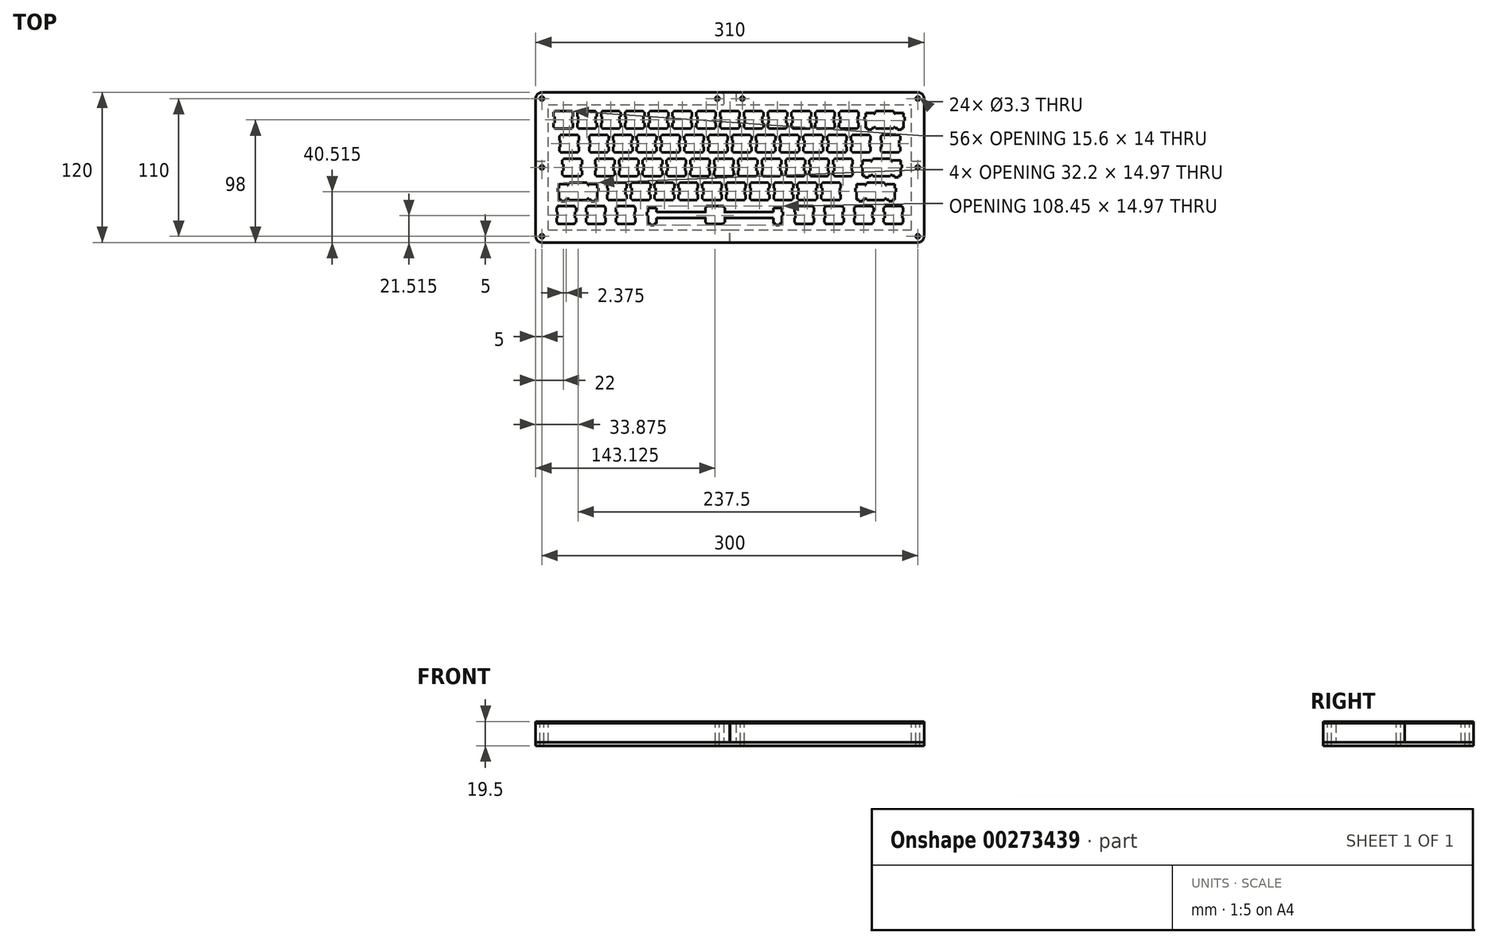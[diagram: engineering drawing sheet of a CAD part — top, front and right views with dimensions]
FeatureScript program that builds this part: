
annotation { "Feature Type Name" : "Feature", "Feature Type Description" : "" }
export const myFeature = defineFeature(function(context is Context, id is Id, definition is map)
    precondition{}
    {
        {
            var Q0;
            Q0=qCreatedBy(makeId("Top.planeOp"),FACE);
            var sketch = newSketch(context, id + "F0", { "sketchPlane" : qUnion([Q0])});
            skLineSegment(sketch, "E0", {"start": v(-145, -50) * mm, "end": v(145, -50) * mm});
            skLineSegment(sketch, "E1", {"start": v(145, -50) * mm, "end": v(145, 50) * mm});
            skLineSegment(sketch, "E2", {"start": v(145, 50) * mm, "end": v(-145, 50) * mm});
            skLineSegment(sketch, "E3", {"start": v(-145, 50) * mm, "end": v(-145, -50) * mm});
            skLineSegment(sketch, "E4", {"start": v(-126, 32) * mm, "end": v(-125.2, 32) * mm});
            skLineSegment(sketch, "E5", {"start": v(-125.2, 32) * mm, "end": v(-125.2, 35.5) * mm});
            skLineSegment(sketch, "E6", {"start": v(-125.2, 35.5) * mm, "end": v(-126, 35.5) * mm});
            skLineSegment(sketch, "E7", {"start": v(-126, 35.5) * mm, "end": v(-126, 40.5) * mm});
            skLineSegment(sketch, "E8", {"start": v(-126, 40.5) * mm, "end": v(-125.2, 40.5) * mm});
            skLineSegment(sketch, "E9", {"start": v(-125.2, 40.5) * mm, "end": v(-125.2, 44) * mm});
            skLineSegment(sketch, "E10", {"start": v(-125.2, 44) * mm, "end": v(-126, 44) * mm});
            skLineSegment(sketch, "E11", {"start": v(-126, 44) * mm, "end": v(-126, 45) * mm});
            skLineSegment(sketch, "E12", {"start": v(-126, 45) * mm, "end": v(-140, 45) * mm});
            skLineSegment(sketch, "E13", {"start": v(-140, 45) * mm, "end": v(-140, 44) * mm});
            skLineSegment(sketch, "E14", {"start": v(-140, 44) * mm, "end": v(-140.8, 44) * mm});
            skLineSegment(sketch, "E15", {"start": v(-140.8, 44) * mm, "end": v(-140.8, 40.5) * mm});
            skLineSegment(sketch, "E16", {"start": v(-140.8, 40.5) * mm, "end": v(-140, 40.5) * mm});
            skLineSegment(sketch, "E17", {"start": v(-140, 40.5) * mm, "end": v(-140, 35.5) * mm});
            skLineSegment(sketch, "E18", {"start": v(-140, 35.5) * mm, "end": v(-140.8, 35.5) * mm});
            skLineSegment(sketch, "E19", {"start": v(-140.8, 35.5) * mm, "end": v(-140.8, 32) * mm});
            skLineSegment(sketch, "E20", {"start": v(-140.8, 32) * mm, "end": v(-140, 32) * mm});
            skLineSegment(sketch, "E21", {"start": v(-140, 32) * mm, "end": v(-140, 31) * mm});
            skLineSegment(sketch, "E22", {"start": v(-140, 31) * mm, "end": v(-126, 31) * mm});
            skLineSegment(sketch, "E23", {"start": v(-126, 31) * mm, "end": v(-126, 32) * mm});
            skLineSegment(sketch, "E24", {"start": v(-107, 32) * mm, "end": v(-106.2, 32) * mm});
            skLineSegment(sketch, "E25", {"start": v(-106.2, 32) * mm, "end": v(-106.2, 35.5) * mm});
            skLineSegment(sketch, "E26", {"start": v(-106.2, 35.5) * mm, "end": v(-107, 35.5) * mm});
            skLineSegment(sketch, "E27", {"start": v(-107, 35.5) * mm, "end": v(-107, 40.5) * mm});
            skLineSegment(sketch, "E28", {"start": v(-107, 40.5) * mm, "end": v(-106.2, 40.5) * mm});
            skLineSegment(sketch, "E29", {"start": v(-106.2, 40.5) * mm, "end": v(-106.2, 44) * mm});
            skLineSegment(sketch, "E30", {"start": v(-106.2, 44) * mm, "end": v(-107, 44) * mm});
            skLineSegment(sketch, "E31", {"start": v(-107, 44) * mm, "end": v(-107, 45) * mm});
            skLineSegment(sketch, "E32", {"start": v(-107, 45) * mm, "end": v(-121, 45) * mm});
            skLineSegment(sketch, "E33", {"start": v(-121, 45) * mm, "end": v(-121, 44) * mm});
            skLineSegment(sketch, "E34", {"start": v(-121, 44) * mm, "end": v(-121.8, 44) * mm});
            skLineSegment(sketch, "E35", {"start": v(-121.8, 44) * mm, "end": v(-121.8, 40.5) * mm});
            skLineSegment(sketch, "E36", {"start": v(-121.8, 40.5) * mm, "end": v(-121, 40.5) * mm});
            skLineSegment(sketch, "E37", {"start": v(-121, 40.5) * mm, "end": v(-121, 35.5) * mm});
            skLineSegment(sketch, "E38", {"start": v(-121, 35.5) * mm, "end": v(-121.8, 35.5) * mm});
            skLineSegment(sketch, "E39", {"start": v(-121.8, 35.5) * mm, "end": v(-121.8, 32) * mm});
            skLineSegment(sketch, "E40", {"start": v(-121.8, 32) * mm, "end": v(-121, 32) * mm});
            skLineSegment(sketch, "E41", {"start": v(-121, 32) * mm, "end": v(-121, 31) * mm});
            skLineSegment(sketch, "E42", {"start": v(-121, 31) * mm, "end": v(-107, 31) * mm});
            skLineSegment(sketch, "E43", {"start": v(-107, 31) * mm, "end": v(-107, 32) * mm});
            skLineSegment(sketch, "E44", {"start": v(-88, 32) * mm, "end": v(-87.2, 32) * mm});
            skLineSegment(sketch, "E45", {"start": v(-87.2, 32) * mm, "end": v(-87.2, 35.5) * mm});
            skLineSegment(sketch, "E46", {"start": v(-87.2, 35.5) * mm, "end": v(-88, 35.5) * mm});
            skLineSegment(sketch, "E47", {"start": v(-88, 35.5) * mm, "end": v(-88, 40.5) * mm});
            skLineSegment(sketch, "E48", {"start": v(-88, 40.5) * mm, "end": v(-87.2, 40.5) * mm});
            skLineSegment(sketch, "E49", {"start": v(-87.2, 40.5) * mm, "end": v(-87.2, 44) * mm});
            skLineSegment(sketch, "E50", {"start": v(-87.2, 44) * mm, "end": v(-88, 44) * mm});
            skLineSegment(sketch, "E51", {"start": v(-88, 44) * mm, "end": v(-88, 45) * mm});
            skLineSegment(sketch, "E52", {"start": v(-88, 45) * mm, "end": v(-102, 45) * mm});
            skLineSegment(sketch, "E53", {"start": v(-102, 45) * mm, "end": v(-102, 44) * mm});
            skLineSegment(sketch, "E54", {"start": v(-102, 44) * mm, "end": v(-102.8, 44) * mm});
            skLineSegment(sketch, "E55", {"start": v(-102.8, 44) * mm, "end": v(-102.8, 40.5) * mm});
            skLineSegment(sketch, "E56", {"start": v(-102.8, 40.5) * mm, "end": v(-102, 40.5) * mm});
            skLineSegment(sketch, "E57", {"start": v(-102, 40.5) * mm, "end": v(-102, 35.5) * mm});
            skLineSegment(sketch, "E58", {"start": v(-102, 35.5) * mm, "end": v(-102.8, 35.5) * mm});
            skLineSegment(sketch, "E59", {"start": v(-102.8, 35.5) * mm, "end": v(-102.8, 32) * mm});
            skLineSegment(sketch, "E60", {"start": v(-102.8, 32) * mm, "end": v(-102, 32) * mm});
            skLineSegment(sketch, "E61", {"start": v(-102, 32) * mm, "end": v(-102, 31) * mm});
            skLineSegment(sketch, "E62", {"start": v(-102, 31) * mm, "end": v(-88, 31) * mm});
            skLineSegment(sketch, "E63", {"start": v(-88, 31) * mm, "end": v(-88, 32) * mm});
            skLineSegment(sketch, "E64", {"start": v(-69, 32) * mm, "end": v(-68.2, 32) * mm});
            skLineSegment(sketch, "E65", {"start": v(-68.2, 32) * mm, "end": v(-68.2, 35.5) * mm});
            skLineSegment(sketch, "E66", {"start": v(-68.2, 35.5) * mm, "end": v(-69, 35.5) * mm});
            skLineSegment(sketch, "E67", {"start": v(-69, 35.5) * mm, "end": v(-69, 40.5) * mm});
            skLineSegment(sketch, "E68", {"start": v(-69, 40.5) * mm, "end": v(-68.2, 40.5) * mm});
            skLineSegment(sketch, "E69", {"start": v(-68.2, 40.5) * mm, "end": v(-68.2, 44) * mm});
            skLineSegment(sketch, "E70", {"start": v(-68.2, 44) * mm, "end": v(-69, 44) * mm});
            skLineSegment(sketch, "E71", {"start": v(-69, 44) * mm, "end": v(-69, 45) * mm});
            skLineSegment(sketch, "E72", {"start": v(-69, 45) * mm, "end": v(-83, 45) * mm});
            skLineSegment(sketch, "E73", {"start": v(-83, 45) * mm, "end": v(-83, 44) * mm});
            skLineSegment(sketch, "E74", {"start": v(-83, 44) * mm, "end": v(-83.8, 44) * mm});
            skLineSegment(sketch, "E75", {"start": v(-83.8, 44) * mm, "end": v(-83.8, 40.5) * mm});
            skLineSegment(sketch, "E76", {"start": v(-83.8, 40.5) * mm, "end": v(-83, 40.5) * mm});
            skLineSegment(sketch, "E77", {"start": v(-83, 40.5) * mm, "end": v(-83, 35.5) * mm});
            skLineSegment(sketch, "E78", {"start": v(-83, 35.5) * mm, "end": v(-83.8, 35.5) * mm});
            skLineSegment(sketch, "E79", {"start": v(-83.8, 35.5) * mm, "end": v(-83.8, 32) * mm});
            skLineSegment(sketch, "E80", {"start": v(-83.8, 32) * mm, "end": v(-83, 32) * mm});
            skLineSegment(sketch, "E81", {"start": v(-83, 32) * mm, "end": v(-83, 31) * mm});
            skLineSegment(sketch, "E82", {"start": v(-83, 31) * mm, "end": v(-69, 31) * mm});
            skLineSegment(sketch, "E83", {"start": v(-69, 31) * mm, "end": v(-69, 32) * mm});
            skLineSegment(sketch, "E84", {"start": v(-50, 32) * mm, "end": v(-49.2, 32) * mm});
            skLineSegment(sketch, "E85", {"start": v(-49.2, 32) * mm, "end": v(-49.2, 35.5) * mm});
            skLineSegment(sketch, "E86", {"start": v(-49.2, 35.5) * mm, "end": v(-50, 35.5) * mm});
            skLineSegment(sketch, "E87", {"start": v(-50, 35.5) * mm, "end": v(-50, 40.5) * mm});
            skLineSegment(sketch, "E88", {"start": v(-50, 40.5) * mm, "end": v(-49.2, 40.5) * mm});
            skLineSegment(sketch, "E89", {"start": v(-49.2, 40.5) * mm, "end": v(-49.2, 44) * mm});
            skLineSegment(sketch, "E90", {"start": v(-49.2, 44) * mm, "end": v(-50, 44) * mm});
            skLineSegment(sketch, "E91", {"start": v(-50, 44) * mm, "end": v(-50, 45) * mm});
            skLineSegment(sketch, "E92", {"start": v(-50, 45) * mm, "end": v(-64, 45) * mm});
            skLineSegment(sketch, "E93", {"start": v(-64, 45) * mm, "end": v(-64, 44) * mm});
            skLineSegment(sketch, "E94", {"start": v(-64, 44) * mm, "end": v(-64.8, 44) * mm});
            skLineSegment(sketch, "E95", {"start": v(-64.8, 44) * mm, "end": v(-64.8, 40.5) * mm});
            skLineSegment(sketch, "E96", {"start": v(-64.8, 40.5) * mm, "end": v(-64, 40.5) * mm});
            skLineSegment(sketch, "E97", {"start": v(-64, 40.5) * mm, "end": v(-64, 35.5) * mm});
            skLineSegment(sketch, "E98", {"start": v(-64, 35.5) * mm, "end": v(-64.8, 35.5) * mm});
            skLineSegment(sketch, "E99", {"start": v(-64.8, 35.5) * mm, "end": v(-64.8, 32) * mm});
            skLineSegment(sketch, "E100", {"start": v(-64.8, 32) * mm, "end": v(-64, 32) * mm});
            skLineSegment(sketch, "E101", {"start": v(-64, 32) * mm, "end": v(-64, 31) * mm});
            skLineSegment(sketch, "E102", {"start": v(-64, 31) * mm, "end": v(-50, 31) * mm});
            skLineSegment(sketch, "E103", {"start": v(-50, 31) * mm, "end": v(-50, 32) * mm});
            skLineSegment(sketch, "E104", {"start": v(-31, 32) * mm, "end": v(-30.2, 32) * mm});
            skLineSegment(sketch, "E105", {"start": v(-30.2, 32) * mm, "end": v(-30.2, 35.5) * mm});
            skLineSegment(sketch, "E106", {"start": v(-30.2, 35.5) * mm, "end": v(-31, 35.5) * mm});
            skLineSegment(sketch, "E107", {"start": v(-31, 35.5) * mm, "end": v(-31, 40.5) * mm});
            skLineSegment(sketch, "E108", {"start": v(-31, 40.5) * mm, "end": v(-30.2, 40.5) * mm});
            skLineSegment(sketch, "E109", {"start": v(-30.2, 40.5) * mm, "end": v(-30.2, 44) * mm});
            skLineSegment(sketch, "E110", {"start": v(-30.2, 44) * mm, "end": v(-31, 44) * mm});
            skLineSegment(sketch, "E111", {"start": v(-31, 44) * mm, "end": v(-31, 45) * mm});
            skLineSegment(sketch, "E112", {"start": v(-31, 45) * mm, "end": v(-45, 45) * mm});
            skLineSegment(sketch, "E113", {"start": v(-45, 45) * mm, "end": v(-45, 44) * mm});
            skLineSegment(sketch, "E114", {"start": v(-45, 44) * mm, "end": v(-45.8, 44) * mm});
            skLineSegment(sketch, "E115", {"start": v(-45.8, 44) * mm, "end": v(-45.8, 40.5) * mm});
            skLineSegment(sketch, "E116", {"start": v(-45.8, 40.5) * mm, "end": v(-45, 40.5) * mm});
            skLineSegment(sketch, "E117", {"start": v(-45, 40.5) * mm, "end": v(-45, 35.5) * mm});
            skLineSegment(sketch, "E118", {"start": v(-45, 35.5) * mm, "end": v(-45.8, 35.5) * mm});
            skLineSegment(sketch, "E119", {"start": v(-45.8, 35.5) * mm, "end": v(-45.8, 32) * mm});
            skLineSegment(sketch, "E120", {"start": v(-45.8, 32) * mm, "end": v(-45, 32) * mm});
            skLineSegment(sketch, "E121", {"start": v(-45, 32) * mm, "end": v(-45, 31) * mm});
            skLineSegment(sketch, "E122", {"start": v(-45, 31) * mm, "end": v(-31, 31) * mm});
            skLineSegment(sketch, "E123", {"start": v(-31, 31) * mm, "end": v(-31, 32) * mm});
            skLineSegment(sketch, "E124", {"start": v(-12, 32) * mm, "end": v(-11.2, 32) * mm});
            skLineSegment(sketch, "E125", {"start": v(-11.2, 32) * mm, "end": v(-11.2, 35.5) * mm});
            skLineSegment(sketch, "E126", {"start": v(-11.2, 35.5) * mm, "end": v(-12, 35.5) * mm});
            skLineSegment(sketch, "E127", {"start": v(-12, 35.5) * mm, "end": v(-12, 40.5) * mm});
            skLineSegment(sketch, "E128", {"start": v(-12, 40.5) * mm, "end": v(-11.2, 40.5) * mm});
            skLineSegment(sketch, "E129", {"start": v(-11.2, 40.5) * mm, "end": v(-11.2, 44) * mm});
            skLineSegment(sketch, "E130", {"start": v(-11.2, 44) * mm, "end": v(-12, 44) * mm});
            skLineSegment(sketch, "E131", {"start": v(-12, 44) * mm, "end": v(-12, 45) * mm});
            skLineSegment(sketch, "E132", {"start": v(-12, 45) * mm, "end": v(-26, 45) * mm});
            skLineSegment(sketch, "E133", {"start": v(-26, 45) * mm, "end": v(-26, 44) * mm});
            skLineSegment(sketch, "E134", {"start": v(-26, 44) * mm, "end": v(-26.8, 44) * mm});
            skLineSegment(sketch, "E135", {"start": v(-26.8, 44) * mm, "end": v(-26.8, 40.5) * mm});
            skLineSegment(sketch, "E136", {"start": v(-26.8, 40.5) * mm, "end": v(-26, 40.5) * mm});
            skLineSegment(sketch, "E137", {"start": v(-26, 40.5) * mm, "end": v(-26, 35.5) * mm});
            skLineSegment(sketch, "E138", {"start": v(-26, 35.5) * mm, "end": v(-26.8, 35.5) * mm});
            skLineSegment(sketch, "E139", {"start": v(-26.8, 35.5) * mm, "end": v(-26.8, 32) * mm});
            skLineSegment(sketch, "E140", {"start": v(-26.8, 32) * mm, "end": v(-26, 32) * mm});
            skLineSegment(sketch, "E141", {"start": v(-26, 32) * mm, "end": v(-26, 31) * mm});
            skLineSegment(sketch, "E142", {"start": v(-26, 31) * mm, "end": v(-12, 31) * mm});
            skLineSegment(sketch, "E143", {"start": v(-12, 31) * mm, "end": v(-12, 32) * mm});
            skLineSegment(sketch, "E144", {"start": v(7, 32) * mm, "end": v(7.8, 32) * mm});
            skLineSegment(sketch, "E145", {"start": v(7.8, 32) * mm, "end": v(7.8, 35.5) * mm});
            skLineSegment(sketch, "E146", {"start": v(7.8, 35.5) * mm, "end": v(7, 35.5) * mm});
            skLineSegment(sketch, "E147", {"start": v(7, 35.5) * mm, "end": v(7, 40.5) * mm});
            skLineSegment(sketch, "E148", {"start": v(7, 40.5) * mm, "end": v(7.8, 40.5) * mm});
            skLineSegment(sketch, "E149", {"start": v(7.8, 40.5) * mm, "end": v(7.8, 44) * mm});
            skLineSegment(sketch, "E150", {"start": v(7.8, 44) * mm, "end": v(7, 44) * mm});
            skLineSegment(sketch, "E151", {"start": v(7, 44) * mm, "end": v(7, 45) * mm});
            skLineSegment(sketch, "E152", {"start": v(7, 45) * mm, "end": v(-7, 45) * mm});
            skLineSegment(sketch, "E153", {"start": v(-7, 45) * mm, "end": v(-7, 44) * mm});
            skLineSegment(sketch, "E154", {"start": v(-7, 44) * mm, "end": v(-7.8, 44) * mm});
            skLineSegment(sketch, "E155", {"start": v(-7.8, 44) * mm, "end": v(-7.8, 40.5) * mm});
            skLineSegment(sketch, "E156", {"start": v(-7.8, 40.5) * mm, "end": v(-7, 40.5) * mm});
            skLineSegment(sketch, "E157", {"start": v(-7, 40.5) * mm, "end": v(-7, 35.5) * mm});
            skLineSegment(sketch, "E158", {"start": v(-7, 35.5) * mm, "end": v(-7.8, 35.5) * mm});
            skLineSegment(sketch, "E159", {"start": v(-7.8, 35.5) * mm, "end": v(-7.8, 32) * mm});
            skLineSegment(sketch, "E160", {"start": v(-7.8, 32) * mm, "end": v(-7, 32) * mm});
            skLineSegment(sketch, "E161", {"start": v(-7, 32) * mm, "end": v(-7, 31) * mm});
            skLineSegment(sketch, "E162", {"start": v(-7, 31) * mm, "end": v(7, 31) * mm});
            skLineSegment(sketch, "E163", {"start": v(7, 31) * mm, "end": v(7, 32) * mm});
            skLineSegment(sketch, "E164", {"start": v(26, 32) * mm, "end": v(26.8, 32) * mm});
            skLineSegment(sketch, "E165", {"start": v(26.8, 32) * mm, "end": v(26.8, 35.5) * mm});
            skLineSegment(sketch, "E166", {"start": v(26.8, 35.5) * mm, "end": v(26, 35.5) * mm});
            skLineSegment(sketch, "E167", {"start": v(26, 35.5) * mm, "end": v(26, 40.5) * mm});
            skLineSegment(sketch, "E168", {"start": v(26, 40.5) * mm, "end": v(26.8, 40.5) * mm});
            skLineSegment(sketch, "E169", {"start": v(26.8, 40.5) * mm, "end": v(26.8, 44) * mm});
            skLineSegment(sketch, "E170", {"start": v(26.8, 44) * mm, "end": v(26, 44) * mm});
            skLineSegment(sketch, "E171", {"start": v(26, 44) * mm, "end": v(26, 45) * mm});
            skLineSegment(sketch, "E172", {"start": v(26, 45) * mm, "end": v(12, 45) * mm});
            skLineSegment(sketch, "E173", {"start": v(12, 45) * mm, "end": v(12, 44) * mm});
            skLineSegment(sketch, "E174", {"start": v(12, 44) * mm, "end": v(11.2, 44) * mm});
            skLineSegment(sketch, "E175", {"start": v(11.2, 44) * mm, "end": v(11.2, 40.5) * mm});
            skLineSegment(sketch, "E176", {"start": v(11.2, 40.5) * mm, "end": v(12, 40.5) * mm});
            skLineSegment(sketch, "E177", {"start": v(12, 40.5) * mm, "end": v(12, 35.5) * mm});
            skLineSegment(sketch, "E178", {"start": v(12, 35.5) * mm, "end": v(11.2, 35.5) * mm});
            skLineSegment(sketch, "E179", {"start": v(11.2, 35.5) * mm, "end": v(11.2, 32) * mm});
            skLineSegment(sketch, "E180", {"start": v(11.2, 32) * mm, "end": v(12, 32) * mm});
            skLineSegment(sketch, "E181", {"start": v(12, 32) * mm, "end": v(12, 31) * mm});
            skLineSegment(sketch, "E182", {"start": v(12, 31) * mm, "end": v(26, 31) * mm});
            skLineSegment(sketch, "E183", {"start": v(26, 31) * mm, "end": v(26, 32) * mm});
            skLineSegment(sketch, "E184", {"start": v(45, 32) * mm, "end": v(45.8, 32) * mm});
            skLineSegment(sketch, "E185", {"start": v(45.8, 32) * mm, "end": v(45.8, 35.5) * mm});
            skLineSegment(sketch, "E186", {"start": v(45.8, 35.5) * mm, "end": v(45, 35.5) * mm});
            skLineSegment(sketch, "E187", {"start": v(45, 35.5) * mm, "end": v(45, 40.5) * mm});
            skLineSegment(sketch, "E188", {"start": v(45, 40.5) * mm, "end": v(45.8, 40.5) * mm});
            skLineSegment(sketch, "E189", {"start": v(45.8, 40.5) * mm, "end": v(45.8, 44) * mm});
            skLineSegment(sketch, "E190", {"start": v(45.8, 44) * mm, "end": v(45, 44) * mm});
            skLineSegment(sketch, "E191", {"start": v(45, 44) * mm, "end": v(45, 45) * mm});
            skLineSegment(sketch, "E192", {"start": v(45, 45) * mm, "end": v(31, 45) * mm});
            skLineSegment(sketch, "E193", {"start": v(31, 45) * mm, "end": v(31, 44) * mm});
            skLineSegment(sketch, "E194", {"start": v(31, 44) * mm, "end": v(30.2, 44) * mm});
            skLineSegment(sketch, "E195", {"start": v(30.2, 44) * mm, "end": v(30.2, 40.5) * mm});
            skLineSegment(sketch, "E196", {"start": v(30.2, 40.5) * mm, "end": v(31, 40.5) * mm});
            skLineSegment(sketch, "E197", {"start": v(31, 40.5) * mm, "end": v(31, 35.5) * mm});
            skLineSegment(sketch, "E198", {"start": v(31, 35.5) * mm, "end": v(30.2, 35.5) * mm});
            skLineSegment(sketch, "E199", {"start": v(30.2, 35.5) * mm, "end": v(30.2, 32) * mm});
            skLineSegment(sketch, "E200", {"start": v(30.2, 32) * mm, "end": v(31, 32) * mm});
            skLineSegment(sketch, "E201", {"start": v(31, 32) * mm, "end": v(31, 31) * mm});
            skLineSegment(sketch, "E202", {"start": v(31, 31) * mm, "end": v(45, 31) * mm});
            skLineSegment(sketch, "E203", {"start": v(45, 31) * mm, "end": v(45, 32) * mm});
            skLineSegment(sketch, "E204", {"start": v(64, 32) * mm, "end": v(64.8, 32) * mm});
            skLineSegment(sketch, "E205", {"start": v(64.8, 32) * mm, "end": v(64.8, 35.5) * mm});
            skLineSegment(sketch, "E206", {"start": v(64.8, 35.5) * mm, "end": v(64, 35.5) * mm});
            skLineSegment(sketch, "E207", {"start": v(64, 35.5) * mm, "end": v(64, 40.5) * mm});
            skLineSegment(sketch, "E208", {"start": v(64, 40.5) * mm, "end": v(64.8, 40.5) * mm});
            skLineSegment(sketch, "E209", {"start": v(64.8, 40.5) * mm, "end": v(64.8, 44) * mm});
            skLineSegment(sketch, "E210", {"start": v(64.8, 44) * mm, "end": v(64, 44) * mm});
            skLineSegment(sketch, "E211", {"start": v(64, 44) * mm, "end": v(64, 45) * mm});
            skLineSegment(sketch, "E212", {"start": v(64, 45) * mm, "end": v(50, 45) * mm});
            skLineSegment(sketch, "E213", {"start": v(50, 45) * mm, "end": v(50, 44) * mm});
            skLineSegment(sketch, "E214", {"start": v(50, 44) * mm, "end": v(49.2, 44) * mm});
            skLineSegment(sketch, "E215", {"start": v(49.2, 44) * mm, "end": v(49.2, 40.5) * mm});
            skLineSegment(sketch, "E216", {"start": v(49.2, 40.5) * mm, "end": v(50, 40.5) * mm});
            skLineSegment(sketch, "E217", {"start": v(50, 40.5) * mm, "end": v(50, 35.5) * mm});
            skLineSegment(sketch, "E218", {"start": v(50, 35.5) * mm, "end": v(49.2, 35.5) * mm});
            skLineSegment(sketch, "E219", {"start": v(49.2, 35.5) * mm, "end": v(49.2, 32) * mm});
            skLineSegment(sketch, "E220", {"start": v(49.2, 32) * mm, "end": v(50, 32) * mm});
            skLineSegment(sketch, "E221", {"start": v(50, 32) * mm, "end": v(50, 31) * mm});
            skLineSegment(sketch, "E222", {"start": v(50, 31) * mm, "end": v(64, 31) * mm});
            skLineSegment(sketch, "E223", {"start": v(64, 31) * mm, "end": v(64, 32) * mm});
            skLineSegment(sketch, "E224", {"start": v(83, 32) * mm, "end": v(83.8, 32) * mm});
            skLineSegment(sketch, "E225", {"start": v(83.8, 32) * mm, "end": v(83.8, 35.5) * mm});
            skLineSegment(sketch, "E226", {"start": v(83.8, 35.5) * mm, "end": v(83, 35.5) * mm});
            skLineSegment(sketch, "E227", {"start": v(83, 35.5) * mm, "end": v(83, 40.5) * mm});
            skLineSegment(sketch, "E228", {"start": v(83, 40.5) * mm, "end": v(83.8, 40.5) * mm});
            skLineSegment(sketch, "E229", {"start": v(83.8, 40.5) * mm, "end": v(83.8, 44) * mm});
            skLineSegment(sketch, "E230", {"start": v(83.8, 44) * mm, "end": v(83, 44) * mm});
            skLineSegment(sketch, "E231", {"start": v(83, 44) * mm, "end": v(83, 45) * mm});
            skLineSegment(sketch, "E232", {"start": v(83, 45) * mm, "end": v(69, 45) * mm});
            skLineSegment(sketch, "E233", {"start": v(69, 45) * mm, "end": v(69, 44) * mm});
            skLineSegment(sketch, "E234", {"start": v(69, 44) * mm, "end": v(68.2, 44) * mm});
            skLineSegment(sketch, "E235", {"start": v(68.2, 44) * mm, "end": v(68.2, 40.5) * mm});
            skLineSegment(sketch, "E236", {"start": v(68.2, 40.5) * mm, "end": v(69, 40.5) * mm});
            skLineSegment(sketch, "E237", {"start": v(69, 40.5) * mm, "end": v(69, 35.5) * mm});
            skLineSegment(sketch, "E238", {"start": v(69, 35.5) * mm, "end": v(68.2, 35.5) * mm});
            skLineSegment(sketch, "E239", {"start": v(68.2, 35.5) * mm, "end": v(68.2, 32) * mm});
            skLineSegment(sketch, "E240", {"start": v(68.2, 32) * mm, "end": v(69, 32) * mm});
            skLineSegment(sketch, "E241", {"start": v(69, 32) * mm, "end": v(69, 31) * mm});
            skLineSegment(sketch, "E242", {"start": v(69, 31) * mm, "end": v(83, 31) * mm});
            skLineSegment(sketch, "E243", {"start": v(83, 31) * mm, "end": v(83, 32) * mm});
            skLineSegment(sketch, "E244", {"start": v(102, 32) * mm, "end": v(102.8, 32) * mm});
            skLineSegment(sketch, "E245", {"start": v(102.8, 32) * mm, "end": v(102.8, 35.5) * mm});
            skLineSegment(sketch, "E246", {"start": v(102.8, 35.5) * mm, "end": v(102, 35.5) * mm});
            skLineSegment(sketch, "E247", {"start": v(102, 35.5) * mm, "end": v(102, 40.5) * mm});
            skLineSegment(sketch, "E248", {"start": v(102, 40.5) * mm, "end": v(102.8, 40.5) * mm});
            skLineSegment(sketch, "E249", {"start": v(102.8, 40.5) * mm, "end": v(102.8, 44) * mm});
            skLineSegment(sketch, "E250", {"start": v(102.8, 44) * mm, "end": v(102, 44) * mm});
            skLineSegment(sketch, "E251", {"start": v(102, 44) * mm, "end": v(102, 45) * mm});
            skLineSegment(sketch, "E252", {"start": v(102, 45) * mm, "end": v(88, 45) * mm});
            skLineSegment(sketch, "E253", {"start": v(88, 45) * mm, "end": v(88, 44) * mm});
            skLineSegment(sketch, "E254", {"start": v(88, 44) * mm, "end": v(87.2, 44) * mm});
            skLineSegment(sketch, "E255", {"start": v(87.2, 44) * mm, "end": v(87.2, 40.5) * mm});
            skLineSegment(sketch, "E256", {"start": v(87.2, 40.5) * mm, "end": v(88, 40.5) * mm});
            skLineSegment(sketch, "E257", {"start": v(88, 40.5) * mm, "end": v(88, 35.5) * mm});
            skLineSegment(sketch, "E258", {"start": v(88, 35.5) * mm, "end": v(87.2, 35.5) * mm});
            skLineSegment(sketch, "E259", {"start": v(87.2, 35.5) * mm, "end": v(87.2, 32) * mm});
            skLineSegment(sketch, "E260", {"start": v(87.2, 32) * mm, "end": v(88, 32) * mm});
            skLineSegment(sketch, "E261", {"start": v(88, 32) * mm, "end": v(88, 31) * mm});
            skLineSegment(sketch, "E262", {"start": v(88, 31) * mm, "end": v(102, 31) * mm});
            skLineSegment(sketch, "E263", {"start": v(102, 31) * mm, "end": v(102, 32) * mm});
            skLineSegment(sketch, "E264", {"start": v(113.1, 31.23) * mm, "end": v(114.93, 31.23) * mm});
            skLineSegment(sketch, "E265", {"start": v(114.93, 31.23) * mm, "end": v(114.93, 32.03) * mm});
            skLineSegment(sketch, "E266", {"start": v(114.93, 32.03) * mm, "end": v(115.7, 32.03) * mm});
            skLineSegment(sketch, "E267", {"start": v(115.7, 32.03) * mm, "end": v(115.7, 32) * mm});
            skLineSegment(sketch, "E268", {"start": v(115.7, 32) * mm, "end": v(116.5, 32) * mm});
            skLineSegment(sketch, "E269", {"start": v(116.5, 32) * mm, "end": v(116.5, 31) * mm});
            skLineSegment(sketch, "E270", {"start": v(116.5, 31) * mm, "end": v(130.5, 31) * mm});
            skLineSegment(sketch, "E271", {"start": v(130.5, 31) * mm, "end": v(130.5, 32) * mm});
            skLineSegment(sketch, "E272", {"start": v(130.5, 32) * mm, "end": v(131.3, 32) * mm});
            skLineSegment(sketch, "E273", {"start": v(131.3, 32) * mm, "end": v(131.3, 32.03) * mm});
            skLineSegment(sketch, "E274", {"start": v(131.3, 32.03) * mm, "end": v(132.07, 32.03) * mm});
            skLineSegment(sketch, "E275", {"start": v(132.07, 32.03) * mm, "end": v(132.07, 31.23) * mm});
            skLineSegment(sketch, "E276", {"start": v(132.07, 31.23) * mm, "end": v(133.9, 31.23) * mm});
            skLineSegment(sketch, "E277", {"start": v(133.9, 31.23) * mm, "end": v(133.9, 30.03) * mm});
            skLineSegment(sketch, "E278", {"start": v(133.9, 30.03) * mm, "end": v(136.9, 30.03) * mm});
            skLineSegment(sketch, "E279", {"start": v(136.9, 30.03) * mm, "end": v(136.9, 31.23) * mm});
            skLineSegment(sketch, "E280", {"start": v(136.9, 31.23) * mm, "end": v(138.73, 31.23) * mm});
            skLineSegment(sketch, "E281", {"start": v(138.73, 31.23) * mm, "end": v(138.73, 37.5) * mm});
            skLineSegment(sketch, "E282", {"start": v(138.73, 37.5) * mm, "end": v(139.6, 37.5) * mm});
            skLineSegment(sketch, "E283", {"start": v(139.6, 37.5) * mm, "end": v(139.6, 40.3) * mm});
            skLineSegment(sketch, "E284", {"start": v(139.6, 40.3) * mm, "end": v(138.73, 40.3) * mm});
            skLineSegment(sketch, "E285", {"start": v(138.73, 40.3) * mm, "end": v(138.73, 43.53) * mm});
            skLineSegment(sketch, "E286", {"start": v(138.73, 43.53) * mm, "end": v(132.07, 43.53) * mm});
            skLineSegment(sketch, "E287", {"start": v(132.07, 43.53) * mm, "end": v(132.07, 42.73) * mm});
            skLineSegment(sketch, "E288", {"start": v(132.07, 42.73) * mm, "end": v(131.3, 42.73) * mm});
            skLineSegment(sketch, "E289", {"start": v(131.3, 42.73) * mm, "end": v(131.3, 44) * mm});
            skLineSegment(sketch, "E290", {"start": v(131.3, 44) * mm, "end": v(130.5, 44) * mm});
            skLineSegment(sketch, "E291", {"start": v(130.5, 44) * mm, "end": v(130.5, 45) * mm});
            skLineSegment(sketch, "E292", {"start": v(130.5, 45) * mm, "end": v(116.5, 45) * mm});
            skLineSegment(sketch, "E293", {"start": v(116.5, 45) * mm, "end": v(116.5, 44) * mm});
            skLineSegment(sketch, "E294", {"start": v(116.5, 44) * mm, "end": v(115.7, 44) * mm});
            skLineSegment(sketch, "E295", {"start": v(115.7, 44) * mm, "end": v(115.7, 42.73) * mm});
            skLineSegment(sketch, "E296", {"start": v(115.7, 42.73) * mm, "end": v(114.93, 42.73) * mm});
            skLineSegment(sketch, "E297", {"start": v(114.93, 42.73) * mm, "end": v(114.93, 43.53) * mm});
            skLineSegment(sketch, "E298", {"start": v(114.93, 43.53) * mm, "end": v(108.28, 43.53) * mm});
            skLineSegment(sketch, "E299", {"start": v(108.28, 43.53) * mm, "end": v(108.28, 40.3) * mm});
            skLineSegment(sketch, "E300", {"start": v(108.28, 40.3) * mm, "end": v(107.4, 40.3) * mm});
            skLineSegment(sketch, "E301", {"start": v(107.4, 40.3) * mm, "end": v(107.4, 37.5) * mm});
            skLineSegment(sketch, "E302", {"start": v(107.4, 37.5) * mm, "end": v(108.28, 37.5) * mm});
            skLineSegment(sketch, "E303", {"start": v(108.28, 37.5) * mm, "end": v(108.28, 31.23) * mm});
            skLineSegment(sketch, "E304", {"start": v(108.28, 31.23) * mm, "end": v(110.1, 31.23) * mm});
            skLineSegment(sketch, "E305", {"start": v(110.1, 31.23) * mm, "end": v(110.1, 30.03) * mm});
            skLineSegment(sketch, "E306", {"start": v(110.1, 30.03) * mm, "end": v(113.1, 30.03) * mm});
            skLineSegment(sketch, "E307", {"start": v(113.1, 30.03) * mm, "end": v(113.1, 31.23) * mm});
            skLineSegment(sketch, "E308", {"start": v(-121.25, 13) * mm, "end": v(-120.45, 13) * mm});
            skLineSegment(sketch, "E309", {"start": v(-120.45, 13) * mm, "end": v(-120.45, 16.5) * mm});
            skLineSegment(sketch, "E310", {"start": v(-120.45, 16.5) * mm, "end": v(-121.25, 16.5) * mm});
            skLineSegment(sketch, "E311", {"start": v(-121.25, 16.5) * mm, "end": v(-121.25, 21.5) * mm});
            skLineSegment(sketch, "E312", {"start": v(-121.25, 21.5) * mm, "end": v(-120.45, 21.5) * mm});
            skLineSegment(sketch, "E313", {"start": v(-120.45, 21.5) * mm, "end": v(-120.45, 25) * mm});
            skLineSegment(sketch, "E314", {"start": v(-120.45, 25) * mm, "end": v(-121.25, 25) * mm});
            skLineSegment(sketch, "E315", {"start": v(-121.25, 25) * mm, "end": v(-121.25, 26) * mm});
            skLineSegment(sketch, "E316", {"start": v(-121.25, 26) * mm, "end": v(-135.25, 26) * mm});
            skLineSegment(sketch, "E317", {"start": v(-135.25, 26) * mm, "end": v(-135.25, 25) * mm});
            skLineSegment(sketch, "E318", {"start": v(-135.25, 25) * mm, "end": v(-136.05, 25) * mm});
            skLineSegment(sketch, "E319", {"start": v(-136.05, 25) * mm, "end": v(-136.05, 21.5) * mm});
            skLineSegment(sketch, "E320", {"start": v(-136.05, 21.5) * mm, "end": v(-135.25, 21.5) * mm});
            skLineSegment(sketch, "E321", {"start": v(-135.25, 21.5) * mm, "end": v(-135.25, 16.5) * mm});
            skLineSegment(sketch, "E322", {"start": v(-135.25, 16.5) * mm, "end": v(-136.05, 16.5) * mm});
            skLineSegment(sketch, "E323", {"start": v(-136.05, 16.5) * mm, "end": v(-136.05, 13) * mm});
            skLineSegment(sketch, "E324", {"start": v(-136.05, 13) * mm, "end": v(-135.25, 13) * mm});
            skLineSegment(sketch, "E325", {"start": v(-135.25, 13) * mm, "end": v(-135.25, 12) * mm});
            skLineSegment(sketch, "E326", {"start": v(-135.25, 12) * mm, "end": v(-121.25, 12) * mm});
            skLineSegment(sketch, "E327", {"start": v(-121.25, 12) * mm, "end": v(-121.25, 13) * mm});
            skLineSegment(sketch, "E328", {"start": v(-97.5, 13) * mm, "end": v(-96.7, 13) * mm});
            skLineSegment(sketch, "E329", {"start": v(-96.7, 13) * mm, "end": v(-96.7, 16.5) * mm});
            skLineSegment(sketch, "E330", {"start": v(-96.7, 16.5) * mm, "end": v(-97.5, 16.5) * mm});
            skLineSegment(sketch, "E331", {"start": v(-97.5, 16.5) * mm, "end": v(-97.5, 21.5) * mm});
            skLineSegment(sketch, "E332", {"start": v(-97.5, 21.5) * mm, "end": v(-96.7, 21.5) * mm});
            skLineSegment(sketch, "E333", {"start": v(-96.7, 21.5) * mm, "end": v(-96.7, 25) * mm});
            skLineSegment(sketch, "E334", {"start": v(-96.7, 25) * mm, "end": v(-97.5, 25) * mm});
            skLineSegment(sketch, "E335", {"start": v(-97.5, 25) * mm, "end": v(-97.5, 26) * mm});
            skLineSegment(sketch, "E336", {"start": v(-97.5, 26) * mm, "end": v(-111.5, 26) * mm});
            skLineSegment(sketch, "E337", {"start": v(-111.5, 26) * mm, "end": v(-111.5, 25) * mm});
            skLineSegment(sketch, "E338", {"start": v(-111.5, 25) * mm, "end": v(-112.3, 25) * mm});
            skLineSegment(sketch, "E339", {"start": v(-112.3, 25) * mm, "end": v(-112.3, 21.5) * mm});
            skLineSegment(sketch, "E340", {"start": v(-112.3, 21.5) * mm, "end": v(-111.5, 21.5) * mm});
            skLineSegment(sketch, "E341", {"start": v(-111.5, 21.5) * mm, "end": v(-111.5, 16.5) * mm});
            skLineSegment(sketch, "E342", {"start": v(-111.5, 16.5) * mm, "end": v(-112.3, 16.5) * mm});
            skLineSegment(sketch, "E343", {"start": v(-112.3, 16.5) * mm, "end": v(-112.3, 13) * mm});
            skLineSegment(sketch, "E344", {"start": v(-112.3, 13) * mm, "end": v(-111.5, 13) * mm});
            skLineSegment(sketch, "E345", {"start": v(-111.5, 13) * mm, "end": v(-111.5, 12) * mm});
            skLineSegment(sketch, "E346", {"start": v(-111.5, 12) * mm, "end": v(-97.5, 12) * mm});
            skLineSegment(sketch, "E347", {"start": v(-97.5, 12) * mm, "end": v(-97.5, 13) * mm});
            skLineSegment(sketch, "E348", {"start": v(-78.5, 13) * mm, "end": v(-77.7, 13) * mm});
            skLineSegment(sketch, "E349", {"start": v(-77.7, 13) * mm, "end": v(-77.7, 16.5) * mm});
            skLineSegment(sketch, "E350", {"start": v(-77.7, 16.5) * mm, "end": v(-78.5, 16.5) * mm});
            skLineSegment(sketch, "E351", {"start": v(-78.5, 16.5) * mm, "end": v(-78.5, 21.5) * mm});
            skLineSegment(sketch, "E352", {"start": v(-78.5, 21.5) * mm, "end": v(-77.7, 21.5) * mm});
            skLineSegment(sketch, "E353", {"start": v(-77.7, 21.5) * mm, "end": v(-77.7, 25) * mm});
            skLineSegment(sketch, "E354", {"start": v(-77.7, 25) * mm, "end": v(-78.5, 25) * mm});
            skLineSegment(sketch, "E355", {"start": v(-78.5, 25) * mm, "end": v(-78.5, 26) * mm});
            skLineSegment(sketch, "E356", {"start": v(-78.5, 26) * mm, "end": v(-92.5, 26) * mm});
            skLineSegment(sketch, "E357", {"start": v(-92.5, 26) * mm, "end": v(-92.5, 25) * mm});
            skLineSegment(sketch, "E358", {"start": v(-92.5, 25) * mm, "end": v(-93.3, 25) * mm});
            skLineSegment(sketch, "E359", {"start": v(-93.3, 25) * mm, "end": v(-93.3, 21.5) * mm});
            skLineSegment(sketch, "E360", {"start": v(-93.3, 21.5) * mm, "end": v(-92.5, 21.5) * mm});
            skLineSegment(sketch, "E361", {"start": v(-92.5, 21.5) * mm, "end": v(-92.5, 16.5) * mm});
            skLineSegment(sketch, "E362", {"start": v(-92.5, 16.5) * mm, "end": v(-93.3, 16.5) * mm});
            skLineSegment(sketch, "E363", {"start": v(-93.3, 16.5) * mm, "end": v(-93.3, 13) * mm});
            skLineSegment(sketch, "E364", {"start": v(-93.3, 13) * mm, "end": v(-92.5, 13) * mm});
            skLineSegment(sketch, "E365", {"start": v(-92.5, 13) * mm, "end": v(-92.5, 12) * mm});
            skLineSegment(sketch, "E366", {"start": v(-92.5, 12) * mm, "end": v(-78.5, 12) * mm});
            skLineSegment(sketch, "E367", {"start": v(-78.5, 12) * mm, "end": v(-78.5, 13) * mm});
            skLineSegment(sketch, "E368", {"start": v(-59.5, 13) * mm, "end": v(-58.7, 13) * mm});
            skLineSegment(sketch, "E369", {"start": v(-58.7, 13) * mm, "end": v(-58.7, 16.5) * mm});
            skLineSegment(sketch, "E370", {"start": v(-58.7, 16.5) * mm, "end": v(-59.5, 16.5) * mm});
            skLineSegment(sketch, "E371", {"start": v(-59.5, 16.5) * mm, "end": v(-59.5, 21.5) * mm});
            skLineSegment(sketch, "E372", {"start": v(-59.5, 21.5) * mm, "end": v(-58.7, 21.5) * mm});
            skLineSegment(sketch, "E373", {"start": v(-58.7, 21.5) * mm, "end": v(-58.7, 25) * mm});
            skLineSegment(sketch, "E374", {"start": v(-58.7, 25) * mm, "end": v(-59.5, 25) * mm});
            skLineSegment(sketch, "E375", {"start": v(-59.5, 25) * mm, "end": v(-59.5, 26) * mm});
            skLineSegment(sketch, "E376", {"start": v(-59.5, 26) * mm, "end": v(-73.5, 26) * mm});
            skLineSegment(sketch, "E377", {"start": v(-73.5, 26) * mm, "end": v(-73.5, 25) * mm});
            skLineSegment(sketch, "E378", {"start": v(-73.5, 25) * mm, "end": v(-74.3, 25) * mm});
            skLineSegment(sketch, "E379", {"start": v(-74.3, 25) * mm, "end": v(-74.3, 21.5) * mm});
            skLineSegment(sketch, "E380", {"start": v(-74.3, 21.5) * mm, "end": v(-73.5, 21.5) * mm});
            skLineSegment(sketch, "E381", {"start": v(-73.5, 21.5) * mm, "end": v(-73.5, 16.5) * mm});
            skLineSegment(sketch, "E382", {"start": v(-73.5, 16.5) * mm, "end": v(-74.3, 16.5) * mm});
            skLineSegment(sketch, "E383", {"start": v(-74.3, 16.5) * mm, "end": v(-74.3, 13) * mm});
            skLineSegment(sketch, "E384", {"start": v(-74.3, 13) * mm, "end": v(-73.5, 13) * mm});
            skLineSegment(sketch, "E385", {"start": v(-73.5, 13) * mm, "end": v(-73.5, 12) * mm});
            skLineSegment(sketch, "E386", {"start": v(-73.5, 12) * mm, "end": v(-59.5, 12) * mm});
            skLineSegment(sketch, "E387", {"start": v(-59.5, 12) * mm, "end": v(-59.5, 13) * mm});
            skLineSegment(sketch, "E388", {"start": v(-40.5, 13) * mm, "end": v(-39.7, 13) * mm});
            skLineSegment(sketch, "E389", {"start": v(-39.7, 13) * mm, "end": v(-39.7, 16.5) * mm});
            skLineSegment(sketch, "E390", {"start": v(-39.7, 16.5) * mm, "end": v(-40.5, 16.5) * mm});
            skLineSegment(sketch, "E391", {"start": v(-40.5, 16.5) * mm, "end": v(-40.5, 21.5) * mm});
            skLineSegment(sketch, "E392", {"start": v(-40.5, 21.5) * mm, "end": v(-39.7, 21.5) * mm});
            skLineSegment(sketch, "E393", {"start": v(-39.7, 21.5) * mm, "end": v(-39.7, 25) * mm});
            skLineSegment(sketch, "E394", {"start": v(-39.7, 25) * mm, "end": v(-40.5, 25) * mm});
            skLineSegment(sketch, "E395", {"start": v(-40.5, 25) * mm, "end": v(-40.5, 26) * mm});
            skLineSegment(sketch, "E396", {"start": v(-40.5, 26) * mm, "end": v(-54.5, 26) * mm});
            skLineSegment(sketch, "E397", {"start": v(-54.5, 26) * mm, "end": v(-54.5, 25) * mm});
            skLineSegment(sketch, "E398", {"start": v(-54.5, 25) * mm, "end": v(-55.3, 25) * mm});
            skLineSegment(sketch, "E399", {"start": v(-55.3, 25) * mm, "end": v(-55.3, 21.5) * mm});
            skLineSegment(sketch, "E400", {"start": v(-55.3, 21.5) * mm, "end": v(-54.5, 21.5) * mm});
            skLineSegment(sketch, "E401", {"start": v(-54.5, 21.5) * mm, "end": v(-54.5, 16.5) * mm});
            skLineSegment(sketch, "E402", {"start": v(-54.5, 16.5) * mm, "end": v(-55.3, 16.5) * mm});
            skLineSegment(sketch, "E403", {"start": v(-55.3, 16.5) * mm, "end": v(-55.3, 13) * mm});
            skLineSegment(sketch, "E404", {"start": v(-55.3, 13) * mm, "end": v(-54.5, 13) * mm});
            skLineSegment(sketch, "E405", {"start": v(-54.5, 13) * mm, "end": v(-54.5, 12) * mm});
            skLineSegment(sketch, "E406", {"start": v(-54.5, 12) * mm, "end": v(-40.5, 12) * mm});
            skLineSegment(sketch, "E407", {"start": v(-40.5, 12) * mm, "end": v(-40.5, 13) * mm});
            skLineSegment(sketch, "E408", {"start": v(-21.5, 13) * mm, "end": v(-20.7, 13) * mm});
            skLineSegment(sketch, "E409", {"start": v(-20.7, 13) * mm, "end": v(-20.7, 16.5) * mm});
            skLineSegment(sketch, "E410", {"start": v(-20.7, 16.5) * mm, "end": v(-21.5, 16.5) * mm});
            skLineSegment(sketch, "E411", {"start": v(-21.5, 16.5) * mm, "end": v(-21.5, 21.5) * mm});
            skLineSegment(sketch, "E412", {"start": v(-21.5, 21.5) * mm, "end": v(-20.7, 21.5) * mm});
            skLineSegment(sketch, "E413", {"start": v(-20.7, 21.5) * mm, "end": v(-20.7, 25) * mm});
            skLineSegment(sketch, "E414", {"start": v(-20.7, 25) * mm, "end": v(-21.5, 25) * mm});
            skLineSegment(sketch, "E415", {"start": v(-21.5, 25) * mm, "end": v(-21.5, 26) * mm});
            skLineSegment(sketch, "E416", {"start": v(-21.5, 26) * mm, "end": v(-35.5, 26) * mm});
            skLineSegment(sketch, "E417", {"start": v(-35.5, 26) * mm, "end": v(-35.5, 25) * mm});
            skLineSegment(sketch, "E418", {"start": v(-35.5, 25) * mm, "end": v(-36.3, 25) * mm});
            skLineSegment(sketch, "E419", {"start": v(-36.3, 25) * mm, "end": v(-36.3, 21.5) * mm});
            skLineSegment(sketch, "E420", {"start": v(-36.3, 21.5) * mm, "end": v(-35.5, 21.5) * mm});
            skLineSegment(sketch, "E421", {"start": v(-35.5, 21.5) * mm, "end": v(-35.5, 16.5) * mm});
            skLineSegment(sketch, "E422", {"start": v(-35.5, 16.5) * mm, "end": v(-36.3, 16.5) * mm});
            skLineSegment(sketch, "E423", {"start": v(-36.3, 16.5) * mm, "end": v(-36.3, 13) * mm});
            skLineSegment(sketch, "E424", {"start": v(-36.3, 13) * mm, "end": v(-35.5, 13) * mm});
            skLineSegment(sketch, "E425", {"start": v(-35.5, 13) * mm, "end": v(-35.5, 12) * mm});
            skLineSegment(sketch, "E426", {"start": v(-35.5, 12) * mm, "end": v(-21.5, 12) * mm});
            skLineSegment(sketch, "E427", {"start": v(-21.5, 12) * mm, "end": v(-21.5, 13) * mm});
            skLineSegment(sketch, "E428", {"start": v(-2.5, 13) * mm, "end": v(-1.7, 13) * mm});
            skLineSegment(sketch, "E429", {"start": v(-1.7, 13) * mm, "end": v(-1.7, 16.5) * mm});
            skLineSegment(sketch, "E430", {"start": v(-1.7, 16.5) * mm, "end": v(-2.5, 16.5) * mm});
            skLineSegment(sketch, "E431", {"start": v(-2.5, 16.5) * mm, "end": v(-2.5, 21.5) * mm});
            skLineSegment(sketch, "E432", {"start": v(-2.5, 21.5) * mm, "end": v(-1.7, 21.5) * mm});
            skLineSegment(sketch, "E433", {"start": v(-1.7, 21.5) * mm, "end": v(-1.7, 25) * mm});
            skLineSegment(sketch, "E434", {"start": v(-1.7, 25) * mm, "end": v(-2.5, 25) * mm});
            skLineSegment(sketch, "E435", {"start": v(-2.5, 25) * mm, "end": v(-2.5, 26) * mm});
            skLineSegment(sketch, "E436", {"start": v(-2.5, 26) * mm, "end": v(-16.5, 26) * mm});
            skLineSegment(sketch, "E437", {"start": v(-16.5, 26) * mm, "end": v(-16.5, 25) * mm});
            skLineSegment(sketch, "E438", {"start": v(-16.5, 25) * mm, "end": v(-17.3, 25) * mm});
            skLineSegment(sketch, "E439", {"start": v(-17.3, 25) * mm, "end": v(-17.3, 21.5) * mm});
            skLineSegment(sketch, "E440", {"start": v(-17.3, 21.5) * mm, "end": v(-16.5, 21.5) * mm});
            skLineSegment(sketch, "E441", {"start": v(-16.5, 21.5) * mm, "end": v(-16.5, 16.5) * mm});
            skLineSegment(sketch, "E442", {"start": v(-16.5, 16.5) * mm, "end": v(-17.3, 16.5) * mm});
            skLineSegment(sketch, "E443", {"start": v(-17.3, 16.5) * mm, "end": v(-17.3, 13) * mm});
            skLineSegment(sketch, "E444", {"start": v(-17.3, 13) * mm, "end": v(-16.5, 13) * mm});
            skLineSegment(sketch, "E445", {"start": v(-16.5, 13) * mm, "end": v(-16.5, 12) * mm});
            skLineSegment(sketch, "E446", {"start": v(-16.5, 12) * mm, "end": v(-2.5, 12) * mm});
            skLineSegment(sketch, "E447", {"start": v(-2.5, 12) * mm, "end": v(-2.5, 13) * mm});
            skLineSegment(sketch, "E448", {"start": v(16.5, 13) * mm, "end": v(17.3, 13) * mm});
            skLineSegment(sketch, "E449", {"start": v(17.3, 13) * mm, "end": v(17.3, 16.5) * mm});
            skLineSegment(sketch, "E450", {"start": v(17.3, 16.5) * mm, "end": v(16.5, 16.5) * mm});
            skLineSegment(sketch, "E451", {"start": v(16.5, 16.5) * mm, "end": v(16.5, 21.5) * mm});
            skLineSegment(sketch, "E452", {"start": v(16.5, 21.5) * mm, "end": v(17.3, 21.5) * mm});
            skLineSegment(sketch, "E453", {"start": v(17.3, 21.5) * mm, "end": v(17.3, 25) * mm});
            skLineSegment(sketch, "E454", {"start": v(17.3, 25) * mm, "end": v(16.5, 25) * mm});
            skLineSegment(sketch, "E455", {"start": v(16.5, 25) * mm, "end": v(16.5, 26) * mm});
            skLineSegment(sketch, "E456", {"start": v(16.5, 26) * mm, "end": v(2.5, 26) * mm});
            skLineSegment(sketch, "E457", {"start": v(2.5, 26) * mm, "end": v(2.5, 25) * mm});
            skLineSegment(sketch, "E458", {"start": v(2.5, 25) * mm, "end": v(1.7, 25) * mm});
            skLineSegment(sketch, "E459", {"start": v(1.7, 25) * mm, "end": v(1.7, 21.5) * mm});
            skLineSegment(sketch, "E460", {"start": v(1.7, 21.5) * mm, "end": v(2.5, 21.5) * mm});
            skLineSegment(sketch, "E461", {"start": v(2.5, 21.5) * mm, "end": v(2.5, 16.5) * mm});
            skLineSegment(sketch, "E462", {"start": v(2.5, 16.5) * mm, "end": v(1.7, 16.5) * mm});
            skLineSegment(sketch, "E463", {"start": v(1.7, 16.5) * mm, "end": v(1.7, 13) * mm});
            skLineSegment(sketch, "E464", {"start": v(1.7, 13) * mm, "end": v(2.5, 13) * mm});
            skLineSegment(sketch, "E465", {"start": v(2.5, 13) * mm, "end": v(2.5, 12) * mm});
            skLineSegment(sketch, "E466", {"start": v(2.5, 12) * mm, "end": v(16.5, 12) * mm});
            skLineSegment(sketch, "E467", {"start": v(16.5, 12) * mm, "end": v(16.5, 13) * mm});
            skLineSegment(sketch, "E468", {"start": v(35.5, 13) * mm, "end": v(36.3, 13) * mm});
            skLineSegment(sketch, "E469", {"start": v(36.3, 13) * mm, "end": v(36.3, 16.5) * mm});
            skLineSegment(sketch, "E470", {"start": v(36.3, 16.5) * mm, "end": v(35.5, 16.5) * mm});
            skLineSegment(sketch, "E471", {"start": v(35.5, 16.5) * mm, "end": v(35.5, 21.5) * mm});
            skLineSegment(sketch, "E472", {"start": v(35.5, 21.5) * mm, "end": v(36.3, 21.5) * mm});
            skLineSegment(sketch, "E473", {"start": v(36.3, 21.5) * mm, "end": v(36.3, 25) * mm});
            skLineSegment(sketch, "E474", {"start": v(36.3, 25) * mm, "end": v(35.5, 25) * mm});
            skLineSegment(sketch, "E475", {"start": v(35.5, 25) * mm, "end": v(35.5, 26) * mm});
            skLineSegment(sketch, "E476", {"start": v(35.5, 26) * mm, "end": v(21.5, 26) * mm});
            skLineSegment(sketch, "E477", {"start": v(21.5, 26) * mm, "end": v(21.5, 25) * mm});
            skLineSegment(sketch, "E478", {"start": v(21.5, 25) * mm, "end": v(20.7, 25) * mm});
            skLineSegment(sketch, "E479", {"start": v(20.7, 25) * mm, "end": v(20.7, 21.5) * mm});
            skLineSegment(sketch, "E480", {"start": v(20.7, 21.5) * mm, "end": v(21.5, 21.5) * mm});
            skLineSegment(sketch, "E481", {"start": v(21.5, 21.5) * mm, "end": v(21.5, 16.5) * mm});
            skLineSegment(sketch, "E482", {"start": v(21.5, 16.5) * mm, "end": v(20.7, 16.5) * mm});
            skLineSegment(sketch, "E483", {"start": v(20.7, 16.5) * mm, "end": v(20.7, 13) * mm});
            skLineSegment(sketch, "E484", {"start": v(20.7, 13) * mm, "end": v(21.5, 13) * mm});
            skLineSegment(sketch, "E485", {"start": v(21.5, 13) * mm, "end": v(21.5, 12) * mm});
            skLineSegment(sketch, "E486", {"start": v(21.5, 12) * mm, "end": v(35.5, 12) * mm});
            skLineSegment(sketch, "E487", {"start": v(35.5, 12) * mm, "end": v(35.5, 13) * mm});
            skLineSegment(sketch, "E488", {"start": v(54.5, 13) * mm, "end": v(55.3, 13) * mm});
            skLineSegment(sketch, "E489", {"start": v(55.3, 13) * mm, "end": v(55.3, 16.5) * mm});
            skLineSegment(sketch, "E490", {"start": v(55.3, 16.5) * mm, "end": v(54.5, 16.5) * mm});
            skLineSegment(sketch, "E491", {"start": v(54.5, 16.5) * mm, "end": v(54.5, 21.5) * mm});
            skLineSegment(sketch, "E492", {"start": v(54.5, 21.5) * mm, "end": v(55.3, 21.5) * mm});
            skLineSegment(sketch, "E493", {"start": v(55.3, 21.5) * mm, "end": v(55.3, 25) * mm});
            skLineSegment(sketch, "E494", {"start": v(55.3, 25) * mm, "end": v(54.5, 25) * mm});
            skLineSegment(sketch, "E495", {"start": v(54.5, 25) * mm, "end": v(54.5, 26) * mm});
            skLineSegment(sketch, "E496", {"start": v(54.5, 26) * mm, "end": v(40.5, 26) * mm});
            skLineSegment(sketch, "E497", {"start": v(40.5, 26) * mm, "end": v(40.5, 25) * mm});
            skLineSegment(sketch, "E498", {"start": v(40.5, 25) * mm, "end": v(39.7, 25) * mm});
            skLineSegment(sketch, "E499", {"start": v(39.7, 25) * mm, "end": v(39.7, 21.5) * mm});
            skLineSegment(sketch, "E500", {"start": v(39.7, 21.5) * mm, "end": v(40.5, 21.5) * mm});
            skLineSegment(sketch, "E501", {"start": v(40.5, 21.5) * mm, "end": v(40.5, 16.5) * mm});
            skLineSegment(sketch, "E502", {"start": v(40.5, 16.5) * mm, "end": v(39.7, 16.5) * mm});
            skLineSegment(sketch, "E503", {"start": v(39.7, 16.5) * mm, "end": v(39.7, 13) * mm});
            skLineSegment(sketch, "E504", {"start": v(39.7, 13) * mm, "end": v(40.5, 13) * mm});
            skLineSegment(sketch, "E505", {"start": v(40.5, 13) * mm, "end": v(40.5, 12) * mm});
            skLineSegment(sketch, "E506", {"start": v(40.5, 12) * mm, "end": v(54.5, 12) * mm});
            skLineSegment(sketch, "E507", {"start": v(54.5, 12) * mm, "end": v(54.5, 13) * mm});
            skLineSegment(sketch, "E508", {"start": v(73.5, 13) * mm, "end": v(74.3, 13) * mm});
            skLineSegment(sketch, "E509", {"start": v(74.3, 13) * mm, "end": v(74.3, 16.5) * mm});
            skLineSegment(sketch, "E510", {"start": v(74.3, 16.5) * mm, "end": v(73.5, 16.5) * mm});
            skLineSegment(sketch, "E511", {"start": v(73.5, 16.5) * mm, "end": v(73.5, 21.5) * mm});
            skLineSegment(sketch, "E512", {"start": v(73.5, 21.5) * mm, "end": v(74.3, 21.5) * mm});
            skLineSegment(sketch, "E513", {"start": v(74.3, 21.5) * mm, "end": v(74.3, 25) * mm});
            skLineSegment(sketch, "E514", {"start": v(74.3, 25) * mm, "end": v(73.5, 25) * mm});
            skLineSegment(sketch, "E515", {"start": v(73.5, 25) * mm, "end": v(73.5, 26) * mm});
            skLineSegment(sketch, "E516", {"start": v(73.5, 26) * mm, "end": v(59.5, 26) * mm});
            skLineSegment(sketch, "E517", {"start": v(59.5, 26) * mm, "end": v(59.5, 25) * mm});
            skLineSegment(sketch, "E518", {"start": v(59.5, 25) * mm, "end": v(58.7, 25) * mm});
            skLineSegment(sketch, "E519", {"start": v(58.7, 25) * mm, "end": v(58.7, 21.5) * mm});
            skLineSegment(sketch, "E520", {"start": v(58.7, 21.5) * mm, "end": v(59.5, 21.5) * mm});
            skLineSegment(sketch, "E521", {"start": v(59.5, 21.5) * mm, "end": v(59.5, 16.5) * mm});
            skLineSegment(sketch, "E522", {"start": v(59.5, 16.5) * mm, "end": v(58.7, 16.5) * mm});
            skLineSegment(sketch, "E523", {"start": v(58.7, 16.5) * mm, "end": v(58.7, 13) * mm});
            skLineSegment(sketch, "E524", {"start": v(58.7, 13) * mm, "end": v(59.5, 13) * mm});
            skLineSegment(sketch, "E525", {"start": v(59.5, 13) * mm, "end": v(59.5, 12) * mm});
            skLineSegment(sketch, "E526", {"start": v(59.5, 12) * mm, "end": v(73.5, 12) * mm});
            skLineSegment(sketch, "E527", {"start": v(73.5, 12) * mm, "end": v(73.5, 13) * mm});
            skLineSegment(sketch, "E528", {"start": v(92.5, 13) * mm, "end": v(93.3, 13) * mm});
            skLineSegment(sketch, "E529", {"start": v(93.3, 13) * mm, "end": v(93.3, 16.5) * mm});
            skLineSegment(sketch, "E530", {"start": v(93.3, 16.5) * mm, "end": v(92.5, 16.5) * mm});
            skLineSegment(sketch, "E531", {"start": v(92.5, 16.5) * mm, "end": v(92.5, 21.5) * mm});
            skLineSegment(sketch, "E532", {"start": v(92.5, 21.5) * mm, "end": v(93.3, 21.5) * mm});
            skLineSegment(sketch, "E533", {"start": v(93.3, 21.5) * mm, "end": v(93.3, 25) * mm});
            skLineSegment(sketch, "E534", {"start": v(93.3, 25) * mm, "end": v(92.5, 25) * mm});
            skLineSegment(sketch, "E535", {"start": v(92.5, 25) * mm, "end": v(92.5, 26) * mm});
            skLineSegment(sketch, "E536", {"start": v(92.5, 26) * mm, "end": v(78.5, 26) * mm});
            skLineSegment(sketch, "E537", {"start": v(78.5, 26) * mm, "end": v(78.5, 25) * mm});
            skLineSegment(sketch, "E538", {"start": v(78.5, 25) * mm, "end": v(77.7, 25) * mm});
            skLineSegment(sketch, "E539", {"start": v(77.7, 25) * mm, "end": v(77.7, 21.5) * mm});
            skLineSegment(sketch, "E540", {"start": v(77.7, 21.5) * mm, "end": v(78.5, 21.5) * mm});
            skLineSegment(sketch, "E541", {"start": v(78.5, 21.5) * mm, "end": v(78.5, 16.5) * mm});
            skLineSegment(sketch, "E542", {"start": v(78.5, 16.5) * mm, "end": v(77.7, 16.5) * mm});
            skLineSegment(sketch, "E543", {"start": v(77.7, 16.5) * mm, "end": v(77.7, 13) * mm});
            skLineSegment(sketch, "E544", {"start": v(77.7, 13) * mm, "end": v(78.5, 13) * mm});
            skLineSegment(sketch, "E545", {"start": v(78.5, 13) * mm, "end": v(78.5, 12) * mm});
            skLineSegment(sketch, "E546", {"start": v(78.5, 12) * mm, "end": v(92.5, 12) * mm});
            skLineSegment(sketch, "E547", {"start": v(92.5, 12) * mm, "end": v(92.5, 13) * mm});
            skLineSegment(sketch, "E548", {"start": v(111.5, 13) * mm, "end": v(112.3, 13) * mm});
            skLineSegment(sketch, "E549", {"start": v(112.3, 13) * mm, "end": v(112.3, 16.5) * mm});
            skLineSegment(sketch, "E550", {"start": v(112.3, 16.5) * mm, "end": v(111.5, 16.5) * mm});
            skLineSegment(sketch, "E551", {"start": v(111.5, 16.5) * mm, "end": v(111.5, 21.5) * mm});
            skLineSegment(sketch, "E552", {"start": v(111.5, 21.5) * mm, "end": v(112.3, 21.5) * mm});
            skLineSegment(sketch, "E553", {"start": v(112.3, 21.5) * mm, "end": v(112.3, 25) * mm});
            skLineSegment(sketch, "E554", {"start": v(112.3, 25) * mm, "end": v(111.5, 25) * mm});
            skLineSegment(sketch, "E555", {"start": v(111.5, 25) * mm, "end": v(111.5, 26) * mm});
            skLineSegment(sketch, "E556", {"start": v(111.5, 26) * mm, "end": v(97.5, 26) * mm});
            skLineSegment(sketch, "E557", {"start": v(97.5, 26) * mm, "end": v(97.5, 25) * mm});
            skLineSegment(sketch, "E558", {"start": v(97.5, 25) * mm, "end": v(96.7, 25) * mm});
            skLineSegment(sketch, "E559", {"start": v(96.7, 25) * mm, "end": v(96.7, 21.5) * mm});
            skLineSegment(sketch, "E560", {"start": v(96.7, 21.5) * mm, "end": v(97.5, 21.5) * mm});
            skLineSegment(sketch, "E561", {"start": v(97.5, 21.5) * mm, "end": v(97.5, 16.5) * mm});
            skLineSegment(sketch, "E562", {"start": v(97.5, 16.5) * mm, "end": v(96.7, 16.5) * mm});
            skLineSegment(sketch, "E563", {"start": v(96.7, 16.5) * mm, "end": v(96.7, 13) * mm});
            skLineSegment(sketch, "E564", {"start": v(96.7, 13) * mm, "end": v(97.5, 13) * mm});
            skLineSegment(sketch, "E565", {"start": v(97.5, 13) * mm, "end": v(97.5, 12) * mm});
            skLineSegment(sketch, "E566", {"start": v(97.5, 12) * mm, "end": v(111.5, 12) * mm});
            skLineSegment(sketch, "E567", {"start": v(111.5, 12) * mm, "end": v(111.5, 13) * mm});
            skLineSegment(sketch, "E568", {"start": v(135.25, 13) * mm, "end": v(136.05, 13) * mm});
            skLineSegment(sketch, "E569", {"start": v(136.05, 13) * mm, "end": v(136.05, 16.5) * mm});
            skLineSegment(sketch, "E570", {"start": v(136.05, 16.5) * mm, "end": v(135.25, 16.5) * mm});
            skLineSegment(sketch, "E571", {"start": v(135.25, 16.5) * mm, "end": v(135.25, 21.5) * mm});
            skLineSegment(sketch, "E572", {"start": v(135.25, 21.5) * mm, "end": v(136.05, 21.5) * mm});
            skLineSegment(sketch, "E573", {"start": v(136.05, 21.5) * mm, "end": v(136.05, 25) * mm});
            skLineSegment(sketch, "E574", {"start": v(136.05, 25) * mm, "end": v(135.25, 25) * mm});
            skLineSegment(sketch, "E575", {"start": v(135.25, 25) * mm, "end": v(135.25, 26) * mm});
            skLineSegment(sketch, "E576", {"start": v(135.25, 26) * mm, "end": v(121.25, 26) * mm});
            skLineSegment(sketch, "E577", {"start": v(121.25, 26) * mm, "end": v(121.25, 25) * mm});
            skLineSegment(sketch, "E578", {"start": v(121.25, 25) * mm, "end": v(120.45, 25) * mm});
            skLineSegment(sketch, "E579", {"start": v(120.45, 25) * mm, "end": v(120.45, 21.5) * mm});
            skLineSegment(sketch, "E580", {"start": v(120.45, 21.5) * mm, "end": v(121.25, 21.5) * mm});
            skLineSegment(sketch, "E581", {"start": v(121.25, 21.5) * mm, "end": v(121.25, 16.5) * mm});
            skLineSegment(sketch, "E582", {"start": v(121.25, 16.5) * mm, "end": v(120.45, 16.5) * mm});
            skLineSegment(sketch, "E583", {"start": v(120.45, 16.5) * mm, "end": v(120.45, 13) * mm});
            skLineSegment(sketch, "E584", {"start": v(120.45, 13) * mm, "end": v(121.25, 13) * mm});
            skLineSegment(sketch, "E585", {"start": v(121.25, 13) * mm, "end": v(121.25, 12) * mm});
            skLineSegment(sketch, "E586", {"start": v(121.25, 12) * mm, "end": v(135.25, 12) * mm});
            skLineSegment(sketch, "E587", {"start": v(135.25, 12) * mm, "end": v(135.25, 13) * mm});
            skLineSegment(sketch, "E588", {"start": v(-118.88, -6) * mm, "end": v(-118.08, -6) * mm});
            skLineSegment(sketch, "E589", {"start": v(-118.08, -6) * mm, "end": v(-118.08, -2.5) * mm});
            skLineSegment(sketch, "E590", {"start": v(-118.08, -2.5) * mm, "end": v(-118.88, -2.5) * mm});
            skLineSegment(sketch, "E591", {"start": v(-118.88, -2.5) * mm, "end": v(-118.88, 2.5) * mm});
            skLineSegment(sketch, "E592", {"start": v(-118.88, 2.5) * mm, "end": v(-118.08, 2.5) * mm});
            skLineSegment(sketch, "E593", {"start": v(-118.08, 2.5) * mm, "end": v(-118.08, 6) * mm});
            skLineSegment(sketch, "E594", {"start": v(-118.08, 6) * mm, "end": v(-118.88, 6) * mm});
            skLineSegment(sketch, "E595", {"start": v(-118.88, 6) * mm, "end": v(-118.88, 7) * mm});
            skLineSegment(sketch, "E596", {"start": v(-118.88, 7) * mm, "end": v(-132.88, 7) * mm});
            skLineSegment(sketch, "E597", {"start": v(-132.88, 7) * mm, "end": v(-132.88, 6) * mm});
            skLineSegment(sketch, "E598", {"start": v(-132.88, 6) * mm, "end": v(-133.68, 6) * mm});
            skLineSegment(sketch, "E599", {"start": v(-133.68, 6) * mm, "end": v(-133.68, 2.5) * mm});
            skLineSegment(sketch, "E600", {"start": v(-133.68, 2.5) * mm, "end": v(-132.88, 2.5) * mm});
            skLineSegment(sketch, "E601", {"start": v(-132.88, 2.5) * mm, "end": v(-132.88, -2.5) * mm});
            skLineSegment(sketch, "E602", {"start": v(-132.88, -2.5) * mm, "end": v(-133.68, -2.5) * mm});
            skLineSegment(sketch, "E603", {"start": v(-133.68, -2.5) * mm, "end": v(-133.68, -6) * mm});
            skLineSegment(sketch, "E604", {"start": v(-133.68, -6) * mm, "end": v(-132.88, -6) * mm});
            skLineSegment(sketch, "E605", {"start": v(-132.88, -6) * mm, "end": v(-132.88, -7) * mm});
            skLineSegment(sketch, "E606", {"start": v(-132.88, -7) * mm, "end": v(-118.88, -7) * mm});
            skLineSegment(sketch, "E607", {"start": v(-118.88, -7) * mm, "end": v(-118.88, -6) * mm});
            skLineSegment(sketch, "E608", {"start": v(-92.75, -6) * mm, "end": v(-91.95, -6) * mm});
            skLineSegment(sketch, "E609", {"start": v(-91.95, -6) * mm, "end": v(-91.95, -2.5) * mm});
            skLineSegment(sketch, "E610", {"start": v(-91.95, -2.5) * mm, "end": v(-92.75, -2.5) * mm});
            skLineSegment(sketch, "E611", {"start": v(-92.75, -2.5) * mm, "end": v(-92.75, 2.5) * mm});
            skLineSegment(sketch, "E612", {"start": v(-92.75, 2.5) * mm, "end": v(-91.95, 2.5) * mm});
            skLineSegment(sketch, "E613", {"start": v(-91.95, 2.5) * mm, "end": v(-91.95, 6) * mm});
            skLineSegment(sketch, "E614", {"start": v(-91.95, 6) * mm, "end": v(-92.75, 6) * mm});
            skLineSegment(sketch, "E615", {"start": v(-92.75, 6) * mm, "end": v(-92.75, 7) * mm});
            skLineSegment(sketch, "E616", {"start": v(-92.75, 7) * mm, "end": v(-106.75, 7) * mm});
            skLineSegment(sketch, "E617", {"start": v(-106.75, 7) * mm, "end": v(-106.75, 6) * mm});
            skLineSegment(sketch, "E618", {"start": v(-106.75, 6) * mm, "end": v(-107.55, 6) * mm});
            skLineSegment(sketch, "E619", {"start": v(-107.55, 6) * mm, "end": v(-107.55, 2.5) * mm});
            skLineSegment(sketch, "E620", {"start": v(-107.55, 2.5) * mm, "end": v(-106.75, 2.5) * mm});
            skLineSegment(sketch, "E621", {"start": v(-106.75, 2.5) * mm, "end": v(-106.75, -2.5) * mm});
            skLineSegment(sketch, "E622", {"start": v(-106.75, -2.5) * mm, "end": v(-107.55, -2.5) * mm});
            skLineSegment(sketch, "E623", {"start": v(-107.55, -2.5) * mm, "end": v(-107.55, -6) * mm});
            skLineSegment(sketch, "E624", {"start": v(-107.55, -6) * mm, "end": v(-106.75, -6) * mm});
            skLineSegment(sketch, "E625", {"start": v(-106.75, -6) * mm, "end": v(-106.75, -7) * mm});
            skLineSegment(sketch, "E626", {"start": v(-106.75, -7) * mm, "end": v(-92.75, -7) * mm});
            skLineSegment(sketch, "E627", {"start": v(-92.75, -7) * mm, "end": v(-92.75, -6) * mm});
            skLineSegment(sketch, "E628", {"start": v(-73.75, -6) * mm, "end": v(-72.95, -6) * mm});
            skLineSegment(sketch, "E629", {"start": v(-72.95, -6) * mm, "end": v(-72.95, -2.5) * mm});
            skLineSegment(sketch, "E630", {"start": v(-72.95, -2.5) * mm, "end": v(-73.75, -2.5) * mm});
            skLineSegment(sketch, "E631", {"start": v(-73.75, -2.5) * mm, "end": v(-73.75, 2.5) * mm});
            skLineSegment(sketch, "E632", {"start": v(-73.75, 2.5) * mm, "end": v(-72.95, 2.5) * mm});
            skLineSegment(sketch, "E633", {"start": v(-72.95, 2.5) * mm, "end": v(-72.95, 6) * mm});
            skLineSegment(sketch, "E634", {"start": v(-72.95, 6) * mm, "end": v(-73.75, 6) * mm});
            skLineSegment(sketch, "E635", {"start": v(-73.75, 6) * mm, "end": v(-73.75, 7) * mm});
            skLineSegment(sketch, "E636", {"start": v(-73.75, 7) * mm, "end": v(-87.75, 7) * mm});
            skLineSegment(sketch, "E637", {"start": v(-87.75, 7) * mm, "end": v(-87.75, 6) * mm});
            skLineSegment(sketch, "E638", {"start": v(-87.75, 6) * mm, "end": v(-88.55, 6) * mm});
            skLineSegment(sketch, "E639", {"start": v(-88.55, 6) * mm, "end": v(-88.55, 2.5) * mm});
            skLineSegment(sketch, "E640", {"start": v(-88.55, 2.5) * mm, "end": v(-87.75, 2.5) * mm});
            skLineSegment(sketch, "E641", {"start": v(-87.75, 2.5) * mm, "end": v(-87.75, -2.5) * mm});
            skLineSegment(sketch, "E642", {"start": v(-87.75, -2.5) * mm, "end": v(-88.55, -2.5) * mm});
            skLineSegment(sketch, "E643", {"start": v(-88.55, -2.5) * mm, "end": v(-88.55, -6) * mm});
            skLineSegment(sketch, "E644", {"start": v(-88.55, -6) * mm, "end": v(-87.75, -6) * mm});
            skLineSegment(sketch, "E645", {"start": v(-87.75, -6) * mm, "end": v(-87.75, -7) * mm});
            skLineSegment(sketch, "E646", {"start": v(-87.75, -7) * mm, "end": v(-73.75, -7) * mm});
            skLineSegment(sketch, "E647", {"start": v(-73.75, -7) * mm, "end": v(-73.75, -6) * mm});
            skLineSegment(sketch, "E648", {"start": v(-54.75, -6) * mm, "end": v(-53.95, -6) * mm});
            skLineSegment(sketch, "E649", {"start": v(-53.95, -6) * mm, "end": v(-53.95, -2.5) * mm});
            skLineSegment(sketch, "E650", {"start": v(-53.95, -2.5) * mm, "end": v(-54.75, -2.5) * mm});
            skLineSegment(sketch, "E651", {"start": v(-54.75, -2.5) * mm, "end": v(-54.75, 2.5) * mm});
            skLineSegment(sketch, "E652", {"start": v(-54.75, 2.5) * mm, "end": v(-53.95, 2.5) * mm});
            skLineSegment(sketch, "E653", {"start": v(-53.95, 2.5) * mm, "end": v(-53.95, 6) * mm});
            skLineSegment(sketch, "E654", {"start": v(-53.95, 6) * mm, "end": v(-54.75, 6) * mm});
            skLineSegment(sketch, "E655", {"start": v(-54.75, 6) * mm, "end": v(-54.75, 7) * mm});
            skLineSegment(sketch, "E656", {"start": v(-54.75, 7) * mm, "end": v(-68.75, 7) * mm});
            skLineSegment(sketch, "E657", {"start": v(-68.75, 7) * mm, "end": v(-68.75, 6) * mm});
            skLineSegment(sketch, "E658", {"start": v(-68.75, 6) * mm, "end": v(-69.55, 6) * mm});
            skLineSegment(sketch, "E659", {"start": v(-69.55, 6) * mm, "end": v(-69.55, 2.5) * mm});
            skLineSegment(sketch, "E660", {"start": v(-69.55, 2.5) * mm, "end": v(-68.75, 2.5) * mm});
            skLineSegment(sketch, "E661", {"start": v(-68.75, 2.5) * mm, "end": v(-68.75, -2.5) * mm});
            skLineSegment(sketch, "E662", {"start": v(-68.75, -2.5) * mm, "end": v(-69.55, -2.5) * mm});
            skLineSegment(sketch, "E663", {"start": v(-69.55, -2.5) * mm, "end": v(-69.55, -6) * mm});
            skLineSegment(sketch, "E664", {"start": v(-69.55, -6) * mm, "end": v(-68.75, -6) * mm});
            skLineSegment(sketch, "E665", {"start": v(-68.75, -6) * mm, "end": v(-68.75, -7) * mm});
            skLineSegment(sketch, "E666", {"start": v(-68.75, -7) * mm, "end": v(-54.75, -7) * mm});
            skLineSegment(sketch, "E667", {"start": v(-54.75, -7) * mm, "end": v(-54.75, -6) * mm});
            skLineSegment(sketch, "E668", {"start": v(-35.75, -6) * mm, "end": v(-34.95, -6) * mm});
            skLineSegment(sketch, "E669", {"start": v(-34.95, -6) * mm, "end": v(-34.95, -2.5) * mm});
            skLineSegment(sketch, "E670", {"start": v(-34.95, -2.5) * mm, "end": v(-35.75, -2.5) * mm});
            skLineSegment(sketch, "E671", {"start": v(-35.75, -2.5) * mm, "end": v(-35.75, 2.5) * mm});
            skLineSegment(sketch, "E672", {"start": v(-35.75, 2.5) * mm, "end": v(-34.95, 2.5) * mm});
            skLineSegment(sketch, "E673", {"start": v(-34.95, 2.5) * mm, "end": v(-34.95, 6) * mm});
            skLineSegment(sketch, "E674", {"start": v(-34.95, 6) * mm, "end": v(-35.75, 6) * mm});
            skLineSegment(sketch, "E675", {"start": v(-35.75, 6) * mm, "end": v(-35.75, 7) * mm});
            skLineSegment(sketch, "E676", {"start": v(-35.75, 7) * mm, "end": v(-49.75, 7) * mm});
            skLineSegment(sketch, "E677", {"start": v(-49.75, 7) * mm, "end": v(-49.75, 6) * mm});
            skLineSegment(sketch, "E678", {"start": v(-49.75, 6) * mm, "end": v(-50.55, 6) * mm});
            skLineSegment(sketch, "E679", {"start": v(-50.55, 6) * mm, "end": v(-50.55, 2.5) * mm});
            skLineSegment(sketch, "E680", {"start": v(-50.55, 2.5) * mm, "end": v(-49.75, 2.5) * mm});
            skLineSegment(sketch, "E681", {"start": v(-49.75, 2.5) * mm, "end": v(-49.75, -2.5) * mm});
            skLineSegment(sketch, "E682", {"start": v(-49.75, -2.5) * mm, "end": v(-50.55, -2.5) * mm});
            skLineSegment(sketch, "E683", {"start": v(-50.55, -2.5) * mm, "end": v(-50.55, -6) * mm});
            skLineSegment(sketch, "E684", {"start": v(-50.55, -6) * mm, "end": v(-49.75, -6) * mm});
            skLineSegment(sketch, "E685", {"start": v(-49.75, -6) * mm, "end": v(-49.75, -7) * mm});
            skLineSegment(sketch, "E686", {"start": v(-49.75, -7) * mm, "end": v(-35.75, -7) * mm});
            skLineSegment(sketch, "E687", {"start": v(-35.75, -7) * mm, "end": v(-35.75, -6) * mm});
            skLineSegment(sketch, "E688", {"start": v(-16.75, -6) * mm, "end": v(-15.95, -6) * mm});
            skLineSegment(sketch, "E689", {"start": v(-15.95, -6) * mm, "end": v(-15.95, -2.5) * mm});
            skLineSegment(sketch, "E690", {"start": v(-15.95, -2.5) * mm, "end": v(-16.75, -2.5) * mm});
            skLineSegment(sketch, "E691", {"start": v(-16.75, -2.5) * mm, "end": v(-16.75, 2.5) * mm});
            skLineSegment(sketch, "E692", {"start": v(-16.75, 2.5) * mm, "end": v(-15.95, 2.5) * mm});
            skLineSegment(sketch, "E693", {"start": v(-15.95, 2.5) * mm, "end": v(-15.95, 6) * mm});
            skLineSegment(sketch, "E694", {"start": v(-15.95, 6) * mm, "end": v(-16.75, 6) * mm});
            skLineSegment(sketch, "E695", {"start": v(-16.75, 6) * mm, "end": v(-16.75, 7) * mm});
            skLineSegment(sketch, "E696", {"start": v(-16.75, 7) * mm, "end": v(-30.75, 7) * mm});
            skLineSegment(sketch, "E697", {"start": v(-30.75, 7) * mm, "end": v(-30.75, 6) * mm});
            skLineSegment(sketch, "E698", {"start": v(-30.75, 6) * mm, "end": v(-31.55, 6) * mm});
            skLineSegment(sketch, "E699", {"start": v(-31.55, 6) * mm, "end": v(-31.55, 2.5) * mm});
            skLineSegment(sketch, "E700", {"start": v(-31.55, 2.5) * mm, "end": v(-30.75, 2.5) * mm});
            skLineSegment(sketch, "E701", {"start": v(-30.75, 2.5) * mm, "end": v(-30.75, -2.5) * mm});
            skLineSegment(sketch, "E702", {"start": v(-30.75, -2.5) * mm, "end": v(-31.55, -2.5) * mm});
            skLineSegment(sketch, "E703", {"start": v(-31.55, -2.5) * mm, "end": v(-31.55, -6) * mm});
            skLineSegment(sketch, "E704", {"start": v(-31.55, -6) * mm, "end": v(-30.75, -6) * mm});
            skLineSegment(sketch, "E705", {"start": v(-30.75, -6) * mm, "end": v(-30.75, -7) * mm});
            skLineSegment(sketch, "E706", {"start": v(-30.75, -7) * mm, "end": v(-16.75, -7) * mm});
            skLineSegment(sketch, "E707", {"start": v(-16.75, -7) * mm, "end": v(-16.75, -6) * mm});
            skLineSegment(sketch, "E708", {"start": v(2.25, -6) * mm, "end": v(3.05, -6) * mm});
            skLineSegment(sketch, "E709", {"start": v(3.05, -6) * mm, "end": v(3.05, -2.5) * mm});
            skLineSegment(sketch, "E710", {"start": v(3.05, -2.5) * mm, "end": v(2.25, -2.5) * mm});
            skLineSegment(sketch, "E711", {"start": v(2.25, -2.5) * mm, "end": v(2.25, 2.5) * mm});
            skLineSegment(sketch, "E712", {"start": v(2.25, 2.5) * mm, "end": v(3.05, 2.5) * mm});
            skLineSegment(sketch, "E713", {"start": v(3.05, 2.5) * mm, "end": v(3.05, 6) * mm});
            skLineSegment(sketch, "E714", {"start": v(3.05, 6) * mm, "end": v(2.25, 6) * mm});
            skLineSegment(sketch, "E715", {"start": v(2.25, 6) * mm, "end": v(2.25, 7) * mm});
            skLineSegment(sketch, "E716", {"start": v(2.25, 7) * mm, "end": v(-11.75, 7) * mm});
            skLineSegment(sketch, "E717", {"start": v(-11.75, 7) * mm, "end": v(-11.75, 6) * mm});
            skLineSegment(sketch, "E718", {"start": v(-11.75, 6) * mm, "end": v(-12.55, 6) * mm});
            skLineSegment(sketch, "E719", {"start": v(-12.55, 6) * mm, "end": v(-12.55, 2.5) * mm});
            skLineSegment(sketch, "E720", {"start": v(-12.55, 2.5) * mm, "end": v(-11.75, 2.5) * mm});
            skLineSegment(sketch, "E721", {"start": v(-11.75, 2.5) * mm, "end": v(-11.75, -2.5) * mm});
            skLineSegment(sketch, "E722", {"start": v(-11.75, -2.5) * mm, "end": v(-12.55, -2.5) * mm});
            skLineSegment(sketch, "E723", {"start": v(-12.55, -2.5) * mm, "end": v(-12.55, -6) * mm});
            skLineSegment(sketch, "E724", {"start": v(-12.55, -6) * mm, "end": v(-11.75, -6) * mm});
            skLineSegment(sketch, "E725", {"start": v(-11.75, -6) * mm, "end": v(-11.75, -7) * mm});
            skLineSegment(sketch, "E726", {"start": v(-11.75, -7) * mm, "end": v(2.25, -7) * mm});
            skLineSegment(sketch, "E727", {"start": v(2.25, -7) * mm, "end": v(2.25, -6) * mm});
            skLineSegment(sketch, "E728", {"start": v(21.25, -6) * mm, "end": v(22.05, -6) * mm});
            skLineSegment(sketch, "E729", {"start": v(22.05, -6) * mm, "end": v(22.05, -2.5) * mm});
            skLineSegment(sketch, "E730", {"start": v(22.05, -2.5) * mm, "end": v(21.25, -2.5) * mm});
            skLineSegment(sketch, "E731", {"start": v(21.25, -2.5) * mm, "end": v(21.25, 2.5) * mm});
            skLineSegment(sketch, "E732", {"start": v(21.25, 2.5) * mm, "end": v(22.05, 2.5) * mm});
            skLineSegment(sketch, "E733", {"start": v(22.05, 2.5) * mm, "end": v(22.05, 6) * mm});
            skLineSegment(sketch, "E734", {"start": v(22.05, 6) * mm, "end": v(21.25, 6) * mm});
            skLineSegment(sketch, "E735", {"start": v(21.25, 6) * mm, "end": v(21.25, 7) * mm});
            skLineSegment(sketch, "E736", {"start": v(21.25, 7) * mm, "end": v(7.25, 7) * mm});
            skLineSegment(sketch, "E737", {"start": v(7.25, 7) * mm, "end": v(7.25, 6) * mm});
            skLineSegment(sketch, "E738", {"start": v(7.25, 6) * mm, "end": v(6.45, 6) * mm});
            skLineSegment(sketch, "E739", {"start": v(6.45, 6) * mm, "end": v(6.45, 2.5) * mm});
            skLineSegment(sketch, "E740", {"start": v(6.45, 2.5) * mm, "end": v(7.25, 2.5) * mm});
            skLineSegment(sketch, "E741", {"start": v(7.25, 2.5) * mm, "end": v(7.25, -2.5) * mm});
            skLineSegment(sketch, "E742", {"start": v(7.25, -2.5) * mm, "end": v(6.45, -2.5) * mm});
            skLineSegment(sketch, "E743", {"start": v(6.45, -2.5) * mm, "end": v(6.45, -6) * mm});
            skLineSegment(sketch, "E744", {"start": v(6.45, -6) * mm, "end": v(7.25, -6) * mm});
            skLineSegment(sketch, "E745", {"start": v(7.25, -6) * mm, "end": v(7.25, -7) * mm});
            skLineSegment(sketch, "E746", {"start": v(7.25, -7) * mm, "end": v(21.25, -7) * mm});
            skLineSegment(sketch, "E747", {"start": v(21.25, -7) * mm, "end": v(21.25, -6) * mm});
            skLineSegment(sketch, "E748", {"start": v(40.25, -6) * mm, "end": v(41.05, -6) * mm});
            skLineSegment(sketch, "E749", {"start": v(41.05, -6) * mm, "end": v(41.05, -2.5) * mm});
            skLineSegment(sketch, "E750", {"start": v(41.05, -2.5) * mm, "end": v(40.25, -2.5) * mm});
            skLineSegment(sketch, "E751", {"start": v(40.25, -2.5) * mm, "end": v(40.25, 2.5) * mm});
            skLineSegment(sketch, "E752", {"start": v(40.25, 2.5) * mm, "end": v(41.05, 2.5) * mm});
            skLineSegment(sketch, "E753", {"start": v(41.05, 2.5) * mm, "end": v(41.05, 6) * mm});
            skLineSegment(sketch, "E754", {"start": v(41.05, 6) * mm, "end": v(40.25, 6) * mm});
            skLineSegment(sketch, "E755", {"start": v(40.25, 6) * mm, "end": v(40.25, 7) * mm});
            skLineSegment(sketch, "E756", {"start": v(40.25, 7) * mm, "end": v(26.25, 7) * mm});
            skLineSegment(sketch, "E757", {"start": v(26.25, 7) * mm, "end": v(26.25, 6) * mm});
            skLineSegment(sketch, "E758", {"start": v(26.25, 6) * mm, "end": v(25.45, 6) * mm});
            skLineSegment(sketch, "E759", {"start": v(25.45, 6) * mm, "end": v(25.45, 2.5) * mm});
            skLineSegment(sketch, "E760", {"start": v(25.45, 2.5) * mm, "end": v(26.25, 2.5) * mm});
            skLineSegment(sketch, "E761", {"start": v(26.25, 2.5) * mm, "end": v(26.25, -2.5) * mm});
            skLineSegment(sketch, "E762", {"start": v(26.25, -2.5) * mm, "end": v(25.45, -2.5) * mm});
            skLineSegment(sketch, "E763", {"start": v(25.45, -2.5) * mm, "end": v(25.45, -6) * mm});
            skLineSegment(sketch, "E764", {"start": v(25.45, -6) * mm, "end": v(26.25, -6) * mm});
            skLineSegment(sketch, "E765", {"start": v(26.25, -6) * mm, "end": v(26.25, -7) * mm});
            skLineSegment(sketch, "E766", {"start": v(26.25, -7) * mm, "end": v(40.25, -7) * mm});
            skLineSegment(sketch, "E767", {"start": v(40.25, -7) * mm, "end": v(40.25, -6) * mm});
            skLineSegment(sketch, "E768", {"start": v(59.25, -6) * mm, "end": v(60.05, -6) * mm});
            skLineSegment(sketch, "E769", {"start": v(60.05, -6) * mm, "end": v(60.05, -2.5) * mm});
            skLineSegment(sketch, "E770", {"start": v(60.05, -2.5) * mm, "end": v(59.25, -2.5) * mm});
            skLineSegment(sketch, "E771", {"start": v(59.25, -2.5) * mm, "end": v(59.25, 2.5) * mm});
            skLineSegment(sketch, "E772", {"start": v(59.25, 2.5) * mm, "end": v(60.05, 2.5) * mm});
            skLineSegment(sketch, "E773", {"start": v(60.05, 2.5) * mm, "end": v(60.05, 6) * mm});
            skLineSegment(sketch, "E774", {"start": v(60.05, 6) * mm, "end": v(59.25, 6) * mm});
            skLineSegment(sketch, "E775", {"start": v(59.25, 6) * mm, "end": v(59.25, 7) * mm});
            skLineSegment(sketch, "E776", {"start": v(59.25, 7) * mm, "end": v(45.25, 7) * mm});
            skLineSegment(sketch, "E777", {"start": v(45.25, 7) * mm, "end": v(45.25, 6) * mm});
            skLineSegment(sketch, "E778", {"start": v(45.25, 6) * mm, "end": v(44.45, 6) * mm});
            skLineSegment(sketch, "E779", {"start": v(44.45, 6) * mm, "end": v(44.45, 2.5) * mm});
            skLineSegment(sketch, "E780", {"start": v(44.45, 2.5) * mm, "end": v(45.25, 2.5) * mm});
            skLineSegment(sketch, "E781", {"start": v(45.25, 2.5) * mm, "end": v(45.25, -2.5) * mm});
            skLineSegment(sketch, "E782", {"start": v(45.25, -2.5) * mm, "end": v(44.45, -2.5) * mm});
            skLineSegment(sketch, "E783", {"start": v(44.45, -2.5) * mm, "end": v(44.45, -6) * mm});
            skLineSegment(sketch, "E784", {"start": v(44.45, -6) * mm, "end": v(45.25, -6) * mm});
            skLineSegment(sketch, "E785", {"start": v(45.25, -6) * mm, "end": v(45.25, -7) * mm});
            skLineSegment(sketch, "E786", {"start": v(45.25, -7) * mm, "end": v(59.25, -7) * mm});
            skLineSegment(sketch, "E787", {"start": v(59.25, -7) * mm, "end": v(59.25, -6) * mm});
            skLineSegment(sketch, "E788", {"start": v(78.25, -6) * mm, "end": v(79.05, -6) * mm});
            skLineSegment(sketch, "E789", {"start": v(79.05, -6) * mm, "end": v(79.05, -2.5) * mm});
            skLineSegment(sketch, "E790", {"start": v(79.05, -2.5) * mm, "end": v(78.25, -2.5) * mm});
            skLineSegment(sketch, "E791", {"start": v(78.25, -2.5) * mm, "end": v(78.25, 2.5) * mm});
            skLineSegment(sketch, "E792", {"start": v(78.25, 2.5) * mm, "end": v(79.05, 2.5) * mm});
            skLineSegment(sketch, "E793", {"start": v(79.05, 2.5) * mm, "end": v(79.05, 6) * mm});
            skLineSegment(sketch, "E794", {"start": v(79.05, 6) * mm, "end": v(78.25, 6) * mm});
            skLineSegment(sketch, "E795", {"start": v(78.25, 6) * mm, "end": v(78.25, 7) * mm});
            skLineSegment(sketch, "E796", {"start": v(78.25, 7) * mm, "end": v(64.25, 7) * mm});
            skLineSegment(sketch, "E797", {"start": v(64.25, 7) * mm, "end": v(64.25, 6) * mm});
            skLineSegment(sketch, "E798", {"start": v(64.25, 6) * mm, "end": v(63.45, 6) * mm});
            skLineSegment(sketch, "E799", {"start": v(63.45, 6) * mm, "end": v(63.45, 2.5) * mm});
            skLineSegment(sketch, "E800", {"start": v(63.45, 2.5) * mm, "end": v(64.25, 2.5) * mm});
            skLineSegment(sketch, "E801", {"start": v(64.25, 2.5) * mm, "end": v(64.25, -2.5) * mm});
            skLineSegment(sketch, "E802", {"start": v(64.25, -2.5) * mm, "end": v(63.45, -2.5) * mm});
            skLineSegment(sketch, "E803", {"start": v(63.45, -2.5) * mm, "end": v(63.45, -6) * mm});
            skLineSegment(sketch, "E804", {"start": v(63.45, -6) * mm, "end": v(64.25, -6) * mm});
            skLineSegment(sketch, "E805", {"start": v(64.25, -6) * mm, "end": v(64.25, -7) * mm});
            skLineSegment(sketch, "E806", {"start": v(64.25, -7) * mm, "end": v(78.25, -7) * mm});
            skLineSegment(sketch, "E807", {"start": v(78.25, -7) * mm, "end": v(78.25, -6) * mm});
            skLineSegment(sketch, "E808", {"start": v(97.25, -6) * mm, "end": v(98.05, -6) * mm});
            skLineSegment(sketch, "E809", {"start": v(98.05, -6) * mm, "end": v(98.05, -2.5) * mm});
            skLineSegment(sketch, "E810", {"start": v(98.05, -2.5) * mm, "end": v(97.25, -2.5) * mm});
            skLineSegment(sketch, "E811", {"start": v(97.25, -2.5) * mm, "end": v(97.25, 2.5) * mm});
            skLineSegment(sketch, "E812", {"start": v(97.25, 2.5) * mm, "end": v(98.05, 2.5) * mm});
            skLineSegment(sketch, "E813", {"start": v(98.05, 2.5) * mm, "end": v(98.05, 6) * mm});
            skLineSegment(sketch, "E814", {"start": v(98.05, 6) * mm, "end": v(97.25, 6) * mm});
            skLineSegment(sketch, "E815", {"start": v(97.25, 6) * mm, "end": v(97.25, 7) * mm});
            skLineSegment(sketch, "E816", {"start": v(97.25, 7) * mm, "end": v(83.25, 7) * mm});
            skLineSegment(sketch, "E817", {"start": v(83.25, 7) * mm, "end": v(83.25, 6) * mm});
            skLineSegment(sketch, "E818", {"start": v(83.25, 6) * mm, "end": v(82.45, 6) * mm});
            skLineSegment(sketch, "E819", {"start": v(82.45, 6) * mm, "end": v(82.45, 2.5) * mm});
            skLineSegment(sketch, "E820", {"start": v(82.45, 2.5) * mm, "end": v(83.25, 2.5) * mm});
            skLineSegment(sketch, "E821", {"start": v(83.25, 2.5) * mm, "end": v(83.25, -2.5) * mm});
            skLineSegment(sketch, "E822", {"start": v(83.25, -2.5) * mm, "end": v(82.45, -2.5) * mm});
            skLineSegment(sketch, "E823", {"start": v(82.45, -2.5) * mm, "end": v(82.45, -6) * mm});
            skLineSegment(sketch, "E824", {"start": v(82.45, -6) * mm, "end": v(83.25, -6) * mm});
            skLineSegment(sketch, "E825", {"start": v(83.25, -6) * mm, "end": v(83.25, -7) * mm});
            skLineSegment(sketch, "E826", {"start": v(83.25, -7) * mm, "end": v(97.25, -7) * mm});
            skLineSegment(sketch, "E827", {"start": v(97.25, -7) * mm, "end": v(97.25, -6) * mm});
            skLineSegment(sketch, "E828", {"start": v(110.72, -6.77) * mm, "end": v(112.55, -6.77) * mm});
            skLineSegment(sketch, "E829", {"start": v(112.55, -6.77) * mm, "end": v(112.55, -5.97) * mm});
            skLineSegment(sketch, "E830", {"start": v(112.55, -5.97) * mm, "end": v(113.32, -5.97) * mm});
            skLineSegment(sketch, "E831", {"start": v(113.32, -5.97) * mm, "end": v(113.32, -6) * mm});
            skLineSegment(sketch, "E832", {"start": v(113.32, -6) * mm, "end": v(114.12, -6) * mm});
            skLineSegment(sketch, "E833", {"start": v(114.12, -6) * mm, "end": v(114.12, -7) * mm});
            skLineSegment(sketch, "E834", {"start": v(114.12, -7) * mm, "end": v(128.12, -7) * mm});
            skLineSegment(sketch, "E835", {"start": v(128.12, -7) * mm, "end": v(128.12, -6) * mm});
            skLineSegment(sketch, "E836", {"start": v(128.12, -6) * mm, "end": v(128.93, -6) * mm});
            skLineSegment(sketch, "E837", {"start": v(128.93, -6) * mm, "end": v(128.93, -5.97) * mm});
            skLineSegment(sketch, "E838", {"start": v(128.93, -5.97) * mm, "end": v(129.7, -5.97) * mm});
            skLineSegment(sketch, "E839", {"start": v(129.7, -5.97) * mm, "end": v(129.7, -6.77) * mm});
            skLineSegment(sketch, "E840", {"start": v(129.7, -6.77) * mm, "end": v(131.52, -6.77) * mm});
            skLineSegment(sketch, "E841", {"start": v(131.52, -6.77) * mm, "end": v(131.52, -7.97) * mm});
            skLineSegment(sketch, "E842", {"start": v(131.52, -7.97) * mm, "end": v(134.52, -7.97) * mm});
            skLineSegment(sketch, "E843", {"start": v(134.52, -7.97) * mm, "end": v(134.52, -6.77) * mm});
            skLineSegment(sketch, "E844", {"start": v(134.52, -6.77) * mm, "end": v(136.35, -6.77) * mm});
            skLineSegment(sketch, "E845", {"start": v(136.35, -6.77) * mm, "end": v(136.35, -0.5) * mm});
            skLineSegment(sketch, "E846", {"start": v(136.35, -0.5) * mm, "end": v(137.23, -0.5) * mm});
            skLineSegment(sketch, "E847", {"start": v(137.23, -0.5) * mm, "end": v(137.23, 2.3) * mm});
            skLineSegment(sketch, "E848", {"start": v(137.23, 2.3) * mm, "end": v(136.35, 2.3) * mm});
            skLineSegment(sketch, "E849", {"start": v(136.35, 2.3) * mm, "end": v(136.35, 5.53) * mm});
            skLineSegment(sketch, "E850", {"start": v(136.35, 5.53) * mm, "end": v(129.7, 5.53) * mm});
            skLineSegment(sketch, "E851", {"start": v(129.7, 5.53) * mm, "end": v(129.7, 4.73) * mm});
            skLineSegment(sketch, "E852", {"start": v(129.7, 4.73) * mm, "end": v(128.93, 4.73) * mm});
            skLineSegment(sketch, "E853", {"start": v(128.93, 4.73) * mm, "end": v(128.93, 6) * mm});
            skLineSegment(sketch, "E854", {"start": v(128.93, 6) * mm, "end": v(128.12, 6) * mm});
            skLineSegment(sketch, "E855", {"start": v(128.12, 6) * mm, "end": v(128.12, 7) * mm});
            skLineSegment(sketch, "E856", {"start": v(128.12, 7) * mm, "end": v(114.12, 7) * mm});
            skLineSegment(sketch, "E857", {"start": v(114.12, 7) * mm, "end": v(114.12, 6) * mm});
            skLineSegment(sketch, "E858", {"start": v(114.12, 6) * mm, "end": v(113.32, 6) * mm});
            skLineSegment(sketch, "E859", {"start": v(113.32, 6) * mm, "end": v(113.32, 4.73) * mm});
            skLineSegment(sketch, "E860", {"start": v(113.32, 4.73) * mm, "end": v(112.55, 4.73) * mm});
            skLineSegment(sketch, "E861", {"start": v(112.55, 4.73) * mm, "end": v(112.55, 5.53) * mm});
            skLineSegment(sketch, "E862", {"start": v(112.55, 5.53) * mm, "end": v(105.9, 5.53) * mm});
            skLineSegment(sketch, "E863", {"start": v(105.9, 5.53) * mm, "end": v(105.9, 2.3) * mm});
            skLineSegment(sketch, "E864", {"start": v(105.9, 2.3) * mm, "end": v(105.03, 2.3) * mm});
            skLineSegment(sketch, "E865", {"start": v(105.03, 2.3) * mm, "end": v(105.03, -0.5) * mm});
            skLineSegment(sketch, "E866", {"start": v(105.03, -0.5) * mm, "end": v(105.9, -0.5) * mm});
            skLineSegment(sketch, "E867", {"start": v(105.9, -0.5) * mm, "end": v(105.9, -6.77) * mm});
            skLineSegment(sketch, "E868", {"start": v(105.9, -6.77) * mm, "end": v(107.72, -6.77) * mm});
            skLineSegment(sketch, "E869", {"start": v(107.72, -6.77) * mm, "end": v(107.72, -7.97) * mm});
            skLineSegment(sketch, "E870", {"start": v(107.72, -7.97) * mm, "end": v(110.72, -7.97) * mm});
            skLineSegment(sketch, "E871", {"start": v(110.72, -7.97) * mm, "end": v(110.72, -6.77) * mm});
            skLineSegment(sketch, "E872", {"start": v(-131.53, -25.77) * mm, "end": v(-129.7, -25.77) * mm});
            skLineSegment(sketch, "E873", {"start": v(-129.7, -25.77) * mm, "end": v(-129.7, -24.97) * mm});
            skLineSegment(sketch, "E874", {"start": v(-129.7, -24.97) * mm, "end": v(-128.93, -24.97) * mm});
            skLineSegment(sketch, "E875", {"start": v(-128.93, -24.97) * mm, "end": v(-128.93, -25) * mm});
            skLineSegment(sketch, "E876", {"start": v(-128.93, -25) * mm, "end": v(-128.12, -25) * mm});
            skLineSegment(sketch, "E877", {"start": v(-128.12, -25) * mm, "end": v(-128.12, -26) * mm});
            skLineSegment(sketch, "E878", {"start": v(-128.12, -26) * mm, "end": v(-114.12, -26) * mm});
            skLineSegment(sketch, "E879", {"start": v(-114.12, -26) * mm, "end": v(-114.12, -25) * mm});
            skLineSegment(sketch, "E880", {"start": v(-114.12, -25) * mm, "end": v(-113.33, -25) * mm});
            skLineSegment(sketch, "E881", {"start": v(-113.33, -25) * mm, "end": v(-113.33, -24.97) * mm});
            skLineSegment(sketch, "E882", {"start": v(-113.33, -24.97) * mm, "end": v(-112.55, -24.97) * mm});
            skLineSegment(sketch, "E883", {"start": v(-112.55, -24.97) * mm, "end": v(-112.55, -25.77) * mm});
            skLineSegment(sketch, "E884", {"start": v(-112.55, -25.77) * mm, "end": v(-110.72, -25.77) * mm});
            skLineSegment(sketch, "E885", {"start": v(-110.72, -25.77) * mm, "end": v(-110.72, -26.97) * mm});
            skLineSegment(sketch, "E886", {"start": v(-110.72, -26.97) * mm, "end": v(-107.72, -26.97) * mm});
            skLineSegment(sketch, "E887", {"start": v(-107.72, -26.97) * mm, "end": v(-107.72, -25.77) * mm});
            skLineSegment(sketch, "E888", {"start": v(-107.72, -25.77) * mm, "end": v(-105.9, -25.77) * mm});
            skLineSegment(sketch, "E889", {"start": v(-105.9, -25.77) * mm, "end": v(-105.9, -19.5) * mm});
            skLineSegment(sketch, "E890", {"start": v(-105.9, -19.5) * mm, "end": v(-105.03, -19.5) * mm});
            skLineSegment(sketch, "E891", {"start": v(-105.03, -19.5) * mm, "end": v(-105.03, -16.7) * mm});
            skLineSegment(sketch, "E892", {"start": v(-105.03, -16.7) * mm, "end": v(-105.9, -16.7) * mm});
            skLineSegment(sketch, "E893", {"start": v(-105.9, -16.7) * mm, "end": v(-105.9, -13.47) * mm});
            skLineSegment(sketch, "E894", {"start": v(-105.9, -13.47) * mm, "end": v(-112.55, -13.47) * mm});
            skLineSegment(sketch, "E895", {"start": v(-112.55, -13.47) * mm, "end": v(-112.55, -14.27) * mm});
            skLineSegment(sketch, "E896", {"start": v(-112.55, -14.27) * mm, "end": v(-113.33, -14.27) * mm});
            skLineSegment(sketch, "E897", {"start": v(-113.33, -14.27) * mm, "end": v(-113.33, -13) * mm});
            skLineSegment(sketch, "E898", {"start": v(-113.33, -13) * mm, "end": v(-114.12, -13) * mm});
            skLineSegment(sketch, "E899", {"start": v(-114.12, -13) * mm, "end": v(-114.12, -12) * mm});
            skLineSegment(sketch, "E900", {"start": v(-114.12, -12) * mm, "end": v(-128.12, -12) * mm});
            skLineSegment(sketch, "E901", {"start": v(-128.12, -12) * mm, "end": v(-128.12, -13) * mm});
            skLineSegment(sketch, "E902", {"start": v(-128.12, -13) * mm, "end": v(-128.93, -13) * mm});
            skLineSegment(sketch, "E903", {"start": v(-128.93, -13) * mm, "end": v(-128.93, -14.27) * mm});
            skLineSegment(sketch, "E904", {"start": v(-128.93, -14.27) * mm, "end": v(-129.7, -14.27) * mm});
            skLineSegment(sketch, "E905", {"start": v(-129.7, -14.27) * mm, "end": v(-129.7, -13.47) * mm});
            skLineSegment(sketch, "E906", {"start": v(-129.7, -13.47) * mm, "end": v(-136.35, -13.47) * mm});
            skLineSegment(sketch, "E907", {"start": v(-136.35, -13.47) * mm, "end": v(-136.35, -16.7) * mm});
            skLineSegment(sketch, "E908", {"start": v(-136.35, -16.7) * mm, "end": v(-137.22, -16.7) * mm});
            skLineSegment(sketch, "E909", {"start": v(-137.22, -16.7) * mm, "end": v(-137.22, -19.5) * mm});
            skLineSegment(sketch, "E910", {"start": v(-137.22, -19.5) * mm, "end": v(-136.35, -19.5) * mm});
            skLineSegment(sketch, "E911", {"start": v(-136.35, -19.5) * mm, "end": v(-136.35, -25.77) * mm});
            skLineSegment(sketch, "E912", {"start": v(-136.35, -25.77) * mm, "end": v(-134.53, -25.77) * mm});
            skLineSegment(sketch, "E913", {"start": v(-134.53, -25.77) * mm, "end": v(-134.53, -26.97) * mm});
            skLineSegment(sketch, "E914", {"start": v(-134.53, -26.97) * mm, "end": v(-131.53, -26.97) * mm});
            skLineSegment(sketch, "E915", {"start": v(-131.53, -26.97) * mm, "end": v(-131.53, -25.77) * mm});
            skLineSegment(sketch, "E916", {"start": v(-83.25, -25) * mm, "end": v(-82.45, -25) * mm});
            skLineSegment(sketch, "E917", {"start": v(-82.45, -25) * mm, "end": v(-82.45, -21.5) * mm});
            skLineSegment(sketch, "E918", {"start": v(-82.45, -21.5) * mm, "end": v(-83.25, -21.5) * mm});
            skLineSegment(sketch, "E919", {"start": v(-83.25, -21.5) * mm, "end": v(-83.25, -16.5) * mm});
            skLineSegment(sketch, "E920", {"start": v(-83.25, -16.5) * mm, "end": v(-82.45, -16.5) * mm});
            skLineSegment(sketch, "E921", {"start": v(-82.45, -16.5) * mm, "end": v(-82.45, -13) * mm});
            skLineSegment(sketch, "E922", {"start": v(-82.45, -13) * mm, "end": v(-83.25, -13) * mm});
            skLineSegment(sketch, "E923", {"start": v(-83.25, -13) * mm, "end": v(-83.25, -12) * mm});
            skLineSegment(sketch, "E924", {"start": v(-83.25, -12) * mm, "end": v(-97.25, -12) * mm});
            skLineSegment(sketch, "E925", {"start": v(-97.25, -12) * mm, "end": v(-97.25, -13) * mm});
            skLineSegment(sketch, "E926", {"start": v(-97.25, -13) * mm, "end": v(-98.05, -13) * mm});
            skLineSegment(sketch, "E927", {"start": v(-98.05, -13) * mm, "end": v(-98.05, -16.5) * mm});
            skLineSegment(sketch, "E928", {"start": v(-98.05, -16.5) * mm, "end": v(-97.25, -16.5) * mm});
            skLineSegment(sketch, "E929", {"start": v(-97.25, -16.5) * mm, "end": v(-97.25, -21.5) * mm});
            skLineSegment(sketch, "E930", {"start": v(-97.25, -21.5) * mm, "end": v(-98.05, -21.5) * mm});
            skLineSegment(sketch, "E931", {"start": v(-98.05, -21.5) * mm, "end": v(-98.05, -25) * mm});
            skLineSegment(sketch, "E932", {"start": v(-98.05, -25) * mm, "end": v(-97.25, -25) * mm});
            skLineSegment(sketch, "E933", {"start": v(-97.25, -25) * mm, "end": v(-97.25, -26) * mm});
            skLineSegment(sketch, "E934", {"start": v(-97.25, -26) * mm, "end": v(-83.25, -26) * mm});
            skLineSegment(sketch, "E935", {"start": v(-83.25, -26) * mm, "end": v(-83.25, -25) * mm});
            skLineSegment(sketch, "E936", {"start": v(-64.25, -25) * mm, "end": v(-63.45, -25) * mm});
            skLineSegment(sketch, "E937", {"start": v(-63.45, -25) * mm, "end": v(-63.45, -21.5) * mm});
            skLineSegment(sketch, "E938", {"start": v(-63.45, -21.5) * mm, "end": v(-64.25, -21.5) * mm});
            skLineSegment(sketch, "E939", {"start": v(-64.25, -21.5) * mm, "end": v(-64.25, -16.5) * mm});
            skLineSegment(sketch, "E940", {"start": v(-64.25, -16.5) * mm, "end": v(-63.45, -16.5) * mm});
            skLineSegment(sketch, "E941", {"start": v(-63.45, -16.5) * mm, "end": v(-63.45, -13) * mm});
            skLineSegment(sketch, "E942", {"start": v(-63.45, -13) * mm, "end": v(-64.25, -13) * mm});
            skLineSegment(sketch, "E943", {"start": v(-64.25, -13) * mm, "end": v(-64.25, -12) * mm});
            skLineSegment(sketch, "E944", {"start": v(-64.25, -12) * mm, "end": v(-78.25, -12) * mm});
            skLineSegment(sketch, "E945", {"start": v(-78.25, -12) * mm, "end": v(-78.25, -13) * mm});
            skLineSegment(sketch, "E946", {"start": v(-78.25, -13) * mm, "end": v(-79.05, -13) * mm});
            skLineSegment(sketch, "E947", {"start": v(-79.05, -13) * mm, "end": v(-79.05, -16.5) * mm});
            skLineSegment(sketch, "E948", {"start": v(-79.05, -16.5) * mm, "end": v(-78.25, -16.5) * mm});
            skLineSegment(sketch, "E949", {"start": v(-78.25, -16.5) * mm, "end": v(-78.25, -21.5) * mm});
            skLineSegment(sketch, "E950", {"start": v(-78.25, -21.5) * mm, "end": v(-79.05, -21.5) * mm});
            skLineSegment(sketch, "E951", {"start": v(-79.05, -21.5) * mm, "end": v(-79.05, -25) * mm});
            skLineSegment(sketch, "E952", {"start": v(-79.05, -25) * mm, "end": v(-78.25, -25) * mm});
            skLineSegment(sketch, "E953", {"start": v(-78.25, -25) * mm, "end": v(-78.25, -26) * mm});
            skLineSegment(sketch, "E954", {"start": v(-78.25, -26) * mm, "end": v(-64.25, -26) * mm});
            skLineSegment(sketch, "E955", {"start": v(-64.25, -26) * mm, "end": v(-64.25, -25) * mm});
            skLineSegment(sketch, "E956", {"start": v(-45.25, -25) * mm, "end": v(-44.45, -25) * mm});
            skLineSegment(sketch, "E957", {"start": v(-44.45, -25) * mm, "end": v(-44.45, -21.5) * mm});
            skLineSegment(sketch, "E958", {"start": v(-44.45, -21.5) * mm, "end": v(-45.25, -21.5) * mm});
            skLineSegment(sketch, "E959", {"start": v(-45.25, -21.5) * mm, "end": v(-45.25, -16.5) * mm});
            skLineSegment(sketch, "E960", {"start": v(-45.25, -16.5) * mm, "end": v(-44.45, -16.5) * mm});
            skLineSegment(sketch, "E961", {"start": v(-44.45, -16.5) * mm, "end": v(-44.45, -13) * mm});
            skLineSegment(sketch, "E962", {"start": v(-44.45, -13) * mm, "end": v(-45.25, -13) * mm});
            skLineSegment(sketch, "E963", {"start": v(-45.25, -13) * mm, "end": v(-45.25, -12) * mm});
            skLineSegment(sketch, "E964", {"start": v(-45.25, -12) * mm, "end": v(-59.25, -12) * mm});
            skLineSegment(sketch, "E965", {"start": v(-59.25, -12) * mm, "end": v(-59.25, -13) * mm});
            skLineSegment(sketch, "E966", {"start": v(-59.25, -13) * mm, "end": v(-60.05, -13) * mm});
            skLineSegment(sketch, "E967", {"start": v(-60.05, -13) * mm, "end": v(-60.05, -16.5) * mm});
            skLineSegment(sketch, "E968", {"start": v(-60.05, -16.5) * mm, "end": v(-59.25, -16.5) * mm});
            skLineSegment(sketch, "E969", {"start": v(-59.25, -16.5) * mm, "end": v(-59.25, -21.5) * mm});
            skLineSegment(sketch, "E970", {"start": v(-59.25, -21.5) * mm, "end": v(-60.05, -21.5) * mm});
            skLineSegment(sketch, "E971", {"start": v(-60.05, -21.5) * mm, "end": v(-60.05, -25) * mm});
            skLineSegment(sketch, "E972", {"start": v(-60.05, -25) * mm, "end": v(-59.25, -25) * mm});
            skLineSegment(sketch, "E973", {"start": v(-59.25, -25) * mm, "end": v(-59.25, -26) * mm});
            skLineSegment(sketch, "E974", {"start": v(-59.25, -26) * mm, "end": v(-45.25, -26) * mm});
            skLineSegment(sketch, "E975", {"start": v(-45.25, -26) * mm, "end": v(-45.25, -25) * mm});
            skLineSegment(sketch, "E976", {"start": v(-26.25, -25) * mm, "end": v(-25.45, -25) * mm});
            skLineSegment(sketch, "E977", {"start": v(-25.45, -25) * mm, "end": v(-25.45, -21.5) * mm});
            skLineSegment(sketch, "E978", {"start": v(-25.45, -21.5) * mm, "end": v(-26.25, -21.5) * mm});
            skLineSegment(sketch, "E979", {"start": v(-26.25, -21.5) * mm, "end": v(-26.25, -16.5) * mm});
            skLineSegment(sketch, "E980", {"start": v(-26.25, -16.5) * mm, "end": v(-25.45, -16.5) * mm});
            skLineSegment(sketch, "E981", {"start": v(-25.45, -16.5) * mm, "end": v(-25.45, -13) * mm});
            skLineSegment(sketch, "E982", {"start": v(-25.45, -13) * mm, "end": v(-26.25, -13) * mm});
            skLineSegment(sketch, "E983", {"start": v(-26.25, -13) * mm, "end": v(-26.25, -12) * mm});
            skLineSegment(sketch, "E984", {"start": v(-26.25, -12) * mm, "end": v(-40.25, -12) * mm});
            skLineSegment(sketch, "E985", {"start": v(-40.25, -12) * mm, "end": v(-40.25, -13) * mm});
            skLineSegment(sketch, "E986", {"start": v(-40.25, -13) * mm, "end": v(-41.05, -13) * mm});
            skLineSegment(sketch, "E987", {"start": v(-41.05, -13) * mm, "end": v(-41.05, -16.5) * mm});
            skLineSegment(sketch, "E988", {"start": v(-41.05, -16.5) * mm, "end": v(-40.25, -16.5) * mm});
            skLineSegment(sketch, "E989", {"start": v(-40.25, -16.5) * mm, "end": v(-40.25, -21.5) * mm});
            skLineSegment(sketch, "E990", {"start": v(-40.25, -21.5) * mm, "end": v(-41.05, -21.5) * mm});
            skLineSegment(sketch, "E991", {"start": v(-41.05, -21.5) * mm, "end": v(-41.05, -25) * mm});
            skLineSegment(sketch, "E992", {"start": v(-41.05, -25) * mm, "end": v(-40.25, -25) * mm});
            skLineSegment(sketch, "E993", {"start": v(-40.25, -25) * mm, "end": v(-40.25, -26) * mm});
            skLineSegment(sketch, "E994", {"start": v(-40.25, -26) * mm, "end": v(-26.25, -26) * mm});
            skLineSegment(sketch, "E995", {"start": v(-26.25, -26) * mm, "end": v(-26.25, -25) * mm});
            skLineSegment(sketch, "E996", {"start": v(-7.25, -25) * mm, "end": v(-6.45, -25) * mm});
            skLineSegment(sketch, "E997", {"start": v(-6.45, -25) * mm, "end": v(-6.45, -21.5) * mm});
            skLineSegment(sketch, "E998", {"start": v(-6.45, -21.5) * mm, "end": v(-7.25, -21.5) * mm});
            skLineSegment(sketch, "E999", {"start": v(-7.25, -21.5) * mm, "end": v(-7.25, -16.5) * mm});
            skLineSegment(sketch, "E1000", {"start": v(-7.25, -16.5) * mm, "end": v(-6.45, -16.5) * mm});
            skLineSegment(sketch, "E1001", {"start": v(-6.45, -16.5) * mm, "end": v(-6.45, -13) * mm});
            skLineSegment(sketch, "E1002", {"start": v(-6.45, -13) * mm, "end": v(-7.25, -13) * mm});
            skLineSegment(sketch, "E1003", {"start": v(-7.25, -13) * mm, "end": v(-7.25, -12) * mm});
            skLineSegment(sketch, "E1004", {"start": v(-7.25, -12) * mm, "end": v(-21.25, -12) * mm});
            skLineSegment(sketch, "E1005", {"start": v(-21.25, -12) * mm, "end": v(-21.25, -13) * mm});
            skLineSegment(sketch, "E1006", {"start": v(-21.25, -13) * mm, "end": v(-22.05, -13) * mm});
            skLineSegment(sketch, "E1007", {"start": v(-22.05, -13) * mm, "end": v(-22.05, -16.5) * mm});
            skLineSegment(sketch, "E1008", {"start": v(-22.05, -16.5) * mm, "end": v(-21.25, -16.5) * mm});
            skLineSegment(sketch, "E1009", {"start": v(-21.25, -16.5) * mm, "end": v(-21.25, -21.5) * mm});
            skLineSegment(sketch, "E1010", {"start": v(-21.25, -21.5) * mm, "end": v(-22.05, -21.5) * mm});
            skLineSegment(sketch, "E1011", {"start": v(-22.05, -21.5) * mm, "end": v(-22.05, -25) * mm});
            skLineSegment(sketch, "E1012", {"start": v(-22.05, -25) * mm, "end": v(-21.25, -25) * mm});
            skLineSegment(sketch, "E1013", {"start": v(-21.25, -25) * mm, "end": v(-21.25, -26) * mm});
            skLineSegment(sketch, "E1014", {"start": v(-21.25, -26) * mm, "end": v(-7.25, -26) * mm});
            skLineSegment(sketch, "E1015", {"start": v(-7.25, -26) * mm, "end": v(-7.25, -25) * mm});
            skLineSegment(sketch, "E1016", {"start": v(11.75, -25) * mm, "end": v(12.55, -25) * mm});
            skLineSegment(sketch, "E1017", {"start": v(12.55, -25) * mm, "end": v(12.55, -21.5) * mm});
            skLineSegment(sketch, "E1018", {"start": v(12.55, -21.5) * mm, "end": v(11.75, -21.5) * mm});
            skLineSegment(sketch, "E1019", {"start": v(11.75, -21.5) * mm, "end": v(11.75, -16.5) * mm});
            skLineSegment(sketch, "E1020", {"start": v(11.75, -16.5) * mm, "end": v(12.55, -16.5) * mm});
            skLineSegment(sketch, "E1021", {"start": v(12.55, -16.5) * mm, "end": v(12.55, -13) * mm});
            skLineSegment(sketch, "E1022", {"start": v(12.55, -13) * mm, "end": v(11.75, -13) * mm});
            skLineSegment(sketch, "E1023", {"start": v(11.75, -13) * mm, "end": v(11.75, -12) * mm});
            skLineSegment(sketch, "E1024", {"start": v(11.75, -12) * mm, "end": v(-2.25, -12) * mm});
            skLineSegment(sketch, "E1025", {"start": v(-2.25, -12) * mm, "end": v(-2.25, -13) * mm});
            skLineSegment(sketch, "E1026", {"start": v(-2.25, -13) * mm, "end": v(-3.05, -13) * mm});
            skLineSegment(sketch, "E1027", {"start": v(-3.05, -13) * mm, "end": v(-3.05, -16.5) * mm});
            skLineSegment(sketch, "E1028", {"start": v(-3.05, -16.5) * mm, "end": v(-2.25, -16.5) * mm});
            skLineSegment(sketch, "E1029", {"start": v(-2.25, -16.5) * mm, "end": v(-2.25, -21.5) * mm});
            skLineSegment(sketch, "E1030", {"start": v(-2.25, -21.5) * mm, "end": v(-3.05, -21.5) * mm});
            skLineSegment(sketch, "E1031", {"start": v(-3.05, -21.5) * mm, "end": v(-3.05, -25) * mm});
            skLineSegment(sketch, "E1032", {"start": v(-3.05, -25) * mm, "end": v(-2.25, -25) * mm});
            skLineSegment(sketch, "E1033", {"start": v(-2.25, -25) * mm, "end": v(-2.25, -26) * mm});
            skLineSegment(sketch, "E1034", {"start": v(-2.25, -26) * mm, "end": v(11.75, -26) * mm});
            skLineSegment(sketch, "E1035", {"start": v(11.75, -26) * mm, "end": v(11.75, -25) * mm});
            skLineSegment(sketch, "E1036", {"start": v(30.75, -25) * mm, "end": v(31.55, -25) * mm});
            skLineSegment(sketch, "E1037", {"start": v(31.55, -25) * mm, "end": v(31.55, -21.5) * mm});
            skLineSegment(sketch, "E1038", {"start": v(31.55, -21.5) * mm, "end": v(30.75, -21.5) * mm});
            skLineSegment(sketch, "E1039", {"start": v(30.75, -21.5) * mm, "end": v(30.75, -16.5) * mm});
            skLineSegment(sketch, "E1040", {"start": v(30.75, -16.5) * mm, "end": v(31.55, -16.5) * mm});
            skLineSegment(sketch, "E1041", {"start": v(31.55, -16.5) * mm, "end": v(31.55, -13) * mm});
            skLineSegment(sketch, "E1042", {"start": v(31.55, -13) * mm, "end": v(30.75, -13) * mm});
            skLineSegment(sketch, "E1043", {"start": v(30.75, -13) * mm, "end": v(30.75, -12) * mm});
            skLineSegment(sketch, "E1044", {"start": v(30.75, -12) * mm, "end": v(16.75, -12) * mm});
            skLineSegment(sketch, "E1045", {"start": v(16.75, -12) * mm, "end": v(16.75, -13) * mm});
            skLineSegment(sketch, "E1046", {"start": v(16.75, -13) * mm, "end": v(15.95, -13) * mm});
            skLineSegment(sketch, "E1047", {"start": v(15.95, -13) * mm, "end": v(15.95, -16.5) * mm});
            skLineSegment(sketch, "E1048", {"start": v(15.95, -16.5) * mm, "end": v(16.75, -16.5) * mm});
            skLineSegment(sketch, "E1049", {"start": v(16.75, -16.5) * mm, "end": v(16.75, -21.5) * mm});
            skLineSegment(sketch, "E1050", {"start": v(16.75, -21.5) * mm, "end": v(15.95, -21.5) * mm});
            skLineSegment(sketch, "E1051", {"start": v(15.95, -21.5) * mm, "end": v(15.95, -25) * mm});
            skLineSegment(sketch, "E1052", {"start": v(15.95, -25) * mm, "end": v(16.75, -25) * mm});
            skLineSegment(sketch, "E1053", {"start": v(16.75, -25) * mm, "end": v(16.75, -26) * mm});
            skLineSegment(sketch, "E1054", {"start": v(16.75, -26) * mm, "end": v(30.75, -26) * mm});
            skLineSegment(sketch, "E1055", {"start": v(30.75, -26) * mm, "end": v(30.75, -25) * mm});
            skLineSegment(sketch, "E1056", {"start": v(49.75, -25) * mm, "end": v(50.55, -25) * mm});
            skLineSegment(sketch, "E1057", {"start": v(50.55, -25) * mm, "end": v(50.55, -21.5) * mm});
            skLineSegment(sketch, "E1058", {"start": v(50.55, -21.5) * mm, "end": v(49.75, -21.5) * mm});
            skLineSegment(sketch, "E1059", {"start": v(49.75, -21.5) * mm, "end": v(49.75, -16.5) * mm});
            skLineSegment(sketch, "E1060", {"start": v(49.75, -16.5) * mm, "end": v(50.55, -16.5) * mm});
            skLineSegment(sketch, "E1061", {"start": v(50.55, -16.5) * mm, "end": v(50.55, -13) * mm});
            skLineSegment(sketch, "E1062", {"start": v(50.55, -13) * mm, "end": v(49.75, -13) * mm});
            skLineSegment(sketch, "E1063", {"start": v(49.75, -13) * mm, "end": v(49.75, -12) * mm});
            skLineSegment(sketch, "E1064", {"start": v(49.75, -12) * mm, "end": v(35.75, -12) * mm});
            skLineSegment(sketch, "E1065", {"start": v(35.75, -12) * mm, "end": v(35.75, -13) * mm});
            skLineSegment(sketch, "E1066", {"start": v(35.75, -13) * mm, "end": v(34.95, -13) * mm});
            skLineSegment(sketch, "E1067", {"start": v(34.95, -13) * mm, "end": v(34.95, -16.5) * mm});
            skLineSegment(sketch, "E1068", {"start": v(34.95, -16.5) * mm, "end": v(35.75, -16.5) * mm});
            skLineSegment(sketch, "E1069", {"start": v(35.75, -16.5) * mm, "end": v(35.75, -21.5) * mm});
            skLineSegment(sketch, "E1070", {"start": v(35.75, -21.5) * mm, "end": v(34.95, -21.5) * mm});
            skLineSegment(sketch, "E1071", {"start": v(34.95, -21.5) * mm, "end": v(34.95, -25) * mm});
            skLineSegment(sketch, "E1072", {"start": v(34.95, -25) * mm, "end": v(35.75, -25) * mm});
            skLineSegment(sketch, "E1073", {"start": v(35.75, -25) * mm, "end": v(35.75, -26) * mm});
            skLineSegment(sketch, "E1074", {"start": v(35.75, -26) * mm, "end": v(49.75, -26) * mm});
            skLineSegment(sketch, "E1075", {"start": v(49.75, -26) * mm, "end": v(49.75, -25) * mm});
            skLineSegment(sketch, "E1076", {"start": v(68.75, -25) * mm, "end": v(69.55, -25) * mm});
            skLineSegment(sketch, "E1077", {"start": v(69.55, -25) * mm, "end": v(69.55, -21.5) * mm});
            skLineSegment(sketch, "E1078", {"start": v(69.55, -21.5) * mm, "end": v(68.75, -21.5) * mm});
            skLineSegment(sketch, "E1079", {"start": v(68.75, -21.5) * mm, "end": v(68.75, -16.5) * mm});
            skLineSegment(sketch, "E1080", {"start": v(68.75, -16.5) * mm, "end": v(69.55, -16.5) * mm});
            skLineSegment(sketch, "E1081", {"start": v(69.55, -16.5) * mm, "end": v(69.55, -13) * mm});
            skLineSegment(sketch, "E1082", {"start": v(69.55, -13) * mm, "end": v(68.75, -13) * mm});
            skLineSegment(sketch, "E1083", {"start": v(68.75, -13) * mm, "end": v(68.75, -12) * mm});
            skLineSegment(sketch, "E1084", {"start": v(68.75, -12) * mm, "end": v(54.75, -12) * mm});
            skLineSegment(sketch, "E1085", {"start": v(54.75, -12) * mm, "end": v(54.75, -13) * mm});
            skLineSegment(sketch, "E1086", {"start": v(54.75, -13) * mm, "end": v(53.95, -13) * mm});
            skLineSegment(sketch, "E1087", {"start": v(53.95, -13) * mm, "end": v(53.95, -16.5) * mm});
            skLineSegment(sketch, "E1088", {"start": v(53.95, -16.5) * mm, "end": v(54.75, -16.5) * mm});
            skLineSegment(sketch, "E1089", {"start": v(54.75, -16.5) * mm, "end": v(54.75, -21.5) * mm});
            skLineSegment(sketch, "E1090", {"start": v(54.75, -21.5) * mm, "end": v(53.95, -21.5) * mm});
            skLineSegment(sketch, "E1091", {"start": v(53.95, -21.5) * mm, "end": v(53.95, -25) * mm});
            skLineSegment(sketch, "E1092", {"start": v(53.95, -25) * mm, "end": v(54.75, -25) * mm});
            skLineSegment(sketch, "E1093", {"start": v(54.75, -25) * mm, "end": v(54.75, -26) * mm});
            skLineSegment(sketch, "E1094", {"start": v(54.75, -26) * mm, "end": v(68.75, -26) * mm});
            skLineSegment(sketch, "E1095", {"start": v(68.75, -26) * mm, "end": v(68.75, -25) * mm});
            skLineSegment(sketch, "E1096", {"start": v(87.75, -25) * mm, "end": v(88.55, -25) * mm});
            skLineSegment(sketch, "E1097", {"start": v(88.55, -25) * mm, "end": v(88.55, -21.5) * mm});
            skLineSegment(sketch, "E1098", {"start": v(88.55, -21.5) * mm, "end": v(87.75, -21.5) * mm});
            skLineSegment(sketch, "E1099", {"start": v(87.75, -21.5) * mm, "end": v(87.75, -16.5) * mm});
            skLineSegment(sketch, "E1100", {"start": v(87.75, -16.5) * mm, "end": v(88.55, -16.5) * mm});
            skLineSegment(sketch, "E1101", {"start": v(88.55, -16.5) * mm, "end": v(88.55, -13) * mm});
            skLineSegment(sketch, "E1102", {"start": v(88.55, -13) * mm, "end": v(87.75, -13) * mm});
            skLineSegment(sketch, "E1103", {"start": v(87.75, -13) * mm, "end": v(87.75, -12) * mm});
            skLineSegment(sketch, "E1104", {"start": v(87.75, -12) * mm, "end": v(73.75, -12) * mm});
            skLineSegment(sketch, "E1105", {"start": v(73.75, -12) * mm, "end": v(73.75, -13) * mm});
            skLineSegment(sketch, "E1106", {"start": v(73.75, -13) * mm, "end": v(72.95, -13) * mm});
            skLineSegment(sketch, "E1107", {"start": v(72.95, -13) * mm, "end": v(72.95, -16.5) * mm});
            skLineSegment(sketch, "E1108", {"start": v(72.95, -16.5) * mm, "end": v(73.75, -16.5) * mm});
            skLineSegment(sketch, "E1109", {"start": v(73.75, -16.5) * mm, "end": v(73.75, -21.5) * mm});
            skLineSegment(sketch, "E1110", {"start": v(73.75, -21.5) * mm, "end": v(72.95, -21.5) * mm});
            skLineSegment(sketch, "E1111", {"start": v(72.95, -21.5) * mm, "end": v(72.95, -25) * mm});
            skLineSegment(sketch, "E1112", {"start": v(72.95, -25) * mm, "end": v(73.75, -25) * mm});
            skLineSegment(sketch, "E1113", {"start": v(73.75, -25) * mm, "end": v(73.75, -26) * mm});
            skLineSegment(sketch, "E1114", {"start": v(73.75, -26) * mm, "end": v(87.75, -26) * mm});
            skLineSegment(sketch, "E1115", {"start": v(87.75, -26) * mm, "end": v(87.75, -25) * mm});
            skLineSegment(sketch, "E1116", {"start": v(105.97, -25.77) * mm, "end": v(107.8, -25.77) * mm});
            skLineSegment(sketch, "E1117", {"start": v(107.8, -25.77) * mm, "end": v(107.8, -24.97) * mm});
            skLineSegment(sketch, "E1118", {"start": v(107.8, -24.97) * mm, "end": v(108.57, -24.97) * mm});
            skLineSegment(sketch, "E1119", {"start": v(108.57, -24.97) * mm, "end": v(108.57, -25) * mm});
            skLineSegment(sketch, "E1120", {"start": v(108.57, -25) * mm, "end": v(109.38, -25) * mm});
            skLineSegment(sketch, "E1121", {"start": v(109.38, -25) * mm, "end": v(109.38, -26) * mm});
            skLineSegment(sketch, "E1122", {"start": v(109.38, -26) * mm, "end": v(123.38, -26) * mm});
            skLineSegment(sketch, "E1123", {"start": v(123.38, -26) * mm, "end": v(123.38, -25) * mm});
            skLineSegment(sketch, "E1124", {"start": v(123.38, -25) * mm, "end": v(124.18, -25) * mm});
            skLineSegment(sketch, "E1125", {"start": v(124.18, -25) * mm, "end": v(124.18, -24.97) * mm});
            skLineSegment(sketch, "E1126", {"start": v(124.18, -24.97) * mm, "end": v(124.95, -24.97) * mm});
            skLineSegment(sketch, "E1127", {"start": v(124.95, -24.97) * mm, "end": v(124.95, -25.77) * mm});
            skLineSegment(sketch, "E1128", {"start": v(124.95, -25.77) * mm, "end": v(126.77, -25.77) * mm});
            skLineSegment(sketch, "E1129", {"start": v(126.77, -25.77) * mm, "end": v(126.77, -26.97) * mm});
            skLineSegment(sketch, "E1130", {"start": v(126.77, -26.97) * mm, "end": v(129.77, -26.97) * mm});
            skLineSegment(sketch, "E1131", {"start": v(129.77, -26.97) * mm, "end": v(129.77, -25.77) * mm});
            skLineSegment(sketch, "E1132", {"start": v(129.77, -25.77) * mm, "end": v(131.6, -25.77) * mm});
            skLineSegment(sketch, "E1133", {"start": v(131.6, -25.77) * mm, "end": v(131.6, -19.5) * mm});
            skLineSegment(sketch, "E1134", {"start": v(131.6, -19.5) * mm, "end": v(132.48, -19.5) * mm});
            skLineSegment(sketch, "E1135", {"start": v(132.48, -19.5) * mm, "end": v(132.48, -16.7) * mm});
            skLineSegment(sketch, "E1136", {"start": v(132.48, -16.7) * mm, "end": v(131.6, -16.7) * mm});
            skLineSegment(sketch, "E1137", {"start": v(131.6, -16.7) * mm, "end": v(131.6, -13.47) * mm});
            skLineSegment(sketch, "E1138", {"start": v(131.6, -13.47) * mm, "end": v(124.95, -13.47) * mm});
            skLineSegment(sketch, "E1139", {"start": v(124.95, -13.47) * mm, "end": v(124.95, -14.27) * mm});
            skLineSegment(sketch, "E1140", {"start": v(124.95, -14.27) * mm, "end": v(124.18, -14.27) * mm});
            skLineSegment(sketch, "E1141", {"start": v(124.18, -14.27) * mm, "end": v(124.18, -13) * mm});
            skLineSegment(sketch, "E1142", {"start": v(124.18, -13) * mm, "end": v(123.38, -13) * mm});
            skLineSegment(sketch, "E1143", {"start": v(123.38, -13) * mm, "end": v(123.38, -12) * mm});
            skLineSegment(sketch, "E1144", {"start": v(123.38, -12) * mm, "end": v(109.38, -12) * mm});
            skLineSegment(sketch, "E1145", {"start": v(109.38, -12) * mm, "end": v(109.38, -13) * mm});
            skLineSegment(sketch, "E1146", {"start": v(109.38, -13) * mm, "end": v(108.57, -13) * mm});
            skLineSegment(sketch, "E1147", {"start": v(108.57, -13) * mm, "end": v(108.57, -14.27) * mm});
            skLineSegment(sketch, "E1148", {"start": v(108.57, -14.27) * mm, "end": v(107.8, -14.27) * mm});
            skLineSegment(sketch, "E1149", {"start": v(107.8, -14.27) * mm, "end": v(107.8, -13.47) * mm});
            skLineSegment(sketch, "E1150", {"start": v(107.8, -13.47) * mm, "end": v(101.15, -13.47) * mm});
            skLineSegment(sketch, "E1151", {"start": v(101.15, -13.47) * mm, "end": v(101.15, -16.7) * mm});
            skLineSegment(sketch, "E1152", {"start": v(101.15, -16.7) * mm, "end": v(100.28, -16.7) * mm});
            skLineSegment(sketch, "E1153", {"start": v(100.28, -16.7) * mm, "end": v(100.28, -19.5) * mm});
            skLineSegment(sketch, "E1154", {"start": v(100.28, -19.5) * mm, "end": v(101.15, -19.5) * mm});
            skLineSegment(sketch, "E1155", {"start": v(101.15, -19.5) * mm, "end": v(101.15, -25.77) * mm});
            skLineSegment(sketch, "E1156", {"start": v(101.15, -25.77) * mm, "end": v(102.97, -25.77) * mm});
            skLineSegment(sketch, "E1157", {"start": v(102.97, -25.77) * mm, "end": v(102.97, -26.97) * mm});
            skLineSegment(sketch, "E1158", {"start": v(102.97, -26.97) * mm, "end": v(105.97, -26.97) * mm});
            skLineSegment(sketch, "E1159", {"start": v(105.97, -26.97) * mm, "end": v(105.97, -25.77) * mm});
            skLineSegment(sketch, "E1160", {"start": v(-123.62, -44) * mm, "end": v(-122.83, -44) * mm});
            skLineSegment(sketch, "E1161", {"start": v(-122.83, -44) * mm, "end": v(-122.83, -40.5) * mm});
            skLineSegment(sketch, "E1162", {"start": v(-122.83, -40.5) * mm, "end": v(-123.62, -40.5) * mm});
            skLineSegment(sketch, "E1163", {"start": v(-123.62, -40.5) * mm, "end": v(-123.62, -35.5) * mm});
            skLineSegment(sketch, "E1164", {"start": v(-123.62, -35.5) * mm, "end": v(-122.83, -35.5) * mm});
            skLineSegment(sketch, "E1165", {"start": v(-122.83, -35.5) * mm, "end": v(-122.83, -32) * mm});
            skLineSegment(sketch, "E1166", {"start": v(-122.83, -32) * mm, "end": v(-123.62, -32) * mm});
            skLineSegment(sketch, "E1167", {"start": v(-123.62, -32) * mm, "end": v(-123.62, -31) * mm});
            skLineSegment(sketch, "E1168", {"start": v(-123.62, -31) * mm, "end": v(-137.62, -31) * mm});
            skLineSegment(sketch, "E1169", {"start": v(-137.62, -31) * mm, "end": v(-137.62, -32) * mm});
            skLineSegment(sketch, "E1170", {"start": v(-137.62, -32) * mm, "end": v(-138.43, -32) * mm});
            skLineSegment(sketch, "E1171", {"start": v(-138.43, -32) * mm, "end": v(-138.43, -35.5) * mm});
            skLineSegment(sketch, "E1172", {"start": v(-138.43, -35.5) * mm, "end": v(-137.62, -35.5) * mm});
            skLineSegment(sketch, "E1173", {"start": v(-137.62, -35.5) * mm, "end": v(-137.62, -40.5) * mm});
            skLineSegment(sketch, "E1174", {"start": v(-137.62, -40.5) * mm, "end": v(-138.43, -40.5) * mm});
            skLineSegment(sketch, "E1175", {"start": v(-138.43, -40.5) * mm, "end": v(-138.43, -44) * mm});
            skLineSegment(sketch, "E1176", {"start": v(-138.43, -44) * mm, "end": v(-137.62, -44) * mm});
            skLineSegment(sketch, "E1177", {"start": v(-137.62, -44) * mm, "end": v(-137.62, -45) * mm});
            skLineSegment(sketch, "E1178", {"start": v(-137.62, -45) * mm, "end": v(-123.62, -45) * mm});
            skLineSegment(sketch, "E1179", {"start": v(-123.62, -45) * mm, "end": v(-123.62, -44) * mm});
            skLineSegment(sketch, "E1180", {"start": v(-99.88, -44) * mm, "end": v(-99.08, -44) * mm});
            skLineSegment(sketch, "E1181", {"start": v(-99.08, -44) * mm, "end": v(-99.08, -40.5) * mm});
            skLineSegment(sketch, "E1182", {"start": v(-99.08, -40.5) * mm, "end": v(-99.88, -40.5) * mm});
            skLineSegment(sketch, "E1183", {"start": v(-99.88, -40.5) * mm, "end": v(-99.88, -35.5) * mm});
            skLineSegment(sketch, "E1184", {"start": v(-99.88, -35.5) * mm, "end": v(-99.08, -35.5) * mm});
            skLineSegment(sketch, "E1185", {"start": v(-99.08, -35.5) * mm, "end": v(-99.08, -32) * mm});
            skLineSegment(sketch, "E1186", {"start": v(-99.08, -32) * mm, "end": v(-99.88, -32) * mm});
            skLineSegment(sketch, "E1187", {"start": v(-99.88, -32) * mm, "end": v(-99.88, -31) * mm});
            skLineSegment(sketch, "E1188", {"start": v(-99.88, -31) * mm, "end": v(-113.88, -31) * mm});
            skLineSegment(sketch, "E1189", {"start": v(-113.88, -31) * mm, "end": v(-113.88, -32) * mm});
            skLineSegment(sketch, "E1190", {"start": v(-113.88, -32) * mm, "end": v(-114.67, -32) * mm});
            skLineSegment(sketch, "E1191", {"start": v(-114.67, -32) * mm, "end": v(-114.67, -35.5) * mm});
            skLineSegment(sketch, "E1192", {"start": v(-114.67, -35.5) * mm, "end": v(-113.88, -35.5) * mm});
            skLineSegment(sketch, "E1193", {"start": v(-113.88, -35.5) * mm, "end": v(-113.88, -40.5) * mm});
            skLineSegment(sketch, "E1194", {"start": v(-113.88, -40.5) * mm, "end": v(-114.67, -40.5) * mm});
            skLineSegment(sketch, "E1195", {"start": v(-114.67, -40.5) * mm, "end": v(-114.67, -44) * mm});
            skLineSegment(sketch, "E1196", {"start": v(-114.67, -44) * mm, "end": v(-113.88, -44) * mm});
            skLineSegment(sketch, "E1197", {"start": v(-113.88, -44) * mm, "end": v(-113.88, -45) * mm});
            skLineSegment(sketch, "E1198", {"start": v(-113.88, -45) * mm, "end": v(-99.88, -45) * mm});
            skLineSegment(sketch, "E1199", {"start": v(-99.88, -45) * mm, "end": v(-99.88, -44) * mm});
            skLineSegment(sketch, "E1200", {"start": v(-76.12, -44) * mm, "end": v(-75.33, -44) * mm});
            skLineSegment(sketch, "E1201", {"start": v(-75.33, -44) * mm, "end": v(-75.33, -40.5) * mm});
            skLineSegment(sketch, "E1202", {"start": v(-75.33, -40.5) * mm, "end": v(-76.12, -40.5) * mm});
            skLineSegment(sketch, "E1203", {"start": v(-76.12, -40.5) * mm, "end": v(-76.12, -35.5) * mm});
            skLineSegment(sketch, "E1204", {"start": v(-76.12, -35.5) * mm, "end": v(-75.33, -35.5) * mm});
            skLineSegment(sketch, "E1205", {"start": v(-75.33, -35.5) * mm, "end": v(-75.33, -32) * mm});
            skLineSegment(sketch, "E1206", {"start": v(-75.33, -32) * mm, "end": v(-76.12, -32) * mm});
            skLineSegment(sketch, "E1207", {"start": v(-76.12, -32) * mm, "end": v(-76.12, -31) * mm});
            skLineSegment(sketch, "E1208", {"start": v(-76.12, -31) * mm, "end": v(-90.12, -31) * mm});
            skLineSegment(sketch, "E1209", {"start": v(-90.12, -31) * mm, "end": v(-90.12, -32) * mm});
            skLineSegment(sketch, "E1210", {"start": v(-90.12, -32) * mm, "end": v(-90.93, -32) * mm});
            skLineSegment(sketch, "E1211", {"start": v(-90.93, -32) * mm, "end": v(-90.93, -35.5) * mm});
            skLineSegment(sketch, "E1212", {"start": v(-90.93, -35.5) * mm, "end": v(-90.12, -35.5) * mm});
            skLineSegment(sketch, "E1213", {"start": v(-90.12, -35.5) * mm, "end": v(-90.12, -40.5) * mm});
            skLineSegment(sketch, "E1214", {"start": v(-90.12, -40.5) * mm, "end": v(-90.93, -40.5) * mm});
            skLineSegment(sketch, "E1215", {"start": v(-90.93, -40.5) * mm, "end": v(-90.93, -44) * mm});
            skLineSegment(sketch, "E1216", {"start": v(-90.93, -44) * mm, "end": v(-90.12, -44) * mm});
            skLineSegment(sketch, "E1217", {"start": v(-90.12, -44) * mm, "end": v(-90.12, -45) * mm});
            skLineSegment(sketch, "E1218", {"start": v(-90.12, -45) * mm, "end": v(-76.12, -45) * mm});
            skLineSegment(sketch, "E1219", {"start": v(-76.12, -45) * mm, "end": v(-76.12, -44) * mm});
            skLineSegment(sketch, "E1220", {"start": v(-60.38, -44.77) * mm, "end": v(-58.55, -44.77) * mm});
            skLineSegment(sketch, "E1221", {"start": v(-58.55, -44.77) * mm, "end": v(-58.55, -40.3) * mm});
            skLineSegment(sketch, "E1222", {"start": v(-58.55, -40.3) * mm, "end": v(-18.87, -40.3) * mm});
            skLineSegment(sketch, "E1223", {"start": v(-18.88, -40.3) * mm, "end": v(-18.88, -40.5) * mm});
            skLineSegment(sketch, "E1224", {"start": v(-18.88, -40.5) * mm, "end": v(-19.67, -40.5) * mm});
            skLineSegment(sketch, "E1225", {"start": v(-19.67, -40.5) * mm, "end": v(-19.67, -44) * mm});
            skLineSegment(sketch, "E1226", {"start": v(-19.67, -44) * mm, "end": v(-18.88, -44) * mm});
            skLineSegment(sketch, "E1227", {"start": v(-18.88, -44) * mm, "end": v(-18.88, -45) * mm});
            skLineSegment(sketch, "E1228", {"start": v(-18.88, -45) * mm, "end": v(-4.88, -45) * mm});
            skLineSegment(sketch, "E1229", {"start": v(-4.88, -45) * mm, "end": v(-4.88, -44) * mm});
            skLineSegment(sketch, "E1230", {"start": v(-4.88, -44) * mm, "end": v(-4.07, -44) * mm});
            skLineSegment(sketch, "E1231", {"start": v(-4.07, -44) * mm, "end": v(-4.07, -40.5) * mm});
            skLineSegment(sketch, "E1232", {"start": v(-4.07, -40.5) * mm, "end": v(-4.88, -40.5) * mm});
            skLineSegment(sketch, "E1233", {"start": v(-4.88, -40.5) * mm, "end": v(-4.88, -40.3) * mm});
            skLineSegment(sketch, "E1234", {"start": v(-4.88, -40.3) * mm, "end": v(34.8, -40.3) * mm});
            skLineSegment(sketch, "E1235", {"start": v(34.8, -40.3) * mm, "end": v(34.8, -44.77) * mm});
            skLineSegment(sketch, "E1236", {"start": v(34.8, -44.77) * mm, "end": v(36.62, -44.77) * mm});
            skLineSegment(sketch, "E1237", {"start": v(36.62, -44.77) * mm, "end": v(36.62, -45.97) * mm});
            skLineSegment(sketch, "E1238", {"start": v(36.62, -45.97) * mm, "end": v(39.62, -45.97) * mm});
            skLineSegment(sketch, "E1239", {"start": v(39.62, -45.97) * mm, "end": v(39.62, -44.77) * mm});
            skLineSegment(sketch, "E1240", {"start": v(39.62, -44.77) * mm, "end": v(41.45, -44.77) * mm});
            skLineSegment(sketch, "E1241", {"start": v(41.45, -44.77) * mm, "end": v(41.45, -38.5) * mm});
            skLineSegment(sketch, "E1242", {"start": v(41.45, -38.5) * mm, "end": v(42.35, -38.5) * mm});
            skLineSegment(sketch, "E1243", {"start": v(42.35, -38.5) * mm, "end": v(42.35, -35.7) * mm});
            skLineSegment(sketch, "E1244", {"start": v(42.35, -35.7) * mm, "end": v(41.45, -35.7) * mm});
            skLineSegment(sketch, "E1245", {"start": v(41.45, -35.7) * mm, "end": v(41.45, -32.47) * mm});
            skLineSegment(sketch, "E1246", {"start": v(41.45, -32.47) * mm, "end": v(34.8, -32.47) * mm});
            skLineSegment(sketch, "E1247", {"start": v(34.8, -32.47) * mm, "end": v(34.8, -35.7) * mm});
            skLineSegment(sketch, "E1248", {"start": v(34.8, -35.7) * mm, "end": v(-4.87, -35.7) * mm});
            skLineSegment(sketch, "E1249", {"start": v(-4.88, -35.7) * mm, "end": v(-4.88, -35.5) * mm});
            skLineSegment(sketch, "E1250", {"start": v(-4.88, -35.5) * mm, "end": v(-4.07, -35.5) * mm});
            skLineSegment(sketch, "E1251", {"start": v(-4.07, -35.5) * mm, "end": v(-4.07, -32) * mm});
            skLineSegment(sketch, "E1252", {"start": v(-4.07, -32) * mm, "end": v(-4.88, -32) * mm});
            skLineSegment(sketch, "E1253", {"start": v(-4.88, -32) * mm, "end": v(-4.88, -31) * mm});
            skLineSegment(sketch, "E1254", {"start": v(-4.88, -31) * mm, "end": v(-18.88, -31) * mm});
            skLineSegment(sketch, "E1255", {"start": v(-18.88, -31) * mm, "end": v(-18.88, -32) * mm});
            skLineSegment(sketch, "E1256", {"start": v(-18.88, -32) * mm, "end": v(-19.67, -32) * mm});
            skLineSegment(sketch, "E1257", {"start": v(-19.67, -32) * mm, "end": v(-19.67, -35.5) * mm});
            skLineSegment(sketch, "E1258", {"start": v(-19.67, -35.5) * mm, "end": v(-18.88, -35.5) * mm});
            skLineSegment(sketch, "E1259", {"start": v(-18.88, -35.5) * mm, "end": v(-18.88, -35.7) * mm});
            skLineSegment(sketch, "E1260", {"start": v(-18.88, -35.7) * mm, "end": v(-58.55, -35.7) * mm});
            skLineSegment(sketch, "E1261", {"start": v(-58.55, -35.7) * mm, "end": v(-58.55, -32.47) * mm});
            skLineSegment(sketch, "E1262", {"start": v(-58.55, -32.47) * mm, "end": v(-65.2, -32.47) * mm});
            skLineSegment(sketch, "E1263", {"start": v(-65.2, -32.47) * mm, "end": v(-65.2, -35.7) * mm});
            skLineSegment(sketch, "E1264", {"start": v(-65.2, -35.7) * mm, "end": v(-66.1, -35.7) * mm});
            skLineSegment(sketch, "E1265", {"start": v(-66.1, -35.7) * mm, "end": v(-66.1, -38.5) * mm});
            skLineSegment(sketch, "E1266", {"start": v(-66.1, -38.5) * mm, "end": v(-65.2, -38.5) * mm});
            skLineSegment(sketch, "E1267", {"start": v(-65.2, -38.5) * mm, "end": v(-65.2, -44.77) * mm});
            skLineSegment(sketch, "E1268", {"start": v(-65.2, -44.77) * mm, "end": v(-63.38, -44.77) * mm});
            skLineSegment(sketch, "E1269", {"start": v(-63.38, -44.77) * mm, "end": v(-63.38, -45.97) * mm});
            skLineSegment(sketch, "E1270", {"start": v(-63.38, -45.97) * mm, "end": v(-60.38, -45.97) * mm});
            skLineSegment(sketch, "E1271", {"start": v(-60.38, -45.97) * mm, "end": v(-60.38, -44.77) * mm});
            skLineSegment(sketch, "E1272", {"start": v(66.38, -44) * mm, "end": v(67.18, -44) * mm});
            skLineSegment(sketch, "E1273", {"start": v(67.18, -44) * mm, "end": v(67.18, -40.5) * mm});
            skLineSegment(sketch, "E1274", {"start": v(67.18, -40.5) * mm, "end": v(66.38, -40.5) * mm});
            skLineSegment(sketch, "E1275", {"start": v(66.38, -40.5) * mm, "end": v(66.38, -35.5) * mm});
            skLineSegment(sketch, "E1276", {"start": v(66.38, -35.5) * mm, "end": v(67.18, -35.5) * mm});
            skLineSegment(sketch, "E1277", {"start": v(67.18, -35.5) * mm, "end": v(67.18, -32) * mm});
            skLineSegment(sketch, "E1278", {"start": v(67.18, -32) * mm, "end": v(66.38, -32) * mm});
            skLineSegment(sketch, "E1279", {"start": v(66.38, -32) * mm, "end": v(66.38, -31) * mm});
            skLineSegment(sketch, "E1280", {"start": v(66.38, -31) * mm, "end": v(52.38, -31) * mm});
            skLineSegment(sketch, "E1281", {"start": v(52.38, -31) * mm, "end": v(52.38, -32) * mm});
            skLineSegment(sketch, "E1282", {"start": v(52.38, -32) * mm, "end": v(51.57, -32) * mm});
            skLineSegment(sketch, "E1283", {"start": v(51.57, -32) * mm, "end": v(51.57, -35.5) * mm});
            skLineSegment(sketch, "E1284", {"start": v(51.57, -35.5) * mm, "end": v(52.38, -35.5) * mm});
            skLineSegment(sketch, "E1285", {"start": v(52.38, -35.5) * mm, "end": v(52.38, -40.5) * mm});
            skLineSegment(sketch, "E1286", {"start": v(52.38, -40.5) * mm, "end": v(51.57, -40.5) * mm});
            skLineSegment(sketch, "E1287", {"start": v(51.57, -40.5) * mm, "end": v(51.57, -44) * mm});
            skLineSegment(sketch, "E1288", {"start": v(51.57, -44) * mm, "end": v(52.38, -44) * mm});
            skLineSegment(sketch, "E1289", {"start": v(52.38, -44) * mm, "end": v(52.38, -45) * mm});
            skLineSegment(sketch, "E1290", {"start": v(52.38, -45) * mm, "end": v(66.38, -45) * mm});
            skLineSegment(sketch, "E1291", {"start": v(66.38, -45) * mm, "end": v(66.38, -44) * mm});
            skLineSegment(sketch, "E1292", {"start": v(90.12, -44) * mm, "end": v(90.93, -44) * mm});
            skLineSegment(sketch, "E1293", {"start": v(90.93, -44) * mm, "end": v(90.93, -40.5) * mm});
            skLineSegment(sketch, "E1294", {"start": v(90.93, -40.5) * mm, "end": v(90.12, -40.5) * mm});
            skLineSegment(sketch, "E1295", {"start": v(90.12, -40.5) * mm, "end": v(90.12, -35.5) * mm});
            skLineSegment(sketch, "E1296", {"start": v(90.12, -35.5) * mm, "end": v(90.93, -35.5) * mm});
            skLineSegment(sketch, "E1297", {"start": v(90.93, -35.5) * mm, "end": v(90.93, -32) * mm});
            skLineSegment(sketch, "E1298", {"start": v(90.93, -32) * mm, "end": v(90.12, -32) * mm});
            skLineSegment(sketch, "E1299", {"start": v(90.12, -32) * mm, "end": v(90.12, -31) * mm});
            skLineSegment(sketch, "E1300", {"start": v(90.12, -31) * mm, "end": v(76.12, -31) * mm});
            skLineSegment(sketch, "E1301", {"start": v(76.12, -31) * mm, "end": v(76.12, -32) * mm});
            skLineSegment(sketch, "E1302", {"start": v(76.12, -32) * mm, "end": v(75.32, -32) * mm});
            skLineSegment(sketch, "E1303", {"start": v(75.32, -32) * mm, "end": v(75.32, -35.5) * mm});
            skLineSegment(sketch, "E1304", {"start": v(75.32, -35.5) * mm, "end": v(76.12, -35.5) * mm});
            skLineSegment(sketch, "E1305", {"start": v(76.12, -35.5) * mm, "end": v(76.12, -40.5) * mm});
            skLineSegment(sketch, "E1306", {"start": v(76.12, -40.5) * mm, "end": v(75.32, -40.5) * mm});
            skLineSegment(sketch, "E1307", {"start": v(75.32, -40.5) * mm, "end": v(75.32, -44) * mm});
            skLineSegment(sketch, "E1308", {"start": v(75.32, -44) * mm, "end": v(76.12, -44) * mm});
            skLineSegment(sketch, "E1309", {"start": v(76.12, -44) * mm, "end": v(76.12, -45) * mm});
            skLineSegment(sketch, "E1310", {"start": v(76.12, -45) * mm, "end": v(90.12, -45) * mm});
            skLineSegment(sketch, "E1311", {"start": v(90.12, -45) * mm, "end": v(90.12, -44) * mm});
            skLineSegment(sketch, "E1312", {"start": v(113.88, -44) * mm, "end": v(114.68, -44) * mm});
            skLineSegment(sketch, "E1313", {"start": v(114.68, -44) * mm, "end": v(114.68, -40.5) * mm});
            skLineSegment(sketch, "E1314", {"start": v(114.68, -40.5) * mm, "end": v(113.88, -40.5) * mm});
            skLineSegment(sketch, "E1315", {"start": v(113.88, -40.5) * mm, "end": v(113.88, -35.5) * mm});
            skLineSegment(sketch, "E1316", {"start": v(113.88, -35.5) * mm, "end": v(114.68, -35.5) * mm});
            skLineSegment(sketch, "E1317", {"start": v(114.68, -35.5) * mm, "end": v(114.68, -32) * mm});
            skLineSegment(sketch, "E1318", {"start": v(114.68, -32) * mm, "end": v(113.88, -32) * mm});
            skLineSegment(sketch, "E1319", {"start": v(113.88, -32) * mm, "end": v(113.88, -31) * mm});
            skLineSegment(sketch, "E1320", {"start": v(113.88, -31) * mm, "end": v(99.88, -31) * mm});
            skLineSegment(sketch, "E1321", {"start": v(99.88, -31) * mm, "end": v(99.88, -32) * mm});
            skLineSegment(sketch, "E1322", {"start": v(99.88, -32) * mm, "end": v(99.08, -32) * mm});
            skLineSegment(sketch, "E1323", {"start": v(99.08, -32) * mm, "end": v(99.08, -35.5) * mm});
            skLineSegment(sketch, "E1324", {"start": v(99.08, -35.5) * mm, "end": v(99.88, -35.5) * mm});
            skLineSegment(sketch, "E1325", {"start": v(99.88, -35.5) * mm, "end": v(99.88, -40.5) * mm});
            skLineSegment(sketch, "E1326", {"start": v(99.88, -40.5) * mm, "end": v(99.08, -40.5) * mm});
            skLineSegment(sketch, "E1327", {"start": v(99.08, -40.5) * mm, "end": v(99.08, -44) * mm});
            skLineSegment(sketch, "E1328", {"start": v(99.08, -44) * mm, "end": v(99.88, -44) * mm});
            skLineSegment(sketch, "E1329", {"start": v(99.88, -44) * mm, "end": v(99.88, -45) * mm});
            skLineSegment(sketch, "E1330", {"start": v(99.88, -45) * mm, "end": v(113.88, -45) * mm});
            skLineSegment(sketch, "E1331", {"start": v(113.88, -45) * mm, "end": v(113.88, -44) * mm});
            skLineSegment(sketch, "E1332", {"start": v(137.62, -44) * mm, "end": v(138.43, -44) * mm});
            skLineSegment(sketch, "E1333", {"start": v(138.43, -44) * mm, "end": v(138.43, -40.5) * mm});
            skLineSegment(sketch, "E1334", {"start": v(138.43, -40.5) * mm, "end": v(137.62, -40.5) * mm});
            skLineSegment(sketch, "E1335", {"start": v(137.62, -40.5) * mm, "end": v(137.62, -35.5) * mm});
            skLineSegment(sketch, "E1336", {"start": v(137.62, -35.5) * mm, "end": v(138.43, -35.5) * mm});
            skLineSegment(sketch, "E1337", {"start": v(138.43, -35.5) * mm, "end": v(138.43, -32) * mm});
            skLineSegment(sketch, "E1338", {"start": v(138.43, -32) * mm, "end": v(137.62, -32) * mm});
            skLineSegment(sketch, "E1339", {"start": v(137.62, -32) * mm, "end": v(137.62, -31) * mm});
            skLineSegment(sketch, "E1340", {"start": v(137.62, -31) * mm, "end": v(123.62, -31) * mm});
            skLineSegment(sketch, "E1341", {"start": v(123.62, -31) * mm, "end": v(123.62, -32) * mm});
            skLineSegment(sketch, "E1342", {"start": v(123.62, -32) * mm, "end": v(122.82, -32) * mm});
            skLineSegment(sketch, "E1343", {"start": v(122.82, -32) * mm, "end": v(122.82, -35.5) * mm});
            skLineSegment(sketch, "E1344", {"start": v(122.82, -35.5) * mm, "end": v(123.62, -35.5) * mm});
            skLineSegment(sketch, "E1345", {"start": v(123.62, -35.5) * mm, "end": v(123.62, -40.5) * mm});
            skLineSegment(sketch, "E1346", {"start": v(123.62, -40.5) * mm, "end": v(122.82, -40.5) * mm});
            skLineSegment(sketch, "E1347", {"start": v(122.82, -40.5) * mm, "end": v(122.82, -44) * mm});
            skLineSegment(sketch, "E1348", {"start": v(122.82, -44) * mm, "end": v(123.62, -44) * mm});
            skLineSegment(sketch, "E1349", {"start": v(123.62, -44) * mm, "end": v(123.62, -45) * mm});
            skLineSegment(sketch, "E1350", {"start": v(123.62, -45) * mm, "end": v(137.62, -45) * mm});
            skLineSegment(sketch, "E1351", {"start": v(137.62, -45) * mm, "end": v(137.62, -44) * mm});
            skSolve(sketch);
        }
        {
            var Q0;
            Q0=qCreatedBy(makeId("Top.planeOp"),FACE);
            var sketch = newSketch(context, id + "F1", { "sketchPlane" : qUnion([Q0])});
            skLineSegment(sketch, "E1352", {"start": v(-145, -50) * mm, "end": v(145, -50) * mm});
            skLineSegment(sketch, "E1353", {"start": v(145, -50) * mm, "end": v(145, 50) * mm});
            skLineSegment(sketch, "E1354", {"start": v(145, 50) * mm, "end": v(-145, 50) * mm});
            skLineSegment(sketch, "E1355", {"start": v(-145, 50) * mm, "end": v(-145, -50) * mm});
            skLineSegment(sketch, "E1356", {"start": v(-126, 32) * mm, "end": v(-125.2, 32) * mm});
            skLineSegment(sketch, "E1357", {"start": v(-125.2, 32) * mm, "end": v(-125.2, 44) * mm});
            skLineSegment(sketch, "E1358", {"start": v(-125.2, 44) * mm, "end": v(-126, 44) * mm});
            skLineSegment(sketch, "E1359", {"start": v(-126, 44) * mm, "end": v(-126, 45) * mm});
            skLineSegment(sketch, "E1360", {"start": v(-126, 45) * mm, "end": v(-140, 45) * mm});
            skLineSegment(sketch, "E1361", {"start": v(-140, 45) * mm, "end": v(-140, 44) * mm});
            skLineSegment(sketch, "E1362", {"start": v(-140, 44) * mm, "end": v(-140.8, 44) * mm});
            skLineSegment(sketch, "E1363", {"start": v(-140.8, 44) * mm, "end": v(-140.8, 32) * mm});
            skLineSegment(sketch, "E1364", {"start": v(-140.8, 32) * mm, "end": v(-140, 32) * mm});
            skLineSegment(sketch, "E1365", {"start": v(-140, 32) * mm, "end": v(-140, 31) * mm});
            skLineSegment(sketch, "E1366", {"start": v(-140, 31) * mm, "end": v(-126, 31) * mm});
            skLineSegment(sketch, "E1367", {"start": v(-126, 31) * mm, "end": v(-126, 32) * mm});
            skLineSegment(sketch, "E1368", {"start": v(-107, 32) * mm, "end": v(-106.2, 32) * mm});
            skLineSegment(sketch, "E1369", {"start": v(-106.2, 32) * mm, "end": v(-106.2, 44) * mm});
            skLineSegment(sketch, "E1370", {"start": v(-106.2, 44) * mm, "end": v(-107, 44) * mm});
            skLineSegment(sketch, "E1371", {"start": v(-107, 44) * mm, "end": v(-107, 45) * mm});
            skLineSegment(sketch, "E1372", {"start": v(-107, 45) * mm, "end": v(-121, 45) * mm});
            skLineSegment(sketch, "E1373", {"start": v(-121, 45) * mm, "end": v(-121, 44) * mm});
            skLineSegment(sketch, "E1374", {"start": v(-121, 44) * mm, "end": v(-121.8, 44) * mm});
            skLineSegment(sketch, "E1375", {"start": v(-121.8, 44) * mm, "end": v(-121.8, 32) * mm});
            skLineSegment(sketch, "E1376", {"start": v(-121.8, 32) * mm, "end": v(-121, 32) * mm});
            skLineSegment(sketch, "E1377", {"start": v(-121, 32) * mm, "end": v(-121, 31) * mm});
            skLineSegment(sketch, "E1378", {"start": v(-121, 31) * mm, "end": v(-107, 31) * mm});
            skLineSegment(sketch, "E1379", {"start": v(-107, 31) * mm, "end": v(-107, 32) * mm});
            skLineSegment(sketch, "E1380", {"start": v(-88, 32) * mm, "end": v(-87.2, 32) * mm});
            skLineSegment(sketch, "E1381", {"start": v(-87.2, 32) * mm, "end": v(-87.2, 44) * mm});
            skLineSegment(sketch, "E1382", {"start": v(-87.2, 44) * mm, "end": v(-88, 44) * mm});
            skLineSegment(sketch, "E1383", {"start": v(-88, 44) * mm, "end": v(-88, 45) * mm});
            skLineSegment(sketch, "E1384", {"start": v(-88, 45) * mm, "end": v(-102, 45) * mm});
            skLineSegment(sketch, "E1385", {"start": v(-102, 45) * mm, "end": v(-102, 44) * mm});
            skLineSegment(sketch, "E1386", {"start": v(-102, 44) * mm, "end": v(-102.8, 44) * mm});
            skLineSegment(sketch, "E1387", {"start": v(-102.8, 44) * mm, "end": v(-102.8, 32) * mm});
            skLineSegment(sketch, "E1388", {"start": v(-102.8, 32) * mm, "end": v(-102, 32) * mm});
            skLineSegment(sketch, "E1389", {"start": v(-102, 32) * mm, "end": v(-102, 31) * mm});
            skLineSegment(sketch, "E1390", {"start": v(-102, 31) * mm, "end": v(-88, 31) * mm});
            skLineSegment(sketch, "E1391", {"start": v(-88, 31) * mm, "end": v(-88, 32) * mm});
            skLineSegment(sketch, "E1392", {"start": v(-69, 32) * mm, "end": v(-68.2, 32) * mm});
            skLineSegment(sketch, "E1393", {"start": v(-68.2, 32) * mm, "end": v(-68.2, 44) * mm});
            skLineSegment(sketch, "E1394", {"start": v(-68.2, 44) * mm, "end": v(-69, 44) * mm});
            skLineSegment(sketch, "E1395", {"start": v(-69, 44) * mm, "end": v(-69, 45) * mm});
            skLineSegment(sketch, "E1396", {"start": v(-69, 45) * mm, "end": v(-83, 45) * mm});
            skLineSegment(sketch, "E1397", {"start": v(-83, 45) * mm, "end": v(-83, 44) * mm});
            skLineSegment(sketch, "E1398", {"start": v(-83, 44) * mm, "end": v(-83.8, 44) * mm});
            skLineSegment(sketch, "E1399", {"start": v(-83.8, 44) * mm, "end": v(-83.8, 32) * mm});
            skLineSegment(sketch, "E1400", {"start": v(-83.8, 32) * mm, "end": v(-83, 32) * mm});
            skLineSegment(sketch, "E1401", {"start": v(-83, 32) * mm, "end": v(-83, 31) * mm});
            skLineSegment(sketch, "E1402", {"start": v(-83, 31) * mm, "end": v(-69, 31) * mm});
            skLineSegment(sketch, "E1403", {"start": v(-69, 31) * mm, "end": v(-69, 32) * mm});
            skLineSegment(sketch, "E1404", {"start": v(-50, 32) * mm, "end": v(-49.2, 32) * mm});
            skLineSegment(sketch, "E1405", {"start": v(-49.2, 32) * mm, "end": v(-49.2, 44) * mm});
            skLineSegment(sketch, "E1406", {"start": v(-49.2, 44) * mm, "end": v(-50, 44) * mm});
            skLineSegment(sketch, "E1407", {"start": v(-50, 44) * mm, "end": v(-50, 45) * mm});
            skLineSegment(sketch, "E1408", {"start": v(-50, 45) * mm, "end": v(-64, 45) * mm});
            skLineSegment(sketch, "E1409", {"start": v(-64, 45) * mm, "end": v(-64, 44) * mm});
            skLineSegment(sketch, "E1410", {"start": v(-64, 44) * mm, "end": v(-64.8, 44) * mm});
            skLineSegment(sketch, "E1411", {"start": v(-64.8, 44) * mm, "end": v(-64.8, 32) * mm});
            skLineSegment(sketch, "E1412", {"start": v(-64.8, 32) * mm, "end": v(-64, 32) * mm});
            skLineSegment(sketch, "E1413", {"start": v(-64, 32) * mm, "end": v(-64, 31) * mm});
            skLineSegment(sketch, "E1414", {"start": v(-64, 31) * mm, "end": v(-50, 31) * mm});
            skLineSegment(sketch, "E1415", {"start": v(-50, 31) * mm, "end": v(-50, 32) * mm});
            skLineSegment(sketch, "E1416", {"start": v(-31, 32) * mm, "end": v(-30.2, 32) * mm});
            skLineSegment(sketch, "E1417", {"start": v(-30.2, 32) * mm, "end": v(-30.2, 44) * mm});
            skLineSegment(sketch, "E1418", {"start": v(-30.2, 44) * mm, "end": v(-31, 44) * mm});
            skLineSegment(sketch, "E1419", {"start": v(-31, 44) * mm, "end": v(-31, 45) * mm});
            skLineSegment(sketch, "E1420", {"start": v(-31, 45) * mm, "end": v(-45, 45) * mm});
            skLineSegment(sketch, "E1421", {"start": v(-45, 45) * mm, "end": v(-45, 44) * mm});
            skLineSegment(sketch, "E1422", {"start": v(-45, 44) * mm, "end": v(-45.8, 44) * mm});
            skLineSegment(sketch, "E1423", {"start": v(-45.8, 44) * mm, "end": v(-45.8, 32) * mm});
            skLineSegment(sketch, "E1424", {"start": v(-45.8, 32) * mm, "end": v(-45, 32) * mm});
            skLineSegment(sketch, "E1425", {"start": v(-45, 32) * mm, "end": v(-45, 31) * mm});
            skLineSegment(sketch, "E1426", {"start": v(-45, 31) * mm, "end": v(-31, 31) * mm});
            skLineSegment(sketch, "E1427", {"start": v(-31, 31) * mm, "end": v(-31, 32) * mm});
            skLineSegment(sketch, "E1428", {"start": v(-12, 32) * mm, "end": v(-11.2, 32) * mm});
            skLineSegment(sketch, "E1429", {"start": v(-11.2, 32) * mm, "end": v(-11.2, 44) * mm});
            skLineSegment(sketch, "E1430", {"start": v(-11.2, 44) * mm, "end": v(-12, 44) * mm});
            skLineSegment(sketch, "E1431", {"start": v(-12, 44) * mm, "end": v(-12, 45) * mm});
            skLineSegment(sketch, "E1432", {"start": v(-12, 45) * mm, "end": v(-26, 45) * mm});
            skLineSegment(sketch, "E1433", {"start": v(-26, 45) * mm, "end": v(-26, 44) * mm});
            skLineSegment(sketch, "E1434", {"start": v(-26, 44) * mm, "end": v(-26.8, 44) * mm});
            skLineSegment(sketch, "E1435", {"start": v(-26.8, 44) * mm, "end": v(-26.8, 32) * mm});
            skLineSegment(sketch, "E1436", {"start": v(-26.8, 32) * mm, "end": v(-26, 32) * mm});
            skLineSegment(sketch, "E1437", {"start": v(-26, 32) * mm, "end": v(-26, 31) * mm});
            skLineSegment(sketch, "E1438", {"start": v(-26, 31) * mm, "end": v(-12, 31) * mm});
            skLineSegment(sketch, "E1439", {"start": v(-12, 31) * mm, "end": v(-12, 32) * mm});
            skLineSegment(sketch, "E1440", {"start": v(7, 32) * mm, "end": v(7.8, 32) * mm});
            skLineSegment(sketch, "E1441", {"start": v(7.8, 32) * mm, "end": v(7.8, 44) * mm});
            skLineSegment(sketch, "E1442", {"start": v(7.8, 44) * mm, "end": v(7, 44) * mm});
            skLineSegment(sketch, "E1443", {"start": v(7, 44) * mm, "end": v(7, 45) * mm});
            skLineSegment(sketch, "E1444", {"start": v(7, 45) * mm, "end": v(-7, 45) * mm});
            skLineSegment(sketch, "E1445", {"start": v(-7, 45) * mm, "end": v(-7, 44) * mm});
            skLineSegment(sketch, "E1446", {"start": v(-7, 44) * mm, "end": v(-7.8, 44) * mm});
            skLineSegment(sketch, "E1447", {"start": v(-7.8, 44) * mm, "end": v(-7.8, 32) * mm});
            skLineSegment(sketch, "E1448", {"start": v(-7.8, 32) * mm, "end": v(-7, 32) * mm});
            skLineSegment(sketch, "E1449", {"start": v(-7, 32) * mm, "end": v(-7, 31) * mm});
            skLineSegment(sketch, "E1450", {"start": v(-7, 31) * mm, "end": v(7, 31) * mm});
            skLineSegment(sketch, "E1451", {"start": v(7, 31) * mm, "end": v(7, 32) * mm});
            skLineSegment(sketch, "E1452", {"start": v(26, 32) * mm, "end": v(26.8, 32) * mm});
            skLineSegment(sketch, "E1453", {"start": v(26.8, 32) * mm, "end": v(26.8, 44) * mm});
            skLineSegment(sketch, "E1454", {"start": v(26.8, 44) * mm, "end": v(26, 44) * mm});
            skLineSegment(sketch, "E1455", {"start": v(26, 44) * mm, "end": v(26, 45) * mm});
            skLineSegment(sketch, "E1456", {"start": v(26, 45) * mm, "end": v(12, 45) * mm});
            skLineSegment(sketch, "E1457", {"start": v(12, 45) * mm, "end": v(12, 44) * mm});
            skLineSegment(sketch, "E1458", {"start": v(12, 44) * mm, "end": v(11.2, 44) * mm});
            skLineSegment(sketch, "E1459", {"start": v(11.2, 44) * mm, "end": v(11.2, 32) * mm});
            skLineSegment(sketch, "E1460", {"start": v(11.2, 32) * mm, "end": v(12, 32) * mm});
            skLineSegment(sketch, "E1461", {"start": v(12, 32) * mm, "end": v(12, 31) * mm});
            skLineSegment(sketch, "E1462", {"start": v(12, 31) * mm, "end": v(26, 31) * mm});
            skLineSegment(sketch, "E1463", {"start": v(26, 31) * mm, "end": v(26, 32) * mm});
            skLineSegment(sketch, "E1464", {"start": v(45, 32) * mm, "end": v(45.8, 32) * mm});
            skLineSegment(sketch, "E1465", {"start": v(45.8, 32) * mm, "end": v(45.8, 44) * mm});
            skLineSegment(sketch, "E1466", {"start": v(45.8, 44) * mm, "end": v(45, 44) * mm});
            skLineSegment(sketch, "E1467", {"start": v(45, 44) * mm, "end": v(45, 45) * mm});
            skLineSegment(sketch, "E1468", {"start": v(45, 45) * mm, "end": v(31, 45) * mm});
            skLineSegment(sketch, "E1469", {"start": v(31, 45) * mm, "end": v(31, 44) * mm});
            skLineSegment(sketch, "E1470", {"start": v(31, 44) * mm, "end": v(30.2, 44) * mm});
            skLineSegment(sketch, "E1471", {"start": v(30.2, 44) * mm, "end": v(30.2, 32) * mm});
            skLineSegment(sketch, "E1472", {"start": v(30.2, 32) * mm, "end": v(31, 32) * mm});
            skLineSegment(sketch, "E1473", {"start": v(31, 32) * mm, "end": v(31, 31) * mm});
            skLineSegment(sketch, "E1474", {"start": v(31, 31) * mm, "end": v(45, 31) * mm});
            skLineSegment(sketch, "E1475", {"start": v(45, 31) * mm, "end": v(45, 32) * mm});
            skLineSegment(sketch, "E1476", {"start": v(64, 32) * mm, "end": v(64.8, 32) * mm});
            skLineSegment(sketch, "E1477", {"start": v(64.8, 32) * mm, "end": v(64.8, 44) * mm});
            skLineSegment(sketch, "E1478", {"start": v(64.8, 44) * mm, "end": v(64, 44) * mm});
            skLineSegment(sketch, "E1479", {"start": v(64, 44) * mm, "end": v(64, 45) * mm});
            skLineSegment(sketch, "E1480", {"start": v(64, 45) * mm, "end": v(50, 45) * mm});
            skLineSegment(sketch, "E1481", {"start": v(50, 45) * mm, "end": v(50, 44) * mm});
            skLineSegment(sketch, "E1482", {"start": v(50, 44) * mm, "end": v(49.2, 44) * mm});
            skLineSegment(sketch, "E1483", {"start": v(49.2, 44) * mm, "end": v(49.2, 32) * mm});
            skLineSegment(sketch, "E1484", {"start": v(49.2, 32) * mm, "end": v(50, 32) * mm});
            skLineSegment(sketch, "E1485", {"start": v(50, 32) * mm, "end": v(50, 31) * mm});
            skLineSegment(sketch, "E1486", {"start": v(50, 31) * mm, "end": v(64, 31) * mm});
            skLineSegment(sketch, "E1487", {"start": v(64, 31) * mm, "end": v(64, 32) * mm});
            skLineSegment(sketch, "E1488", {"start": v(83, 32) * mm, "end": v(83.8, 32) * mm});
            skLineSegment(sketch, "E1489", {"start": v(83.8, 32) * mm, "end": v(83.8, 44) * mm});
            skLineSegment(sketch, "E1490", {"start": v(83.8, 44) * mm, "end": v(83, 44) * mm});
            skLineSegment(sketch, "E1491", {"start": v(83, 44) * mm, "end": v(83, 45) * mm});
            skLineSegment(sketch, "E1492", {"start": v(83, 45) * mm, "end": v(69, 45) * mm});
            skLineSegment(sketch, "E1493", {"start": v(69, 45) * mm, "end": v(69, 44) * mm});
            skLineSegment(sketch, "E1494", {"start": v(69, 44) * mm, "end": v(68.2, 44) * mm});
            skLineSegment(sketch, "E1495", {"start": v(68.2, 44) * mm, "end": v(68.2, 32) * mm});
            skLineSegment(sketch, "E1496", {"start": v(68.2, 32) * mm, "end": v(69, 32) * mm});
            skLineSegment(sketch, "E1497", {"start": v(69, 32) * mm, "end": v(69, 31) * mm});
            skLineSegment(sketch, "E1498", {"start": v(69, 31) * mm, "end": v(83, 31) * mm});
            skLineSegment(sketch, "E1499", {"start": v(83, 31) * mm, "end": v(83, 32) * mm});
            skLineSegment(sketch, "E1500", {"start": v(102, 32) * mm, "end": v(102.8, 32) * mm});
            skLineSegment(sketch, "E1501", {"start": v(102.8, 32) * mm, "end": v(102.8, 44) * mm});
            skLineSegment(sketch, "E1502", {"start": v(102.8, 44) * mm, "end": v(102, 44) * mm});
            skLineSegment(sketch, "E1503", {"start": v(102, 44) * mm, "end": v(102, 45) * mm});
            skLineSegment(sketch, "E1504", {"start": v(102, 45) * mm, "end": v(88, 45) * mm});
            skLineSegment(sketch, "E1505", {"start": v(88, 45) * mm, "end": v(88, 44) * mm});
            skLineSegment(sketch, "E1506", {"start": v(88, 44) * mm, "end": v(87.2, 44) * mm});
            skLineSegment(sketch, "E1507", {"start": v(87.2, 44) * mm, "end": v(87.2, 32) * mm});
            skLineSegment(sketch, "E1508", {"start": v(87.2, 32) * mm, "end": v(88, 32) * mm});
            skLineSegment(sketch, "E1509", {"start": v(88, 32) * mm, "end": v(88, 31) * mm});
            skLineSegment(sketch, "E1510", {"start": v(88, 31) * mm, "end": v(102, 31) * mm});
            skLineSegment(sketch, "E1511", {"start": v(102, 31) * mm, "end": v(102, 32) * mm});
            skLineSegment(sketch, "E1512", {"start": v(113.1, 31.23) * mm, "end": v(114.93, 31.23) * mm});
            skLineSegment(sketch, "E1513", {"start": v(114.93, 31.23) * mm, "end": v(114.93, 32.03) * mm});
            skLineSegment(sketch, "E1514", {"start": v(114.93, 32.03) * mm, "end": v(115.7, 32.03) * mm});
            skLineSegment(sketch, "E1515", {"start": v(115.7, 32.03) * mm, "end": v(115.7, 32) * mm});
            skLineSegment(sketch, "E1516", {"start": v(115.7, 32) * mm, "end": v(116.5, 32) * mm});
            skLineSegment(sketch, "E1517", {"start": v(116.5, 32) * mm, "end": v(116.5, 31) * mm});
            skLineSegment(sketch, "E1518", {"start": v(116.5, 31) * mm, "end": v(130.5, 31) * mm});
            skLineSegment(sketch, "E1519", {"start": v(130.5, 31) * mm, "end": v(130.5, 32) * mm});
            skLineSegment(sketch, "E1520", {"start": v(130.5, 32) * mm, "end": v(131.3, 32) * mm});
            skLineSegment(sketch, "E1521", {"start": v(131.3, 32) * mm, "end": v(131.3, 32.03) * mm});
            skLineSegment(sketch, "E1522", {"start": v(131.3, 32.03) * mm, "end": v(132.07, 32.03) * mm});
            skLineSegment(sketch, "E1523", {"start": v(132.07, 32.03) * mm, "end": v(132.07, 31.23) * mm});
            skLineSegment(sketch, "E1524", {"start": v(132.07, 31.23) * mm, "end": v(133.9, 31.23) * mm});
            skLineSegment(sketch, "E1525", {"start": v(133.9, 31.23) * mm, "end": v(133.9, 30.03) * mm});
            skLineSegment(sketch, "E1526", {"start": v(133.9, 30.03) * mm, "end": v(136.9, 30.03) * mm});
            skLineSegment(sketch, "E1527", {"start": v(136.9, 30.03) * mm, "end": v(136.9, 31.23) * mm});
            skLineSegment(sketch, "E1528", {"start": v(136.9, 31.23) * mm, "end": v(138.73, 31.23) * mm});
            skLineSegment(sketch, "E1529", {"start": v(138.73, 31.23) * mm, "end": v(138.73, 37.5) * mm});
            skLineSegment(sketch, "E1530", {"start": v(138.73, 37.5) * mm, "end": v(139.6, 37.5) * mm});
            skLineSegment(sketch, "E1531", {"start": v(139.6, 37.5) * mm, "end": v(139.6, 40.3) * mm});
            skLineSegment(sketch, "E1532", {"start": v(139.6, 40.3) * mm, "end": v(138.73, 40.3) * mm});
            skLineSegment(sketch, "E1533", {"start": v(138.73, 40.3) * mm, "end": v(138.73, 43.53) * mm});
            skLineSegment(sketch, "E1534", {"start": v(138.73, 43.53) * mm, "end": v(132.07, 43.53) * mm});
            skLineSegment(sketch, "E1535", {"start": v(132.07, 43.53) * mm, "end": v(132.07, 42.73) * mm});
            skLineSegment(sketch, "E1536", {"start": v(132.07, 42.73) * mm, "end": v(131.3, 42.73) * mm});
            skLineSegment(sketch, "E1537", {"start": v(131.3, 42.73) * mm, "end": v(131.3, 44) * mm});
            skLineSegment(sketch, "E1538", {"start": v(131.3, 44) * mm, "end": v(130.5, 44) * mm});
            skLineSegment(sketch, "E1539", {"start": v(130.5, 44) * mm, "end": v(130.5, 45) * mm});
            skLineSegment(sketch, "E1540", {"start": v(130.5, 45) * mm, "end": v(116.5, 45) * mm});
            skLineSegment(sketch, "E1541", {"start": v(116.5, 45) * mm, "end": v(116.5, 44) * mm});
            skLineSegment(sketch, "E1542", {"start": v(116.5, 44) * mm, "end": v(115.7, 44) * mm});
            skLineSegment(sketch, "E1543", {"start": v(115.7, 44) * mm, "end": v(115.7, 42.73) * mm});
            skLineSegment(sketch, "E1544", {"start": v(115.7, 42.73) * mm, "end": v(114.93, 42.73) * mm});
            skLineSegment(sketch, "E1545", {"start": v(114.93, 42.73) * mm, "end": v(114.93, 43.53) * mm});
            skLineSegment(sketch, "E1546", {"start": v(114.93, 43.53) * mm, "end": v(108.28, 43.53) * mm});
            skLineSegment(sketch, "E1547", {"start": v(108.28, 43.53) * mm, "end": v(108.28, 40.3) * mm});
            skLineSegment(sketch, "E1548", {"start": v(108.28, 40.3) * mm, "end": v(107.4, 40.3) * mm});
            skLineSegment(sketch, "E1549", {"start": v(107.4, 40.3) * mm, "end": v(107.4, 37.5) * mm});
            skLineSegment(sketch, "E1550", {"start": v(107.4, 37.5) * mm, "end": v(108.28, 37.5) * mm});
            skLineSegment(sketch, "E1551", {"start": v(108.28, 37.5) * mm, "end": v(108.28, 31.23) * mm});
            skLineSegment(sketch, "E1552", {"start": v(108.28, 31.23) * mm, "end": v(110.1, 31.23) * mm});
            skLineSegment(sketch, "E1553", {"start": v(110.1, 31.23) * mm, "end": v(110.1, 30.03) * mm});
            skLineSegment(sketch, "E1554", {"start": v(110.1, 30.03) * mm, "end": v(113.1, 30.03) * mm});
            skLineSegment(sketch, "E1555", {"start": v(113.1, 30.03) * mm, "end": v(113.1, 31.23) * mm});
            skLineSegment(sketch, "E1556", {"start": v(-121.25, 13) * mm, "end": v(-120.45, 13) * mm});
            skLineSegment(sketch, "E1557", {"start": v(-120.45, 13) * mm, "end": v(-120.45, 25) * mm});
            skLineSegment(sketch, "E1558", {"start": v(-120.45, 25) * mm, "end": v(-121.25, 25) * mm});
            skLineSegment(sketch, "E1559", {"start": v(-121.25, 25) * mm, "end": v(-121.25, 26) * mm});
            skLineSegment(sketch, "E1560", {"start": v(-121.25, 26) * mm, "end": v(-135.25, 26) * mm});
            skLineSegment(sketch, "E1561", {"start": v(-135.25, 26) * mm, "end": v(-135.25, 25) * mm});
            skLineSegment(sketch, "E1562", {"start": v(-135.25, 25) * mm, "end": v(-136.05, 25) * mm});
            skLineSegment(sketch, "E1563", {"start": v(-136.05, 25) * mm, "end": v(-136.05, 13) * mm});
            skLineSegment(sketch, "E1564", {"start": v(-136.05, 13) * mm, "end": v(-135.25, 13) * mm});
            skLineSegment(sketch, "E1565", {"start": v(-135.25, 13) * mm, "end": v(-135.25, 12) * mm});
            skLineSegment(sketch, "E1566", {"start": v(-135.25, 12) * mm, "end": v(-121.25, 12) * mm});
            skLineSegment(sketch, "E1567", {"start": v(-121.25, 12) * mm, "end": v(-121.25, 13) * mm});
            skLineSegment(sketch, "E1568", {"start": v(-97.5, 13) * mm, "end": v(-96.7, 13) * mm});
            skLineSegment(sketch, "E1569", {"start": v(-96.7, 13) * mm, "end": v(-96.7, 25) * mm});
            skLineSegment(sketch, "E1570", {"start": v(-96.7, 25) * mm, "end": v(-97.5, 25) * mm});
            skLineSegment(sketch, "E1571", {"start": v(-97.5, 25) * mm, "end": v(-97.5, 26) * mm});
            skLineSegment(sketch, "E1572", {"start": v(-97.5, 26) * mm, "end": v(-111.5, 26) * mm});
            skLineSegment(sketch, "E1573", {"start": v(-111.5, 26) * mm, "end": v(-111.5, 25) * mm});
            skLineSegment(sketch, "E1574", {"start": v(-111.5, 25) * mm, "end": v(-112.3, 25) * mm});
            skLineSegment(sketch, "E1575", {"start": v(-112.3, 25) * mm, "end": v(-112.3, 13) * mm});
            skLineSegment(sketch, "E1576", {"start": v(-112.3, 13) * mm, "end": v(-111.5, 13) * mm});
            skLineSegment(sketch, "E1577", {"start": v(-111.5, 13) * mm, "end": v(-111.5, 12) * mm});
            skLineSegment(sketch, "E1578", {"start": v(-111.5, 12) * mm, "end": v(-97.5, 12) * mm});
            skLineSegment(sketch, "E1579", {"start": v(-97.5, 12) * mm, "end": v(-97.5, 13) * mm});
            skLineSegment(sketch, "E1580", {"start": v(-78.5, 13) * mm, "end": v(-77.7, 13) * mm});
            skLineSegment(sketch, "E1581", {"start": v(-77.7, 13) * mm, "end": v(-77.7, 25) * mm});
            skLineSegment(sketch, "E1582", {"start": v(-77.7, 25) * mm, "end": v(-78.5, 25) * mm});
            skLineSegment(sketch, "E1583", {"start": v(-78.5, 25) * mm, "end": v(-78.5, 26) * mm});
            skLineSegment(sketch, "E1584", {"start": v(-78.5, 26) * mm, "end": v(-92.5, 26) * mm});
            skLineSegment(sketch, "E1585", {"start": v(-92.5, 26) * mm, "end": v(-92.5, 25) * mm});
            skLineSegment(sketch, "E1586", {"start": v(-92.5, 25) * mm, "end": v(-93.3, 25) * mm});
            skLineSegment(sketch, "E1587", {"start": v(-93.3, 25) * mm, "end": v(-93.3, 13) * mm});
            skLineSegment(sketch, "E1588", {"start": v(-93.3, 13) * mm, "end": v(-92.5, 13) * mm});
            skLineSegment(sketch, "E1589", {"start": v(-92.5, 13) * mm, "end": v(-92.5, 12) * mm});
            skLineSegment(sketch, "E1590", {"start": v(-92.5, 12) * mm, "end": v(-78.5, 12) * mm});
            skLineSegment(sketch, "E1591", {"start": v(-78.5, 12) * mm, "end": v(-78.5, 13) * mm});
            skLineSegment(sketch, "E1592", {"start": v(-59.5, 13) * mm, "end": v(-58.7, 13) * mm});
            skLineSegment(sketch, "E1593", {"start": v(-58.7, 13) * mm, "end": v(-58.7, 25) * mm});
            skLineSegment(sketch, "E1594", {"start": v(-58.7, 25) * mm, "end": v(-59.5, 25) * mm});
            skLineSegment(sketch, "E1595", {"start": v(-59.5, 25) * mm, "end": v(-59.5, 26) * mm});
            skLineSegment(sketch, "E1596", {"start": v(-59.5, 26) * mm, "end": v(-73.5, 26) * mm});
            skLineSegment(sketch, "E1597", {"start": v(-73.5, 26) * mm, "end": v(-73.5, 25) * mm});
            skLineSegment(sketch, "E1598", {"start": v(-73.5, 25) * mm, "end": v(-74.3, 25) * mm});
            skLineSegment(sketch, "E1599", {"start": v(-74.3, 25) * mm, "end": v(-74.3, 13) * mm});
            skLineSegment(sketch, "E1600", {"start": v(-74.3, 13) * mm, "end": v(-73.5, 13) * mm});
            skLineSegment(sketch, "E1601", {"start": v(-73.5, 13) * mm, "end": v(-73.5, 12) * mm});
            skLineSegment(sketch, "E1602", {"start": v(-73.5, 12) * mm, "end": v(-59.5, 12) * mm});
            skLineSegment(sketch, "E1603", {"start": v(-59.5, 12) * mm, "end": v(-59.5, 13) * mm});
            skLineSegment(sketch, "E1604", {"start": v(-40.5, 13) * mm, "end": v(-39.7, 13) * mm});
            skLineSegment(sketch, "E1605", {"start": v(-39.7, 13) * mm, "end": v(-39.7, 25) * mm});
            skLineSegment(sketch, "E1606", {"start": v(-39.7, 25) * mm, "end": v(-40.5, 25) * mm});
            skLineSegment(sketch, "E1607", {"start": v(-40.5, 25) * mm, "end": v(-40.5, 26) * mm});
            skLineSegment(sketch, "E1608", {"start": v(-40.5, 26) * mm, "end": v(-54.5, 26) * mm});
            skLineSegment(sketch, "E1609", {"start": v(-54.5, 26) * mm, "end": v(-54.5, 25) * mm});
            skLineSegment(sketch, "E1610", {"start": v(-54.5, 25) * mm, "end": v(-55.3, 25) * mm});
            skLineSegment(sketch, "E1611", {"start": v(-55.3, 25) * mm, "end": v(-55.3, 13) * mm});
            skLineSegment(sketch, "E1612", {"start": v(-55.3, 13) * mm, "end": v(-54.5, 13) * mm});
            skLineSegment(sketch, "E1613", {"start": v(-54.5, 13) * mm, "end": v(-54.5, 12) * mm});
            skLineSegment(sketch, "E1614", {"start": v(-54.5, 12) * mm, "end": v(-40.5, 12) * mm});
            skLineSegment(sketch, "E1615", {"start": v(-40.5, 12) * mm, "end": v(-40.5, 13) * mm});
            skLineSegment(sketch, "E1616", {"start": v(-21.5, 13) * mm, "end": v(-20.7, 13) * mm});
            skLineSegment(sketch, "E1617", {"start": v(-20.7, 13) * mm, "end": v(-20.7, 25) * mm});
            skLineSegment(sketch, "E1618", {"start": v(-20.7, 25) * mm, "end": v(-21.5, 25) * mm});
            skLineSegment(sketch, "E1619", {"start": v(-21.5, 25) * mm, "end": v(-21.5, 26) * mm});
            skLineSegment(sketch, "E1620", {"start": v(-21.5, 26) * mm, "end": v(-35.5, 26) * mm});
            skLineSegment(sketch, "E1621", {"start": v(-35.5, 26) * mm, "end": v(-35.5, 25) * mm});
            skLineSegment(sketch, "E1622", {"start": v(-35.5, 25) * mm, "end": v(-36.3, 25) * mm});
            skLineSegment(sketch, "E1623", {"start": v(-36.3, 25) * mm, "end": v(-36.3, 13) * mm});
            skLineSegment(sketch, "E1624", {"start": v(-36.3, 13) * mm, "end": v(-35.5, 13) * mm});
            skLineSegment(sketch, "E1625", {"start": v(-35.5, 13) * mm, "end": v(-35.5, 12) * mm});
            skLineSegment(sketch, "E1626", {"start": v(-35.5, 12) * mm, "end": v(-21.5, 12) * mm});
            skLineSegment(sketch, "E1627", {"start": v(-21.5, 12) * mm, "end": v(-21.5, 13) * mm});
            skLineSegment(sketch, "E1628", {"start": v(-2.5, 13) * mm, "end": v(-1.7, 13) * mm});
            skLineSegment(sketch, "E1629", {"start": v(-1.7, 13) * mm, "end": v(-1.7, 25) * mm});
            skLineSegment(sketch, "E1630", {"start": v(-1.7, 25) * mm, "end": v(-2.5, 25) * mm});
            skLineSegment(sketch, "E1631", {"start": v(-2.5, 25) * mm, "end": v(-2.5, 26) * mm});
            skLineSegment(sketch, "E1632", {"start": v(-2.5, 26) * mm, "end": v(-16.5, 26) * mm});
            skLineSegment(sketch, "E1633", {"start": v(-16.5, 26) * mm, "end": v(-16.5, 25) * mm});
            skLineSegment(sketch, "E1634", {"start": v(-16.5, 25) * mm, "end": v(-17.3, 25) * mm});
            skLineSegment(sketch, "E1635", {"start": v(-17.3, 25) * mm, "end": v(-17.3, 13) * mm});
            skLineSegment(sketch, "E1636", {"start": v(-17.3, 13) * mm, "end": v(-16.5, 13) * mm});
            skLineSegment(sketch, "E1637", {"start": v(-16.5, 13) * mm, "end": v(-16.5, 12) * mm});
            skLineSegment(sketch, "E1638", {"start": v(-16.5, 12) * mm, "end": v(-2.5, 12) * mm});
            skLineSegment(sketch, "E1639", {"start": v(-2.5, 12) * mm, "end": v(-2.5, 13) * mm});
            skLineSegment(sketch, "E1640", {"start": v(16.5, 13) * mm, "end": v(17.3, 13) * mm});
            skLineSegment(sketch, "E1641", {"start": v(17.3, 13) * mm, "end": v(17.3, 25) * mm});
            skLineSegment(sketch, "E1642", {"start": v(17.3, 25) * mm, "end": v(16.5, 25) * mm});
            skLineSegment(sketch, "E1643", {"start": v(16.5, 25) * mm, "end": v(16.5, 26) * mm});
            skLineSegment(sketch, "E1644", {"start": v(16.5, 26) * mm, "end": v(2.5, 26) * mm});
            skLineSegment(sketch, "E1645", {"start": v(2.5, 26) * mm, "end": v(2.5, 25) * mm});
            skLineSegment(sketch, "E1646", {"start": v(2.5, 25) * mm, "end": v(1.7, 25) * mm});
            skLineSegment(sketch, "E1647", {"start": v(1.7, 25) * mm, "end": v(1.7, 13) * mm});
            skLineSegment(sketch, "E1648", {"start": v(1.7, 13) * mm, "end": v(2.5, 13) * mm});
            skLineSegment(sketch, "E1649", {"start": v(2.5, 13) * mm, "end": v(2.5, 12) * mm});
            skLineSegment(sketch, "E1650", {"start": v(2.5, 12) * mm, "end": v(16.5, 12) * mm});
            skLineSegment(sketch, "E1651", {"start": v(16.5, 12) * mm, "end": v(16.5, 13) * mm});
            skLineSegment(sketch, "E1652", {"start": v(35.5, 13) * mm, "end": v(36.3, 13) * mm});
            skLineSegment(sketch, "E1653", {"start": v(36.3, 13) * mm, "end": v(36.3, 25) * mm});
            skLineSegment(sketch, "E1654", {"start": v(36.3, 25) * mm, "end": v(35.5, 25) * mm});
            skLineSegment(sketch, "E1655", {"start": v(35.5, 25) * mm, "end": v(35.5, 26) * mm});
            skLineSegment(sketch, "E1656", {"start": v(35.5, 26) * mm, "end": v(21.5, 26) * mm});
            skLineSegment(sketch, "E1657", {"start": v(21.5, 26) * mm, "end": v(21.5, 25) * mm});
            skLineSegment(sketch, "E1658", {"start": v(21.5, 25) * mm, "end": v(20.7, 25) * mm});
            skLineSegment(sketch, "E1659", {"start": v(20.7, 25) * mm, "end": v(20.7, 13) * mm});
            skLineSegment(sketch, "E1660", {"start": v(20.7, 13) * mm, "end": v(21.5, 13) * mm});
            skLineSegment(sketch, "E1661", {"start": v(21.5, 13) * mm, "end": v(21.5, 12) * mm});
            skLineSegment(sketch, "E1662", {"start": v(21.5, 12) * mm, "end": v(35.5, 12) * mm});
            skLineSegment(sketch, "E1663", {"start": v(35.5, 12) * mm, "end": v(35.5, 13) * mm});
            skLineSegment(sketch, "E1664", {"start": v(54.5, 13) * mm, "end": v(55.3, 13) * mm});
            skLineSegment(sketch, "E1665", {"start": v(55.3, 13) * mm, "end": v(55.3, 25) * mm});
            skLineSegment(sketch, "E1666", {"start": v(55.3, 25) * mm, "end": v(54.5, 25) * mm});
            skLineSegment(sketch, "E1667", {"start": v(54.5, 25) * mm, "end": v(54.5, 26) * mm});
            skLineSegment(sketch, "E1668", {"start": v(54.5, 26) * mm, "end": v(40.5, 26) * mm});
            skLineSegment(sketch, "E1669", {"start": v(40.5, 26) * mm, "end": v(40.5, 25) * mm});
            skLineSegment(sketch, "E1670", {"start": v(40.5, 25) * mm, "end": v(39.7, 25) * mm});
            skLineSegment(sketch, "E1671", {"start": v(39.7, 25) * mm, "end": v(39.7, 13) * mm});
            skLineSegment(sketch, "E1672", {"start": v(39.7, 13) * mm, "end": v(40.5, 13) * mm});
            skLineSegment(sketch, "E1673", {"start": v(40.5, 13) * mm, "end": v(40.5, 12) * mm});
            skLineSegment(sketch, "E1674", {"start": v(40.5, 12) * mm, "end": v(54.5, 12) * mm});
            skLineSegment(sketch, "E1675", {"start": v(54.5, 12) * mm, "end": v(54.5, 13) * mm});
            skLineSegment(sketch, "E1676", {"start": v(73.5, 13) * mm, "end": v(74.3, 13) * mm});
            skLineSegment(sketch, "E1677", {"start": v(74.3, 13) * mm, "end": v(74.3, 25) * mm});
            skLineSegment(sketch, "E1678", {"start": v(74.3, 25) * mm, "end": v(73.5, 25) * mm});
            skLineSegment(sketch, "E1679", {"start": v(73.5, 25) * mm, "end": v(73.5, 26) * mm});
            skLineSegment(sketch, "E1680", {"start": v(73.5, 26) * mm, "end": v(59.5, 26) * mm});
            skLineSegment(sketch, "E1681", {"start": v(59.5, 26) * mm, "end": v(59.5, 25) * mm});
            skLineSegment(sketch, "E1682", {"start": v(59.5, 25) * mm, "end": v(58.7, 25) * mm});
            skLineSegment(sketch, "E1683", {"start": v(58.7, 25) * mm, "end": v(58.7, 13) * mm});
            skLineSegment(sketch, "E1684", {"start": v(58.7, 13) * mm, "end": v(59.5, 13) * mm});
            skLineSegment(sketch, "E1685", {"start": v(59.5, 13) * mm, "end": v(59.5, 12) * mm});
            skLineSegment(sketch, "E1686", {"start": v(59.5, 12) * mm, "end": v(73.5, 12) * mm});
            skLineSegment(sketch, "E1687", {"start": v(73.5, 12) * mm, "end": v(73.5, 13) * mm});
            skLineSegment(sketch, "E1688", {"start": v(92.5, 13) * mm, "end": v(93.3, 13) * mm});
            skLineSegment(sketch, "E1689", {"start": v(93.3, 13) * mm, "end": v(93.3, 25) * mm});
            skLineSegment(sketch, "E1690", {"start": v(93.3, 25) * mm, "end": v(92.5, 25) * mm});
            skLineSegment(sketch, "E1691", {"start": v(92.5, 25) * mm, "end": v(92.5, 26) * mm});
            skLineSegment(sketch, "E1692", {"start": v(92.5, 26) * mm, "end": v(78.5, 26) * mm});
            skLineSegment(sketch, "E1693", {"start": v(78.5, 26) * mm, "end": v(78.5, 25) * mm});
            skLineSegment(sketch, "E1694", {"start": v(78.5, 25) * mm, "end": v(77.7, 25) * mm});
            skLineSegment(sketch, "E1695", {"start": v(77.7, 25) * mm, "end": v(77.7, 13) * mm});
            skLineSegment(sketch, "E1696", {"start": v(77.7, 13) * mm, "end": v(78.5, 13) * mm});
            skLineSegment(sketch, "E1697", {"start": v(78.5, 13) * mm, "end": v(78.5, 12) * mm});
            skLineSegment(sketch, "E1698", {"start": v(78.5, 12) * mm, "end": v(92.5, 12) * mm});
            skLineSegment(sketch, "E1699", {"start": v(92.5, 12) * mm, "end": v(92.5, 13) * mm});
            skLineSegment(sketch, "E1700", {"start": v(111.5, 13) * mm, "end": v(112.3, 13) * mm});
            skLineSegment(sketch, "E1701", {"start": v(112.3, 13) * mm, "end": v(112.3, 25) * mm});
            skLineSegment(sketch, "E1702", {"start": v(112.3, 25) * mm, "end": v(111.5, 25) * mm});
            skLineSegment(sketch, "E1703", {"start": v(111.5, 25) * mm, "end": v(111.5, 26) * mm});
            skLineSegment(sketch, "E1704", {"start": v(111.5, 26) * mm, "end": v(97.5, 26) * mm});
            skLineSegment(sketch, "E1705", {"start": v(97.5, 26) * mm, "end": v(97.5, 25) * mm});
            skLineSegment(sketch, "E1706", {"start": v(97.5, 25) * mm, "end": v(96.7, 25) * mm});
            skLineSegment(sketch, "E1707", {"start": v(96.7, 25) * mm, "end": v(96.7, 13) * mm});
            skLineSegment(sketch, "E1708", {"start": v(96.7, 13) * mm, "end": v(97.5, 13) * mm});
            skLineSegment(sketch, "E1709", {"start": v(97.5, 13) * mm, "end": v(97.5, 12) * mm});
            skLineSegment(sketch, "E1710", {"start": v(97.5, 12) * mm, "end": v(111.5, 12) * mm});
            skLineSegment(sketch, "E1711", {"start": v(111.5, 12) * mm, "end": v(111.5, 13) * mm});
            skLineSegment(sketch, "E1712", {"start": v(135.25, 13) * mm, "end": v(136.05, 13) * mm});
            skLineSegment(sketch, "E1713", {"start": v(136.05, 13) * mm, "end": v(136.05, 25) * mm});
            skLineSegment(sketch, "E1714", {"start": v(136.05, 25) * mm, "end": v(135.25, 25) * mm});
            skLineSegment(sketch, "E1715", {"start": v(135.25, 25) * mm, "end": v(135.25, 26) * mm});
            skLineSegment(sketch, "E1716", {"start": v(135.25, 26) * mm, "end": v(121.25, 26) * mm});
            skLineSegment(sketch, "E1717", {"start": v(121.25, 26) * mm, "end": v(121.25, 25) * mm});
            skLineSegment(sketch, "E1718", {"start": v(121.25, 25) * mm, "end": v(120.45, 25) * mm});
            skLineSegment(sketch, "E1719", {"start": v(120.45, 25) * mm, "end": v(120.45, 13) * mm});
            skLineSegment(sketch, "E1720", {"start": v(120.45, 13) * mm, "end": v(121.25, 13) * mm});
            skLineSegment(sketch, "E1721", {"start": v(121.25, 13) * mm, "end": v(121.25, 12) * mm});
            skLineSegment(sketch, "E1722", {"start": v(121.25, 12) * mm, "end": v(135.25, 12) * mm});
            skLineSegment(sketch, "E1723", {"start": v(135.25, 12) * mm, "end": v(135.25, 13) * mm});
            skLineSegment(sketch, "E1724", {"start": v(-118.88, -6) * mm, "end": v(-118.08, -6) * mm});
            skLineSegment(sketch, "E1725", {"start": v(-118.08, -6) * mm, "end": v(-118.08, 6) * mm});
            skLineSegment(sketch, "E1726", {"start": v(-118.08, 6) * mm, "end": v(-118.88, 6) * mm});
            skLineSegment(sketch, "E1727", {"start": v(-118.88, 6) * mm, "end": v(-118.88, 7) * mm});
            skLineSegment(sketch, "E1728", {"start": v(-118.88, 7) * mm, "end": v(-132.88, 7) * mm});
            skLineSegment(sketch, "E1729", {"start": v(-132.88, 7) * mm, "end": v(-132.88, 6) * mm});
            skLineSegment(sketch, "E1730", {"start": v(-132.88, 6) * mm, "end": v(-133.68, 6) * mm});
            skLineSegment(sketch, "E1731", {"start": v(-133.68, 6) * mm, "end": v(-133.68, -6) * mm});
            skLineSegment(sketch, "E1732", {"start": v(-133.68, -6) * mm, "end": v(-132.88, -6) * mm});
            skLineSegment(sketch, "E1733", {"start": v(-132.88, -6) * mm, "end": v(-132.88, -7) * mm});
            skLineSegment(sketch, "E1734", {"start": v(-132.88, -7) * mm, "end": v(-118.88, -7) * mm});
            skLineSegment(sketch, "E1735", {"start": v(-118.88, -7) * mm, "end": v(-118.88, -6) * mm});
            skLineSegment(sketch, "E1736", {"start": v(-92.75, -6) * mm, "end": v(-91.95, -6) * mm});
            skLineSegment(sketch, "E1737", {"start": v(-91.95, -6) * mm, "end": v(-91.95, 6) * mm});
            skLineSegment(sketch, "E1738", {"start": v(-91.95, 6) * mm, "end": v(-92.75, 6) * mm});
            skLineSegment(sketch, "E1739", {"start": v(-92.75, 6) * mm, "end": v(-92.75, 7) * mm});
            skLineSegment(sketch, "E1740", {"start": v(-92.75, 7) * mm, "end": v(-106.75, 7) * mm});
            skLineSegment(sketch, "E1741", {"start": v(-106.75, 7) * mm, "end": v(-106.75, 6) * mm});
            skLineSegment(sketch, "E1742", {"start": v(-106.75, 6) * mm, "end": v(-107.55, 6) * mm});
            skLineSegment(sketch, "E1743", {"start": v(-107.55, 6) * mm, "end": v(-107.55, -6) * mm});
            skLineSegment(sketch, "E1744", {"start": v(-107.55, -6) * mm, "end": v(-106.75, -6) * mm});
            skLineSegment(sketch, "E1745", {"start": v(-106.75, -6) * mm, "end": v(-106.75, -7) * mm});
            skLineSegment(sketch, "E1746", {"start": v(-106.75, -7) * mm, "end": v(-92.75, -7) * mm});
            skLineSegment(sketch, "E1747", {"start": v(-92.75, -7) * mm, "end": v(-92.75, -6) * mm});
            skLineSegment(sketch, "E1748", {"start": v(-73.75, -6) * mm, "end": v(-72.95, -6) * mm});
            skLineSegment(sketch, "E1749", {"start": v(-72.95, -6) * mm, "end": v(-72.95, 6) * mm});
            skLineSegment(sketch, "E1750", {"start": v(-72.95, 6) * mm, "end": v(-73.75, 6) * mm});
            skLineSegment(sketch, "E1751", {"start": v(-73.75, 6) * mm, "end": v(-73.75, 7) * mm});
            skLineSegment(sketch, "E1752", {"start": v(-73.75, 7) * mm, "end": v(-87.75, 7) * mm});
            skLineSegment(sketch, "E1753", {"start": v(-87.75, 7) * mm, "end": v(-87.75, 6) * mm});
            skLineSegment(sketch, "E1754", {"start": v(-87.75, 6) * mm, "end": v(-88.55, 6) * mm});
            skLineSegment(sketch, "E1755", {"start": v(-88.55, 6) * mm, "end": v(-88.55, -6) * mm});
            skLineSegment(sketch, "E1756", {"start": v(-88.55, -6) * mm, "end": v(-87.75, -6) * mm});
            skLineSegment(sketch, "E1757", {"start": v(-87.75, -6) * mm, "end": v(-87.75, -7) * mm});
            skLineSegment(sketch, "E1758", {"start": v(-87.75, -7) * mm, "end": v(-73.75, -7) * mm});
            skLineSegment(sketch, "E1759", {"start": v(-73.75, -7) * mm, "end": v(-73.75, -6) * mm});
            skLineSegment(sketch, "E1760", {"start": v(-54.75, -6) * mm, "end": v(-53.95, -6) * mm});
            skLineSegment(sketch, "E1761", {"start": v(-53.95, -6) * mm, "end": v(-53.95, 6) * mm});
            skLineSegment(sketch, "E1762", {"start": v(-53.95, 6) * mm, "end": v(-54.75, 6) * mm});
            skLineSegment(sketch, "E1763", {"start": v(-54.75, 6) * mm, "end": v(-54.75, 7) * mm});
            skLineSegment(sketch, "E1764", {"start": v(-54.75, 7) * mm, "end": v(-68.75, 7) * mm});
            skLineSegment(sketch, "E1765", {"start": v(-68.75, 7) * mm, "end": v(-68.75, 6) * mm});
            skLineSegment(sketch, "E1766", {"start": v(-68.75, 6) * mm, "end": v(-69.55, 6) * mm});
            skLineSegment(sketch, "E1767", {"start": v(-69.55, 6) * mm, "end": v(-69.55, -6) * mm});
            skLineSegment(sketch, "E1768", {"start": v(-69.55, -6) * mm, "end": v(-68.75, -6) * mm});
            skLineSegment(sketch, "E1769", {"start": v(-68.75, -6) * mm, "end": v(-68.75, -7) * mm});
            skLineSegment(sketch, "E1770", {"start": v(-68.75, -7) * mm, "end": v(-54.75, -7) * mm});
            skLineSegment(sketch, "E1771", {"start": v(-54.75, -7) * mm, "end": v(-54.75, -6) * mm});
            skLineSegment(sketch, "E1772", {"start": v(-35.75, -6) * mm, "end": v(-34.95, -6) * mm});
            skLineSegment(sketch, "E1773", {"start": v(-34.95, -6) * mm, "end": v(-34.95, 6) * mm});
            skLineSegment(sketch, "E1774", {"start": v(-34.95, 6) * mm, "end": v(-35.75, 6) * mm});
            skLineSegment(sketch, "E1775", {"start": v(-35.75, 6) * mm, "end": v(-35.75, 7) * mm});
            skLineSegment(sketch, "E1776", {"start": v(-35.75, 7) * mm, "end": v(-49.75, 7) * mm});
            skLineSegment(sketch, "E1777", {"start": v(-49.75, 7) * mm, "end": v(-49.75, 6) * mm});
            skLineSegment(sketch, "E1778", {"start": v(-49.75, 6) * mm, "end": v(-50.55, 6) * mm});
            skLineSegment(sketch, "E1779", {"start": v(-50.55, 6) * mm, "end": v(-50.55, -6) * mm});
            skLineSegment(sketch, "E1780", {"start": v(-50.55, -6) * mm, "end": v(-49.75, -6) * mm});
            skLineSegment(sketch, "E1781", {"start": v(-49.75, -6) * mm, "end": v(-49.75, -7) * mm});
            skLineSegment(sketch, "E1782", {"start": v(-49.75, -7) * mm, "end": v(-35.75, -7) * mm});
            skLineSegment(sketch, "E1783", {"start": v(-35.75, -7) * mm, "end": v(-35.75, -6) * mm});
            skLineSegment(sketch, "E1784", {"start": v(-16.75, -6) * mm, "end": v(-15.95, -6) * mm});
            skLineSegment(sketch, "E1785", {"start": v(-15.95, -6) * mm, "end": v(-15.95, 6) * mm});
            skLineSegment(sketch, "E1786", {"start": v(-15.95, 6) * mm, "end": v(-16.75, 6) * mm});
            skLineSegment(sketch, "E1787", {"start": v(-16.75, 6) * mm, "end": v(-16.75, 7) * mm});
            skLineSegment(sketch, "E1788", {"start": v(-16.75, 7) * mm, "end": v(-30.75, 7) * mm});
            skLineSegment(sketch, "E1789", {"start": v(-30.75, 7) * mm, "end": v(-30.75, 6) * mm});
            skLineSegment(sketch, "E1790", {"start": v(-30.75, 6) * mm, "end": v(-31.55, 6) * mm});
            skLineSegment(sketch, "E1791", {"start": v(-31.55, 6) * mm, "end": v(-31.55, -6) * mm});
            skLineSegment(sketch, "E1792", {"start": v(-31.55, -6) * mm, "end": v(-30.75, -6) * mm});
            skLineSegment(sketch, "E1793", {"start": v(-30.75, -6) * mm, "end": v(-30.75, -7) * mm});
            skLineSegment(sketch, "E1794", {"start": v(-30.75, -7) * mm, "end": v(-16.75, -7) * mm});
            skLineSegment(sketch, "E1795", {"start": v(-16.75, -7) * mm, "end": v(-16.75, -6) * mm});
            skLineSegment(sketch, "E1796", {"start": v(2.25, -6) * mm, "end": v(3.05, -6) * mm});
            skLineSegment(sketch, "E1797", {"start": v(3.05, -6) * mm, "end": v(3.05, 6) * mm});
            skLineSegment(sketch, "E1798", {"start": v(3.05, 6) * mm, "end": v(2.25, 6) * mm});
            skLineSegment(sketch, "E1799", {"start": v(2.25, 6) * mm, "end": v(2.25, 7) * mm});
            skLineSegment(sketch, "E1800", {"start": v(2.25, 7) * mm, "end": v(-11.75, 7) * mm});
            skLineSegment(sketch, "E1801", {"start": v(-11.75, 7) * mm, "end": v(-11.75, 6) * mm});
            skLineSegment(sketch, "E1802", {"start": v(-11.75, 6) * mm, "end": v(-12.55, 6) * mm});
            skLineSegment(sketch, "E1803", {"start": v(-12.55, 6) * mm, "end": v(-12.55, -6) * mm});
            skLineSegment(sketch, "E1804", {"start": v(-12.55, -6) * mm, "end": v(-11.75, -6) * mm});
            skLineSegment(sketch, "E1805", {"start": v(-11.75, -6) * mm, "end": v(-11.75, -7) * mm});
            skLineSegment(sketch, "E1806", {"start": v(-11.75, -7) * mm, "end": v(2.25, -7) * mm});
            skLineSegment(sketch, "E1807", {"start": v(2.25, -7) * mm, "end": v(2.25, -6) * mm});
            skLineSegment(sketch, "E1808", {"start": v(21.25, -6) * mm, "end": v(22.05, -6) * mm});
            skLineSegment(sketch, "E1809", {"start": v(22.05, -6) * mm, "end": v(22.05, 6) * mm});
            skLineSegment(sketch, "E1810", {"start": v(22.05, 6) * mm, "end": v(21.25, 6) * mm});
            skLineSegment(sketch, "E1811", {"start": v(21.25, 6) * mm, "end": v(21.25, 7) * mm});
            skLineSegment(sketch, "E1812", {"start": v(21.25, 7) * mm, "end": v(7.25, 7) * mm});
            skLineSegment(sketch, "E1813", {"start": v(7.25, 7) * mm, "end": v(7.25, 6) * mm});
            skLineSegment(sketch, "E1814", {"start": v(7.25, 6) * mm, "end": v(6.45, 6) * mm});
            skLineSegment(sketch, "E1815", {"start": v(6.45, 6) * mm, "end": v(6.45, -6) * mm});
            skLineSegment(sketch, "E1816", {"start": v(6.45, -6) * mm, "end": v(7.25, -6) * mm});
            skLineSegment(sketch, "E1817", {"start": v(7.25, -6) * mm, "end": v(7.25, -7) * mm});
            skLineSegment(sketch, "E1818", {"start": v(7.25, -7) * mm, "end": v(21.25, -7) * mm});
            skLineSegment(sketch, "E1819", {"start": v(21.25, -7) * mm, "end": v(21.25, -6) * mm});
            skLineSegment(sketch, "E1820", {"start": v(40.25, -6) * mm, "end": v(41.05, -6) * mm});
            skLineSegment(sketch, "E1821", {"start": v(41.05, -6) * mm, "end": v(41.05, 6) * mm});
            skLineSegment(sketch, "E1822", {"start": v(41.05, 6) * mm, "end": v(40.25, 6) * mm});
            skLineSegment(sketch, "E1823", {"start": v(40.25, 6) * mm, "end": v(40.25, 7) * mm});
            skLineSegment(sketch, "E1824", {"start": v(40.25, 7) * mm, "end": v(26.25, 7) * mm});
            skLineSegment(sketch, "E1825", {"start": v(26.25, 7) * mm, "end": v(26.25, 6) * mm});
            skLineSegment(sketch, "E1826", {"start": v(26.25, 6) * mm, "end": v(25.45, 6) * mm});
            skLineSegment(sketch, "E1827", {"start": v(25.45, 6) * mm, "end": v(25.45, -6) * mm});
            skLineSegment(sketch, "E1828", {"start": v(25.45, -6) * mm, "end": v(26.25, -6) * mm});
            skLineSegment(sketch, "E1829", {"start": v(26.25, -6) * mm, "end": v(26.25, -7) * mm});
            skLineSegment(sketch, "E1830", {"start": v(26.25, -7) * mm, "end": v(40.25, -7) * mm});
            skLineSegment(sketch, "E1831", {"start": v(40.25, -7) * mm, "end": v(40.25, -6) * mm});
            skLineSegment(sketch, "E1832", {"start": v(59.25, -6) * mm, "end": v(60.05, -6) * mm});
            skLineSegment(sketch, "E1833", {"start": v(60.05, -6) * mm, "end": v(60.05, 6) * mm});
            skLineSegment(sketch, "E1834", {"start": v(60.05, 6) * mm, "end": v(59.25, 6) * mm});
            skLineSegment(sketch, "E1835", {"start": v(59.25, 6) * mm, "end": v(59.25, 7) * mm});
            skLineSegment(sketch, "E1836", {"start": v(59.25, 7) * mm, "end": v(45.25, 7) * mm});
            skLineSegment(sketch, "E1837", {"start": v(45.25, 7) * mm, "end": v(45.25, 6) * mm});
            skLineSegment(sketch, "E1838", {"start": v(45.25, 6) * mm, "end": v(44.45, 6) * mm});
            skLineSegment(sketch, "E1839", {"start": v(44.45, 6) * mm, "end": v(44.45, -6) * mm});
            skLineSegment(sketch, "E1840", {"start": v(44.45, -6) * mm, "end": v(45.25, -6) * mm});
            skLineSegment(sketch, "E1841", {"start": v(45.25, -6) * mm, "end": v(45.25, -7) * mm});
            skLineSegment(sketch, "E1842", {"start": v(45.25, -7) * mm, "end": v(59.25, -7) * mm});
            skLineSegment(sketch, "E1843", {"start": v(59.25, -7) * mm, "end": v(59.25, -6) * mm});
            skLineSegment(sketch, "E1844", {"start": v(78.25, -6) * mm, "end": v(79.05, -6) * mm});
            skLineSegment(sketch, "E1845", {"start": v(79.05, -6) * mm, "end": v(79.05, 6) * mm});
            skLineSegment(sketch, "E1846", {"start": v(79.05, 6) * mm, "end": v(78.25, 6) * mm});
            skLineSegment(sketch, "E1847", {"start": v(78.25, 6) * mm, "end": v(78.25, 7) * mm});
            skLineSegment(sketch, "E1848", {"start": v(78.25, 7) * mm, "end": v(64.25, 7) * mm});
            skLineSegment(sketch, "E1849", {"start": v(64.25, 7) * mm, "end": v(64.25, 6) * mm});
            skLineSegment(sketch, "E1850", {"start": v(64.25, 6) * mm, "end": v(63.45, 6) * mm});
            skLineSegment(sketch, "E1851", {"start": v(63.45, 6) * mm, "end": v(63.45, -6) * mm});
            skLineSegment(sketch, "E1852", {"start": v(63.45, -6) * mm, "end": v(64.25, -6) * mm});
            skLineSegment(sketch, "E1853", {"start": v(64.25, -6) * mm, "end": v(64.25, -7) * mm});
            skLineSegment(sketch, "E1854", {"start": v(64.25, -7) * mm, "end": v(78.25, -7) * mm});
            skLineSegment(sketch, "E1855", {"start": v(78.25, -7) * mm, "end": v(78.25, -6) * mm});
            skLineSegment(sketch, "E1856", {"start": v(97.25, -6) * mm, "end": v(98.05, -6) * mm});
            skLineSegment(sketch, "E1857", {"start": v(98.05, -6) * mm, "end": v(98.05, 6) * mm});
            skLineSegment(sketch, "E1858", {"start": v(98.05, 6) * mm, "end": v(97.25, 6) * mm});
            skLineSegment(sketch, "E1859", {"start": v(97.25, 6) * mm, "end": v(97.25, 7) * mm});
            skLineSegment(sketch, "E1860", {"start": v(97.25, 7) * mm, "end": v(83.25, 7) * mm});
            skLineSegment(sketch, "E1861", {"start": v(83.25, 7) * mm, "end": v(83.25, 6) * mm});
            skLineSegment(sketch, "E1862", {"start": v(83.25, 6) * mm, "end": v(82.45, 6) * mm});
            skLineSegment(sketch, "E1863", {"start": v(82.45, 6) * mm, "end": v(82.45, -6) * mm});
            skLineSegment(sketch, "E1864", {"start": v(82.45, -6) * mm, "end": v(83.25, -6) * mm});
            skLineSegment(sketch, "E1865", {"start": v(83.25, -6) * mm, "end": v(83.25, -7) * mm});
            skLineSegment(sketch, "E1866", {"start": v(83.25, -7) * mm, "end": v(97.25, -7) * mm});
            skLineSegment(sketch, "E1867", {"start": v(97.25, -7) * mm, "end": v(97.25, -6) * mm});
            skLineSegment(sketch, "E1868", {"start": v(110.72, -6.77) * mm, "end": v(112.55, -6.77) * mm});
            skLineSegment(sketch, "E1869", {"start": v(112.55, -6.77) * mm, "end": v(112.55, -5.97) * mm});
            skLineSegment(sketch, "E1870", {"start": v(112.55, -5.97) * mm, "end": v(113.32, -5.97) * mm});
            skLineSegment(sketch, "E1871", {"start": v(113.32, -5.97) * mm, "end": v(113.32, -6) * mm});
            skLineSegment(sketch, "E1872", {"start": v(113.32, -6) * mm, "end": v(114.12, -6) * mm});
            skLineSegment(sketch, "E1873", {"start": v(114.12, -6) * mm, "end": v(114.12, -7) * mm});
            skLineSegment(sketch, "E1874", {"start": v(114.12, -7) * mm, "end": v(128.12, -7) * mm});
            skLineSegment(sketch, "E1875", {"start": v(128.12, -7) * mm, "end": v(128.12, -6) * mm});
            skLineSegment(sketch, "E1876", {"start": v(128.12, -6) * mm, "end": v(128.93, -6) * mm});
            skLineSegment(sketch, "E1877", {"start": v(128.93, -6) * mm, "end": v(128.93, -5.97) * mm});
            skLineSegment(sketch, "E1878", {"start": v(128.93, -5.97) * mm, "end": v(129.7, -5.97) * mm});
            skLineSegment(sketch, "E1879", {"start": v(129.7, -5.97) * mm, "end": v(129.7, -6.77) * mm});
            skLineSegment(sketch, "E1880", {"start": v(129.7, -6.77) * mm, "end": v(131.52, -6.77) * mm});
            skLineSegment(sketch, "E1881", {"start": v(131.52, -6.77) * mm, "end": v(131.52, -7.97) * mm});
            skLineSegment(sketch, "E1882", {"start": v(131.52, -7.97) * mm, "end": v(134.52, -7.97) * mm});
            skLineSegment(sketch, "E1883", {"start": v(134.52, -7.97) * mm, "end": v(134.52, -6.77) * mm});
            skLineSegment(sketch, "E1884", {"start": v(134.52, -6.77) * mm, "end": v(136.35, -6.77) * mm});
            skLineSegment(sketch, "E1885", {"start": v(136.35, -6.77) * mm, "end": v(136.35, -0.5) * mm});
            skLineSegment(sketch, "E1886", {"start": v(136.35, -0.5) * mm, "end": v(137.23, -0.5) * mm});
            skLineSegment(sketch, "E1887", {"start": v(137.23, -0.5) * mm, "end": v(137.23, 2.3) * mm});
            skLineSegment(sketch, "E1888", {"start": v(137.23, 2.3) * mm, "end": v(136.35, 2.3) * mm});
            skLineSegment(sketch, "E1889", {"start": v(136.35, 2.3) * mm, "end": v(136.35, 5.53) * mm});
            skLineSegment(sketch, "E1890", {"start": v(136.35, 5.53) * mm, "end": v(129.7, 5.53) * mm});
            skLineSegment(sketch, "E1891", {"start": v(129.7, 5.53) * mm, "end": v(129.7, 4.73) * mm});
            skLineSegment(sketch, "E1892", {"start": v(129.7, 4.73) * mm, "end": v(128.93, 4.73) * mm});
            skLineSegment(sketch, "E1893", {"start": v(128.93, 4.73) * mm, "end": v(128.93, 6) * mm});
            skLineSegment(sketch, "E1894", {"start": v(128.93, 6) * mm, "end": v(128.12, 6) * mm});
            skLineSegment(sketch, "E1895", {"start": v(128.12, 6) * mm, "end": v(128.12, 7) * mm});
            skLineSegment(sketch, "E1896", {"start": v(128.12, 7) * mm, "end": v(114.12, 7) * mm});
            skLineSegment(sketch, "E1897", {"start": v(114.12, 7) * mm, "end": v(114.12, 6) * mm});
            skLineSegment(sketch, "E1898", {"start": v(114.12, 6) * mm, "end": v(113.32, 6) * mm});
            skLineSegment(sketch, "E1899", {"start": v(113.32, 6) * mm, "end": v(113.32, 4.73) * mm});
            skLineSegment(sketch, "E1900", {"start": v(113.32, 4.73) * mm, "end": v(112.55, 4.73) * mm});
            skLineSegment(sketch, "E1901", {"start": v(112.55, 4.73) * mm, "end": v(112.55, 5.53) * mm});
            skLineSegment(sketch, "E1902", {"start": v(112.55, 5.53) * mm, "end": v(105.9, 5.53) * mm});
            skLineSegment(sketch, "E1903", {"start": v(105.9, 5.53) * mm, "end": v(105.9, 2.3) * mm});
            skLineSegment(sketch, "E1904", {"start": v(105.9, 2.3) * mm, "end": v(105.03, 2.3) * mm});
            skLineSegment(sketch, "E1905", {"start": v(105.03, 2.3) * mm, "end": v(105.03, -0.5) * mm});
            skLineSegment(sketch, "E1906", {"start": v(105.03, -0.5) * mm, "end": v(105.9, -0.5) * mm});
            skLineSegment(sketch, "E1907", {"start": v(105.9, -0.5) * mm, "end": v(105.9, -6.77) * mm});
            skLineSegment(sketch, "E1908", {"start": v(105.9, -6.77) * mm, "end": v(107.72, -6.77) * mm});
            skLineSegment(sketch, "E1909", {"start": v(107.72, -6.77) * mm, "end": v(107.72, -7.97) * mm});
            skLineSegment(sketch, "E1910", {"start": v(107.72, -7.97) * mm, "end": v(110.72, -7.97) * mm});
            skLineSegment(sketch, "E1911", {"start": v(110.72, -7.97) * mm, "end": v(110.72, -6.77) * mm});
            skLineSegment(sketch, "E1912", {"start": v(-131.53, -25.77) * mm, "end": v(-129.7, -25.77) * mm});
            skLineSegment(sketch, "E1913", {"start": v(-129.7, -25.77) * mm, "end": v(-129.7, -24.97) * mm});
            skLineSegment(sketch, "E1914", {"start": v(-129.7, -24.97) * mm, "end": v(-128.93, -24.97) * mm});
            skLineSegment(sketch, "E1915", {"start": v(-128.93, -24.97) * mm, "end": v(-128.93, -25) * mm});
            skLineSegment(sketch, "E1916", {"start": v(-128.93, -25) * mm, "end": v(-128.12, -25) * mm});
            skLineSegment(sketch, "E1917", {"start": v(-128.12, -25) * mm, "end": v(-128.12, -26) * mm});
            skLineSegment(sketch, "E1918", {"start": v(-128.12, -26) * mm, "end": v(-114.12, -26) * mm});
            skLineSegment(sketch, "E1919", {"start": v(-114.12, -26) * mm, "end": v(-114.12, -25) * mm});
            skLineSegment(sketch, "E1920", {"start": v(-114.12, -25) * mm, "end": v(-113.33, -25) * mm});
            skLineSegment(sketch, "E1921", {"start": v(-113.33, -25) * mm, "end": v(-113.33, -24.97) * mm});
            skLineSegment(sketch, "E1922", {"start": v(-113.33, -24.97) * mm, "end": v(-112.55, -24.97) * mm});
            skLineSegment(sketch, "E1923", {"start": v(-112.55, -24.97) * mm, "end": v(-112.55, -25.77) * mm});
            skLineSegment(sketch, "E1924", {"start": v(-112.55, -25.77) * mm, "end": v(-110.72, -25.77) * mm});
            skLineSegment(sketch, "E1925", {"start": v(-110.72, -25.77) * mm, "end": v(-110.72, -26.97) * mm});
            skLineSegment(sketch, "E1926", {"start": v(-110.72, -26.97) * mm, "end": v(-107.72, -26.97) * mm});
            skLineSegment(sketch, "E1927", {"start": v(-107.72, -26.97) * mm, "end": v(-107.72, -25.77) * mm});
            skLineSegment(sketch, "E1928", {"start": v(-107.72, -25.77) * mm, "end": v(-105.9, -25.77) * mm});
            skLineSegment(sketch, "E1929", {"start": v(-105.9, -25.77) * mm, "end": v(-105.9, -19.5) * mm});
            skLineSegment(sketch, "E1930", {"start": v(-105.9, -19.5) * mm, "end": v(-105.03, -19.5) * mm});
            skLineSegment(sketch, "E1931", {"start": v(-105.03, -19.5) * mm, "end": v(-105.03, -16.7) * mm});
            skLineSegment(sketch, "E1932", {"start": v(-105.03, -16.7) * mm, "end": v(-105.9, -16.7) * mm});
            skLineSegment(sketch, "E1933", {"start": v(-105.9, -16.7) * mm, "end": v(-105.9, -13.47) * mm});
            skLineSegment(sketch, "E1934", {"start": v(-105.9, -13.47) * mm, "end": v(-112.55, -13.47) * mm});
            skLineSegment(sketch, "E1935", {"start": v(-112.55, -13.47) * mm, "end": v(-112.55, -14.27) * mm});
            skLineSegment(sketch, "E1936", {"start": v(-112.55, -14.27) * mm, "end": v(-113.33, -14.27) * mm});
            skLineSegment(sketch, "E1937", {"start": v(-113.33, -14.27) * mm, "end": v(-113.33, -13) * mm});
            skLineSegment(sketch, "E1938", {"start": v(-113.33, -13) * mm, "end": v(-114.12, -13) * mm});
            skLineSegment(sketch, "E1939", {"start": v(-114.12, -13) * mm, "end": v(-114.12, -12) * mm});
            skLineSegment(sketch, "E1940", {"start": v(-114.12, -12) * mm, "end": v(-128.12, -12) * mm});
            skLineSegment(sketch, "E1941", {"start": v(-128.12, -12) * mm, "end": v(-128.12, -13) * mm});
            skLineSegment(sketch, "E1942", {"start": v(-128.12, -13) * mm, "end": v(-128.93, -13) * mm});
            skLineSegment(sketch, "E1943", {"start": v(-128.93, -13) * mm, "end": v(-128.93, -14.27) * mm});
            skLineSegment(sketch, "E1944", {"start": v(-128.93, -14.27) * mm, "end": v(-129.7, -14.27) * mm});
            skLineSegment(sketch, "E1945", {"start": v(-129.7, -14.27) * mm, "end": v(-129.7, -13.47) * mm});
            skLineSegment(sketch, "E1946", {"start": v(-129.7, -13.47) * mm, "end": v(-136.35, -13.47) * mm});
            skLineSegment(sketch, "E1947", {"start": v(-136.35, -13.47) * mm, "end": v(-136.35, -16.7) * mm});
            skLineSegment(sketch, "E1948", {"start": v(-136.35, -16.7) * mm, "end": v(-137.22, -16.7) * mm});
            skLineSegment(sketch, "E1949", {"start": v(-137.22, -16.7) * mm, "end": v(-137.22, -19.5) * mm});
            skLineSegment(sketch, "E1950", {"start": v(-137.22, -19.5) * mm, "end": v(-136.35, -19.5) * mm});
            skLineSegment(sketch, "E1951", {"start": v(-136.35, -19.5) * mm, "end": v(-136.35, -25.77) * mm});
            skLineSegment(sketch, "E1952", {"start": v(-136.35, -25.77) * mm, "end": v(-134.53, -25.77) * mm});
            skLineSegment(sketch, "E1953", {"start": v(-134.53, -25.77) * mm, "end": v(-134.53, -26.97) * mm});
            skLineSegment(sketch, "E1954", {"start": v(-134.53, -26.97) * mm, "end": v(-131.53, -26.97) * mm});
            skLineSegment(sketch, "E1955", {"start": v(-131.53, -26.97) * mm, "end": v(-131.53, -25.77) * mm});
            skLineSegment(sketch, "E1956", {"start": v(-83.25, -25) * mm, "end": v(-82.45, -25) * mm});
            skLineSegment(sketch, "E1957", {"start": v(-82.45, -25) * mm, "end": v(-82.45, -13) * mm});
            skLineSegment(sketch, "E1958", {"start": v(-82.45, -13) * mm, "end": v(-83.25, -13) * mm});
            skLineSegment(sketch, "E1959", {"start": v(-83.25, -13) * mm, "end": v(-83.25, -12) * mm});
            skLineSegment(sketch, "E1960", {"start": v(-83.25, -12) * mm, "end": v(-97.25, -12) * mm});
            skLineSegment(sketch, "E1961", {"start": v(-97.25, -12) * mm, "end": v(-97.25, -13) * mm});
            skLineSegment(sketch, "E1962", {"start": v(-97.25, -13) * mm, "end": v(-98.05, -13) * mm});
            skLineSegment(sketch, "E1963", {"start": v(-98.05, -13) * mm, "end": v(-98.05, -25) * mm});
            skLineSegment(sketch, "E1964", {"start": v(-98.05, -25) * mm, "end": v(-97.25, -25) * mm});
            skLineSegment(sketch, "E1965", {"start": v(-97.25, -25) * mm, "end": v(-97.25, -26) * mm});
            skLineSegment(sketch, "E1966", {"start": v(-97.25, -26) * mm, "end": v(-83.25, -26) * mm});
            skLineSegment(sketch, "E1967", {"start": v(-83.25, -26) * mm, "end": v(-83.25, -25) * mm});
            skLineSegment(sketch, "E1968", {"start": v(-64.25, -25) * mm, "end": v(-63.45, -25) * mm});
            skLineSegment(sketch, "E1969", {"start": v(-63.45, -25) * mm, "end": v(-63.45, -13) * mm});
            skLineSegment(sketch, "E1970", {"start": v(-63.45, -13) * mm, "end": v(-64.25, -13) * mm});
            skLineSegment(sketch, "E1971", {"start": v(-64.25, -13) * mm, "end": v(-64.25, -12) * mm});
            skLineSegment(sketch, "E1972", {"start": v(-64.25, -12) * mm, "end": v(-78.25, -12) * mm});
            skLineSegment(sketch, "E1973", {"start": v(-78.25, -12) * mm, "end": v(-78.25, -13) * mm});
            skLineSegment(sketch, "E1974", {"start": v(-78.25, -13) * mm, "end": v(-79.05, -13) * mm});
            skLineSegment(sketch, "E1975", {"start": v(-79.05, -13) * mm, "end": v(-79.05, -25) * mm});
            skLineSegment(sketch, "E1976", {"start": v(-79.05, -25) * mm, "end": v(-78.25, -25) * mm});
            skLineSegment(sketch, "E1977", {"start": v(-78.25, -25) * mm, "end": v(-78.25, -26) * mm});
            skLineSegment(sketch, "E1978", {"start": v(-78.25, -26) * mm, "end": v(-64.25, -26) * mm});
            skLineSegment(sketch, "E1979", {"start": v(-64.25, -26) * mm, "end": v(-64.25, -25) * mm});
            skLineSegment(sketch, "E1980", {"start": v(-45.25, -25) * mm, "end": v(-44.45, -25) * mm});
            skLineSegment(sketch, "E1981", {"start": v(-44.45, -25) * mm, "end": v(-44.45, -13) * mm});
            skLineSegment(sketch, "E1982", {"start": v(-44.45, -13) * mm, "end": v(-45.25, -13) * mm});
            skLineSegment(sketch, "E1983", {"start": v(-45.25, -13) * mm, "end": v(-45.25, -12) * mm});
            skLineSegment(sketch, "E1984", {"start": v(-45.25, -12) * mm, "end": v(-59.25, -12) * mm});
            skLineSegment(sketch, "E1985", {"start": v(-59.25, -12) * mm, "end": v(-59.25, -13) * mm});
            skLineSegment(sketch, "E1986", {"start": v(-59.25, -13) * mm, "end": v(-60.05, -13) * mm});
            skLineSegment(sketch, "E1987", {"start": v(-60.05, -13) * mm, "end": v(-60.05, -25) * mm});
            skLineSegment(sketch, "E1988", {"start": v(-60.05, -25) * mm, "end": v(-59.25, -25) * mm});
            skLineSegment(sketch, "E1989", {"start": v(-59.25, -25) * mm, "end": v(-59.25, -26) * mm});
            skLineSegment(sketch, "E1990", {"start": v(-59.25, -26) * mm, "end": v(-45.25, -26) * mm});
            skLineSegment(sketch, "E1991", {"start": v(-45.25, -26) * mm, "end": v(-45.25, -25) * mm});
            skLineSegment(sketch, "E1992", {"start": v(-26.25, -25) * mm, "end": v(-25.45, -25) * mm});
            skLineSegment(sketch, "E1993", {"start": v(-25.45, -25) * mm, "end": v(-25.45, -13) * mm});
            skLineSegment(sketch, "E1994", {"start": v(-25.45, -13) * mm, "end": v(-26.25, -13) * mm});
            skLineSegment(sketch, "E1995", {"start": v(-26.25, -13) * mm, "end": v(-26.25, -12) * mm});
            skLineSegment(sketch, "E1996", {"start": v(-26.25, -12) * mm, "end": v(-40.25, -12) * mm});
            skLineSegment(sketch, "E1997", {"start": v(-40.25, -12) * mm, "end": v(-40.25, -13) * mm});
            skLineSegment(sketch, "E1998", {"start": v(-40.25, -13) * mm, "end": v(-41.05, -13) * mm});
            skLineSegment(sketch, "E1999", {"start": v(-41.05, -13) * mm, "end": v(-41.05, -25) * mm});
            skLineSegment(sketch, "E2000", {"start": v(-41.05, -25) * mm, "end": v(-40.25, -25) * mm});
            skLineSegment(sketch, "E2001", {"start": v(-40.25, -25) * mm, "end": v(-40.25, -26) * mm});
            skLineSegment(sketch, "E2002", {"start": v(-40.25, -26) * mm, "end": v(-26.25, -26) * mm});
            skLineSegment(sketch, "E2003", {"start": v(-26.25, -26) * mm, "end": v(-26.25, -25) * mm});
            skLineSegment(sketch, "E2004", {"start": v(-7.25, -25) * mm, "end": v(-6.45, -25) * mm});
            skLineSegment(sketch, "E2005", {"start": v(-6.45, -25) * mm, "end": v(-6.45, -13) * mm});
            skLineSegment(sketch, "E2006", {"start": v(-6.45, -13) * mm, "end": v(-7.25, -13) * mm});
            skLineSegment(sketch, "E2007", {"start": v(-7.25, -13) * mm, "end": v(-7.25, -12) * mm});
            skLineSegment(sketch, "E2008", {"start": v(-7.25, -12) * mm, "end": v(-21.25, -12) * mm});
            skLineSegment(sketch, "E2009", {"start": v(-21.25, -12) * mm, "end": v(-21.25, -13) * mm});
            skLineSegment(sketch, "E2010", {"start": v(-21.25, -13) * mm, "end": v(-22.05, -13) * mm});
            skLineSegment(sketch, "E2011", {"start": v(-22.05, -13) * mm, "end": v(-22.05, -25) * mm});
            skLineSegment(sketch, "E2012", {"start": v(-22.05, -25) * mm, "end": v(-21.25, -25) * mm});
            skLineSegment(sketch, "E2013", {"start": v(-21.25, -25) * mm, "end": v(-21.25, -26) * mm});
            skLineSegment(sketch, "E2014", {"start": v(-21.25, -26) * mm, "end": v(-7.25, -26) * mm});
            skLineSegment(sketch, "E2015", {"start": v(-7.25, -26) * mm, "end": v(-7.25, -25) * mm});
            skLineSegment(sketch, "E2016", {"start": v(11.75, -25) * mm, "end": v(12.55, -25) * mm});
            skLineSegment(sketch, "E2017", {"start": v(12.55, -25) * mm, "end": v(12.55, -13) * mm});
            skLineSegment(sketch, "E2018", {"start": v(12.55, -13) * mm, "end": v(11.75, -13) * mm});
            skLineSegment(sketch, "E2019", {"start": v(11.75, -13) * mm, "end": v(11.75, -12) * mm});
            skLineSegment(sketch, "E2020", {"start": v(11.75, -12) * mm, "end": v(-2.25, -12) * mm});
            skLineSegment(sketch, "E2021", {"start": v(-2.25, -12) * mm, "end": v(-2.25, -13) * mm});
            skLineSegment(sketch, "E2022", {"start": v(-2.25, -13) * mm, "end": v(-3.05, -13) * mm});
            skLineSegment(sketch, "E2023", {"start": v(-3.05, -13) * mm, "end": v(-3.05, -25) * mm});
            skLineSegment(sketch, "E2024", {"start": v(-3.05, -25) * mm, "end": v(-2.25, -25) * mm});
            skLineSegment(sketch, "E2025", {"start": v(-2.25, -25) * mm, "end": v(-2.25, -26) * mm});
            skLineSegment(sketch, "E2026", {"start": v(-2.25, -26) * mm, "end": v(11.75, -26) * mm});
            skLineSegment(sketch, "E2027", {"start": v(11.75, -26) * mm, "end": v(11.75, -25) * mm});
            skLineSegment(sketch, "E2028", {"start": v(30.75, -25) * mm, "end": v(31.55, -25) * mm});
            skLineSegment(sketch, "E2029", {"start": v(31.55, -25) * mm, "end": v(31.55, -13) * mm});
            skLineSegment(sketch, "E2030", {"start": v(31.55, -13) * mm, "end": v(30.75, -13) * mm});
            skLineSegment(sketch, "E2031", {"start": v(30.75, -13) * mm, "end": v(30.75, -12) * mm});
            skLineSegment(sketch, "E2032", {"start": v(30.75, -12) * mm, "end": v(16.75, -12) * mm});
            skLineSegment(sketch, "E2033", {"start": v(16.75, -12) * mm, "end": v(16.75, -13) * mm});
            skLineSegment(sketch, "E2034", {"start": v(16.75, -13) * mm, "end": v(15.95, -13) * mm});
            skLineSegment(sketch, "E2035", {"start": v(15.95, -13) * mm, "end": v(15.95, -25) * mm});
            skLineSegment(sketch, "E2036", {"start": v(15.95, -25) * mm, "end": v(16.75, -25) * mm});
            skLineSegment(sketch, "E2037", {"start": v(16.75, -25) * mm, "end": v(16.75, -26) * mm});
            skLineSegment(sketch, "E2038", {"start": v(16.75, -26) * mm, "end": v(30.75, -26) * mm});
            skLineSegment(sketch, "E2039", {"start": v(30.75, -26) * mm, "end": v(30.75, -25) * mm});
            skLineSegment(sketch, "E2040", {"start": v(49.75, -25) * mm, "end": v(50.55, -25) * mm});
            skLineSegment(sketch, "E2041", {"start": v(50.55, -25) * mm, "end": v(50.55, -13) * mm});
            skLineSegment(sketch, "E2042", {"start": v(50.55, -13) * mm, "end": v(49.75, -13) * mm});
            skLineSegment(sketch, "E2043", {"start": v(49.75, -13) * mm, "end": v(49.75, -12) * mm});
            skLineSegment(sketch, "E2044", {"start": v(49.75, -12) * mm, "end": v(35.75, -12) * mm});
            skLineSegment(sketch, "E2045", {"start": v(35.75, -12) * mm, "end": v(35.75, -13) * mm});
            skLineSegment(sketch, "E2046", {"start": v(35.75, -13) * mm, "end": v(34.95, -13) * mm});
            skLineSegment(sketch, "E2047", {"start": v(34.95, -13) * mm, "end": v(34.95, -25) * mm});
            skLineSegment(sketch, "E2048", {"start": v(34.95, -25) * mm, "end": v(35.75, -25) * mm});
            skLineSegment(sketch, "E2049", {"start": v(35.75, -25) * mm, "end": v(35.75, -26) * mm});
            skLineSegment(sketch, "E2050", {"start": v(35.75, -26) * mm, "end": v(49.75, -26) * mm});
            skLineSegment(sketch, "E2051", {"start": v(49.75, -26) * mm, "end": v(49.75, -25) * mm});
            skLineSegment(sketch, "E2052", {"start": v(68.75, -25) * mm, "end": v(69.55, -25) * mm});
            skLineSegment(sketch, "E2053", {"start": v(69.55, -25) * mm, "end": v(69.55, -13) * mm});
            skLineSegment(sketch, "E2054", {"start": v(69.55, -13) * mm, "end": v(68.75, -13) * mm});
            skLineSegment(sketch, "E2055", {"start": v(68.75, -13) * mm, "end": v(68.75, -12) * mm});
            skLineSegment(sketch, "E2056", {"start": v(68.75, -12) * mm, "end": v(54.75, -12) * mm});
            skLineSegment(sketch, "E2057", {"start": v(54.75, -12) * mm, "end": v(54.75, -13) * mm});
            skLineSegment(sketch, "E2058", {"start": v(54.75, -13) * mm, "end": v(53.95, -13) * mm});
            skLineSegment(sketch, "E2059", {"start": v(53.95, -13) * mm, "end": v(53.95, -25) * mm});
            skLineSegment(sketch, "E2060", {"start": v(53.95, -25) * mm, "end": v(54.75, -25) * mm});
            skLineSegment(sketch, "E2061", {"start": v(54.75, -25) * mm, "end": v(54.75, -26) * mm});
            skLineSegment(sketch, "E2062", {"start": v(54.75, -26) * mm, "end": v(68.75, -26) * mm});
            skLineSegment(sketch, "E2063", {"start": v(68.75, -26) * mm, "end": v(68.75, -25) * mm});
            skLineSegment(sketch, "E2064", {"start": v(87.75, -25) * mm, "end": v(88.55, -25) * mm});
            skLineSegment(sketch, "E2065", {"start": v(88.55, -25) * mm, "end": v(88.55, -13) * mm});
            skLineSegment(sketch, "E2066", {"start": v(88.55, -13) * mm, "end": v(87.75, -13) * mm});
            skLineSegment(sketch, "E2067", {"start": v(87.75, -13) * mm, "end": v(87.75, -12) * mm});
            skLineSegment(sketch, "E2068", {"start": v(87.75, -12) * mm, "end": v(73.75, -12) * mm});
            skLineSegment(sketch, "E2069", {"start": v(73.75, -12) * mm, "end": v(73.75, -13) * mm});
            skLineSegment(sketch, "E2070", {"start": v(73.75, -13) * mm, "end": v(72.95, -13) * mm});
            skLineSegment(sketch, "E2071", {"start": v(72.95, -13) * mm, "end": v(72.95, -25) * mm});
            skLineSegment(sketch, "E2072", {"start": v(72.95, -25) * mm, "end": v(73.75, -25) * mm});
            skLineSegment(sketch, "E2073", {"start": v(73.75, -25) * mm, "end": v(73.75, -26) * mm});
            skLineSegment(sketch, "E2074", {"start": v(73.75, -26) * mm, "end": v(87.75, -26) * mm});
            skLineSegment(sketch, "E2075", {"start": v(87.75, -26) * mm, "end": v(87.75, -25) * mm});
            skLineSegment(sketch, "E2076", {"start": v(105.97, -25.77) * mm, "end": v(107.8, -25.77) * mm});
            skLineSegment(sketch, "E2077", {"start": v(107.8, -25.77) * mm, "end": v(107.8, -24.97) * mm});
            skLineSegment(sketch, "E2078", {"start": v(107.8, -24.97) * mm, "end": v(108.57, -24.97) * mm});
            skLineSegment(sketch, "E2079", {"start": v(108.57, -24.97) * mm, "end": v(108.57, -25) * mm});
            skLineSegment(sketch, "E2080", {"start": v(108.57, -25) * mm, "end": v(109.38, -25) * mm});
            skLineSegment(sketch, "E2081", {"start": v(109.38, -25) * mm, "end": v(109.38, -26) * mm});
            skLineSegment(sketch, "E2082", {"start": v(109.38, -26) * mm, "end": v(123.38, -26) * mm});
            skLineSegment(sketch, "E2083", {"start": v(123.38, -26) * mm, "end": v(123.38, -25) * mm});
            skLineSegment(sketch, "E2084", {"start": v(123.38, -25) * mm, "end": v(124.18, -25) * mm});
            skLineSegment(sketch, "E2085", {"start": v(124.18, -25) * mm, "end": v(124.18, -24.97) * mm});
            skLineSegment(sketch, "E2086", {"start": v(124.18, -24.97) * mm, "end": v(124.95, -24.97) * mm});
            skLineSegment(sketch, "E2087", {"start": v(124.95, -24.97) * mm, "end": v(124.95, -25.77) * mm});
            skLineSegment(sketch, "E2088", {"start": v(124.95, -25.77) * mm, "end": v(126.77, -25.77) * mm});
            skLineSegment(sketch, "E2089", {"start": v(126.77, -25.77) * mm, "end": v(126.77, -26.97) * mm});
            skLineSegment(sketch, "E2090", {"start": v(126.77, -26.97) * mm, "end": v(129.77, -26.97) * mm});
            skLineSegment(sketch, "E2091", {"start": v(129.77, -26.97) * mm, "end": v(129.77, -25.77) * mm});
            skLineSegment(sketch, "E2092", {"start": v(129.77, -25.77) * mm, "end": v(131.6, -25.77) * mm});
            skLineSegment(sketch, "E2093", {"start": v(131.6, -25.77) * mm, "end": v(131.6, -19.5) * mm});
            skLineSegment(sketch, "E2094", {"start": v(131.6, -19.5) * mm, "end": v(132.48, -19.5) * mm});
            skLineSegment(sketch, "E2095", {"start": v(132.48, -19.5) * mm, "end": v(132.48, -16.7) * mm});
            skLineSegment(sketch, "E2096", {"start": v(132.48, -16.7) * mm, "end": v(131.6, -16.7) * mm});
            skLineSegment(sketch, "E2097", {"start": v(131.6, -16.7) * mm, "end": v(131.6, -13.47) * mm});
            skLineSegment(sketch, "E2098", {"start": v(131.6, -13.47) * mm, "end": v(124.95, -13.47) * mm});
            skLineSegment(sketch, "E2099", {"start": v(124.95, -13.47) * mm, "end": v(124.95, -14.27) * mm});
            skLineSegment(sketch, "E2100", {"start": v(124.95, -14.27) * mm, "end": v(124.18, -14.27) * mm});
            skLineSegment(sketch, "E2101", {"start": v(124.18, -14.27) * mm, "end": v(124.18, -13) * mm});
            skLineSegment(sketch, "E2102", {"start": v(124.18, -13) * mm, "end": v(123.38, -13) * mm});
            skLineSegment(sketch, "E2103", {"start": v(123.38, -13) * mm, "end": v(123.38, -12) * mm});
            skLineSegment(sketch, "E2104", {"start": v(123.38, -12) * mm, "end": v(109.38, -12) * mm});
            skLineSegment(sketch, "E2105", {"start": v(109.38, -12) * mm, "end": v(109.38, -13) * mm});
            skLineSegment(sketch, "E2106", {"start": v(109.38, -13) * mm, "end": v(108.57, -13) * mm});
            skLineSegment(sketch, "E2107", {"start": v(108.57, -13) * mm, "end": v(108.57, -14.27) * mm});
            skLineSegment(sketch, "E2108", {"start": v(108.57, -14.27) * mm, "end": v(107.8, -14.27) * mm});
            skLineSegment(sketch, "E2109", {"start": v(107.8, -14.27) * mm, "end": v(107.8, -13.47) * mm});
            skLineSegment(sketch, "E2110", {"start": v(107.8, -13.47) * mm, "end": v(101.15, -13.47) * mm});
            skLineSegment(sketch, "E2111", {"start": v(101.15, -13.47) * mm, "end": v(101.15, -16.7) * mm});
            skLineSegment(sketch, "E2112", {"start": v(101.15, -16.7) * mm, "end": v(100.28, -16.7) * mm});
            skLineSegment(sketch, "E2113", {"start": v(100.28, -16.7) * mm, "end": v(100.28, -19.5) * mm});
            skLineSegment(sketch, "E2114", {"start": v(100.28, -19.5) * mm, "end": v(101.15, -19.5) * mm});
            skLineSegment(sketch, "E2115", {"start": v(101.15, -19.5) * mm, "end": v(101.15, -25.77) * mm});
            skLineSegment(sketch, "E2116", {"start": v(101.15, -25.77) * mm, "end": v(102.97, -25.77) * mm});
            skLineSegment(sketch, "E2117", {"start": v(102.97, -25.77) * mm, "end": v(102.97, -26.97) * mm});
            skLineSegment(sketch, "E2118", {"start": v(102.97, -26.97) * mm, "end": v(105.97, -26.97) * mm});
            skLineSegment(sketch, "E2119", {"start": v(105.97, -26.97) * mm, "end": v(105.97, -25.77) * mm});
            skLineSegment(sketch, "E2120", {"start": v(-123.62, -44) * mm, "end": v(-122.83, -44) * mm});
            skLineSegment(sketch, "E2121", {"start": v(-122.83, -44) * mm, "end": v(-122.83, -32) * mm});
            skLineSegment(sketch, "E2122", {"start": v(-122.83, -32) * mm, "end": v(-123.62, -32) * mm});
            skLineSegment(sketch, "E2123", {"start": v(-123.62, -32) * mm, "end": v(-123.62, -31) * mm});
            skLineSegment(sketch, "E2124", {"start": v(-123.62, -31) * mm, "end": v(-137.62, -31) * mm});
            skLineSegment(sketch, "E2125", {"start": v(-137.62, -31) * mm, "end": v(-137.62, -32) * mm});
            skLineSegment(sketch, "E2126", {"start": v(-137.62, -32) * mm, "end": v(-138.43, -32) * mm});
            skLineSegment(sketch, "E2127", {"start": v(-138.43, -32) * mm, "end": v(-138.43, -44) * mm});
            skLineSegment(sketch, "E2128", {"start": v(-138.43, -44) * mm, "end": v(-137.62, -44) * mm});
            skLineSegment(sketch, "E2129", {"start": v(-137.62, -44) * mm, "end": v(-137.62, -45) * mm});
            skLineSegment(sketch, "E2130", {"start": v(-137.62, -45) * mm, "end": v(-123.62, -45) * mm});
            skLineSegment(sketch, "E2131", {"start": v(-123.62, -45) * mm, "end": v(-123.62, -44) * mm});
            skLineSegment(sketch, "E2132", {"start": v(-99.88, -44) * mm, "end": v(-99.08, -44) * mm});
            skLineSegment(sketch, "E2133", {"start": v(-99.08, -44) * mm, "end": v(-99.08, -32) * mm});
            skLineSegment(sketch, "E2134", {"start": v(-99.08, -32) * mm, "end": v(-99.88, -32) * mm});
            skLineSegment(sketch, "E2135", {"start": v(-99.88, -32) * mm, "end": v(-99.88, -31) * mm});
            skLineSegment(sketch, "E2136", {"start": v(-99.88, -31) * mm, "end": v(-113.88, -31) * mm});
            skLineSegment(sketch, "E2137", {"start": v(-113.88, -31) * mm, "end": v(-113.88, -32) * mm});
            skLineSegment(sketch, "E2138", {"start": v(-113.88, -32) * mm, "end": v(-114.67, -32) * mm});
            skLineSegment(sketch, "E2139", {"start": v(-114.67, -32) * mm, "end": v(-114.67, -44) * mm});
            skLineSegment(sketch, "E2140", {"start": v(-114.67, -44) * mm, "end": v(-113.88, -44) * mm});
            skLineSegment(sketch, "E2141", {"start": v(-113.88, -44) * mm, "end": v(-113.88, -45) * mm});
            skLineSegment(sketch, "E2142", {"start": v(-113.88, -45) * mm, "end": v(-99.88, -45) * mm});
            skLineSegment(sketch, "E2143", {"start": v(-99.88, -45) * mm, "end": v(-99.88, -44) * mm});
            skLineSegment(sketch, "E2144", {"start": v(-76.12, -44) * mm, "end": v(-75.33, -44) * mm});
            skLineSegment(sketch, "E2145", {"start": v(-75.33, -44) * mm, "end": v(-75.33, -32) * mm});
            skLineSegment(sketch, "E2146", {"start": v(-75.33, -32) * mm, "end": v(-76.12, -32) * mm});
            skLineSegment(sketch, "E2147", {"start": v(-76.12, -32) * mm, "end": v(-76.12, -31) * mm});
            skLineSegment(sketch, "E2148", {"start": v(-76.12, -31) * mm, "end": v(-90.12, -31) * mm});
            skLineSegment(sketch, "E2149", {"start": v(-90.12, -31) * mm, "end": v(-90.12, -32) * mm});
            skLineSegment(sketch, "E2150", {"start": v(-90.12, -32) * mm, "end": v(-90.93, -32) * mm});
            skLineSegment(sketch, "E2151", {"start": v(-90.93, -32) * mm, "end": v(-90.93, -44) * mm});
            skLineSegment(sketch, "E2152", {"start": v(-90.93, -44) * mm, "end": v(-90.12, -44) * mm});
            skLineSegment(sketch, "E2153", {"start": v(-90.12, -44) * mm, "end": v(-90.12, -45) * mm});
            skLineSegment(sketch, "E2154", {"start": v(-90.12, -45) * mm, "end": v(-76.12, -45) * mm});
            skLineSegment(sketch, "E2155", {"start": v(-76.12, -45) * mm, "end": v(-76.12, -44) * mm});
            skLineSegment(sketch, "E2156", {"start": v(-60.38, -44.77) * mm, "end": v(-58.55, -44.77) * mm});
            skLineSegment(sketch, "E2157", {"start": v(-58.55, -44.77) * mm, "end": v(-58.55, -40.3) * mm});
            skLineSegment(sketch, "E2158", {"start": v(-58.55, -40.3) * mm, "end": v(-19.67, -40.3) * mm});
            skLineSegment(sketch, "E2159", {"start": v(-19.67, -40.3) * mm, "end": v(-19.67, -44) * mm});
            skLineSegment(sketch, "E2160", {"start": v(-19.67, -44) * mm, "end": v(-18.88, -44) * mm});
            skLineSegment(sketch, "E2161", {"start": v(-18.88, -44) * mm, "end": v(-18.88, -45) * mm});
            skLineSegment(sketch, "E2162", {"start": v(-18.88, -45) * mm, "end": v(-4.88, -45) * mm});
            skLineSegment(sketch, "E2163", {"start": v(-4.88, -45) * mm, "end": v(-4.88, -44) * mm});
            skLineSegment(sketch, "E2164", {"start": v(-4.88, -44) * mm, "end": v(-4.07, -44) * mm});
            skLineSegment(sketch, "E2165", {"start": v(-4.07, -44) * mm, "end": v(-4.07, -40.3) * mm});
            skLineSegment(sketch, "E2166", {"start": v(-4.07, -40.3) * mm, "end": v(34.8, -40.3) * mm});
            skLineSegment(sketch, "E2167", {"start": v(34.8, -40.3) * mm, "end": v(34.8, -44.77) * mm});
            skLineSegment(sketch, "E2168", {"start": v(34.8, -44.77) * mm, "end": v(36.62, -44.77) * mm});
            skLineSegment(sketch, "E2169", {"start": v(36.62, -44.77) * mm, "end": v(36.62, -45.97) * mm});
            skLineSegment(sketch, "E2170", {"start": v(36.62, -45.97) * mm, "end": v(39.62, -45.97) * mm});
            skLineSegment(sketch, "E2171", {"start": v(39.62, -45.97) * mm, "end": v(39.62, -44.77) * mm});
            skLineSegment(sketch, "E2172", {"start": v(39.62, -44.77) * mm, "end": v(41.45, -44.77) * mm});
            skLineSegment(sketch, "E2173", {"start": v(41.45, -44.77) * mm, "end": v(41.45, -38.5) * mm});
            skLineSegment(sketch, "E2174", {"start": v(41.45, -38.5) * mm, "end": v(42.35, -38.5) * mm});
            skLineSegment(sketch, "E2175", {"start": v(42.35, -38.5) * mm, "end": v(42.35, -35.7) * mm});
            skLineSegment(sketch, "E2176", {"start": v(42.35, -35.7) * mm, "end": v(41.45, -35.7) * mm});
            skLineSegment(sketch, "E2177", {"start": v(41.45, -35.7) * mm, "end": v(41.45, -32.47) * mm});
            skLineSegment(sketch, "E2178", {"start": v(41.45, -32.47) * mm, "end": v(34.8, -32.47) * mm});
            skLineSegment(sketch, "E2179", {"start": v(34.8, -32.47) * mm, "end": v(34.8, -35.7) * mm});
            skLineSegment(sketch, "E2180", {"start": v(34.8, -35.7) * mm, "end": v(-4.07, -35.7) * mm});
            skLineSegment(sketch, "E2181", {"start": v(-4.07, -35.7) * mm, "end": v(-4.07, -32) * mm});
            skLineSegment(sketch, "E2182", {"start": v(-4.07, -32) * mm, "end": v(-4.88, -32) * mm});
            skLineSegment(sketch, "E2183", {"start": v(-4.88, -32) * mm, "end": v(-4.88, -31) * mm});
            skLineSegment(sketch, "E2184", {"start": v(-4.88, -31) * mm, "end": v(-18.88, -31) * mm});
            skLineSegment(sketch, "E2185", {"start": v(-18.88, -31) * mm, "end": v(-18.88, -32) * mm});
            skLineSegment(sketch, "E2186", {"start": v(-18.88, -32) * mm, "end": v(-19.67, -32) * mm});
            skLineSegment(sketch, "E2187", {"start": v(-19.67, -32) * mm, "end": v(-19.67, -35.7) * mm});
            skLineSegment(sketch, "E2188", {"start": v(-19.67, -35.7) * mm, "end": v(-58.55, -35.7) * mm});
            skLineSegment(sketch, "E2189", {"start": v(-58.55, -35.7) * mm, "end": v(-58.55, -32.47) * mm});
            skLineSegment(sketch, "E2190", {"start": v(-58.55, -32.47) * mm, "end": v(-65.2, -32.47) * mm});
            skLineSegment(sketch, "E2191", {"start": v(-65.2, -32.47) * mm, "end": v(-65.2, -35.7) * mm});
            skLineSegment(sketch, "E2192", {"start": v(-65.2, -35.7) * mm, "end": v(-66.1, -35.7) * mm});
            skLineSegment(sketch, "E2193", {"start": v(-66.1, -35.7) * mm, "end": v(-66.1, -38.5) * mm});
            skLineSegment(sketch, "E2194", {"start": v(-66.1, -38.5) * mm, "end": v(-65.2, -38.5) * mm});
            skLineSegment(sketch, "E2195", {"start": v(-65.2, -38.5) * mm, "end": v(-65.2, -44.77) * mm});
            skLineSegment(sketch, "E2196", {"start": v(-65.2, -44.77) * mm, "end": v(-63.38, -44.77) * mm});
            skLineSegment(sketch, "E2197", {"start": v(-63.38, -44.77) * mm, "end": v(-63.38, -45.97) * mm});
            skLineSegment(sketch, "E2198", {"start": v(-63.38, -45.97) * mm, "end": v(-60.38, -45.97) * mm});
            skLineSegment(sketch, "E2199", {"start": v(-60.38, -45.97) * mm, "end": v(-60.38, -44.77) * mm});
            skLineSegment(sketch, "E2200", {"start": v(66.38, -44) * mm, "end": v(67.18, -44) * mm});
            skLineSegment(sketch, "E2201", {"start": v(67.18, -44) * mm, "end": v(67.18, -32) * mm});
            skLineSegment(sketch, "E2202", {"start": v(67.18, -32) * mm, "end": v(66.38, -32) * mm});
            skLineSegment(sketch, "E2203", {"start": v(66.38, -32) * mm, "end": v(66.38, -31) * mm});
            skLineSegment(sketch, "E2204", {"start": v(66.38, -31) * mm, "end": v(52.38, -31) * mm});
            skLineSegment(sketch, "E2205", {"start": v(52.38, -31) * mm, "end": v(52.38, -32) * mm});
            skLineSegment(sketch, "E2206", {"start": v(52.38, -32) * mm, "end": v(51.57, -32) * mm});
            skLineSegment(sketch, "E2207", {"start": v(51.57, -32) * mm, "end": v(51.57, -44) * mm});
            skLineSegment(sketch, "E2208", {"start": v(51.57, -44) * mm, "end": v(52.38, -44) * mm});
            skLineSegment(sketch, "E2209", {"start": v(52.38, -44) * mm, "end": v(52.38, -45) * mm});
            skLineSegment(sketch, "E2210", {"start": v(52.38, -45) * mm, "end": v(66.38, -45) * mm});
            skLineSegment(sketch, "E2211", {"start": v(66.38, -45) * mm, "end": v(66.38, -44) * mm});
            skLineSegment(sketch, "E2212", {"start": v(90.12, -44) * mm, "end": v(90.93, -44) * mm});
            skLineSegment(sketch, "E2213", {"start": v(90.93, -44) * mm, "end": v(90.93, -32) * mm});
            skLineSegment(sketch, "E2214", {"start": v(90.93, -32) * mm, "end": v(90.12, -32) * mm});
            skLineSegment(sketch, "E2215", {"start": v(90.12, -32) * mm, "end": v(90.12, -31) * mm});
            skLineSegment(sketch, "E2216", {"start": v(90.12, -31) * mm, "end": v(76.12, -31) * mm});
            skLineSegment(sketch, "E2217", {"start": v(76.12, -31) * mm, "end": v(76.12, -32) * mm});
            skLineSegment(sketch, "E2218", {"start": v(76.12, -32) * mm, "end": v(75.32, -32) * mm});
            skLineSegment(sketch, "E2219", {"start": v(75.32, -32) * mm, "end": v(75.32, -44) * mm});
            skLineSegment(sketch, "E2220", {"start": v(75.32, -44) * mm, "end": v(76.12, -44) * mm});
            skLineSegment(sketch, "E2221", {"start": v(76.12, -44) * mm, "end": v(76.12, -45) * mm});
            skLineSegment(sketch, "E2222", {"start": v(76.12, -45) * mm, "end": v(90.12, -45) * mm});
            skLineSegment(sketch, "E2223", {"start": v(90.12, -45) * mm, "end": v(90.12, -44) * mm});
            skLineSegment(sketch, "E2224", {"start": v(113.88, -44) * mm, "end": v(114.68, -44) * mm});
            skLineSegment(sketch, "E2225", {"start": v(114.68, -44) * mm, "end": v(114.68, -32) * mm});
            skLineSegment(sketch, "E2226", {"start": v(114.68, -32) * mm, "end": v(113.88, -32) * mm});
            skLineSegment(sketch, "E2227", {"start": v(113.88, -32) * mm, "end": v(113.88, -31) * mm});
            skLineSegment(sketch, "E2228", {"start": v(113.88, -31) * mm, "end": v(99.88, -31) * mm});
            skLineSegment(sketch, "E2229", {"start": v(99.88, -31) * mm, "end": v(99.88, -32) * mm});
            skLineSegment(sketch, "E2230", {"start": v(99.88, -32) * mm, "end": v(99.08, -32) * mm});
            skLineSegment(sketch, "E2231", {"start": v(99.08, -32) * mm, "end": v(99.08, -44) * mm});
            skLineSegment(sketch, "E2232", {"start": v(99.08, -44) * mm, "end": v(99.88, -44) * mm});
            skLineSegment(sketch, "E2233", {"start": v(99.88, -44) * mm, "end": v(99.88, -45) * mm});
            skLineSegment(sketch, "E2234", {"start": v(99.88, -45) * mm, "end": v(113.88, -45) * mm});
            skLineSegment(sketch, "E2235", {"start": v(113.88, -45) * mm, "end": v(113.88, -44) * mm});
            skLineSegment(sketch, "E2236", {"start": v(137.62, -44) * mm, "end": v(138.43, -44) * mm});
            skLineSegment(sketch, "E2237", {"start": v(138.43, -44) * mm, "end": v(138.43, -32) * mm});
            skLineSegment(sketch, "E2238", {"start": v(138.43, -32) * mm, "end": v(137.62, -32) * mm});
            skLineSegment(sketch, "E2239", {"start": v(137.62, -32) * mm, "end": v(137.62, -31) * mm});
            skLineSegment(sketch, "E2240", {"start": v(137.62, -31) * mm, "end": v(123.62, -31) * mm});
            skLineSegment(sketch, "E2241", {"start": v(123.62, -31) * mm, "end": v(123.62, -32) * mm});
            skLineSegment(sketch, "E2242", {"start": v(123.62, -32) * mm, "end": v(122.82, -32) * mm});
            skLineSegment(sketch, "E2243", {"start": v(122.82, -32) * mm, "end": v(122.82, -44) * mm});
            skLineSegment(sketch, "E2244", {"start": v(122.82, -44) * mm, "end": v(123.62, -44) * mm});
            skLineSegment(sketch, "E2245", {"start": v(123.62, -44) * mm, "end": v(123.62, -45) * mm});
            skLineSegment(sketch, "E2246", {"start": v(123.62, -45) * mm, "end": v(137.62, -45) * mm});
            skLineSegment(sketch, "E2247", {"start": v(137.62, -45) * mm, "end": v(137.62, -44) * mm});
            skSolve(sketch);
        }
        {
            var Q0;
            Q0 = qSketchRegion(id + "F0", true);
            extrude(context, id + "F2", {"entities" : qUnion([Q0]), "depth" : 1.5 * mm});
        }
        {
            var Q0;
            Q0=makeQuery(id+"F2.opExtrude","CAP_FACE",FACE,{"disambiguationData":[OSD([sQuery(id+"F0.wireOp",EDGE,"E0"),sQuery(id+"F0.wireOp",EDGE,"E1"),sQuery(id+"F0.wireOp",EDGE,"E2"),sQuery(id+"F0.wireOp",EDGE,"E3"),sQuery(id+"F0.wireOp",EDGE,"E4"),sQuery(id+"F0.wireOp",EDGE,"E5"),sQuery(id+"F0.wireOp",EDGE,"E6"),sQuery(id+"F0.wireOp",EDGE,"E7"),sQuery(id+"F0.wireOp",EDGE,"E8"),sQuery(id+"F0.wireOp",EDGE,"E9"),sQuery(id+"F0.wireOp",EDGE,"E10"),sQuery(id+"F0.wireOp",EDGE,"E11"),sQuery(id+"F0.wireOp",EDGE,"E12"),sQuery(id+"F0.wireOp",EDGE,"E13"),sQuery(id+"F0.wireOp",EDGE,"E14"),sQuery(id+"F0.wireOp",EDGE,"E15"),sQuery(id+"F0.wireOp",EDGE,"E16"),sQuery(id+"F0.wireOp",EDGE,"E17"),sQuery(id+"F0.wireOp",EDGE,"E18"),sQuery(id+"F0.wireOp",EDGE,"E19"),sQuery(id+"F0.wireOp",EDGE,"E20"),sQuery(id+"F0.wireOp",EDGE,"E21"),sQuery(id+"F0.wireOp",EDGE,"E22"),sQuery(id+"F0.wireOp",EDGE,"E23"),sQuery(id+"F0.wireOp",EDGE,"E24"),sQuery(id+"F0.wireOp",EDGE,"E25"),sQuery(id+"F0.wireOp",EDGE,"E26"),sQuery(id+"F0.wireOp",EDGE,"E27"),sQuery(id+"F0.wireOp",EDGE,"E28"),sQuery(id+"F0.wireOp",EDGE,"E29"),sQuery(id+"F0.wireOp",EDGE,"E30"),sQuery(id+"F0.wireOp",EDGE,"E31"),sQuery(id+"F0.wireOp",EDGE,"E32"),sQuery(id+"F0.wireOp",EDGE,"E33"),sQuery(id+"F0.wireOp",EDGE,"E34"),sQuery(id+"F0.wireOp",EDGE,"E35"),sQuery(id+"F0.wireOp",EDGE,"E36"),sQuery(id+"F0.wireOp",EDGE,"E37"),sQuery(id+"F0.wireOp",EDGE,"E38"),sQuery(id+"F0.wireOp",EDGE,"E39"),sQuery(id+"F0.wireOp",EDGE,"E40"),sQuery(id+"F0.wireOp",EDGE,"E41"),sQuery(id+"F0.wireOp",EDGE,"E42"),sQuery(id+"F0.wireOp",EDGE,"E43"),sQuery(id+"F0.wireOp",EDGE,"E44"),sQuery(id+"F0.wireOp",EDGE,"E45"),sQuery(id+"F0.wireOp",EDGE,"E46"),sQuery(id+"F0.wireOp",EDGE,"E47"),sQuery(id+"F0.wireOp",EDGE,"E48"),sQuery(id+"F0.wireOp",EDGE,"E49"),sQuery(id+"F0.wireOp",EDGE,"E50"),sQuery(id+"F0.wireOp",EDGE,"E51"),sQuery(id+"F0.wireOp",EDGE,"E52"),sQuery(id+"F0.wireOp",EDGE,"E53"),sQuery(id+"F0.wireOp",EDGE,"E54"),sQuery(id+"F0.wireOp",EDGE,"E55"),sQuery(id+"F0.wireOp",EDGE,"E56"),sQuery(id+"F0.wireOp",EDGE,"E57"),sQuery(id+"F0.wireOp",EDGE,"E58"),sQuery(id+"F0.wireOp",EDGE,"E59"),sQuery(id+"F0.wireOp",EDGE,"E60"),sQuery(id+"F0.wireOp",EDGE,"E61"),sQuery(id+"F0.wireOp",EDGE,"E62"),sQuery(id+"F0.wireOp",EDGE,"E63"),sQuery(id+"F0.wireOp",EDGE,"E64"),sQuery(id+"F0.wireOp",EDGE,"E65"),sQuery(id+"F0.wireOp",EDGE,"E66"),sQuery(id+"F0.wireOp",EDGE,"E67"),sQuery(id+"F0.wireOp",EDGE,"E68"),sQuery(id+"F0.wireOp",EDGE,"E69"),sQuery(id+"F0.wireOp",EDGE,"E70"),sQuery(id+"F0.wireOp",EDGE,"E71"),sQuery(id+"F0.wireOp",EDGE,"E72"),sQuery(id+"F0.wireOp",EDGE,"E73"),sQuery(id+"F0.wireOp",EDGE,"E74"),sQuery(id+"F0.wireOp",EDGE,"E75"),sQuery(id+"F0.wireOp",EDGE,"E76"),sQuery(id+"F0.wireOp",EDGE,"E77"),sQuery(id+"F0.wireOp",EDGE,"E78"),sQuery(id+"F0.wireOp",EDGE,"E79"),sQuery(id+"F0.wireOp",EDGE,"E80"),sQuery(id+"F0.wireOp",EDGE,"E81"),sQuery(id+"F0.wireOp",EDGE,"E82"),sQuery(id+"F0.wireOp",EDGE,"E83"),sQuery(id+"F0.wireOp",EDGE,"E84"),sQuery(id+"F0.wireOp",EDGE,"E85"),sQuery(id+"F0.wireOp",EDGE,"E86"),sQuery(id+"F0.wireOp",EDGE,"E87"),sQuery(id+"F0.wireOp",EDGE,"E88"),sQuery(id+"F0.wireOp",EDGE,"E89"),sQuery(id+"F0.wireOp",EDGE,"E90"),sQuery(id+"F0.wireOp",EDGE,"E91"),sQuery(id+"F0.wireOp",EDGE,"E92"),sQuery(id+"F0.wireOp",EDGE,"E93"),sQuery(id+"F0.wireOp",EDGE,"E94"),sQuery(id+"F0.wireOp",EDGE,"E95"),sQuery(id+"F0.wireOp",EDGE,"E96"),sQuery(id+"F0.wireOp",EDGE,"E97"),sQuery(id+"F0.wireOp",EDGE,"E98"),sQuery(id+"F0.wireOp",EDGE,"E99"),sQuery(id+"F0.wireOp",EDGE,"E100"),sQuery(id+"F0.wireOp",EDGE,"E101"),sQuery(id+"F0.wireOp",EDGE,"E102"),sQuery(id+"F0.wireOp",EDGE,"E103"),sQuery(id+"F0.wireOp",EDGE,"E104"),sQuery(id+"F0.wireOp",EDGE,"E105"),sQuery(id+"F0.wireOp",EDGE,"E106"),sQuery(id+"F0.wireOp",EDGE,"E107"),sQuery(id+"F0.wireOp",EDGE,"E108"),sQuery(id+"F0.wireOp",EDGE,"E109"),sQuery(id+"F0.wireOp",EDGE,"E110"),sQuery(id+"F0.wireOp",EDGE,"E111"),sQuery(id+"F0.wireOp",EDGE,"E112"),sQuery(id+"F0.wireOp",EDGE,"E113"),sQuery(id+"F0.wireOp",EDGE,"E114"),sQuery(id+"F0.wireOp",EDGE,"E115"),sQuery(id+"F0.wireOp",EDGE,"E116"),sQuery(id+"F0.wireOp",EDGE,"E117"),sQuery(id+"F0.wireOp",EDGE,"E118"),sQuery(id+"F0.wireOp",EDGE,"E119"),sQuery(id+"F0.wireOp",EDGE,"E120"),sQuery(id+"F0.wireOp",EDGE,"E121"),sQuery(id+"F0.wireOp",EDGE,"E122"),sQuery(id+"F0.wireOp",EDGE,"E123"),sQuery(id+"F0.wireOp",EDGE,"E124"),sQuery(id+"F0.wireOp",EDGE,"E125"),sQuery(id+"F0.wireOp",EDGE,"E126"),sQuery(id+"F0.wireOp",EDGE,"E127"),sQuery(id+"F0.wireOp",EDGE,"E128"),sQuery(id+"F0.wireOp",EDGE,"E129"),sQuery(id+"F0.wireOp",EDGE,"E130"),sQuery(id+"F0.wireOp",EDGE,"E131"),sQuery(id+"F0.wireOp",EDGE,"E132"),sQuery(id+"F0.wireOp",EDGE,"E133"),sQuery(id+"F0.wireOp",EDGE,"E134"),sQuery(id+"F0.wireOp",EDGE,"E135"),sQuery(id+"F0.wireOp",EDGE,"E136"),sQuery(id+"F0.wireOp",EDGE,"E137"),sQuery(id+"F0.wireOp",EDGE,"E138"),sQuery(id+"F0.wireOp",EDGE,"E139"),sQuery(id+"F0.wireOp",EDGE,"E140"),sQuery(id+"F0.wireOp",EDGE,"E141"),sQuery(id+"F0.wireOp",EDGE,"E142"),sQuery(id+"F0.wireOp",EDGE,"E143"),sQuery(id+"F0.wireOp",EDGE,"E144"),sQuery(id+"F0.wireOp",EDGE,"E145"),sQuery(id+"F0.wireOp",EDGE,"E146"),sQuery(id+"F0.wireOp",EDGE,"E147"),sQuery(id+"F0.wireOp",EDGE,"E148"),sQuery(id+"F0.wireOp",EDGE,"E149"),sQuery(id+"F0.wireOp",EDGE,"E150"),sQuery(id+"F0.wireOp",EDGE,"E151"),sQuery(id+"F0.wireOp",EDGE,"E152"),sQuery(id+"F0.wireOp",EDGE,"E153"),sQuery(id+"F0.wireOp",EDGE,"E154"),sQuery(id+"F0.wireOp",EDGE,"E155"),sQuery(id+"F0.wireOp",EDGE,"E156"),sQuery(id+"F0.wireOp",EDGE,"E157"),sQuery(id+"F0.wireOp",EDGE,"E158"),sQuery(id+"F0.wireOp",EDGE,"E159"),sQuery(id+"F0.wireOp",EDGE,"E160"),sQuery(id+"F0.wireOp",EDGE,"E161"),sQuery(id+"F0.wireOp",EDGE,"E162"),sQuery(id+"F0.wireOp",EDGE,"E163"),sQuery(id+"F0.wireOp",EDGE,"E164"),sQuery(id+"F0.wireOp",EDGE,"E165"),sQuery(id+"F0.wireOp",EDGE,"E166"),sQuery(id+"F0.wireOp",EDGE,"E167"),sQuery(id+"F0.wireOp",EDGE,"E168"),sQuery(id+"F0.wireOp",EDGE,"E169"),sQuery(id+"F0.wireOp",EDGE,"E170"),sQuery(id+"F0.wireOp",EDGE,"E171"),sQuery(id+"F0.wireOp",EDGE,"E172"),sQuery(id+"F0.wireOp",EDGE,"E173"),sQuery(id+"F0.wireOp",EDGE,"E174"),sQuery(id+"F0.wireOp",EDGE,"E175"),sQuery(id+"F0.wireOp",EDGE,"E176"),sQuery(id+"F0.wireOp",EDGE,"E177"),sQuery(id+"F0.wireOp",EDGE,"E178"),sQuery(id+"F0.wireOp",EDGE,"E179"),sQuery(id+"F0.wireOp",EDGE,"E180"),sQuery(id+"F0.wireOp",EDGE,"E181"),sQuery(id+"F0.wireOp",EDGE,"E182"),sQuery(id+"F0.wireOp",EDGE,"E183"),sQuery(id+"F0.wireOp",EDGE,"E184"),sQuery(id+"F0.wireOp",EDGE,"E185"),sQuery(id+"F0.wireOp",EDGE,"E186"),sQuery(id+"F0.wireOp",EDGE,"E187"),sQuery(id+"F0.wireOp",EDGE,"E188"),sQuery(id+"F0.wireOp",EDGE,"E189"),sQuery(id+"F0.wireOp",EDGE,"E190"),sQuery(id+"F0.wireOp",EDGE,"E191"),sQuery(id+"F0.wireOp",EDGE,"E192"),sQuery(id+"F0.wireOp",EDGE,"E193"),sQuery(id+"F0.wireOp",EDGE,"E194"),sQuery(id+"F0.wireOp",EDGE,"E195"),sQuery(id+"F0.wireOp",EDGE,"E196"),sQuery(id+"F0.wireOp",EDGE,"E197"),sQuery(id+"F0.wireOp",EDGE,"E198"),sQuery(id+"F0.wireOp",EDGE,"E199"),sQuery(id+"F0.wireOp",EDGE,"E200"),sQuery(id+"F0.wireOp",EDGE,"E201"),sQuery(id+"F0.wireOp",EDGE,"E202"),sQuery(id+"F0.wireOp",EDGE,"E203"),sQuery(id+"F0.wireOp",EDGE,"E204"),sQuery(id+"F0.wireOp",EDGE,"E205"),sQuery(id+"F0.wireOp",EDGE,"E206"),sQuery(id+"F0.wireOp",EDGE,"E207"),sQuery(id+"F0.wireOp",EDGE,"E208"),sQuery(id+"F0.wireOp",EDGE,"E209"),sQuery(id+"F0.wireOp",EDGE,"E210"),sQuery(id+"F0.wireOp",EDGE,"E211"),sQuery(id+"F0.wireOp",EDGE,"E212"),sQuery(id+"F0.wireOp",EDGE,"E213"),sQuery(id+"F0.wireOp",EDGE,"E214"),sQuery(id+"F0.wireOp",EDGE,"E215"),sQuery(id+"F0.wireOp",EDGE,"E216"),sQuery(id+"F0.wireOp",EDGE,"E217"),sQuery(id+"F0.wireOp",EDGE,"E218"),sQuery(id+"F0.wireOp",EDGE,"E219"),sQuery(id+"F0.wireOp",EDGE,"E220"),sQuery(id+"F0.wireOp",EDGE,"E221"),sQuery(id+"F0.wireOp",EDGE,"E222"),sQuery(id+"F0.wireOp",EDGE,"E223"),sQuery(id+"F0.wireOp",EDGE,"E224"),sQuery(id+"F0.wireOp",EDGE,"E225"),sQuery(id+"F0.wireOp",EDGE,"E226"),sQuery(id+"F0.wireOp",EDGE,"E227"),sQuery(id+"F0.wireOp",EDGE,"E228"),sQuery(id+"F0.wireOp",EDGE,"E229"),sQuery(id+"F0.wireOp",EDGE,"E230"),sQuery(id+"F0.wireOp",EDGE,"E231"),sQuery(id+"F0.wireOp",EDGE,"E232"),sQuery(id+"F0.wireOp",EDGE,"E233"),sQuery(id+"F0.wireOp",EDGE,"E234"),sQuery(id+"F0.wireOp",EDGE,"E235"),sQuery(id+"F0.wireOp",EDGE,"E236"),sQuery(id+"F0.wireOp",EDGE,"E237"),sQuery(id+"F0.wireOp",EDGE,"E238"),sQuery(id+"F0.wireOp",EDGE,"E239"),sQuery(id+"F0.wireOp",EDGE,"E240"),sQuery(id+"F0.wireOp",EDGE,"E241"),sQuery(id+"F0.wireOp",EDGE,"E242"),sQuery(id+"F0.wireOp",EDGE,"E243"),sQuery(id+"F0.wireOp",EDGE,"E244"),sQuery(id+"F0.wireOp",EDGE,"E245"),sQuery(id+"F0.wireOp",EDGE,"E246"),sQuery(id+"F0.wireOp",EDGE,"E247"),sQuery(id+"F0.wireOp",EDGE,"E248"),sQuery(id+"F0.wireOp",EDGE,"E249"),sQuery(id+"F0.wireOp",EDGE,"E250"),sQuery(id+"F0.wireOp",EDGE,"E251"),sQuery(id+"F0.wireOp",EDGE,"E252"),sQuery(id+"F0.wireOp",EDGE,"E253"),sQuery(id+"F0.wireOp",EDGE,"E254"),sQuery(id+"F0.wireOp",EDGE,"E255"),sQuery(id+"F0.wireOp",EDGE,"E256"),sQuery(id+"F0.wireOp",EDGE,"E257"),sQuery(id+"F0.wireOp",EDGE,"E258"),sQuery(id+"F0.wireOp",EDGE,"E259"),sQuery(id+"F0.wireOp",EDGE,"E260"),sQuery(id+"F0.wireOp",EDGE,"E261"),sQuery(id+"F0.wireOp",EDGE,"E262"),sQuery(id+"F0.wireOp",EDGE,"E263"),sQuery(id+"F0.wireOp",EDGE,"E264"),sQuery(id+"F0.wireOp",EDGE,"E265"),sQuery(id+"F0.wireOp",EDGE,"E266"),sQuery(id+"F0.wireOp",EDGE,"E267"),sQuery(id+"F0.wireOp",EDGE,"E268"),sQuery(id+"F0.wireOp",EDGE,"E269"),sQuery(id+"F0.wireOp",EDGE,"E270"),sQuery(id+"F0.wireOp",EDGE,"E271"),sQuery(id+"F0.wireOp",EDGE,"E272"),sQuery(id+"F0.wireOp",EDGE,"E273"),sQuery(id+"F0.wireOp",EDGE,"E274"),sQuery(id+"F0.wireOp",EDGE,"E275"),sQuery(id+"F0.wireOp",EDGE,"E276"),sQuery(id+"F0.wireOp",EDGE,"E277"),sQuery(id+"F0.wireOp",EDGE,"E278"),sQuery(id+"F0.wireOp",EDGE,"E279"),sQuery(id+"F0.wireOp",EDGE,"E280"),sQuery(id+"F0.wireOp",EDGE,"E281"),sQuery(id+"F0.wireOp",EDGE,"E282"),sQuery(id+"F0.wireOp",EDGE,"E283"),sQuery(id+"F0.wireOp",EDGE,"E284"),sQuery(id+"F0.wireOp",EDGE,"E285"),sQuery(id+"F0.wireOp",EDGE,"E286"),sQuery(id+"F0.wireOp",EDGE,"E287"),sQuery(id+"F0.wireOp",EDGE,"E288"),sQuery(id+"F0.wireOp",EDGE,"E289"),sQuery(id+"F0.wireOp",EDGE,"E290"),sQuery(id+"F0.wireOp",EDGE,"E291"),sQuery(id+"F0.wireOp",EDGE,"E292"),sQuery(id+"F0.wireOp",EDGE,"E293"),sQuery(id+"F0.wireOp",EDGE,"E294"),sQuery(id+"F0.wireOp",EDGE,"E295"),sQuery(id+"F0.wireOp",EDGE,"E296"),sQuery(id+"F0.wireOp",EDGE,"E297"),sQuery(id+"F0.wireOp",EDGE,"E298"),sQuery(id+"F0.wireOp",EDGE,"E299"),sQuery(id+"F0.wireOp",EDGE,"E300"),sQuery(id+"F0.wireOp",EDGE,"E301"),sQuery(id+"F0.wireOp",EDGE,"E302"),sQuery(id+"F0.wireOp",EDGE,"E303"),sQuery(id+"F0.wireOp",EDGE,"E304"),sQuery(id+"F0.wireOp",EDGE,"E305"),sQuery(id+"F0.wireOp",EDGE,"E306"),sQuery(id+"F0.wireOp",EDGE,"E307"),sQuery(id+"F0.wireOp",EDGE,"E308"),sQuery(id+"F0.wireOp",EDGE,"E309"),sQuery(id+"F0.wireOp",EDGE,"E310"),sQuery(id+"F0.wireOp",EDGE,"E311"),sQuery(id+"F0.wireOp",EDGE,"E312"),sQuery(id+"F0.wireOp",EDGE,"E313"),sQuery(id+"F0.wireOp",EDGE,"E314"),sQuery(id+"F0.wireOp",EDGE,"E315"),sQuery(id+"F0.wireOp",EDGE,"E316"),sQuery(id+"F0.wireOp",EDGE,"E317"),sQuery(id+"F0.wireOp",EDGE,"E318"),sQuery(id+"F0.wireOp",EDGE,"E319"),sQuery(id+"F0.wireOp",EDGE,"E320"),sQuery(id+"F0.wireOp",EDGE,"E321"),sQuery(id+"F0.wireOp",EDGE,"E322"),sQuery(id+"F0.wireOp",EDGE,"E323"),sQuery(id+"F0.wireOp",EDGE,"E324"),sQuery(id+"F0.wireOp",EDGE,"E325"),sQuery(id+"F0.wireOp",EDGE,"E326"),sQuery(id+"F0.wireOp",EDGE,"E327"),sQuery(id+"F0.wireOp",EDGE,"E328"),sQuery(id+"F0.wireOp",EDGE,"E329"),sQuery(id+"F0.wireOp",EDGE,"E330"),sQuery(id+"F0.wireOp",EDGE,"E331"),sQuery(id+"F0.wireOp",EDGE,"E332"),sQuery(id+"F0.wireOp",EDGE,"E333"),sQuery(id+"F0.wireOp",EDGE,"E334"),sQuery(id+"F0.wireOp",EDGE,"E335"),sQuery(id+"F0.wireOp",EDGE,"E336"),sQuery(id+"F0.wireOp",EDGE,"E337"),sQuery(id+"F0.wireOp",EDGE,"E338"),sQuery(id+"F0.wireOp",EDGE,"E339"),sQuery(id+"F0.wireOp",EDGE,"E340"),sQuery(id+"F0.wireOp",EDGE,"E341"),sQuery(id+"F0.wireOp",EDGE,"E342"),sQuery(id+"F0.wireOp",EDGE,"E343"),sQuery(id+"F0.wireOp",EDGE,"E344"),sQuery(id+"F0.wireOp",EDGE,"E345"),sQuery(id+"F0.wireOp",EDGE,"E346"),sQuery(id+"F0.wireOp",EDGE,"E347"),sQuery(id+"F0.wireOp",EDGE,"E348"),sQuery(id+"F0.wireOp",EDGE,"E349"),sQuery(id+"F0.wireOp",EDGE,"E350"),sQuery(id+"F0.wireOp",EDGE,"E351"),sQuery(id+"F0.wireOp",EDGE,"E352"),sQuery(id+"F0.wireOp",EDGE,"E353"),sQuery(id+"F0.wireOp",EDGE,"E354"),sQuery(id+"F0.wireOp",EDGE,"E355"),sQuery(id+"F0.wireOp",EDGE,"E356"),sQuery(id+"F0.wireOp",EDGE,"E357"),sQuery(id+"F0.wireOp",EDGE,"E358"),sQuery(id+"F0.wireOp",EDGE,"E359"),sQuery(id+"F0.wireOp",EDGE,"E360"),sQuery(id+"F0.wireOp",EDGE,"E361"),sQuery(id+"F0.wireOp",EDGE,"E362"),sQuery(id+"F0.wireOp",EDGE,"E363"),sQuery(id+"F0.wireOp",EDGE,"E364"),sQuery(id+"F0.wireOp",EDGE,"E365"),sQuery(id+"F0.wireOp",EDGE,"E366"),sQuery(id+"F0.wireOp",EDGE,"E367"),sQuery(id+"F0.wireOp",EDGE,"E368"),sQuery(id+"F0.wireOp",EDGE,"E369"),sQuery(id+"F0.wireOp",EDGE,"E370"),sQuery(id+"F0.wireOp",EDGE,"E371"),sQuery(id+"F0.wireOp",EDGE,"E372"),sQuery(id+"F0.wireOp",EDGE,"E373"),sQuery(id+"F0.wireOp",EDGE,"E374"),sQuery(id+"F0.wireOp",EDGE,"E375"),sQuery(id+"F0.wireOp",EDGE,"E376"),sQuery(id+"F0.wireOp",EDGE,"E377"),sQuery(id+"F0.wireOp",EDGE,"E378"),sQuery(id+"F0.wireOp",EDGE,"E379"),sQuery(id+"F0.wireOp",EDGE,"E380"),sQuery(id+"F0.wireOp",EDGE,"E381"),sQuery(id+"F0.wireOp",EDGE,"E382"),sQuery(id+"F0.wireOp",EDGE,"E383"),sQuery(id+"F0.wireOp",EDGE,"E384"),sQuery(id+"F0.wireOp",EDGE,"E385"),sQuery(id+"F0.wireOp",EDGE,"E386"),sQuery(id+"F0.wireOp",EDGE,"E387"),sQuery(id+"F0.wireOp",EDGE,"E388"),sQuery(id+"F0.wireOp",EDGE,"E389"),sQuery(id+"F0.wireOp",EDGE,"E390"),sQuery(id+"F0.wireOp",EDGE,"E391"),sQuery(id+"F0.wireOp",EDGE,"E392"),sQuery(id+"F0.wireOp",EDGE,"E393"),sQuery(id+"F0.wireOp",EDGE,"E394"),sQuery(id+"F0.wireOp",EDGE,"E395"),sQuery(id+"F0.wireOp",EDGE,"E396"),sQuery(id+"F0.wireOp",EDGE,"E397"),sQuery(id+"F0.wireOp",EDGE,"E398"),sQuery(id+"F0.wireOp",EDGE,"E399"),sQuery(id+"F0.wireOp",EDGE,"E400"),sQuery(id+"F0.wireOp",EDGE,"E401"),sQuery(id+"F0.wireOp",EDGE,"E402"),sQuery(id+"F0.wireOp",EDGE,"E403"),sQuery(id+"F0.wireOp",EDGE,"E404"),sQuery(id+"F0.wireOp",EDGE,"E405"),sQuery(id+"F0.wireOp",EDGE,"E406"),sQuery(id+"F0.wireOp",EDGE,"E407"),sQuery(id+"F0.wireOp",EDGE,"E408"),sQuery(id+"F0.wireOp",EDGE,"E409"),sQuery(id+"F0.wireOp",EDGE,"E410"),sQuery(id+"F0.wireOp",EDGE,"E411"),sQuery(id+"F0.wireOp",EDGE,"E412"),sQuery(id+"F0.wireOp",EDGE,"E413"),sQuery(id+"F0.wireOp",EDGE,"E414"),sQuery(id+"F0.wireOp",EDGE,"E415"),sQuery(id+"F0.wireOp",EDGE,"E416"),sQuery(id+"F0.wireOp",EDGE,"E417"),sQuery(id+"F0.wireOp",EDGE,"E418"),sQuery(id+"F0.wireOp",EDGE,"E419"),sQuery(id+"F0.wireOp",EDGE,"E420"),sQuery(id+"F0.wireOp",EDGE,"E421"),sQuery(id+"F0.wireOp",EDGE,"E422"),sQuery(id+"F0.wireOp",EDGE,"E423"),sQuery(id+"F0.wireOp",EDGE,"E424"),sQuery(id+"F0.wireOp",EDGE,"E425"),sQuery(id+"F0.wireOp",EDGE,"E426"),sQuery(id+"F0.wireOp",EDGE,"E427"),sQuery(id+"F0.wireOp",EDGE,"E428"),sQuery(id+"F0.wireOp",EDGE,"E429"),sQuery(id+"F0.wireOp",EDGE,"E430"),sQuery(id+"F0.wireOp",EDGE,"E431"),sQuery(id+"F0.wireOp",EDGE,"E432"),sQuery(id+"F0.wireOp",EDGE,"E433"),sQuery(id+"F0.wireOp",EDGE,"E434"),sQuery(id+"F0.wireOp",EDGE,"E435"),sQuery(id+"F0.wireOp",EDGE,"E436"),sQuery(id+"F0.wireOp",EDGE,"E437"),sQuery(id+"F0.wireOp",EDGE,"E438"),sQuery(id+"F0.wireOp",EDGE,"E439"),sQuery(id+"F0.wireOp",EDGE,"E440"),sQuery(id+"F0.wireOp",EDGE,"E441"),sQuery(id+"F0.wireOp",EDGE,"E442"),sQuery(id+"F0.wireOp",EDGE,"E443"),sQuery(id+"F0.wireOp",EDGE,"E444"),sQuery(id+"F0.wireOp",EDGE,"E445"),sQuery(id+"F0.wireOp",EDGE,"E446"),sQuery(id+"F0.wireOp",EDGE,"E447"),sQuery(id+"F0.wireOp",EDGE,"E448"),sQuery(id+"F0.wireOp",EDGE,"E449"),sQuery(id+"F0.wireOp",EDGE,"E450"),sQuery(id+"F0.wireOp",EDGE,"E451"),sQuery(id+"F0.wireOp",EDGE,"E452"),sQuery(id+"F0.wireOp",EDGE,"E453"),sQuery(id+"F0.wireOp",EDGE,"E454"),sQuery(id+"F0.wireOp",EDGE,"E455"),sQuery(id+"F0.wireOp",EDGE,"E456"),sQuery(id+"F0.wireOp",EDGE,"E457"),sQuery(id+"F0.wireOp",EDGE,"E458"),sQuery(id+"F0.wireOp",EDGE,"E459"),sQuery(id+"F0.wireOp",EDGE,"E460"),sQuery(id+"F0.wireOp",EDGE,"E461"),sQuery(id+"F0.wireOp",EDGE,"E462"),sQuery(id+"F0.wireOp",EDGE,"E463"),sQuery(id+"F0.wireOp",EDGE,"E464"),sQuery(id+"F0.wireOp",EDGE,"E465"),sQuery(id+"F0.wireOp",EDGE,"E466"),sQuery(id+"F0.wireOp",EDGE,"E467"),sQuery(id+"F0.wireOp",EDGE,"E468"),sQuery(id+"F0.wireOp",EDGE,"E469"),sQuery(id+"F0.wireOp",EDGE,"E470"),sQuery(id+"F0.wireOp",EDGE,"E471"),sQuery(id+"F0.wireOp",EDGE,"E472"),sQuery(id+"F0.wireOp",EDGE,"E473"),sQuery(id+"F0.wireOp",EDGE,"E474"),sQuery(id+"F0.wireOp",EDGE,"E475"),sQuery(id+"F0.wireOp",EDGE,"E476"),sQuery(id+"F0.wireOp",EDGE,"E477"),sQuery(id+"F0.wireOp",EDGE,"E478"),sQuery(id+"F0.wireOp",EDGE,"E479"),sQuery(id+"F0.wireOp",EDGE,"E480"),sQuery(id+"F0.wireOp",EDGE,"E481"),sQuery(id+"F0.wireOp",EDGE,"E482"),sQuery(id+"F0.wireOp",EDGE,"E483"),sQuery(id+"F0.wireOp",EDGE,"E484"),sQuery(id+"F0.wireOp",EDGE,"E485"),sQuery(id+"F0.wireOp",EDGE,"E486"),sQuery(id+"F0.wireOp",EDGE,"E487"),sQuery(id+"F0.wireOp",EDGE,"E488"),sQuery(id+"F0.wireOp",EDGE,"E489"),sQuery(id+"F0.wireOp",EDGE,"E490"),sQuery(id+"F0.wireOp",EDGE,"E491"),sQuery(id+"F0.wireOp",EDGE,"E492"),sQuery(id+"F0.wireOp",EDGE,"E493"),sQuery(id+"F0.wireOp",EDGE,"E494"),sQuery(id+"F0.wireOp",EDGE,"E495"),sQuery(id+"F0.wireOp",EDGE,"E496"),sQuery(id+"F0.wireOp",EDGE,"E497"),sQuery(id+"F0.wireOp",EDGE,"E498"),sQuery(id+"F0.wireOp",EDGE,"E499"),sQuery(id+"F0.wireOp",EDGE,"E500"),sQuery(id+"F0.wireOp",EDGE,"E501"),sQuery(id+"F0.wireOp",EDGE,"E502"),sQuery(id+"F0.wireOp",EDGE,"E503"),sQuery(id+"F0.wireOp",EDGE,"E504"),sQuery(id+"F0.wireOp",EDGE,"E505"),sQuery(id+"F0.wireOp",EDGE,"E506"),sQuery(id+"F0.wireOp",EDGE,"E507"),sQuery(id+"F0.wireOp",EDGE,"E508"),sQuery(id+"F0.wireOp",EDGE,"E509"),sQuery(id+"F0.wireOp",EDGE,"E510"),sQuery(id+"F0.wireOp",EDGE,"E511"),sQuery(id+"F0.wireOp",EDGE,"E512"),sQuery(id+"F0.wireOp",EDGE,"E513"),sQuery(id+"F0.wireOp",EDGE,"E514"),sQuery(id+"F0.wireOp",EDGE,"E515"),sQuery(id+"F0.wireOp",EDGE,"E516"),sQuery(id+"F0.wireOp",EDGE,"E517"),sQuery(id+"F0.wireOp",EDGE,"E518"),sQuery(id+"F0.wireOp",EDGE,"E519"),sQuery(id+"F0.wireOp",EDGE,"E520"),sQuery(id+"F0.wireOp",EDGE,"E521"),sQuery(id+"F0.wireOp",EDGE,"E522"),sQuery(id+"F0.wireOp",EDGE,"E523"),sQuery(id+"F0.wireOp",EDGE,"E524"),sQuery(id+"F0.wireOp",EDGE,"E525"),sQuery(id+"F0.wireOp",EDGE,"E526"),sQuery(id+"F0.wireOp",EDGE,"E527"),sQuery(id+"F0.wireOp",EDGE,"E528"),sQuery(id+"F0.wireOp",EDGE,"E529"),sQuery(id+"F0.wireOp",EDGE,"E530"),sQuery(id+"F0.wireOp",EDGE,"E531"),sQuery(id+"F0.wireOp",EDGE,"E532"),sQuery(id+"F0.wireOp",EDGE,"E533"),sQuery(id+"F0.wireOp",EDGE,"E534"),sQuery(id+"F0.wireOp",EDGE,"E535"),sQuery(id+"F0.wireOp",EDGE,"E536"),sQuery(id+"F0.wireOp",EDGE,"E537"),sQuery(id+"F0.wireOp",EDGE,"E538"),sQuery(id+"F0.wireOp",EDGE,"E539"),sQuery(id+"F0.wireOp",EDGE,"E540"),sQuery(id+"F0.wireOp",EDGE,"E541"),sQuery(id+"F0.wireOp",EDGE,"E542"),sQuery(id+"F0.wireOp",EDGE,"E543"),sQuery(id+"F0.wireOp",EDGE,"E544"),sQuery(id+"F0.wireOp",EDGE,"E545"),sQuery(id+"F0.wireOp",EDGE,"E546"),sQuery(id+"F0.wireOp",EDGE,"E547"),sQuery(id+"F0.wireOp",EDGE,"E548"),sQuery(id+"F0.wireOp",EDGE,"E549"),sQuery(id+"F0.wireOp",EDGE,"E550"),sQuery(id+"F0.wireOp",EDGE,"E551"),sQuery(id+"F0.wireOp",EDGE,"E552"),sQuery(id+"F0.wireOp",EDGE,"E553"),sQuery(id+"F0.wireOp",EDGE,"E554"),sQuery(id+"F0.wireOp",EDGE,"E555"),sQuery(id+"F0.wireOp",EDGE,"E556"),sQuery(id+"F0.wireOp",EDGE,"E557"),sQuery(id+"F0.wireOp",EDGE,"E558"),sQuery(id+"F0.wireOp",EDGE,"E559"),sQuery(id+"F0.wireOp",EDGE,"E560"),sQuery(id+"F0.wireOp",EDGE,"E561"),sQuery(id+"F0.wireOp",EDGE,"E562"),sQuery(id+"F0.wireOp",EDGE,"E563"),sQuery(id+"F0.wireOp",EDGE,"E564"),sQuery(id+"F0.wireOp",EDGE,"E565"),sQuery(id+"F0.wireOp",EDGE,"E566"),sQuery(id+"F0.wireOp",EDGE,"E567"),sQuery(id+"F0.wireOp",EDGE,"E568"),sQuery(id+"F0.wireOp",EDGE,"E569"),sQuery(id+"F0.wireOp",EDGE,"E570"),sQuery(id+"F0.wireOp",EDGE,"E571"),sQuery(id+"F0.wireOp",EDGE,"E572"),sQuery(id+"F0.wireOp",EDGE,"E573"),sQuery(id+"F0.wireOp",EDGE,"E574"),sQuery(id+"F0.wireOp",EDGE,"E575"),sQuery(id+"F0.wireOp",EDGE,"E576"),sQuery(id+"F0.wireOp",EDGE,"E577"),sQuery(id+"F0.wireOp",EDGE,"E578"),sQuery(id+"F0.wireOp",EDGE,"E579"),sQuery(id+"F0.wireOp",EDGE,"E580"),sQuery(id+"F0.wireOp",EDGE,"E581"),sQuery(id+"F0.wireOp",EDGE,"E582"),sQuery(id+"F0.wireOp",EDGE,"E583"),sQuery(id+"F0.wireOp",EDGE,"E584"),sQuery(id+"F0.wireOp",EDGE,"E585"),sQuery(id+"F0.wireOp",EDGE,"E586"),sQuery(id+"F0.wireOp",EDGE,"E587"),sQuery(id+"F0.wireOp",EDGE,"E588"),sQuery(id+"F0.wireOp",EDGE,"E589"),sQuery(id+"F0.wireOp",EDGE,"E590"),sQuery(id+"F0.wireOp",EDGE,"E591"),sQuery(id+"F0.wireOp",EDGE,"E592"),sQuery(id+"F0.wireOp",EDGE,"E593"),sQuery(id+"F0.wireOp",EDGE,"E594"),sQuery(id+"F0.wireOp",EDGE,"E595"),sQuery(id+"F0.wireOp",EDGE,"E596"),sQuery(id+"F0.wireOp",EDGE,"E597"),sQuery(id+"F0.wireOp",EDGE,"E598"),sQuery(id+"F0.wireOp",EDGE,"E599"),sQuery(id+"F0.wireOp",EDGE,"E600"),sQuery(id+"F0.wireOp",EDGE,"E601"),sQuery(id+"F0.wireOp",EDGE,"E602"),sQuery(id+"F0.wireOp",EDGE,"E603"),sQuery(id+"F0.wireOp",EDGE,"E604"),sQuery(id+"F0.wireOp",EDGE,"E605"),sQuery(id+"F0.wireOp",EDGE,"E606"),sQuery(id+"F0.wireOp",EDGE,"E607"),sQuery(id+"F0.wireOp",EDGE,"E608"),sQuery(id+"F0.wireOp",EDGE,"E609"),sQuery(id+"F0.wireOp",EDGE,"E610"),sQuery(id+"F0.wireOp",EDGE,"E611"),sQuery(id+"F0.wireOp",EDGE,"E612"),sQuery(id+"F0.wireOp",EDGE,"E613"),sQuery(id+"F0.wireOp",EDGE,"E614"),sQuery(id+"F0.wireOp",EDGE,"E615"),sQuery(id+"F0.wireOp",EDGE,"E616"),sQuery(id+"F0.wireOp",EDGE,"E617"),sQuery(id+"F0.wireOp",EDGE,"E618"),sQuery(id+"F0.wireOp",EDGE,"E619"),sQuery(id+"F0.wireOp",EDGE,"E620"),sQuery(id+"F0.wireOp",EDGE,"E621"),sQuery(id+"F0.wireOp",EDGE,"E622"),sQuery(id+"F0.wireOp",EDGE,"E623"),sQuery(id+"F0.wireOp",EDGE,"E624"),sQuery(id+"F0.wireOp",EDGE,"E625"),sQuery(id+"F0.wireOp",EDGE,"E626"),sQuery(id+"F0.wireOp",EDGE,"E627"),sQuery(id+"F0.wireOp",EDGE,"E628"),sQuery(id+"F0.wireOp",EDGE,"E629"),sQuery(id+"F0.wireOp",EDGE,"E630"),sQuery(id+"F0.wireOp",EDGE,"E631"),sQuery(id+"F0.wireOp",EDGE,"E632"),sQuery(id+"F0.wireOp",EDGE,"E633"),sQuery(id+"F0.wireOp",EDGE,"E634"),sQuery(id+"F0.wireOp",EDGE,"E635"),sQuery(id+"F0.wireOp",EDGE,"E636"),sQuery(id+"F0.wireOp",EDGE,"E637"),sQuery(id+"F0.wireOp",EDGE,"E638"),sQuery(id+"F0.wireOp",EDGE,"E639"),sQuery(id+"F0.wireOp",EDGE,"E640"),sQuery(id+"F0.wireOp",EDGE,"E641"),sQuery(id+"F0.wireOp",EDGE,"E642"),sQuery(id+"F0.wireOp",EDGE,"E643"),sQuery(id+"F0.wireOp",EDGE,"E644"),sQuery(id+"F0.wireOp",EDGE,"E645"),sQuery(id+"F0.wireOp",EDGE,"E646"),sQuery(id+"F0.wireOp",EDGE,"E647"),sQuery(id+"F0.wireOp",EDGE,"E648"),sQuery(id+"F0.wireOp",EDGE,"E649"),sQuery(id+"F0.wireOp",EDGE,"E650"),sQuery(id+"F0.wireOp",EDGE,"E651"),sQuery(id+"F0.wireOp",EDGE,"E652"),sQuery(id+"F0.wireOp",EDGE,"E653"),sQuery(id+"F0.wireOp",EDGE,"E654"),sQuery(id+"F0.wireOp",EDGE,"E655"),sQuery(id+"F0.wireOp",EDGE,"E656"),sQuery(id+"F0.wireOp",EDGE,"E657"),sQuery(id+"F0.wireOp",EDGE,"E658"),sQuery(id+"F0.wireOp",EDGE,"E659"),sQuery(id+"F0.wireOp",EDGE,"E660"),sQuery(id+"F0.wireOp",EDGE,"E661"),sQuery(id+"F0.wireOp",EDGE,"E662"),sQuery(id+"F0.wireOp",EDGE,"E663"),sQuery(id+"F0.wireOp",EDGE,"E664"),sQuery(id+"F0.wireOp",EDGE,"E665"),sQuery(id+"F0.wireOp",EDGE,"E666"),sQuery(id+"F0.wireOp",EDGE,"E667"),sQuery(id+"F0.wireOp",EDGE,"E668"),sQuery(id+"F0.wireOp",EDGE,"E669"),sQuery(id+"F0.wireOp",EDGE,"E670"),sQuery(id+"F0.wireOp",EDGE,"E671"),sQuery(id+"F0.wireOp",EDGE,"E672"),sQuery(id+"F0.wireOp",EDGE,"E673"),sQuery(id+"F0.wireOp",EDGE,"E674"),sQuery(id+"F0.wireOp",EDGE,"E675"),sQuery(id+"F0.wireOp",EDGE,"E676"),sQuery(id+"F0.wireOp",EDGE,"E677"),sQuery(id+"F0.wireOp",EDGE,"E678"),sQuery(id+"F0.wireOp",EDGE,"E679"),sQuery(id+"F0.wireOp",EDGE,"E680"),sQuery(id+"F0.wireOp",EDGE,"E681"),sQuery(id+"F0.wireOp",EDGE,"E682"),sQuery(id+"F0.wireOp",EDGE,"E683"),sQuery(id+"F0.wireOp",EDGE,"E684"),sQuery(id+"F0.wireOp",EDGE,"E685"),sQuery(id+"F0.wireOp",EDGE,"E686"),sQuery(id+"F0.wireOp",EDGE,"E687"),sQuery(id+"F0.wireOp",EDGE,"E688"),sQuery(id+"F0.wireOp",EDGE,"E689"),sQuery(id+"F0.wireOp",EDGE,"E690"),sQuery(id+"F0.wireOp",EDGE,"E691"),sQuery(id+"F0.wireOp",EDGE,"E692"),sQuery(id+"F0.wireOp",EDGE,"E693"),sQuery(id+"F0.wireOp",EDGE,"E694"),sQuery(id+"F0.wireOp",EDGE,"E695"),sQuery(id+"F0.wireOp",EDGE,"E696"),sQuery(id+"F0.wireOp",EDGE,"E697"),sQuery(id+"F0.wireOp",EDGE,"E698"),sQuery(id+"F0.wireOp",EDGE,"E699"),sQuery(id+"F0.wireOp",EDGE,"E700"),sQuery(id+"F0.wireOp",EDGE,"E701"),sQuery(id+"F0.wireOp",EDGE,"E702"),sQuery(id+"F0.wireOp",EDGE,"E703"),sQuery(id+"F0.wireOp",EDGE,"E704"),sQuery(id+"F0.wireOp",EDGE,"E705"),sQuery(id+"F0.wireOp",EDGE,"E706"),sQuery(id+"F0.wireOp",EDGE,"E707"),sQuery(id+"F0.wireOp",EDGE,"E708"),sQuery(id+"F0.wireOp",EDGE,"E709"),sQuery(id+"F0.wireOp",EDGE,"E710"),sQuery(id+"F0.wireOp",EDGE,"E711"),sQuery(id+"F0.wireOp",EDGE,"E712"),sQuery(id+"F0.wireOp",EDGE,"E713"),sQuery(id+"F0.wireOp",EDGE,"E714"),sQuery(id+"F0.wireOp",EDGE,"E715"),sQuery(id+"F0.wireOp",EDGE,"E716"),sQuery(id+"F0.wireOp",EDGE,"E717"),sQuery(id+"F0.wireOp",EDGE,"E718"),sQuery(id+"F0.wireOp",EDGE,"E719"),sQuery(id+"F0.wireOp",EDGE,"E720"),sQuery(id+"F0.wireOp",EDGE,"E721"),sQuery(id+"F0.wireOp",EDGE,"E722"),sQuery(id+"F0.wireOp",EDGE,"E723"),sQuery(id+"F0.wireOp",EDGE,"E724"),sQuery(id+"F0.wireOp",EDGE,"E725"),sQuery(id+"F0.wireOp",EDGE,"E726"),sQuery(id+"F0.wireOp",EDGE,"E727"),sQuery(id+"F0.wireOp",EDGE,"E728"),sQuery(id+"F0.wireOp",EDGE,"E729"),sQuery(id+"F0.wireOp",EDGE,"E730"),sQuery(id+"F0.wireOp",EDGE,"E731"),sQuery(id+"F0.wireOp",EDGE,"E732"),sQuery(id+"F0.wireOp",EDGE,"E733"),sQuery(id+"F0.wireOp",EDGE,"E734"),sQuery(id+"F0.wireOp",EDGE,"E735"),sQuery(id+"F0.wireOp",EDGE,"E736"),sQuery(id+"F0.wireOp",EDGE,"E737"),sQuery(id+"F0.wireOp",EDGE,"E738"),sQuery(id+"F0.wireOp",EDGE,"E739"),sQuery(id+"F0.wireOp",EDGE,"E740"),sQuery(id+"F0.wireOp",EDGE,"E741"),sQuery(id+"F0.wireOp",EDGE,"E742"),sQuery(id+"F0.wireOp",EDGE,"E743"),sQuery(id+"F0.wireOp",EDGE,"E744"),sQuery(id+"F0.wireOp",EDGE,"E745"),sQuery(id+"F0.wireOp",EDGE,"E746"),sQuery(id+"F0.wireOp",EDGE,"E747"),sQuery(id+"F0.wireOp",EDGE,"E748"),sQuery(id+"F0.wireOp",EDGE,"E749"),sQuery(id+"F0.wireOp",EDGE,"E750"),sQuery(id+"F0.wireOp",EDGE,"E751"),sQuery(id+"F0.wireOp",EDGE,"E752"),sQuery(id+"F0.wireOp",EDGE,"E753"),sQuery(id+"F0.wireOp",EDGE,"E754"),sQuery(id+"F0.wireOp",EDGE,"E755"),sQuery(id+"F0.wireOp",EDGE,"E756"),sQuery(id+"F0.wireOp",EDGE,"E757"),sQuery(id+"F0.wireOp",EDGE,"E758"),sQuery(id+"F0.wireOp",EDGE,"E759"),sQuery(id+"F0.wireOp",EDGE,"E760"),sQuery(id+"F0.wireOp",EDGE,"E761"),sQuery(id+"F0.wireOp",EDGE,"E762"),sQuery(id+"F0.wireOp",EDGE,"E763"),sQuery(id+"F0.wireOp",EDGE,"E764"),sQuery(id+"F0.wireOp",EDGE,"E765"),sQuery(id+"F0.wireOp",EDGE,"E766"),sQuery(id+"F0.wireOp",EDGE,"E767"),sQuery(id+"F0.wireOp",EDGE,"E768"),sQuery(id+"F0.wireOp",EDGE,"E769"),sQuery(id+"F0.wireOp",EDGE,"E770"),sQuery(id+"F0.wireOp",EDGE,"E771"),sQuery(id+"F0.wireOp",EDGE,"E772"),sQuery(id+"F0.wireOp",EDGE,"E773"),sQuery(id+"F0.wireOp",EDGE,"E774"),sQuery(id+"F0.wireOp",EDGE,"E775"),sQuery(id+"F0.wireOp",EDGE,"E776"),sQuery(id+"F0.wireOp",EDGE,"E777"),sQuery(id+"F0.wireOp",EDGE,"E778"),sQuery(id+"F0.wireOp",EDGE,"E779"),sQuery(id+"F0.wireOp",EDGE,"E780"),sQuery(id+"F0.wireOp",EDGE,"E781"),sQuery(id+"F0.wireOp",EDGE,"E782"),sQuery(id+"F0.wireOp",EDGE,"E783"),sQuery(id+"F0.wireOp",EDGE,"E784"),sQuery(id+"F0.wireOp",EDGE,"E785"),sQuery(id+"F0.wireOp",EDGE,"E786"),sQuery(id+"F0.wireOp",EDGE,"E787"),sQuery(id+"F0.wireOp",EDGE,"E788"),sQuery(id+"F0.wireOp",EDGE,"E789"),sQuery(id+"F0.wireOp",EDGE,"E790"),sQuery(id+"F0.wireOp",EDGE,"E791"),sQuery(id+"F0.wireOp",EDGE,"E792"),sQuery(id+"F0.wireOp",EDGE,"E793"),sQuery(id+"F0.wireOp",EDGE,"E794"),sQuery(id+"F0.wireOp",EDGE,"E795"),sQuery(id+"F0.wireOp",EDGE,"E796"),sQuery(id+"F0.wireOp",EDGE,"E797"),sQuery(id+"F0.wireOp",EDGE,"E798"),sQuery(id+"F0.wireOp",EDGE,"E799"),sQuery(id+"F0.wireOp",EDGE,"E800"),sQuery(id+"F0.wireOp",EDGE,"E801"),sQuery(id+"F0.wireOp",EDGE,"E802"),sQuery(id+"F0.wireOp",EDGE,"E803"),sQuery(id+"F0.wireOp",EDGE,"E804"),sQuery(id+"F0.wireOp",EDGE,"E805"),sQuery(id+"F0.wireOp",EDGE,"E806"),sQuery(id+"F0.wireOp",EDGE,"E807"),sQuery(id+"F0.wireOp",EDGE,"E808"),sQuery(id+"F0.wireOp",EDGE,"E809"),sQuery(id+"F0.wireOp",EDGE,"E810"),sQuery(id+"F0.wireOp",EDGE,"E811"),sQuery(id+"F0.wireOp",EDGE,"E812"),sQuery(id+"F0.wireOp",EDGE,"E813"),sQuery(id+"F0.wireOp",EDGE,"E814"),sQuery(id+"F0.wireOp",EDGE,"E815"),sQuery(id+"F0.wireOp",EDGE,"E816"),sQuery(id+"F0.wireOp",EDGE,"E817"),sQuery(id+"F0.wireOp",EDGE,"E818"),sQuery(id+"F0.wireOp",EDGE,"E819"),sQuery(id+"F0.wireOp",EDGE,"E820"),sQuery(id+"F0.wireOp",EDGE,"E821"),sQuery(id+"F0.wireOp",EDGE,"E822"),sQuery(id+"F0.wireOp",EDGE,"E823"),sQuery(id+"F0.wireOp",EDGE,"E824"),sQuery(id+"F0.wireOp",EDGE,"E825"),sQuery(id+"F0.wireOp",EDGE,"E826"),sQuery(id+"F0.wireOp",EDGE,"E827"),sQuery(id+"F0.wireOp",EDGE,"E828"),sQuery(id+"F0.wireOp",EDGE,"E829"),sQuery(id+"F0.wireOp",EDGE,"E830"),sQuery(id+"F0.wireOp",EDGE,"E831"),sQuery(id+"F0.wireOp",EDGE,"E832"),sQuery(id+"F0.wireOp",EDGE,"E833"),sQuery(id+"F0.wireOp",EDGE,"E834"),sQuery(id+"F0.wireOp",EDGE,"E835"),sQuery(id+"F0.wireOp",EDGE,"E836"),sQuery(id+"F0.wireOp",EDGE,"E837"),sQuery(id+"F0.wireOp",EDGE,"E838"),sQuery(id+"F0.wireOp",EDGE,"E839"),sQuery(id+"F0.wireOp",EDGE,"E840"),sQuery(id+"F0.wireOp",EDGE,"E841"),sQuery(id+"F0.wireOp",EDGE,"E842"),sQuery(id+"F0.wireOp",EDGE,"E843"),sQuery(id+"F0.wireOp",EDGE,"E844"),sQuery(id+"F0.wireOp",EDGE,"E845"),sQuery(id+"F0.wireOp",EDGE,"E846"),sQuery(id+"F0.wireOp",EDGE,"E847"),sQuery(id+"F0.wireOp",EDGE,"E848"),sQuery(id+"F0.wireOp",EDGE,"E849"),sQuery(id+"F0.wireOp",EDGE,"E850"),sQuery(id+"F0.wireOp",EDGE,"E851"),sQuery(id+"F0.wireOp",EDGE,"E852"),sQuery(id+"F0.wireOp",EDGE,"E853"),sQuery(id+"F0.wireOp",EDGE,"E854"),sQuery(id+"F0.wireOp",EDGE,"E855"),sQuery(id+"F0.wireOp",EDGE,"E856"),sQuery(id+"F0.wireOp",EDGE,"E857"),sQuery(id+"F0.wireOp",EDGE,"E858"),sQuery(id+"F0.wireOp",EDGE,"E859"),sQuery(id+"F0.wireOp",EDGE,"E860"),sQuery(id+"F0.wireOp",EDGE,"E861"),sQuery(id+"F0.wireOp",EDGE,"E862"),sQuery(id+"F0.wireOp",EDGE,"E863"),sQuery(id+"F0.wireOp",EDGE,"E864"),sQuery(id+"F0.wireOp",EDGE,"E865"),sQuery(id+"F0.wireOp",EDGE,"E866"),sQuery(id+"F0.wireOp",EDGE,"E867"),sQuery(id+"F0.wireOp",EDGE,"E868"),sQuery(id+"F0.wireOp",EDGE,"E869"),sQuery(id+"F0.wireOp",EDGE,"E870"),sQuery(id+"F0.wireOp",EDGE,"E871"),sQuery(id+"F0.wireOp",EDGE,"E872"),sQuery(id+"F0.wireOp",EDGE,"E873"),sQuery(id+"F0.wireOp",EDGE,"E874"),sQuery(id+"F0.wireOp",EDGE,"E875"),sQuery(id+"F0.wireOp",EDGE,"E876"),sQuery(id+"F0.wireOp",EDGE,"E877"),sQuery(id+"F0.wireOp",EDGE,"E878"),sQuery(id+"F0.wireOp",EDGE,"E879"),sQuery(id+"F0.wireOp",EDGE,"E880"),sQuery(id+"F0.wireOp",EDGE,"E881"),sQuery(id+"F0.wireOp",EDGE,"E882"),sQuery(id+"F0.wireOp",EDGE,"E883"),sQuery(id+"F0.wireOp",EDGE,"E884"),sQuery(id+"F0.wireOp",EDGE,"E885"),sQuery(id+"F0.wireOp",EDGE,"E886"),sQuery(id+"F0.wireOp",EDGE,"E887"),sQuery(id+"F0.wireOp",EDGE,"E888"),sQuery(id+"F0.wireOp",EDGE,"E889"),sQuery(id+"F0.wireOp",EDGE,"E890"),sQuery(id+"F0.wireOp",EDGE,"E891"),sQuery(id+"F0.wireOp",EDGE,"E892"),sQuery(id+"F0.wireOp",EDGE,"E893"),sQuery(id+"F0.wireOp",EDGE,"E894"),sQuery(id+"F0.wireOp",EDGE,"E895"),sQuery(id+"F0.wireOp",EDGE,"E896"),sQuery(id+"F0.wireOp",EDGE,"E897"),sQuery(id+"F0.wireOp",EDGE,"E898"),sQuery(id+"F0.wireOp",EDGE,"E899"),sQuery(id+"F0.wireOp",EDGE,"E900"),sQuery(id+"F0.wireOp",EDGE,"E901"),sQuery(id+"F0.wireOp",EDGE,"E902"),sQuery(id+"F0.wireOp",EDGE,"E903"),sQuery(id+"F0.wireOp",EDGE,"E904"),sQuery(id+"F0.wireOp",EDGE,"E905"),sQuery(id+"F0.wireOp",EDGE,"E906"),sQuery(id+"F0.wireOp",EDGE,"E907"),sQuery(id+"F0.wireOp",EDGE,"E908"),sQuery(id+"F0.wireOp",EDGE,"E909"),sQuery(id+"F0.wireOp",EDGE,"E910"),sQuery(id+"F0.wireOp",EDGE,"E911"),sQuery(id+"F0.wireOp",EDGE,"E912"),sQuery(id+"F0.wireOp",EDGE,"E913"),sQuery(id+"F0.wireOp",EDGE,"E914"),sQuery(id+"F0.wireOp",EDGE,"E915"),sQuery(id+"F0.wireOp",EDGE,"E916"),sQuery(id+"F0.wireOp",EDGE,"E917"),sQuery(id+"F0.wireOp",EDGE,"E918"),sQuery(id+"F0.wireOp",EDGE,"E919"),sQuery(id+"F0.wireOp",EDGE,"E920"),sQuery(id+"F0.wireOp",EDGE,"E921"),sQuery(id+"F0.wireOp",EDGE,"E922"),sQuery(id+"F0.wireOp",EDGE,"E923"),sQuery(id+"F0.wireOp",EDGE,"E924"),sQuery(id+"F0.wireOp",EDGE,"E925"),sQuery(id+"F0.wireOp",EDGE,"E926"),sQuery(id+"F0.wireOp",EDGE,"E927"),sQuery(id+"F0.wireOp",EDGE,"E928"),sQuery(id+"F0.wireOp",EDGE,"E929"),sQuery(id+"F0.wireOp",EDGE,"E930"),sQuery(id+"F0.wireOp",EDGE,"E931"),sQuery(id+"F0.wireOp",EDGE,"E932"),sQuery(id+"F0.wireOp",EDGE,"E933"),sQuery(id+"F0.wireOp",EDGE,"E934"),sQuery(id+"F0.wireOp",EDGE,"E935"),sQuery(id+"F0.wireOp",EDGE,"E936"),sQuery(id+"F0.wireOp",EDGE,"E937"),sQuery(id+"F0.wireOp",EDGE,"E938"),sQuery(id+"F0.wireOp",EDGE,"E939"),sQuery(id+"F0.wireOp",EDGE,"E940"),sQuery(id+"F0.wireOp",EDGE,"E941"),sQuery(id+"F0.wireOp",EDGE,"E942"),sQuery(id+"F0.wireOp",EDGE,"E943"),sQuery(id+"F0.wireOp",EDGE,"E944"),sQuery(id+"F0.wireOp",EDGE,"E945"),sQuery(id+"F0.wireOp",EDGE,"E946"),sQuery(id+"F0.wireOp",EDGE,"E947"),sQuery(id+"F0.wireOp",EDGE,"E948"),sQuery(id+"F0.wireOp",EDGE,"E949"),sQuery(id+"F0.wireOp",EDGE,"E950"),sQuery(id+"F0.wireOp",EDGE,"E951"),sQuery(id+"F0.wireOp",EDGE,"E952"),sQuery(id+"F0.wireOp",EDGE,"E953"),sQuery(id+"F0.wireOp",EDGE,"E954"),sQuery(id+"F0.wireOp",EDGE,"E955"),sQuery(id+"F0.wireOp",EDGE,"E956"),sQuery(id+"F0.wireOp",EDGE,"E957"),sQuery(id+"F0.wireOp",EDGE,"E958"),sQuery(id+"F0.wireOp",EDGE,"E959"),sQuery(id+"F0.wireOp",EDGE,"E960"),sQuery(id+"F0.wireOp",EDGE,"E961"),sQuery(id+"F0.wireOp",EDGE,"E962"),sQuery(id+"F0.wireOp",EDGE,"E963"),sQuery(id+"F0.wireOp",EDGE,"E964"),sQuery(id+"F0.wireOp",EDGE,"E965"),sQuery(id+"F0.wireOp",EDGE,"E966"),sQuery(id+"F0.wireOp",EDGE,"E967"),sQuery(id+"F0.wireOp",EDGE,"E968"),sQuery(id+"F0.wireOp",EDGE,"E969"),sQuery(id+"F0.wireOp",EDGE,"E970"),sQuery(id+"F0.wireOp",EDGE,"E971"),sQuery(id+"F0.wireOp",EDGE,"E972"),sQuery(id+"F0.wireOp",EDGE,"E973"),sQuery(id+"F0.wireOp",EDGE,"E974"),sQuery(id+"F0.wireOp",EDGE,"E975"),sQuery(id+"F0.wireOp",EDGE,"E976"),sQuery(id+"F0.wireOp",EDGE,"E977"),sQuery(id+"F0.wireOp",EDGE,"E978"),sQuery(id+"F0.wireOp",EDGE,"E979"),sQuery(id+"F0.wireOp",EDGE,"E980"),sQuery(id+"F0.wireOp",EDGE,"E981"),sQuery(id+"F0.wireOp",EDGE,"E982"),sQuery(id+"F0.wireOp",EDGE,"E983"),sQuery(id+"F0.wireOp",EDGE,"E984"),sQuery(id+"F0.wireOp",EDGE,"E985"),sQuery(id+"F0.wireOp",EDGE,"E986"),sQuery(id+"F0.wireOp",EDGE,"E987"),sQuery(id+"F0.wireOp",EDGE,"E988"),sQuery(id+"F0.wireOp",EDGE,"E989"),sQuery(id+"F0.wireOp",EDGE,"E990"),sQuery(id+"F0.wireOp",EDGE,"E991"),sQuery(id+"F0.wireOp",EDGE,"E992"),sQuery(id+"F0.wireOp",EDGE,"E993"),sQuery(id+"F0.wireOp",EDGE,"E994"),sQuery(id+"F0.wireOp",EDGE,"E995"),sQuery(id+"F0.wireOp",EDGE,"E996"),sQuery(id+"F0.wireOp",EDGE,"E997"),sQuery(id+"F0.wireOp",EDGE,"E998"),sQuery(id+"F0.wireOp",EDGE,"E999"),sQuery(id+"F0.wireOp",EDGE,"E1000"),sQuery(id+"F0.wireOp",EDGE,"E1001"),sQuery(id+"F0.wireOp",EDGE,"E1002"),sQuery(id+"F0.wireOp",EDGE,"E1003"),sQuery(id+"F0.wireOp",EDGE,"E1004"),sQuery(id+"F0.wireOp",EDGE,"E1005"),sQuery(id+"F0.wireOp",EDGE,"E1006"),sQuery(id+"F0.wireOp",EDGE,"E1007"),sQuery(id+"F0.wireOp",EDGE,"E1008"),sQuery(id+"F0.wireOp",EDGE,"E1009"),sQuery(id+"F0.wireOp",EDGE,"E1010"),sQuery(id+"F0.wireOp",EDGE,"E1011"),sQuery(id+"F0.wireOp",EDGE,"E1012"),sQuery(id+"F0.wireOp",EDGE,"E1013"),sQuery(id+"F0.wireOp",EDGE,"E1014"),sQuery(id+"F0.wireOp",EDGE,"E1015"),sQuery(id+"F0.wireOp",EDGE,"E1016"),sQuery(id+"F0.wireOp",EDGE,"E1017"),sQuery(id+"F0.wireOp",EDGE,"E1018"),sQuery(id+"F0.wireOp",EDGE,"E1019"),sQuery(id+"F0.wireOp",EDGE,"E1020"),sQuery(id+"F0.wireOp",EDGE,"E1021"),sQuery(id+"F0.wireOp",EDGE,"E1022"),sQuery(id+"F0.wireOp",EDGE,"E1023"),sQuery(id+"F0.wireOp",EDGE,"E1024"),sQuery(id+"F0.wireOp",EDGE,"E1025"),sQuery(id+"F0.wireOp",EDGE,"E1026"),sQuery(id+"F0.wireOp",EDGE,"E1027"),sQuery(id+"F0.wireOp",EDGE,"E1028"),sQuery(id+"F0.wireOp",EDGE,"E1029"),sQuery(id+"F0.wireOp",EDGE,"E1030"),sQuery(id+"F0.wireOp",EDGE,"E1031"),sQuery(id+"F0.wireOp",EDGE,"E1032"),sQuery(id+"F0.wireOp",EDGE,"E1033"),sQuery(id+"F0.wireOp",EDGE,"E1034"),sQuery(id+"F0.wireOp",EDGE,"E1035"),sQuery(id+"F0.wireOp",EDGE,"E1036"),sQuery(id+"F0.wireOp",EDGE,"E1037"),sQuery(id+"F0.wireOp",EDGE,"E1038"),sQuery(id+"F0.wireOp",EDGE,"E1039"),sQuery(id+"F0.wireOp",EDGE,"E1040"),sQuery(id+"F0.wireOp",EDGE,"E1041"),sQuery(id+"F0.wireOp",EDGE,"E1042"),sQuery(id+"F0.wireOp",EDGE,"E1043"),sQuery(id+"F0.wireOp",EDGE,"E1044"),sQuery(id+"F0.wireOp",EDGE,"E1045"),sQuery(id+"F0.wireOp",EDGE,"E1046"),sQuery(id+"F0.wireOp",EDGE,"E1047"),sQuery(id+"F0.wireOp",EDGE,"E1048"),sQuery(id+"F0.wireOp",EDGE,"E1049"),sQuery(id+"F0.wireOp",EDGE,"E1050"),sQuery(id+"F0.wireOp",EDGE,"E1051"),sQuery(id+"F0.wireOp",EDGE,"E1052"),sQuery(id+"F0.wireOp",EDGE,"E1053"),sQuery(id+"F0.wireOp",EDGE,"E1054"),sQuery(id+"F0.wireOp",EDGE,"E1055"),sQuery(id+"F0.wireOp",EDGE,"E1056"),sQuery(id+"F0.wireOp",EDGE,"E1057"),sQuery(id+"F0.wireOp",EDGE,"E1058"),sQuery(id+"F0.wireOp",EDGE,"E1059"),sQuery(id+"F0.wireOp",EDGE,"E1060"),sQuery(id+"F0.wireOp",EDGE,"E1061"),sQuery(id+"F0.wireOp",EDGE,"E1062"),sQuery(id+"F0.wireOp",EDGE,"E1063"),sQuery(id+"F0.wireOp",EDGE,"E1064"),sQuery(id+"F0.wireOp",EDGE,"E1065"),sQuery(id+"F0.wireOp",EDGE,"E1066"),sQuery(id+"F0.wireOp",EDGE,"E1067"),sQuery(id+"F0.wireOp",EDGE,"E1068"),sQuery(id+"F0.wireOp",EDGE,"E1069"),sQuery(id+"F0.wireOp",EDGE,"E1070"),sQuery(id+"F0.wireOp",EDGE,"E1071"),sQuery(id+"F0.wireOp",EDGE,"E1072"),sQuery(id+"F0.wireOp",EDGE,"E1073"),sQuery(id+"F0.wireOp",EDGE,"E1074"),sQuery(id+"F0.wireOp",EDGE,"E1075"),sQuery(id+"F0.wireOp",EDGE,"E1076"),sQuery(id+"F0.wireOp",EDGE,"E1077"),sQuery(id+"F0.wireOp",EDGE,"E1078"),sQuery(id+"F0.wireOp",EDGE,"E1079"),sQuery(id+"F0.wireOp",EDGE,"E1080"),sQuery(id+"F0.wireOp",EDGE,"E1081"),sQuery(id+"F0.wireOp",EDGE,"E1082"),sQuery(id+"F0.wireOp",EDGE,"E1083"),sQuery(id+"F0.wireOp",EDGE,"E1084"),sQuery(id+"F0.wireOp",EDGE,"E1085"),sQuery(id+"F0.wireOp",EDGE,"E1086"),sQuery(id+"F0.wireOp",EDGE,"E1087"),sQuery(id+"F0.wireOp",EDGE,"E1088"),sQuery(id+"F0.wireOp",EDGE,"E1089"),sQuery(id+"F0.wireOp",EDGE,"E1090"),sQuery(id+"F0.wireOp",EDGE,"E1091"),sQuery(id+"F0.wireOp",EDGE,"E1092"),sQuery(id+"F0.wireOp",EDGE,"E1093"),sQuery(id+"F0.wireOp",EDGE,"E1094"),sQuery(id+"F0.wireOp",EDGE,"E1095"),sQuery(id+"F0.wireOp",EDGE,"E1096"),sQuery(id+"F0.wireOp",EDGE,"E1097"),sQuery(id+"F0.wireOp",EDGE,"E1098"),sQuery(id+"F0.wireOp",EDGE,"E1099"),sQuery(id+"F0.wireOp",EDGE,"E1100"),sQuery(id+"F0.wireOp",EDGE,"E1101"),sQuery(id+"F0.wireOp",EDGE,"E1102"),sQuery(id+"F0.wireOp",EDGE,"E1103"),sQuery(id+"F0.wireOp",EDGE,"E1104"),sQuery(id+"F0.wireOp",EDGE,"E1105"),sQuery(id+"F0.wireOp",EDGE,"E1106"),sQuery(id+"F0.wireOp",EDGE,"E1107"),sQuery(id+"F0.wireOp",EDGE,"E1108"),sQuery(id+"F0.wireOp",EDGE,"E1109"),sQuery(id+"F0.wireOp",EDGE,"E1110"),sQuery(id+"F0.wireOp",EDGE,"E1111"),sQuery(id+"F0.wireOp",EDGE,"E1112"),sQuery(id+"F0.wireOp",EDGE,"E1113"),sQuery(id+"F0.wireOp",EDGE,"E1114"),sQuery(id+"F0.wireOp",EDGE,"E1115"),sQuery(id+"F0.wireOp",EDGE,"E1116"),sQuery(id+"F0.wireOp",EDGE,"E1117"),sQuery(id+"F0.wireOp",EDGE,"E1118"),sQuery(id+"F0.wireOp",EDGE,"E1119"),sQuery(id+"F0.wireOp",EDGE,"E1120"),sQuery(id+"F0.wireOp",EDGE,"E1121"),sQuery(id+"F0.wireOp",EDGE,"E1122"),sQuery(id+"F0.wireOp",EDGE,"E1123"),sQuery(id+"F0.wireOp",EDGE,"E1124"),sQuery(id+"F0.wireOp",EDGE,"E1125"),sQuery(id+"F0.wireOp",EDGE,"E1126"),sQuery(id+"F0.wireOp",EDGE,"E1127"),sQuery(id+"F0.wireOp",EDGE,"E1128"),sQuery(id+"F0.wireOp",EDGE,"E1129"),sQuery(id+"F0.wireOp",EDGE,"E1130"),sQuery(id+"F0.wireOp",EDGE,"E1131"),sQuery(id+"F0.wireOp",EDGE,"E1132"),sQuery(id+"F0.wireOp",EDGE,"E1133"),sQuery(id+"F0.wireOp",EDGE,"E1134"),sQuery(id+"F0.wireOp",EDGE,"E1135"),sQuery(id+"F0.wireOp",EDGE,"E1136"),sQuery(id+"F0.wireOp",EDGE,"E1137"),sQuery(id+"F0.wireOp",EDGE,"E1138"),sQuery(id+"F0.wireOp",EDGE,"E1139"),sQuery(id+"F0.wireOp",EDGE,"E1140"),sQuery(id+"F0.wireOp",EDGE,"E1141"),sQuery(id+"F0.wireOp",EDGE,"E1142"),sQuery(id+"F0.wireOp",EDGE,"E1143"),sQuery(id+"F0.wireOp",EDGE,"E1144"),sQuery(id+"F0.wireOp",EDGE,"E1145"),sQuery(id+"F0.wireOp",EDGE,"E1146"),sQuery(id+"F0.wireOp",EDGE,"E1147"),sQuery(id+"F0.wireOp",EDGE,"E1148"),sQuery(id+"F0.wireOp",EDGE,"E1149"),sQuery(id+"F0.wireOp",EDGE,"E1150"),sQuery(id+"F0.wireOp",EDGE,"E1151"),sQuery(id+"F0.wireOp",EDGE,"E1152"),sQuery(id+"F0.wireOp",EDGE,"E1153"),sQuery(id+"F0.wireOp",EDGE,"E1154"),sQuery(id+"F0.wireOp",EDGE,"E1155"),sQuery(id+"F0.wireOp",EDGE,"E1156"),sQuery(id+"F0.wireOp",EDGE,"E1157"),sQuery(id+"F0.wireOp",EDGE,"E1158"),sQuery(id+"F0.wireOp",EDGE,"E1159"),sQuery(id+"F0.wireOp",EDGE,"E1160"),sQuery(id+"F0.wireOp",EDGE,"E1161"),sQuery(id+"F0.wireOp",EDGE,"E1162"),sQuery(id+"F0.wireOp",EDGE,"E1163"),sQuery(id+"F0.wireOp",EDGE,"E1164"),sQuery(id+"F0.wireOp",EDGE,"E1165"),sQuery(id+"F0.wireOp",EDGE,"E1166"),sQuery(id+"F0.wireOp",EDGE,"E1167"),sQuery(id+"F0.wireOp",EDGE,"E1168"),sQuery(id+"F0.wireOp",EDGE,"E1169"),sQuery(id+"F0.wireOp",EDGE,"E1170"),sQuery(id+"F0.wireOp",EDGE,"E1171"),sQuery(id+"F0.wireOp",EDGE,"E1172"),sQuery(id+"F0.wireOp",EDGE,"E1173"),sQuery(id+"F0.wireOp",EDGE,"E1174"),sQuery(id+"F0.wireOp",EDGE,"E1175"),sQuery(id+"F0.wireOp",EDGE,"E1176"),sQuery(id+"F0.wireOp",EDGE,"E1177"),sQuery(id+"F0.wireOp",EDGE,"E1178"),sQuery(id+"F0.wireOp",EDGE,"E1179"),sQuery(id+"F0.wireOp",EDGE,"E1180"),sQuery(id+"F0.wireOp",EDGE,"E1181"),sQuery(id+"F0.wireOp",EDGE,"E1182"),sQuery(id+"F0.wireOp",EDGE,"E1183"),sQuery(id+"F0.wireOp",EDGE,"E1184"),sQuery(id+"F0.wireOp",EDGE,"E1185"),sQuery(id+"F0.wireOp",EDGE,"E1186"),sQuery(id+"F0.wireOp",EDGE,"E1187"),sQuery(id+"F0.wireOp",EDGE,"E1188"),sQuery(id+"F0.wireOp",EDGE,"E1189"),sQuery(id+"F0.wireOp",EDGE,"E1190"),sQuery(id+"F0.wireOp",EDGE,"E1191"),sQuery(id+"F0.wireOp",EDGE,"E1192"),sQuery(id+"F0.wireOp",EDGE,"E1193"),sQuery(id+"F0.wireOp",EDGE,"E1194"),sQuery(id+"F0.wireOp",EDGE,"E1195"),sQuery(id+"F0.wireOp",EDGE,"E1196"),sQuery(id+"F0.wireOp",EDGE,"E1197"),sQuery(id+"F0.wireOp",EDGE,"E1198"),sQuery(id+"F0.wireOp",EDGE,"E1199"),sQuery(id+"F0.wireOp",EDGE,"E1200"),sQuery(id+"F0.wireOp",EDGE,"E1201"),sQuery(id+"F0.wireOp",EDGE,"E1202"),sQuery(id+"F0.wireOp",EDGE,"E1203"),sQuery(id+"F0.wireOp",EDGE,"E1204"),sQuery(id+"F0.wireOp",EDGE,"E1205"),sQuery(id+"F0.wireOp",EDGE,"E1206"),sQuery(id+"F0.wireOp",EDGE,"E1207"),sQuery(id+"F0.wireOp",EDGE,"E1208"),sQuery(id+"F0.wireOp",EDGE,"E1209"),sQuery(id+"F0.wireOp",EDGE,"E1210"),sQuery(id+"F0.wireOp",EDGE,"E1211"),sQuery(id+"F0.wireOp",EDGE,"E1212"),sQuery(id+"F0.wireOp",EDGE,"E1213"),sQuery(id+"F0.wireOp",EDGE,"E1214"),sQuery(id+"F0.wireOp",EDGE,"E1215"),sQuery(id+"F0.wireOp",EDGE,"E1216"),sQuery(id+"F0.wireOp",EDGE,"E1217"),sQuery(id+"F0.wireOp",EDGE,"E1218"),sQuery(id+"F0.wireOp",EDGE,"E1219"),sQuery(id+"F0.wireOp",EDGE,"E1220"),sQuery(id+"F0.wireOp",EDGE,"E1221"),sQuery(id+"F0.wireOp",EDGE,"E1222"),sQuery(id+"F0.wireOp",EDGE,"E1223"),sQuery(id+"F0.wireOp",EDGE,"E1224"),sQuery(id+"F0.wireOp",EDGE,"E1225"),sQuery(id+"F0.wireOp",EDGE,"E1226"),sQuery(id+"F0.wireOp",EDGE,"E1227"),sQuery(id+"F0.wireOp",EDGE,"E1228"),sQuery(id+"F0.wireOp",EDGE,"E1229"),sQuery(id+"F0.wireOp",EDGE,"E1230"),sQuery(id+"F0.wireOp",EDGE,"E1231"),sQuery(id+"F0.wireOp",EDGE,"E1232"),sQuery(id+"F0.wireOp",EDGE,"E1233"),sQuery(id+"F0.wireOp",EDGE,"E1234"),sQuery(id+"F0.wireOp",EDGE,"E1235"),sQuery(id+"F0.wireOp",EDGE,"E1236"),sQuery(id+"F0.wireOp",EDGE,"E1237"),sQuery(id+"F0.wireOp",EDGE,"E1238"),sQuery(id+"F0.wireOp",EDGE,"E1239"),sQuery(id+"F0.wireOp",EDGE,"E1240"),sQuery(id+"F0.wireOp",EDGE,"E1241"),sQuery(id+"F0.wireOp",EDGE,"E1242"),sQuery(id+"F0.wireOp",EDGE,"E1243"),sQuery(id+"F0.wireOp",EDGE,"E1244"),sQuery(id+"F0.wireOp",EDGE,"E1245"),sQuery(id+"F0.wireOp",EDGE,"E1246"),sQuery(id+"F0.wireOp",EDGE,"E1247"),sQuery(id+"F0.wireOp",EDGE,"E1248"),sQuery(id+"F0.wireOp",EDGE,"E1249"),sQuery(id+"F0.wireOp",EDGE,"E1250"),sQuery(id+"F0.wireOp",EDGE,"E1251"),sQuery(id+"F0.wireOp",EDGE,"E1252"),sQuery(id+"F0.wireOp",EDGE,"E1253"),sQuery(id+"F0.wireOp",EDGE,"E1254"),sQuery(id+"F0.wireOp",EDGE,"E1255"),sQuery(id+"F0.wireOp",EDGE,"E1256"),sQuery(id+"F0.wireOp",EDGE,"E1257"),sQuery(id+"F0.wireOp",EDGE,"E1258"),sQuery(id+"F0.wireOp",EDGE,"E1259"),sQuery(id+"F0.wireOp",EDGE,"E1260"),sQuery(id+"F0.wireOp",EDGE,"E1261"),sQuery(id+"F0.wireOp",EDGE,"E1262"),sQuery(id+"F0.wireOp",EDGE,"E1263"),sQuery(id+"F0.wireOp",EDGE,"E1264"),sQuery(id+"F0.wireOp",EDGE,"E1265"),sQuery(id+"F0.wireOp",EDGE,"E1266"),sQuery(id+"F0.wireOp",EDGE,"E1267"),sQuery(id+"F0.wireOp",EDGE,"E1268"),sQuery(id+"F0.wireOp",EDGE,"E1269"),sQuery(id+"F0.wireOp",EDGE,"E1270"),sQuery(id+"F0.wireOp",EDGE,"E1271"),sQuery(id+"F0.wireOp",EDGE,"E1272"),sQuery(id+"F0.wireOp",EDGE,"E1273"),sQuery(id+"F0.wireOp",EDGE,"E1274"),sQuery(id+"F0.wireOp",EDGE,"E1275"),sQuery(id+"F0.wireOp",EDGE,"E1276"),sQuery(id+"F0.wireOp",EDGE,"E1277"),sQuery(id+"F0.wireOp",EDGE,"E1278"),sQuery(id+"F0.wireOp",EDGE,"E1279"),sQuery(id+"F0.wireOp",EDGE,"E1280"),sQuery(id+"F0.wireOp",EDGE,"E1281"),sQuery(id+"F0.wireOp",EDGE,"E1282"),sQuery(id+"F0.wireOp",EDGE,"E1283"),sQuery(id+"F0.wireOp",EDGE,"E1284"),sQuery(id+"F0.wireOp",EDGE,"E1285"),sQuery(id+"F0.wireOp",EDGE,"E1286"),sQuery(id+"F0.wireOp",EDGE,"E1287"),sQuery(id+"F0.wireOp",EDGE,"E1288"),sQuery(id+"F0.wireOp",EDGE,"E1289"),sQuery(id+"F0.wireOp",EDGE,"E1290"),sQuery(id+"F0.wireOp",EDGE,"E1291"),sQuery(id+"F0.wireOp",EDGE,"E1292"),sQuery(id+"F0.wireOp",EDGE,"E1293"),sQuery(id+"F0.wireOp",EDGE,"E1294"),sQuery(id+"F0.wireOp",EDGE,"E1295"),sQuery(id+"F0.wireOp",EDGE,"E1296"),sQuery(id+"F0.wireOp",EDGE,"E1297"),sQuery(id+"F0.wireOp",EDGE,"E1298"),sQuery(id+"F0.wireOp",EDGE,"E1299"),sQuery(id+"F0.wireOp",EDGE,"E1300"),sQuery(id+"F0.wireOp",EDGE,"E1301"),sQuery(id+"F0.wireOp",EDGE,"E1302"),sQuery(id+"F0.wireOp",EDGE,"E1303"),sQuery(id+"F0.wireOp",EDGE,"E1304"),sQuery(id+"F0.wireOp",EDGE,"E1305"),sQuery(id+"F0.wireOp",EDGE,"E1306"),sQuery(id+"F0.wireOp",EDGE,"E1307"),sQuery(id+"F0.wireOp",EDGE,"E1308"),sQuery(id+"F0.wireOp",EDGE,"E1309"),sQuery(id+"F0.wireOp",EDGE,"E1310"),sQuery(id+"F0.wireOp",EDGE,"E1311"),sQuery(id+"F0.wireOp",EDGE,"E1312"),sQuery(id+"F0.wireOp",EDGE,"E1313"),sQuery(id+"F0.wireOp",EDGE,"E1314"),sQuery(id+"F0.wireOp",EDGE,"E1315"),sQuery(id+"F0.wireOp",EDGE,"E1316"),sQuery(id+"F0.wireOp",EDGE,"E1317"),sQuery(id+"F0.wireOp",EDGE,"E1318"),sQuery(id+"F0.wireOp",EDGE,"E1319"),sQuery(id+"F0.wireOp",EDGE,"E1320"),sQuery(id+"F0.wireOp",EDGE,"E1321"),sQuery(id+"F0.wireOp",EDGE,"E1322"),sQuery(id+"F0.wireOp",EDGE,"E1323"),sQuery(id+"F0.wireOp",EDGE,"E1324"),sQuery(id+"F0.wireOp",EDGE,"E1325"),sQuery(id+"F0.wireOp",EDGE,"E1326"),sQuery(id+"F0.wireOp",EDGE,"E1327"),sQuery(id+"F0.wireOp",EDGE,"E1328"),sQuery(id+"F0.wireOp",EDGE,"E1329"),sQuery(id+"F0.wireOp",EDGE,"E1330"),sQuery(id+"F0.wireOp",EDGE,"E1331"),sQuery(id+"F0.wireOp",EDGE,"E1332"),sQuery(id+"F0.wireOp",EDGE,"E1333"),sQuery(id+"F0.wireOp",EDGE,"E1334"),sQuery(id+"F0.wireOp",EDGE,"E1335"),sQuery(id+"F0.wireOp",EDGE,"E1336"),sQuery(id+"F0.wireOp",EDGE,"E1337"),sQuery(id+"F0.wireOp",EDGE,"E1338"),sQuery(id+"F0.wireOp",EDGE,"E1339"),sQuery(id+"F0.wireOp",EDGE,"E1340"),sQuery(id+"F0.wireOp",EDGE,"E1341"),sQuery(id+"F0.wireOp",EDGE,"E1342"),sQuery(id+"F0.wireOp",EDGE,"E1343"),sQuery(id+"F0.wireOp",EDGE,"E1344"),sQuery(id+"F0.wireOp",EDGE,"E1345"),sQuery(id+"F0.wireOp",EDGE,"E1346"),sQuery(id+"F0.wireOp",EDGE,"E1347"),sQuery(id+"F0.wireOp",EDGE,"E1348"),sQuery(id+"F0.wireOp",EDGE,"E1349"),sQuery(id+"F0.wireOp",EDGE,"E1350"),sQuery(id+"F0.wireOp",EDGE,"E1351")])],"isStart":false});
            var sketch = newSketch(context, id + "F3", { "sketchPlane" : qUnion([Q0])});
            skLineSegment(sketch, "E2248.bottom", {"start": v(155, 60) * mm, "end": v(-155, 60) * mm});
            skLineSegment(sketch, "E2248.top", {"start": v(155, -60) * mm, "end": v(-155, -60) * mm});
            skLineSegment(sketch, "E2248.left", {"start": v(155, 60) * mm, "end": v(155, -60) * mm});
            skLineSegment(sketch, "E2248.right", {"start": v(-155, 60) * mm, "end": v(-155, -60) * mm});
            skLineSegment(sketch, "E2249.bottom", {"start": v(-145, 50) * mm, "end": v(145, 50) * mm});
            skLineSegment(sketch, "E2249.top", {"start": v(-145, -50) * mm, "end": v(145, -50) * mm});
            skLineSegment(sketch, "E2249.left", {"start": v(-145, 50) * mm, "end": v(-145, -50) * mm});
            skLineSegment(sketch, "E2249.right", {"start": v(145, 50) * mm, "end": v(145, -50) * mm});
            skSolve(sketch);
        }
        {
            var Q0;
            Q0 = qSketchRegion(id + "F3", true);
            extrude(context, id + "F4", {"entities" : qUnion([Q0]), "operationType" : NewBodyOperationType.ADD, "oppositeDirection" : true, "depth" : 1.5 * mm});
        }
        {
            var Q0;
            Q0=makeQuery(id+"F4.boolean.opBoolean","MERGE",FACE,{"derivedFrom":[makeQuery(id+"F2.opExtrude","CAP_FACE",FACE,{"disambiguationData":[OSD([sQuery(id+"F1.wireOp",EDGE,"E1352"),sQuery(id+"F1.wireOp",EDGE,"E1353"),sQuery(id+"F1.wireOp",EDGE,"E1354"),sQuery(id+"F1.wireOp",EDGE,"E1355"),sQuery(id+"F1.wireOp",EDGE,"E1356"),sQuery(id+"F1.wireOp",EDGE,"E1357"),sQuery(id+"F1.wireOp",EDGE,"E1358"),sQuery(id+"F1.wireOp",EDGE,"E1359"),sQuery(id+"F1.wireOp",EDGE,"E1360"),sQuery(id+"F1.wireOp",EDGE,"E1361"),sQuery(id+"F1.wireOp",EDGE,"E1362"),sQuery(id+"F1.wireOp",EDGE,"E1363"),sQuery(id+"F1.wireOp",EDGE,"E1364"),sQuery(id+"F1.wireOp",EDGE,"E1365"),sQuery(id+"F1.wireOp",EDGE,"E1366"),sQuery(id+"F1.wireOp",EDGE,"E1367"),sQuery(id+"F1.wireOp",EDGE,"E1368"),sQuery(id+"F1.wireOp",EDGE,"E1369"),sQuery(id+"F1.wireOp",EDGE,"E1370"),sQuery(id+"F1.wireOp",EDGE,"E1371"),sQuery(id+"F1.wireOp",EDGE,"E1372"),sQuery(id+"F1.wireOp",EDGE,"E1373"),sQuery(id+"F1.wireOp",EDGE,"E1374"),sQuery(id+"F1.wireOp",EDGE,"E1375"),sQuery(id+"F1.wireOp",EDGE,"E1376"),sQuery(id+"F1.wireOp",EDGE,"E1377"),sQuery(id+"F1.wireOp",EDGE,"E1378"),sQuery(id+"F1.wireOp",EDGE,"E1379"),sQuery(id+"F1.wireOp",EDGE,"E1380"),sQuery(id+"F1.wireOp",EDGE,"E1381"),sQuery(id+"F1.wireOp",EDGE,"E1382"),sQuery(id+"F1.wireOp",EDGE,"E1383"),sQuery(id+"F1.wireOp",EDGE,"E1384"),sQuery(id+"F1.wireOp",EDGE,"E1385"),sQuery(id+"F1.wireOp",EDGE,"E1386"),sQuery(id+"F1.wireOp",EDGE,"E1387"),sQuery(id+"F1.wireOp",EDGE,"E1388"),sQuery(id+"F1.wireOp",EDGE,"E1389"),sQuery(id+"F1.wireOp",EDGE,"E1390"),sQuery(id+"F1.wireOp",EDGE,"E1391"),sQuery(id+"F1.wireOp",EDGE,"E1392"),sQuery(id+"F1.wireOp",EDGE,"E1393"),sQuery(id+"F1.wireOp",EDGE,"E1394"),sQuery(id+"F1.wireOp",EDGE,"E1395"),sQuery(id+"F1.wireOp",EDGE,"E1396"),sQuery(id+"F1.wireOp",EDGE,"E1397"),sQuery(id+"F1.wireOp",EDGE,"E1398"),sQuery(id+"F1.wireOp",EDGE,"E1399"),sQuery(id+"F1.wireOp",EDGE,"E1400"),sQuery(id+"F1.wireOp",EDGE,"E1401"),sQuery(id+"F1.wireOp",EDGE,"E1402"),sQuery(id+"F1.wireOp",EDGE,"E1403"),sQuery(id+"F1.wireOp",EDGE,"E1404"),sQuery(id+"F1.wireOp",EDGE,"E1405"),sQuery(id+"F1.wireOp",EDGE,"E1406"),sQuery(id+"F1.wireOp",EDGE,"E1407"),sQuery(id+"F1.wireOp",EDGE,"E1408"),sQuery(id+"F1.wireOp",EDGE,"E1409"),sQuery(id+"F1.wireOp",EDGE,"E1410"),sQuery(id+"F1.wireOp",EDGE,"E1411"),sQuery(id+"F1.wireOp",EDGE,"E1412"),sQuery(id+"F1.wireOp",EDGE,"E1413"),sQuery(id+"F1.wireOp",EDGE,"E1414"),sQuery(id+"F1.wireOp",EDGE,"E1415"),sQuery(id+"F1.wireOp",EDGE,"E1416"),sQuery(id+"F1.wireOp",EDGE,"E1417"),sQuery(id+"F1.wireOp",EDGE,"E1418"),sQuery(id+"F1.wireOp",EDGE,"E1419"),sQuery(id+"F1.wireOp",EDGE,"E1420"),sQuery(id+"F1.wireOp",EDGE,"E1421"),sQuery(id+"F1.wireOp",EDGE,"E1422"),sQuery(id+"F1.wireOp",EDGE,"E1423"),sQuery(id+"F1.wireOp",EDGE,"E1424"),sQuery(id+"F1.wireOp",EDGE,"E1425"),sQuery(id+"F1.wireOp",EDGE,"E1426"),sQuery(id+"F1.wireOp",EDGE,"E1427"),sQuery(id+"F1.wireOp",EDGE,"E1428"),sQuery(id+"F1.wireOp",EDGE,"E1429"),sQuery(id+"F1.wireOp",EDGE,"E1430"),sQuery(id+"F1.wireOp",EDGE,"E1431"),sQuery(id+"F1.wireOp",EDGE,"E1432"),sQuery(id+"F1.wireOp",EDGE,"E1433"),sQuery(id+"F1.wireOp",EDGE,"E1434"),sQuery(id+"F1.wireOp",EDGE,"E1435"),sQuery(id+"F1.wireOp",EDGE,"E1436"),sQuery(id+"F1.wireOp",EDGE,"E1437"),sQuery(id+"F1.wireOp",EDGE,"E1438"),sQuery(id+"F1.wireOp",EDGE,"E1439"),sQuery(id+"F1.wireOp",EDGE,"E1440"),sQuery(id+"F1.wireOp",EDGE,"E1441"),sQuery(id+"F1.wireOp",EDGE,"E1442"),sQuery(id+"F1.wireOp",EDGE,"E1443"),sQuery(id+"F1.wireOp",EDGE,"E1444"),sQuery(id+"F1.wireOp",EDGE,"E1445"),sQuery(id+"F1.wireOp",EDGE,"E1446"),sQuery(id+"F1.wireOp",EDGE,"E1447"),sQuery(id+"F1.wireOp",EDGE,"E1448"),sQuery(id+"F1.wireOp",EDGE,"E1449"),sQuery(id+"F1.wireOp",EDGE,"E1450"),sQuery(id+"F1.wireOp",EDGE,"E1451"),sQuery(id+"F1.wireOp",EDGE,"E1452"),sQuery(id+"F1.wireOp",EDGE,"E1453"),sQuery(id+"F1.wireOp",EDGE,"E1454"),sQuery(id+"F1.wireOp",EDGE,"E1455"),sQuery(id+"F1.wireOp",EDGE,"E1456"),sQuery(id+"F1.wireOp",EDGE,"E1457"),sQuery(id+"F1.wireOp",EDGE,"E1458"),sQuery(id+"F1.wireOp",EDGE,"E1459"),sQuery(id+"F1.wireOp",EDGE,"E1460"),sQuery(id+"F1.wireOp",EDGE,"E1461"),sQuery(id+"F1.wireOp",EDGE,"E1462"),sQuery(id+"F1.wireOp",EDGE,"E1463"),sQuery(id+"F1.wireOp",EDGE,"E1464"),sQuery(id+"F1.wireOp",EDGE,"E1465"),sQuery(id+"F1.wireOp",EDGE,"E1466"),sQuery(id+"F1.wireOp",EDGE,"E1467"),sQuery(id+"F1.wireOp",EDGE,"E1468"),sQuery(id+"F1.wireOp",EDGE,"E1469"),sQuery(id+"F1.wireOp",EDGE,"E1470"),sQuery(id+"F1.wireOp",EDGE,"E1471"),sQuery(id+"F1.wireOp",EDGE,"E1472"),sQuery(id+"F1.wireOp",EDGE,"E1473"),sQuery(id+"F1.wireOp",EDGE,"E1474"),sQuery(id+"F1.wireOp",EDGE,"E1475"),sQuery(id+"F1.wireOp",EDGE,"E1476"),sQuery(id+"F1.wireOp",EDGE,"E1477"),sQuery(id+"F1.wireOp",EDGE,"E1478"),sQuery(id+"F1.wireOp",EDGE,"E1479"),sQuery(id+"F1.wireOp",EDGE,"E1480"),sQuery(id+"F1.wireOp",EDGE,"E1481"),sQuery(id+"F1.wireOp",EDGE,"E1482"),sQuery(id+"F1.wireOp",EDGE,"E1483"),sQuery(id+"F1.wireOp",EDGE,"E1484"),sQuery(id+"F1.wireOp",EDGE,"E1485"),sQuery(id+"F1.wireOp",EDGE,"E1486"),sQuery(id+"F1.wireOp",EDGE,"E1487"),sQuery(id+"F1.wireOp",EDGE,"E1488"),sQuery(id+"F1.wireOp",EDGE,"E1489"),sQuery(id+"F1.wireOp",EDGE,"E1490"),sQuery(id+"F1.wireOp",EDGE,"E1491"),sQuery(id+"F1.wireOp",EDGE,"E1492"),sQuery(id+"F1.wireOp",EDGE,"E1493"),sQuery(id+"F1.wireOp",EDGE,"E1494"),sQuery(id+"F1.wireOp",EDGE,"E1495"),sQuery(id+"F1.wireOp",EDGE,"E1496"),sQuery(id+"F1.wireOp",EDGE,"E1497"),sQuery(id+"F1.wireOp",EDGE,"E1498"),sQuery(id+"F1.wireOp",EDGE,"E1499"),sQuery(id+"F1.wireOp",EDGE,"E1500"),sQuery(id+"F1.wireOp",EDGE,"E1501"),sQuery(id+"F1.wireOp",EDGE,"E1502"),sQuery(id+"F1.wireOp",EDGE,"E1503"),sQuery(id+"F1.wireOp",EDGE,"E1504"),sQuery(id+"F1.wireOp",EDGE,"E1505"),sQuery(id+"F1.wireOp",EDGE,"E1506"),sQuery(id+"F1.wireOp",EDGE,"E1507"),sQuery(id+"F1.wireOp",EDGE,"E1508"),sQuery(id+"F1.wireOp",EDGE,"E1509"),sQuery(id+"F1.wireOp",EDGE,"E1510"),sQuery(id+"F1.wireOp",EDGE,"E1511"),sQuery(id+"F1.wireOp",EDGE,"E1512"),sQuery(id+"F1.wireOp",EDGE,"E1513"),sQuery(id+"F1.wireOp",EDGE,"E1514"),sQuery(id+"F1.wireOp",EDGE,"E1515"),sQuery(id+"F1.wireOp",EDGE,"E1516"),sQuery(id+"F1.wireOp",EDGE,"E1517"),sQuery(id+"F1.wireOp",EDGE,"E1518"),sQuery(id+"F1.wireOp",EDGE,"E1519"),sQuery(id+"F1.wireOp",EDGE,"E1520"),sQuery(id+"F1.wireOp",EDGE,"E1521"),sQuery(id+"F1.wireOp",EDGE,"E1522"),sQuery(id+"F1.wireOp",EDGE,"E1523"),sQuery(id+"F1.wireOp",EDGE,"E1524"),sQuery(id+"F1.wireOp",EDGE,"E1525"),sQuery(id+"F1.wireOp",EDGE,"E1526"),sQuery(id+"F1.wireOp",EDGE,"E1527"),sQuery(id+"F1.wireOp",EDGE,"E1528"),sQuery(id+"F1.wireOp",EDGE,"E1529"),sQuery(id+"F1.wireOp",EDGE,"E1530"),sQuery(id+"F1.wireOp",EDGE,"E1531"),sQuery(id+"F1.wireOp",EDGE,"E1532"),sQuery(id+"F1.wireOp",EDGE,"E1533"),sQuery(id+"F1.wireOp",EDGE,"E1534"),sQuery(id+"F1.wireOp",EDGE,"E1535"),sQuery(id+"F1.wireOp",EDGE,"E1536"),sQuery(id+"F1.wireOp",EDGE,"E1537"),sQuery(id+"F1.wireOp",EDGE,"E1538"),sQuery(id+"F1.wireOp",EDGE,"E1539"),sQuery(id+"F1.wireOp",EDGE,"E1540"),sQuery(id+"F1.wireOp",EDGE,"E1541"),sQuery(id+"F1.wireOp",EDGE,"E1542"),sQuery(id+"F1.wireOp",EDGE,"E1543"),sQuery(id+"F1.wireOp",EDGE,"E1544"),sQuery(id+"F1.wireOp",EDGE,"E1545"),sQuery(id+"F1.wireOp",EDGE,"E1546"),sQuery(id+"F1.wireOp",EDGE,"E1547"),sQuery(id+"F1.wireOp",EDGE,"E1548"),sQuery(id+"F1.wireOp",EDGE,"E1549"),sQuery(id+"F1.wireOp",EDGE,"E1550"),sQuery(id+"F1.wireOp",EDGE,"E1551"),sQuery(id+"F1.wireOp",EDGE,"E1552"),sQuery(id+"F1.wireOp",EDGE,"E1553"),sQuery(id+"F1.wireOp",EDGE,"E1554"),sQuery(id+"F1.wireOp",EDGE,"E1555"),sQuery(id+"F1.wireOp",EDGE,"E1556"),sQuery(id+"F1.wireOp",EDGE,"E1557"),sQuery(id+"F1.wireOp",EDGE,"E1558"),sQuery(id+"F1.wireOp",EDGE,"E1559"),sQuery(id+"F1.wireOp",EDGE,"E1560"),sQuery(id+"F1.wireOp",EDGE,"E1561"),sQuery(id+"F1.wireOp",EDGE,"E1562"),sQuery(id+"F1.wireOp",EDGE,"E1563"),sQuery(id+"F1.wireOp",EDGE,"E1564"),sQuery(id+"F1.wireOp",EDGE,"E1565"),sQuery(id+"F1.wireOp",EDGE,"E1566"),sQuery(id+"F1.wireOp",EDGE,"E1567"),sQuery(id+"F1.wireOp",EDGE,"E1568"),sQuery(id+"F1.wireOp",EDGE,"E1569"),sQuery(id+"F1.wireOp",EDGE,"E1570"),sQuery(id+"F1.wireOp",EDGE,"E1571"),sQuery(id+"F1.wireOp",EDGE,"E1572"),sQuery(id+"F1.wireOp",EDGE,"E1573"),sQuery(id+"F1.wireOp",EDGE,"E1574"),sQuery(id+"F1.wireOp",EDGE,"E1575"),sQuery(id+"F1.wireOp",EDGE,"E1576"),sQuery(id+"F1.wireOp",EDGE,"E1577"),sQuery(id+"F1.wireOp",EDGE,"E1578"),sQuery(id+"F1.wireOp",EDGE,"E1579"),sQuery(id+"F1.wireOp",EDGE,"E1580"),sQuery(id+"F1.wireOp",EDGE,"E1581"),sQuery(id+"F1.wireOp",EDGE,"E1582"),sQuery(id+"F1.wireOp",EDGE,"E1583"),sQuery(id+"F1.wireOp",EDGE,"E1584"),sQuery(id+"F1.wireOp",EDGE,"E1585"),sQuery(id+"F1.wireOp",EDGE,"E1586"),sQuery(id+"F1.wireOp",EDGE,"E1587"),sQuery(id+"F1.wireOp",EDGE,"E1588"),sQuery(id+"F1.wireOp",EDGE,"E1589"),sQuery(id+"F1.wireOp",EDGE,"E1590"),sQuery(id+"F1.wireOp",EDGE,"E1591"),sQuery(id+"F1.wireOp",EDGE,"E1592"),sQuery(id+"F1.wireOp",EDGE,"E1593"),sQuery(id+"F1.wireOp",EDGE,"E1594"),sQuery(id+"F1.wireOp",EDGE,"E1595"),sQuery(id+"F1.wireOp",EDGE,"E1596"),sQuery(id+"F1.wireOp",EDGE,"E1597"),sQuery(id+"F1.wireOp",EDGE,"E1598"),sQuery(id+"F1.wireOp",EDGE,"E1599"),sQuery(id+"F1.wireOp",EDGE,"E1600"),sQuery(id+"F1.wireOp",EDGE,"E1601"),sQuery(id+"F1.wireOp",EDGE,"E1602"),sQuery(id+"F1.wireOp",EDGE,"E1603"),sQuery(id+"F1.wireOp",EDGE,"E1604"),sQuery(id+"F1.wireOp",EDGE,"E1605"),sQuery(id+"F1.wireOp",EDGE,"E1606"),sQuery(id+"F1.wireOp",EDGE,"E1607"),sQuery(id+"F1.wireOp",EDGE,"E1608"),sQuery(id+"F1.wireOp",EDGE,"E1609"),sQuery(id+"F1.wireOp",EDGE,"E1610"),sQuery(id+"F1.wireOp",EDGE,"E1611"),sQuery(id+"F1.wireOp",EDGE,"E1612"),sQuery(id+"F1.wireOp",EDGE,"E1613"),sQuery(id+"F1.wireOp",EDGE,"E1614"),sQuery(id+"F1.wireOp",EDGE,"E1615"),sQuery(id+"F1.wireOp",EDGE,"E1616"),sQuery(id+"F1.wireOp",EDGE,"E1617"),sQuery(id+"F1.wireOp",EDGE,"E1618"),sQuery(id+"F1.wireOp",EDGE,"E1619"),sQuery(id+"F1.wireOp",EDGE,"E1620"),sQuery(id+"F1.wireOp",EDGE,"E1621"),sQuery(id+"F1.wireOp",EDGE,"E1622"),sQuery(id+"F1.wireOp",EDGE,"E1623"),sQuery(id+"F1.wireOp",EDGE,"E1624"),sQuery(id+"F1.wireOp",EDGE,"E1625"),sQuery(id+"F1.wireOp",EDGE,"E1626"),sQuery(id+"F1.wireOp",EDGE,"E1627"),sQuery(id+"F1.wireOp",EDGE,"E1628"),sQuery(id+"F1.wireOp",EDGE,"E1629"),sQuery(id+"F1.wireOp",EDGE,"E1630"),sQuery(id+"F1.wireOp",EDGE,"E1631"),sQuery(id+"F1.wireOp",EDGE,"E1632"),sQuery(id+"F1.wireOp",EDGE,"E1633"),sQuery(id+"F1.wireOp",EDGE,"E1634"),sQuery(id+"F1.wireOp",EDGE,"E1635"),sQuery(id+"F1.wireOp",EDGE,"E1636"),sQuery(id+"F1.wireOp",EDGE,"E1637"),sQuery(id+"F1.wireOp",EDGE,"E1638"),sQuery(id+"F1.wireOp",EDGE,"E1639"),sQuery(id+"F1.wireOp",EDGE,"E1640"),sQuery(id+"F1.wireOp",EDGE,"E1641"),sQuery(id+"F1.wireOp",EDGE,"E1642"),sQuery(id+"F1.wireOp",EDGE,"E1643"),sQuery(id+"F1.wireOp",EDGE,"E1644"),sQuery(id+"F1.wireOp",EDGE,"E1645"),sQuery(id+"F1.wireOp",EDGE,"E1646"),sQuery(id+"F1.wireOp",EDGE,"E1647"),sQuery(id+"F1.wireOp",EDGE,"E1648"),sQuery(id+"F1.wireOp",EDGE,"E1649"),sQuery(id+"F1.wireOp",EDGE,"E1650"),sQuery(id+"F1.wireOp",EDGE,"E1651"),sQuery(id+"F1.wireOp",EDGE,"E1652"),sQuery(id+"F1.wireOp",EDGE,"E1653"),sQuery(id+"F1.wireOp",EDGE,"E1654"),sQuery(id+"F1.wireOp",EDGE,"E1655"),sQuery(id+"F1.wireOp",EDGE,"E1656"),sQuery(id+"F1.wireOp",EDGE,"E1657"),sQuery(id+"F1.wireOp",EDGE,"E1658"),sQuery(id+"F1.wireOp",EDGE,"E1659"),sQuery(id+"F1.wireOp",EDGE,"E1660"),sQuery(id+"F1.wireOp",EDGE,"E1661"),sQuery(id+"F1.wireOp",EDGE,"E1662"),sQuery(id+"F1.wireOp",EDGE,"E1663"),sQuery(id+"F1.wireOp",EDGE,"E1664"),sQuery(id+"F1.wireOp",EDGE,"E1665"),sQuery(id+"F1.wireOp",EDGE,"E1666"),sQuery(id+"F1.wireOp",EDGE,"E1667"),sQuery(id+"F1.wireOp",EDGE,"E1668"),sQuery(id+"F1.wireOp",EDGE,"E1669"),sQuery(id+"F1.wireOp",EDGE,"E1670"),sQuery(id+"F1.wireOp",EDGE,"E1671"),sQuery(id+"F1.wireOp",EDGE,"E1672"),sQuery(id+"F1.wireOp",EDGE,"E1673"),sQuery(id+"F1.wireOp",EDGE,"E1674"),sQuery(id+"F1.wireOp",EDGE,"E1675"),sQuery(id+"F1.wireOp",EDGE,"E1676"),sQuery(id+"F1.wireOp",EDGE,"E1677"),sQuery(id+"F1.wireOp",EDGE,"E1678"),sQuery(id+"F1.wireOp",EDGE,"E1679"),sQuery(id+"F1.wireOp",EDGE,"E1680"),sQuery(id+"F1.wireOp",EDGE,"E1681"),sQuery(id+"F1.wireOp",EDGE,"E1682"),sQuery(id+"F1.wireOp",EDGE,"E1683"),sQuery(id+"F1.wireOp",EDGE,"E1684"),sQuery(id+"F1.wireOp",EDGE,"E1685"),sQuery(id+"F1.wireOp",EDGE,"E1686"),sQuery(id+"F1.wireOp",EDGE,"E1687"),sQuery(id+"F1.wireOp",EDGE,"E1688"),sQuery(id+"F1.wireOp",EDGE,"E1689"),sQuery(id+"F1.wireOp",EDGE,"E1690"),sQuery(id+"F1.wireOp",EDGE,"E1691"),sQuery(id+"F1.wireOp",EDGE,"E1692"),sQuery(id+"F1.wireOp",EDGE,"E1693"),sQuery(id+"F1.wireOp",EDGE,"E1694"),sQuery(id+"F1.wireOp",EDGE,"E1695"),sQuery(id+"F1.wireOp",EDGE,"E1696"),sQuery(id+"F1.wireOp",EDGE,"E1697"),sQuery(id+"F1.wireOp",EDGE,"E1698"),sQuery(id+"F1.wireOp",EDGE,"E1699"),sQuery(id+"F1.wireOp",EDGE,"E1700"),sQuery(id+"F1.wireOp",EDGE,"E1701"),sQuery(id+"F1.wireOp",EDGE,"E1702"),sQuery(id+"F1.wireOp",EDGE,"E1703"),sQuery(id+"F1.wireOp",EDGE,"E1704"),sQuery(id+"F1.wireOp",EDGE,"E1705"),sQuery(id+"F1.wireOp",EDGE,"E1706"),sQuery(id+"F1.wireOp",EDGE,"E1707"),sQuery(id+"F1.wireOp",EDGE,"E1708"),sQuery(id+"F1.wireOp",EDGE,"E1709"),sQuery(id+"F1.wireOp",EDGE,"E1710"),sQuery(id+"F1.wireOp",EDGE,"E1711"),sQuery(id+"F1.wireOp",EDGE,"E1712"),sQuery(id+"F1.wireOp",EDGE,"E1713"),sQuery(id+"F1.wireOp",EDGE,"E1714"),sQuery(id+"F1.wireOp",EDGE,"E1715"),sQuery(id+"F1.wireOp",EDGE,"E1716"),sQuery(id+"F1.wireOp",EDGE,"E1717"),sQuery(id+"F1.wireOp",EDGE,"E1718"),sQuery(id+"F1.wireOp",EDGE,"E1719"),sQuery(id+"F1.wireOp",EDGE,"E1720"),sQuery(id+"F1.wireOp",EDGE,"E1721"),sQuery(id+"F1.wireOp",EDGE,"E1722"),sQuery(id+"F1.wireOp",EDGE,"E1723"),sQuery(id+"F1.wireOp",EDGE,"E1724"),sQuery(id+"F1.wireOp",EDGE,"E1725"),sQuery(id+"F1.wireOp",EDGE,"E1726"),sQuery(id+"F1.wireOp",EDGE,"E1727"),sQuery(id+"F1.wireOp",EDGE,"E1728"),sQuery(id+"F1.wireOp",EDGE,"E1729"),sQuery(id+"F1.wireOp",EDGE,"E1730"),sQuery(id+"F1.wireOp",EDGE,"E1731"),sQuery(id+"F1.wireOp",EDGE,"E1732"),sQuery(id+"F1.wireOp",EDGE,"E1733"),sQuery(id+"F1.wireOp",EDGE,"E1734"),sQuery(id+"F1.wireOp",EDGE,"E1735"),sQuery(id+"F1.wireOp",EDGE,"E1736"),sQuery(id+"F1.wireOp",EDGE,"E1737"),sQuery(id+"F1.wireOp",EDGE,"E1738"),sQuery(id+"F1.wireOp",EDGE,"E1739"),sQuery(id+"F1.wireOp",EDGE,"E1740"),sQuery(id+"F1.wireOp",EDGE,"E1741"),sQuery(id+"F1.wireOp",EDGE,"E1742"),sQuery(id+"F1.wireOp",EDGE,"E1743"),sQuery(id+"F1.wireOp",EDGE,"E1744"),sQuery(id+"F1.wireOp",EDGE,"E1745"),sQuery(id+"F1.wireOp",EDGE,"E1746"),sQuery(id+"F1.wireOp",EDGE,"E1747"),sQuery(id+"F1.wireOp",EDGE,"E1748"),sQuery(id+"F1.wireOp",EDGE,"E1749"),sQuery(id+"F1.wireOp",EDGE,"E1750"),sQuery(id+"F1.wireOp",EDGE,"E1751"),sQuery(id+"F1.wireOp",EDGE,"E1752"),sQuery(id+"F1.wireOp",EDGE,"E1753"),sQuery(id+"F1.wireOp",EDGE,"E1754"),sQuery(id+"F1.wireOp",EDGE,"E1755"),sQuery(id+"F1.wireOp",EDGE,"E1756"),sQuery(id+"F1.wireOp",EDGE,"E1757"),sQuery(id+"F1.wireOp",EDGE,"E1758"),sQuery(id+"F1.wireOp",EDGE,"E1759"),sQuery(id+"F1.wireOp",EDGE,"E1760"),sQuery(id+"F1.wireOp",EDGE,"E1761"),sQuery(id+"F1.wireOp",EDGE,"E1762"),sQuery(id+"F1.wireOp",EDGE,"E1763"),sQuery(id+"F1.wireOp",EDGE,"E1764"),sQuery(id+"F1.wireOp",EDGE,"E1765"),sQuery(id+"F1.wireOp",EDGE,"E1766"),sQuery(id+"F1.wireOp",EDGE,"E1767"),sQuery(id+"F1.wireOp",EDGE,"E1768"),sQuery(id+"F1.wireOp",EDGE,"E1769"),sQuery(id+"F1.wireOp",EDGE,"E1770"),sQuery(id+"F1.wireOp",EDGE,"E1771"),sQuery(id+"F1.wireOp",EDGE,"E1772"),sQuery(id+"F1.wireOp",EDGE,"E1773"),sQuery(id+"F1.wireOp",EDGE,"E1774"),sQuery(id+"F1.wireOp",EDGE,"E1775"),sQuery(id+"F1.wireOp",EDGE,"E1776"),sQuery(id+"F1.wireOp",EDGE,"E1777"),sQuery(id+"F1.wireOp",EDGE,"E1778"),sQuery(id+"F1.wireOp",EDGE,"E1779"),sQuery(id+"F1.wireOp",EDGE,"E1780"),sQuery(id+"F1.wireOp",EDGE,"E1781"),sQuery(id+"F1.wireOp",EDGE,"E1782"),sQuery(id+"F1.wireOp",EDGE,"E1783"),sQuery(id+"F1.wireOp",EDGE,"E1784"),sQuery(id+"F1.wireOp",EDGE,"E1785"),sQuery(id+"F1.wireOp",EDGE,"E1786"),sQuery(id+"F1.wireOp",EDGE,"E1787"),sQuery(id+"F1.wireOp",EDGE,"E1788"),sQuery(id+"F1.wireOp",EDGE,"E1789"),sQuery(id+"F1.wireOp",EDGE,"E1790"),sQuery(id+"F1.wireOp",EDGE,"E1791"),sQuery(id+"F1.wireOp",EDGE,"E1792"),sQuery(id+"F1.wireOp",EDGE,"E1793"),sQuery(id+"F1.wireOp",EDGE,"E1794"),sQuery(id+"F1.wireOp",EDGE,"E1795"),sQuery(id+"F1.wireOp",EDGE,"E1796"),sQuery(id+"F1.wireOp",EDGE,"E1797"),sQuery(id+"F1.wireOp",EDGE,"E1798"),sQuery(id+"F1.wireOp",EDGE,"E1799"),sQuery(id+"F1.wireOp",EDGE,"E1800"),sQuery(id+"F1.wireOp",EDGE,"E1801"),sQuery(id+"F1.wireOp",EDGE,"E1802"),sQuery(id+"F1.wireOp",EDGE,"E1803"),sQuery(id+"F1.wireOp",EDGE,"E1804"),sQuery(id+"F1.wireOp",EDGE,"E1805"),sQuery(id+"F1.wireOp",EDGE,"E1806"),sQuery(id+"F1.wireOp",EDGE,"E1807"),sQuery(id+"F1.wireOp",EDGE,"E1808"),sQuery(id+"F1.wireOp",EDGE,"E1809"),sQuery(id+"F1.wireOp",EDGE,"E1810"),sQuery(id+"F1.wireOp",EDGE,"E1811"),sQuery(id+"F1.wireOp",EDGE,"E1812"),sQuery(id+"F1.wireOp",EDGE,"E1813"),sQuery(id+"F1.wireOp",EDGE,"E1814"),sQuery(id+"F1.wireOp",EDGE,"E1815"),sQuery(id+"F1.wireOp",EDGE,"E1816"),sQuery(id+"F1.wireOp",EDGE,"E1817"),sQuery(id+"F1.wireOp",EDGE,"E1818"),sQuery(id+"F1.wireOp",EDGE,"E1819"),sQuery(id+"F1.wireOp",EDGE,"E1820"),sQuery(id+"F1.wireOp",EDGE,"E1821"),sQuery(id+"F1.wireOp",EDGE,"E1822"),sQuery(id+"F1.wireOp",EDGE,"E1823"),sQuery(id+"F1.wireOp",EDGE,"E1824"),sQuery(id+"F1.wireOp",EDGE,"E1825"),sQuery(id+"F1.wireOp",EDGE,"E1826"),sQuery(id+"F1.wireOp",EDGE,"E1827"),sQuery(id+"F1.wireOp",EDGE,"E1828"),sQuery(id+"F1.wireOp",EDGE,"E1829"),sQuery(id+"F1.wireOp",EDGE,"E1830"),sQuery(id+"F1.wireOp",EDGE,"E1831"),sQuery(id+"F1.wireOp",EDGE,"E1832"),sQuery(id+"F1.wireOp",EDGE,"E1833"),sQuery(id+"F1.wireOp",EDGE,"E1834"),sQuery(id+"F1.wireOp",EDGE,"E1835"),sQuery(id+"F1.wireOp",EDGE,"E1836"),sQuery(id+"F1.wireOp",EDGE,"E1837"),sQuery(id+"F1.wireOp",EDGE,"E1838"),sQuery(id+"F1.wireOp",EDGE,"E1839"),sQuery(id+"F1.wireOp",EDGE,"E1840"),sQuery(id+"F1.wireOp",EDGE,"E1841"),sQuery(id+"F1.wireOp",EDGE,"E1842"),sQuery(id+"F1.wireOp",EDGE,"E1843"),sQuery(id+"F1.wireOp",EDGE,"E1844"),sQuery(id+"F1.wireOp",EDGE,"E1845"),sQuery(id+"F1.wireOp",EDGE,"E1846"),sQuery(id+"F1.wireOp",EDGE,"E1847"),sQuery(id+"F1.wireOp",EDGE,"E1848"),sQuery(id+"F1.wireOp",EDGE,"E1849"),sQuery(id+"F1.wireOp",EDGE,"E1850"),sQuery(id+"F1.wireOp",EDGE,"E1851"),sQuery(id+"F1.wireOp",EDGE,"E1852"),sQuery(id+"F1.wireOp",EDGE,"E1853"),sQuery(id+"F1.wireOp",EDGE,"E1854"),sQuery(id+"F1.wireOp",EDGE,"E1855"),sQuery(id+"F1.wireOp",EDGE,"E1856"),sQuery(id+"F1.wireOp",EDGE,"E1857"),sQuery(id+"F1.wireOp",EDGE,"E1858"),sQuery(id+"F1.wireOp",EDGE,"E1859"),sQuery(id+"F1.wireOp",EDGE,"E1860"),sQuery(id+"F1.wireOp",EDGE,"E1861"),sQuery(id+"F1.wireOp",EDGE,"E1862"),sQuery(id+"F1.wireOp",EDGE,"E1863"),sQuery(id+"F1.wireOp",EDGE,"E1864"),sQuery(id+"F1.wireOp",EDGE,"E1865"),sQuery(id+"F1.wireOp",EDGE,"E1866"),sQuery(id+"F1.wireOp",EDGE,"E1867"),sQuery(id+"F1.wireOp",EDGE,"E1868"),sQuery(id+"F1.wireOp",EDGE,"E1869"),sQuery(id+"F1.wireOp",EDGE,"E1870"),sQuery(id+"F1.wireOp",EDGE,"E1871"),sQuery(id+"F1.wireOp",EDGE,"E1872"),sQuery(id+"F1.wireOp",EDGE,"E1873"),sQuery(id+"F1.wireOp",EDGE,"E1874"),sQuery(id+"F1.wireOp",EDGE,"E1875"),sQuery(id+"F1.wireOp",EDGE,"E1876"),sQuery(id+"F1.wireOp",EDGE,"E1877"),sQuery(id+"F1.wireOp",EDGE,"E1878"),sQuery(id+"F1.wireOp",EDGE,"E1879"),sQuery(id+"F1.wireOp",EDGE,"E1880"),sQuery(id+"F1.wireOp",EDGE,"E1881"),sQuery(id+"F1.wireOp",EDGE,"E1882"),sQuery(id+"F1.wireOp",EDGE,"E1883"),sQuery(id+"F1.wireOp",EDGE,"E1884"),sQuery(id+"F1.wireOp",EDGE,"E1885"),sQuery(id+"F1.wireOp",EDGE,"E1886"),sQuery(id+"F1.wireOp",EDGE,"E1887"),sQuery(id+"F1.wireOp",EDGE,"E1888"),sQuery(id+"F1.wireOp",EDGE,"E1889"),sQuery(id+"F1.wireOp",EDGE,"E1890"),sQuery(id+"F1.wireOp",EDGE,"E1891"),sQuery(id+"F1.wireOp",EDGE,"E1892"),sQuery(id+"F1.wireOp",EDGE,"E1893"),sQuery(id+"F1.wireOp",EDGE,"E1894"),sQuery(id+"F1.wireOp",EDGE,"E1895"),sQuery(id+"F1.wireOp",EDGE,"E1896"),sQuery(id+"F1.wireOp",EDGE,"E1897"),sQuery(id+"F1.wireOp",EDGE,"E1898"),sQuery(id+"F1.wireOp",EDGE,"E1899"),sQuery(id+"F1.wireOp",EDGE,"E1900"),sQuery(id+"F1.wireOp",EDGE,"E1901"),sQuery(id+"F1.wireOp",EDGE,"E1902"),sQuery(id+"F1.wireOp",EDGE,"E1903"),sQuery(id+"F1.wireOp",EDGE,"E1904"),sQuery(id+"F1.wireOp",EDGE,"E1905"),sQuery(id+"F1.wireOp",EDGE,"E1906"),sQuery(id+"F1.wireOp",EDGE,"E1907"),sQuery(id+"F1.wireOp",EDGE,"E1908"),sQuery(id+"F1.wireOp",EDGE,"E1909"),sQuery(id+"F1.wireOp",EDGE,"E1910"),sQuery(id+"F1.wireOp",EDGE,"E1911"),sQuery(id+"F1.wireOp",EDGE,"E1912"),sQuery(id+"F1.wireOp",EDGE,"E1913"),sQuery(id+"F1.wireOp",EDGE,"E1914"),sQuery(id+"F1.wireOp",EDGE,"E1915"),sQuery(id+"F1.wireOp",EDGE,"E1916"),sQuery(id+"F1.wireOp",EDGE,"E1917"),sQuery(id+"F1.wireOp",EDGE,"E1918"),sQuery(id+"F1.wireOp",EDGE,"E1919"),sQuery(id+"F1.wireOp",EDGE,"E1920"),sQuery(id+"F1.wireOp",EDGE,"E1921"),sQuery(id+"F1.wireOp",EDGE,"E1922"),sQuery(id+"F1.wireOp",EDGE,"E1923"),sQuery(id+"F1.wireOp",EDGE,"E1924"),sQuery(id+"F1.wireOp",EDGE,"E1925"),sQuery(id+"F1.wireOp",EDGE,"E1926"),sQuery(id+"F1.wireOp",EDGE,"E1927"),sQuery(id+"F1.wireOp",EDGE,"E1928"),sQuery(id+"F1.wireOp",EDGE,"E1929"),sQuery(id+"F1.wireOp",EDGE,"E1930"),sQuery(id+"F1.wireOp",EDGE,"E1931"),sQuery(id+"F1.wireOp",EDGE,"E1932"),sQuery(id+"F1.wireOp",EDGE,"E1933"),sQuery(id+"F1.wireOp",EDGE,"E1934"),sQuery(id+"F1.wireOp",EDGE,"E1935"),sQuery(id+"F1.wireOp",EDGE,"E1936"),sQuery(id+"F1.wireOp",EDGE,"E1937"),sQuery(id+"F1.wireOp",EDGE,"E1938"),sQuery(id+"F1.wireOp",EDGE,"E1939"),sQuery(id+"F1.wireOp",EDGE,"E1940"),sQuery(id+"F1.wireOp",EDGE,"E1941"),sQuery(id+"F1.wireOp",EDGE,"E1942"),sQuery(id+"F1.wireOp",EDGE,"E1943"),sQuery(id+"F1.wireOp",EDGE,"E1944"),sQuery(id+"F1.wireOp",EDGE,"E1945"),sQuery(id+"F1.wireOp",EDGE,"E1946"),sQuery(id+"F1.wireOp",EDGE,"E1947"),sQuery(id+"F1.wireOp",EDGE,"E1948"),sQuery(id+"F1.wireOp",EDGE,"E1949"),sQuery(id+"F1.wireOp",EDGE,"E1950"),sQuery(id+"F1.wireOp",EDGE,"E1951"),sQuery(id+"F1.wireOp",EDGE,"E1952"),sQuery(id+"F1.wireOp",EDGE,"E1953"),sQuery(id+"F1.wireOp",EDGE,"E1954"),sQuery(id+"F1.wireOp",EDGE,"E1955"),sQuery(id+"F1.wireOp",EDGE,"E1956"),sQuery(id+"F1.wireOp",EDGE,"E1957"),sQuery(id+"F1.wireOp",EDGE,"E1958"),sQuery(id+"F1.wireOp",EDGE,"E1959"),sQuery(id+"F1.wireOp",EDGE,"E1960"),sQuery(id+"F1.wireOp",EDGE,"E1961"),sQuery(id+"F1.wireOp",EDGE,"E1962"),sQuery(id+"F1.wireOp",EDGE,"E1963"),sQuery(id+"F1.wireOp",EDGE,"E1964"),sQuery(id+"F1.wireOp",EDGE,"E1965"),sQuery(id+"F1.wireOp",EDGE,"E1966"),sQuery(id+"F1.wireOp",EDGE,"E1967"),sQuery(id+"F1.wireOp",EDGE,"E1968"),sQuery(id+"F1.wireOp",EDGE,"E1969"),sQuery(id+"F1.wireOp",EDGE,"E1970"),sQuery(id+"F1.wireOp",EDGE,"E1971"),sQuery(id+"F1.wireOp",EDGE,"E1972"),sQuery(id+"F1.wireOp",EDGE,"E1973"),sQuery(id+"F1.wireOp",EDGE,"E1974"),sQuery(id+"F1.wireOp",EDGE,"E1975"),sQuery(id+"F1.wireOp",EDGE,"E1976"),sQuery(id+"F1.wireOp",EDGE,"E1977"),sQuery(id+"F1.wireOp",EDGE,"E1978"),sQuery(id+"F1.wireOp",EDGE,"E1979"),sQuery(id+"F1.wireOp",EDGE,"E1980"),sQuery(id+"F1.wireOp",EDGE,"E1981"),sQuery(id+"F1.wireOp",EDGE,"E1982"),sQuery(id+"F1.wireOp",EDGE,"E1983"),sQuery(id+"F1.wireOp",EDGE,"E1984"),sQuery(id+"F1.wireOp",EDGE,"E1985"),sQuery(id+"F1.wireOp",EDGE,"E1986"),sQuery(id+"F1.wireOp",EDGE,"E1987"),sQuery(id+"F1.wireOp",EDGE,"E1988"),sQuery(id+"F1.wireOp",EDGE,"E1989"),sQuery(id+"F1.wireOp",EDGE,"E1990"),sQuery(id+"F1.wireOp",EDGE,"E1991"),sQuery(id+"F1.wireOp",EDGE,"E1992"),sQuery(id+"F1.wireOp",EDGE,"E1993"),sQuery(id+"F1.wireOp",EDGE,"E1994"),sQuery(id+"F1.wireOp",EDGE,"E1995"),sQuery(id+"F1.wireOp",EDGE,"E1996"),sQuery(id+"F1.wireOp",EDGE,"E1997"),sQuery(id+"F1.wireOp",EDGE,"E1998"),sQuery(id+"F1.wireOp",EDGE,"E1999"),sQuery(id+"F1.wireOp",EDGE,"E2000"),sQuery(id+"F1.wireOp",EDGE,"E2001"),sQuery(id+"F1.wireOp",EDGE,"E2002"),sQuery(id+"F1.wireOp",EDGE,"E2003"),sQuery(id+"F1.wireOp",EDGE,"E2004"),sQuery(id+"F1.wireOp",EDGE,"E2005"),sQuery(id+"F1.wireOp",EDGE,"E2006"),sQuery(id+"F1.wireOp",EDGE,"E2007"),sQuery(id+"F1.wireOp",EDGE,"E2008"),sQuery(id+"F1.wireOp",EDGE,"E2009"),sQuery(id+"F1.wireOp",EDGE,"E2010"),sQuery(id+"F1.wireOp",EDGE,"E2011"),sQuery(id+"F1.wireOp",EDGE,"E2012"),sQuery(id+"F1.wireOp",EDGE,"E2013"),sQuery(id+"F1.wireOp",EDGE,"E2014"),sQuery(id+"F1.wireOp",EDGE,"E2015"),sQuery(id+"F1.wireOp",EDGE,"E2016"),sQuery(id+"F1.wireOp",EDGE,"E2017"),sQuery(id+"F1.wireOp",EDGE,"E2018"),sQuery(id+"F1.wireOp",EDGE,"E2019"),sQuery(id+"F1.wireOp",EDGE,"E2020"),sQuery(id+"F1.wireOp",EDGE,"E2021"),sQuery(id+"F1.wireOp",EDGE,"E2022"),sQuery(id+"F1.wireOp",EDGE,"E2023"),sQuery(id+"F1.wireOp",EDGE,"E2024"),sQuery(id+"F1.wireOp",EDGE,"E2025"),sQuery(id+"F1.wireOp",EDGE,"E2026"),sQuery(id+"F1.wireOp",EDGE,"E2027"),sQuery(id+"F1.wireOp",EDGE,"E2028"),sQuery(id+"F1.wireOp",EDGE,"E2029"),sQuery(id+"F1.wireOp",EDGE,"E2030"),sQuery(id+"F1.wireOp",EDGE,"E2031"),sQuery(id+"F1.wireOp",EDGE,"E2032"),sQuery(id+"F1.wireOp",EDGE,"E2033"),sQuery(id+"F1.wireOp",EDGE,"E2034"),sQuery(id+"F1.wireOp",EDGE,"E2035"),sQuery(id+"F1.wireOp",EDGE,"E2036"),sQuery(id+"F1.wireOp",EDGE,"E2037"),sQuery(id+"F1.wireOp",EDGE,"E2038"),sQuery(id+"F1.wireOp",EDGE,"E2039"),sQuery(id+"F1.wireOp",EDGE,"E2040"),sQuery(id+"F1.wireOp",EDGE,"E2041"),sQuery(id+"F1.wireOp",EDGE,"E2042"),sQuery(id+"F1.wireOp",EDGE,"E2043"),sQuery(id+"F1.wireOp",EDGE,"E2044"),sQuery(id+"F1.wireOp",EDGE,"E2045"),sQuery(id+"F1.wireOp",EDGE,"E2046"),sQuery(id+"F1.wireOp",EDGE,"E2047"),sQuery(id+"F1.wireOp",EDGE,"E2048"),sQuery(id+"F1.wireOp",EDGE,"E2049"),sQuery(id+"F1.wireOp",EDGE,"E2050"),sQuery(id+"F1.wireOp",EDGE,"E2051"),sQuery(id+"F1.wireOp",EDGE,"E2052"),sQuery(id+"F1.wireOp",EDGE,"E2053"),sQuery(id+"F1.wireOp",EDGE,"E2054"),sQuery(id+"F1.wireOp",EDGE,"E2055"),sQuery(id+"F1.wireOp",EDGE,"E2056"),sQuery(id+"F1.wireOp",EDGE,"E2057"),sQuery(id+"F1.wireOp",EDGE,"E2058"),sQuery(id+"F1.wireOp",EDGE,"E2059"),sQuery(id+"F1.wireOp",EDGE,"E2060"),sQuery(id+"F1.wireOp",EDGE,"E2061"),sQuery(id+"F1.wireOp",EDGE,"E2062"),sQuery(id+"F1.wireOp",EDGE,"E2063"),sQuery(id+"F1.wireOp",EDGE,"E2064"),sQuery(id+"F1.wireOp",EDGE,"E2065"),sQuery(id+"F1.wireOp",EDGE,"E2066"),sQuery(id+"F1.wireOp",EDGE,"E2067"),sQuery(id+"F1.wireOp",EDGE,"E2068"),sQuery(id+"F1.wireOp",EDGE,"E2069"),sQuery(id+"F1.wireOp",EDGE,"E2070"),sQuery(id+"F1.wireOp",EDGE,"E2071"),sQuery(id+"F1.wireOp",EDGE,"E2072"),sQuery(id+"F1.wireOp",EDGE,"E2073"),sQuery(id+"F1.wireOp",EDGE,"E2074"),sQuery(id+"F1.wireOp",EDGE,"E2075"),sQuery(id+"F1.wireOp",EDGE,"E2076"),sQuery(id+"F1.wireOp",EDGE,"E2077"),sQuery(id+"F1.wireOp",EDGE,"E2078"),sQuery(id+"F1.wireOp",EDGE,"E2079"),sQuery(id+"F1.wireOp",EDGE,"E2080"),sQuery(id+"F1.wireOp",EDGE,"E2081"),sQuery(id+"F1.wireOp",EDGE,"E2082"),sQuery(id+"F1.wireOp",EDGE,"E2083"),sQuery(id+"F1.wireOp",EDGE,"E2084"),sQuery(id+"F1.wireOp",EDGE,"E2085"),sQuery(id+"F1.wireOp",EDGE,"E2086"),sQuery(id+"F1.wireOp",EDGE,"E2087"),sQuery(id+"F1.wireOp",EDGE,"E2088"),sQuery(id+"F1.wireOp",EDGE,"E2089"),sQuery(id+"F1.wireOp",EDGE,"E2090"),sQuery(id+"F1.wireOp",EDGE,"E2091"),sQuery(id+"F1.wireOp",EDGE,"E2092"),sQuery(id+"F1.wireOp",EDGE,"E2093"),sQuery(id+"F1.wireOp",EDGE,"E2094"),sQuery(id+"F1.wireOp",EDGE,"E2095"),sQuery(id+"F1.wireOp",EDGE,"E2096"),sQuery(id+"F1.wireOp",EDGE,"E2097"),sQuery(id+"F1.wireOp",EDGE,"E2098"),sQuery(id+"F1.wireOp",EDGE,"E2099"),sQuery(id+"F1.wireOp",EDGE,"E2100"),sQuery(id+"F1.wireOp",EDGE,"E2101"),sQuery(id+"F1.wireOp",EDGE,"E2102"),sQuery(id+"F1.wireOp",EDGE,"E2103"),sQuery(id+"F1.wireOp",EDGE,"E2104"),sQuery(id+"F1.wireOp",EDGE,"E2105"),sQuery(id+"F1.wireOp",EDGE,"E2106"),sQuery(id+"F1.wireOp",EDGE,"E2107"),sQuery(id+"F1.wireOp",EDGE,"E2108"),sQuery(id+"F1.wireOp",EDGE,"E2109"),sQuery(id+"F1.wireOp",EDGE,"E2110"),sQuery(id+"F1.wireOp",EDGE,"E2111"),sQuery(id+"F1.wireOp",EDGE,"E2112"),sQuery(id+"F1.wireOp",EDGE,"E2113"),sQuery(id+"F1.wireOp",EDGE,"E2114"),sQuery(id+"F1.wireOp",EDGE,"E2115"),sQuery(id+"F1.wireOp",EDGE,"E2116"),sQuery(id+"F1.wireOp",EDGE,"E2117"),sQuery(id+"F1.wireOp",EDGE,"E2118"),sQuery(id+"F1.wireOp",EDGE,"E2119"),sQuery(id+"F1.wireOp",EDGE,"E2120"),sQuery(id+"F1.wireOp",EDGE,"E2121"),sQuery(id+"F1.wireOp",EDGE,"E2122"),sQuery(id+"F1.wireOp",EDGE,"E2123"),sQuery(id+"F1.wireOp",EDGE,"E2124"),sQuery(id+"F1.wireOp",EDGE,"E2125"),sQuery(id+"F1.wireOp",EDGE,"E2126"),sQuery(id+"F1.wireOp",EDGE,"E2127"),sQuery(id+"F1.wireOp",EDGE,"E2128"),sQuery(id+"F1.wireOp",EDGE,"E2129"),sQuery(id+"F1.wireOp",EDGE,"E2130"),sQuery(id+"F1.wireOp",EDGE,"E2131"),sQuery(id+"F1.wireOp",EDGE,"E2132"),sQuery(id+"F1.wireOp",EDGE,"E2133"),sQuery(id+"F1.wireOp",EDGE,"E2134"),sQuery(id+"F1.wireOp",EDGE,"E2135"),sQuery(id+"F1.wireOp",EDGE,"E2136"),sQuery(id+"F1.wireOp",EDGE,"E2137"),sQuery(id+"F1.wireOp",EDGE,"E2138"),sQuery(id+"F1.wireOp",EDGE,"E2139"),sQuery(id+"F1.wireOp",EDGE,"E2140"),sQuery(id+"F1.wireOp",EDGE,"E2141"),sQuery(id+"F1.wireOp",EDGE,"E2142"),sQuery(id+"F1.wireOp",EDGE,"E2143"),sQuery(id+"F1.wireOp",EDGE,"E2144"),sQuery(id+"F1.wireOp",EDGE,"E2145"),sQuery(id+"F1.wireOp",EDGE,"E2146"),sQuery(id+"F1.wireOp",EDGE,"E2147"),sQuery(id+"F1.wireOp",EDGE,"E2148"),sQuery(id+"F1.wireOp",EDGE,"E2149"),sQuery(id+"F1.wireOp",EDGE,"E2150"),sQuery(id+"F1.wireOp",EDGE,"E2151"),sQuery(id+"F1.wireOp",EDGE,"E2152"),sQuery(id+"F1.wireOp",EDGE,"E2153"),sQuery(id+"F1.wireOp",EDGE,"E2154"),sQuery(id+"F1.wireOp",EDGE,"E2155"),sQuery(id+"F1.wireOp",EDGE,"E2156"),sQuery(id+"F1.wireOp",EDGE,"E2157"),sQuery(id+"F1.wireOp",EDGE,"E2158"),sQuery(id+"F1.wireOp",EDGE,"E2159"),sQuery(id+"F1.wireOp",EDGE,"E2160"),sQuery(id+"F1.wireOp",EDGE,"E2161"),sQuery(id+"F1.wireOp",EDGE,"E2162"),sQuery(id+"F1.wireOp",EDGE,"E2163"),sQuery(id+"F1.wireOp",EDGE,"E2164"),sQuery(id+"F1.wireOp",EDGE,"E2165"),sQuery(id+"F1.wireOp",EDGE,"E2166"),sQuery(id+"F1.wireOp",EDGE,"E2167"),sQuery(id+"F1.wireOp",EDGE,"E2168"),sQuery(id+"F1.wireOp",EDGE,"E2169"),sQuery(id+"F1.wireOp",EDGE,"E2170"),sQuery(id+"F1.wireOp",EDGE,"E2171"),sQuery(id+"F1.wireOp",EDGE,"E2172"),sQuery(id+"F1.wireOp",EDGE,"E2173"),sQuery(id+"F1.wireOp",EDGE,"E2174"),sQuery(id+"F1.wireOp",EDGE,"E2175"),sQuery(id+"F1.wireOp",EDGE,"E2176"),sQuery(id+"F1.wireOp",EDGE,"E2177"),sQuery(id+"F1.wireOp",EDGE,"E2178"),sQuery(id+"F1.wireOp",EDGE,"E2179"),sQuery(id+"F1.wireOp",EDGE,"E2180"),sQuery(id+"F1.wireOp",EDGE,"E2181"),sQuery(id+"F1.wireOp",EDGE,"E2182"),sQuery(id+"F1.wireOp",EDGE,"E2183"),sQuery(id+"F1.wireOp",EDGE,"E2184"),sQuery(id+"F1.wireOp",EDGE,"E2185"),sQuery(id+"F1.wireOp",EDGE,"E2186"),sQuery(id+"F1.wireOp",EDGE,"E2187"),sQuery(id+"F1.wireOp",EDGE,"E2188"),sQuery(id+"F1.wireOp",EDGE,"E2189"),sQuery(id+"F1.wireOp",EDGE,"E2190"),sQuery(id+"F1.wireOp",EDGE,"E2191"),sQuery(id+"F1.wireOp",EDGE,"E2192"),sQuery(id+"F1.wireOp",EDGE,"E2193"),sQuery(id+"F1.wireOp",EDGE,"E2194"),sQuery(id+"F1.wireOp",EDGE,"E2195"),sQuery(id+"F1.wireOp",EDGE,"E2196"),sQuery(id+"F1.wireOp",EDGE,"E2197"),sQuery(id+"F1.wireOp",EDGE,"E2198"),sQuery(id+"F1.wireOp",EDGE,"E2199"),sQuery(id+"F1.wireOp",EDGE,"E2200"),sQuery(id+"F1.wireOp",EDGE,"E2201"),sQuery(id+"F1.wireOp",EDGE,"E2202"),sQuery(id+"F1.wireOp",EDGE,"E2203"),sQuery(id+"F1.wireOp",EDGE,"E2204"),sQuery(id+"F1.wireOp",EDGE,"E2205"),sQuery(id+"F1.wireOp",EDGE,"E2206"),sQuery(id+"F1.wireOp",EDGE,"E2207"),sQuery(id+"F1.wireOp",EDGE,"E2208"),sQuery(id+"F1.wireOp",EDGE,"E2209"),sQuery(id+"F1.wireOp",EDGE,"E2210"),sQuery(id+"F1.wireOp",EDGE,"E2211"),sQuery(id+"F1.wireOp",EDGE,"E2212"),sQuery(id+"F1.wireOp",EDGE,"E2213"),sQuery(id+"F1.wireOp",EDGE,"E2214"),sQuery(id+"F1.wireOp",EDGE,"E2215"),sQuery(id+"F1.wireOp",EDGE,"E2216"),sQuery(id+"F1.wireOp",EDGE,"E2217"),sQuery(id+"F1.wireOp",EDGE,"E2218"),sQuery(id+"F1.wireOp",EDGE,"E2219"),sQuery(id+"F1.wireOp",EDGE,"E2220"),sQuery(id+"F1.wireOp",EDGE,"E2221"),sQuery(id+"F1.wireOp",EDGE,"E2222"),sQuery(id+"F1.wireOp",EDGE,"E2223"),sQuery(id+"F1.wireOp",EDGE,"E2224"),sQuery(id+"F1.wireOp",EDGE,"E2225"),sQuery(id+"F1.wireOp",EDGE,"E2226"),sQuery(id+"F1.wireOp",EDGE,"E2227"),sQuery(id+"F1.wireOp",EDGE,"E2228"),sQuery(id+"F1.wireOp",EDGE,"E2229"),sQuery(id+"F1.wireOp",EDGE,"E2230"),sQuery(id+"F1.wireOp",EDGE,"E2231"),sQuery(id+"F1.wireOp",EDGE,"E2232"),sQuery(id+"F1.wireOp",EDGE,"E2233"),sQuery(id+"F1.wireOp",EDGE,"E2234"),sQuery(id+"F1.wireOp",EDGE,"E2235"),sQuery(id+"F1.wireOp",EDGE,"E2236"),sQuery(id+"F1.wireOp",EDGE,"E2237"),sQuery(id+"F1.wireOp",EDGE,"E2238"),sQuery(id+"F1.wireOp",EDGE,"E2239"),sQuery(id+"F1.wireOp",EDGE,"E2240"),sQuery(id+"F1.wireOp",EDGE,"E2241"),sQuery(id+"F1.wireOp",EDGE,"E2242"),sQuery(id+"F1.wireOp",EDGE,"E2243"),sQuery(id+"F1.wireOp",EDGE,"E2244"),sQuery(id+"F1.wireOp",EDGE,"E2245"),sQuery(id+"F1.wireOp",EDGE,"E2246"),sQuery(id+"F1.wireOp",EDGE,"E2247")])],"isStart":true}),makeQuery(id+"F4.opExtrude","CAP_FACE",FACE,{"disambiguationData":[OSD([sQuery(id+"F3.wireOp",EDGE,"E2248.bottom"),sQuery(id+"F3.wireOp",EDGE,"E2248.top"),sQuery(id+"F3.wireOp",EDGE,"E2248.left"),sQuery(id+"F3.wireOp",EDGE,"E2248.right"),sQuery(id+"F3.wireOp",EDGE,"E2249.bottom"),sQuery(id+"F3.wireOp",EDGE,"E2249.top"),sQuery(id+"F3.wireOp",EDGE,"E2249.left"),sQuery(id+"F3.wireOp",EDGE,"E2249.right")])],"isStart":false})]});
            var sketch = newSketch(context, id + "F5", { "sketchPlane" : qUnion([Q0])});
            skLineSegment(sketch, "E2250.bottom", {"start": v(-155, 60) * mm, "end": v(155, 60) * mm});
            skLineSegment(sketch, "E2250.top", {"start": v(-155, -60) * mm, "end": v(155, -60) * mm});
            skLineSegment(sketch, "E2250.left", {"start": v(-155, 60) * mm, "end": v(-155, -60) * mm});
            skLineSegment(sketch, "E2250.right", {"start": v(155, 60) * mm, "end": v(155, -60) * mm});
            skLineSegment(sketch, "E2251.bottom", {"start": v(-145, 50) * mm, "end": v(145, 50) * mm});
            skLineSegment(sketch, "E2251.top", {"start": v(-145, -50) * mm, "end": v(145, -50) * mm});
            skLineSegment(sketch, "E2251.left", {"start": v(-145, 50) * mm, "end": v(-145, -50) * mm});
            skLineSegment(sketch, "E2251.right", {"start": v(145, 50) * mm, "end": v(145, -50) * mm});
            skLineSegment(sketch, "E2252", {"start": v(0, 60) * mm, "end": v(0, -60) * mm, "construction": true});
            skLineSegment(sketch, "E2253", {"start": v(-155, 0) * mm, "end": v(155, 0) * mm, "construction": true});
            skSolve(sketch);
        }
        {
            var Q0;
            Q0 = qSketchRegion(id + "F5", true);
            extrude(context, id + "F6", {"entities" : qUnion([Q0]), "depth" : 15 * mm});
        }
        {
            var Q0;
            Q0=makeQuery(id+"F6.opExtrude","CAP_FACE",FACE,{"disambiguationData":[OSD([sQuery(id+"F5.wireOp",EDGE,"E2250.bottom"),sQuery(id+"F5.wireOp",EDGE,"E2250.top"),sQuery(id+"F5.wireOp",EDGE,"E2250.left"),sQuery(id+"F5.wireOp",EDGE,"E2250.right"),sQuery(id+"F5.wireOp",EDGE,"E2251.bottom"),sQuery(id+"F5.wireOp",EDGE,"E2251.top"),sQuery(id+"F5.wireOp",EDGE,"E2251.left"),sQuery(id+"F5.wireOp",EDGE,"E2251.right")])],"isStart":false});
            var sketch = newSketch(context, id + "F7", { "sketchPlane" : qUnion([Q0])});
            skLineSegment(sketch, "E2254.bottom", {"start": v(-5, -60) * mm, "end": v(5, -60) * mm});
            skLineSegment(sketch, "E2254.top", {"start": v(-5, -50) * mm, "end": v(5, -50) * mm});
            skLineSegment(sketch, "E2254.left", {"start": v(-5, -60) * mm, "end": v(-5, -50) * mm});
            skLineSegment(sketch, "E2254.right", {"start": v(5, -60) * mm, "end": v(5, -50) * mm});
            skLineSegment(sketch, "E2255.bottom", {"start": v(-155, -4.95) * mm, "end": v(155, -4.95) * mm});
            skLineSegment(sketch, "E2255.top", {"start": v(-155, -5.05) * mm, "end": v(155, -5.05) * mm});
            skLineSegment(sketch, "E2255.left", {"start": v(-155, -4.95) * mm, "end": v(-155, -5.05) * mm});
            skLineSegment(sketch, "E2255.right", {"start": v(155, -4.95) * mm, "end": v(155, -5.05) * mm});
            skLineSegment(sketch, "E2256", {"start": v(-155, -5) * mm, "end": v(155, -5) * mm, "construction": true});
            skLineSegment(sketch, "E2257.bottom", {"start": v(-0.05, 62.7) * mm, "end": v(0.05, 62.7) * mm});
            skLineSegment(sketch, "E2257.top", {"start": v(-0.05, 46.25) * mm, "end": v(0.05, 46.25) * mm});
            skLineSegment(sketch, "E2257.left", {"start": v(-0.05, 62.7) * mm, "end": v(-0.05, 46.25) * mm});
            skLineSegment(sketch, "E2257.right", {"start": v(0.05, 62.7) * mm, "end": v(0.05, 46.25) * mm});
            skLineSegment(sketch, "E2258", {"start": v(0, 62.7) * mm, "end": v(0, 46.25) * mm, "construction": true});
            skSolve(sketch);
        }
        {
            var Q0;
            Q0 = qSketchRegion(id + "F7", true);
            var Q1;
            Q1=makeQuery(id+"F4.boolean.opBoolean","MERGE",FACE,{"derivedFrom":[makeQuery(id+"F2.opExtrude","CAP_FACE",FACE,{"disambiguationData":[OSD([sQuery(id+"F1.wireOp",EDGE,"E1352"),sQuery(id+"F1.wireOp",EDGE,"E1353"),sQuery(id+"F1.wireOp",EDGE,"E1354"),sQuery(id+"F1.wireOp",EDGE,"E1355"),sQuery(id+"F1.wireOp",EDGE,"E1356"),sQuery(id+"F1.wireOp",EDGE,"E1357"),sQuery(id+"F1.wireOp",EDGE,"E1358"),sQuery(id+"F1.wireOp",EDGE,"E1359"),sQuery(id+"F1.wireOp",EDGE,"E1360"),sQuery(id+"F1.wireOp",EDGE,"E1361"),sQuery(id+"F1.wireOp",EDGE,"E1362"),sQuery(id+"F1.wireOp",EDGE,"E1363"),sQuery(id+"F1.wireOp",EDGE,"E1364"),sQuery(id+"F1.wireOp",EDGE,"E1365"),sQuery(id+"F1.wireOp",EDGE,"E1366"),sQuery(id+"F1.wireOp",EDGE,"E1367"),sQuery(id+"F1.wireOp",EDGE,"E1368"),sQuery(id+"F1.wireOp",EDGE,"E1369"),sQuery(id+"F1.wireOp",EDGE,"E1370"),sQuery(id+"F1.wireOp",EDGE,"E1371"),sQuery(id+"F1.wireOp",EDGE,"E1372"),sQuery(id+"F1.wireOp",EDGE,"E1373"),sQuery(id+"F1.wireOp",EDGE,"E1374"),sQuery(id+"F1.wireOp",EDGE,"E1375"),sQuery(id+"F1.wireOp",EDGE,"E1376"),sQuery(id+"F1.wireOp",EDGE,"E1377"),sQuery(id+"F1.wireOp",EDGE,"E1378"),sQuery(id+"F1.wireOp",EDGE,"E1379"),sQuery(id+"F1.wireOp",EDGE,"E1380"),sQuery(id+"F1.wireOp",EDGE,"E1381"),sQuery(id+"F1.wireOp",EDGE,"E1382"),sQuery(id+"F1.wireOp",EDGE,"E1383"),sQuery(id+"F1.wireOp",EDGE,"E1384"),sQuery(id+"F1.wireOp",EDGE,"E1385"),sQuery(id+"F1.wireOp",EDGE,"E1386"),sQuery(id+"F1.wireOp",EDGE,"E1387"),sQuery(id+"F1.wireOp",EDGE,"E1388"),sQuery(id+"F1.wireOp",EDGE,"E1389"),sQuery(id+"F1.wireOp",EDGE,"E1390"),sQuery(id+"F1.wireOp",EDGE,"E1391"),sQuery(id+"F1.wireOp",EDGE,"E1392"),sQuery(id+"F1.wireOp",EDGE,"E1393"),sQuery(id+"F1.wireOp",EDGE,"E1394"),sQuery(id+"F1.wireOp",EDGE,"E1395"),sQuery(id+"F1.wireOp",EDGE,"E1396"),sQuery(id+"F1.wireOp",EDGE,"E1397"),sQuery(id+"F1.wireOp",EDGE,"E1398"),sQuery(id+"F1.wireOp",EDGE,"E1399"),sQuery(id+"F1.wireOp",EDGE,"E1400"),sQuery(id+"F1.wireOp",EDGE,"E1401"),sQuery(id+"F1.wireOp",EDGE,"E1402"),sQuery(id+"F1.wireOp",EDGE,"E1403"),sQuery(id+"F1.wireOp",EDGE,"E1404"),sQuery(id+"F1.wireOp",EDGE,"E1405"),sQuery(id+"F1.wireOp",EDGE,"E1406"),sQuery(id+"F1.wireOp",EDGE,"E1407"),sQuery(id+"F1.wireOp",EDGE,"E1408"),sQuery(id+"F1.wireOp",EDGE,"E1409"),sQuery(id+"F1.wireOp",EDGE,"E1410"),sQuery(id+"F1.wireOp",EDGE,"E1411"),sQuery(id+"F1.wireOp",EDGE,"E1412"),sQuery(id+"F1.wireOp",EDGE,"E1413"),sQuery(id+"F1.wireOp",EDGE,"E1414"),sQuery(id+"F1.wireOp",EDGE,"E1415"),sQuery(id+"F1.wireOp",EDGE,"E1416"),sQuery(id+"F1.wireOp",EDGE,"E1417"),sQuery(id+"F1.wireOp",EDGE,"E1418"),sQuery(id+"F1.wireOp",EDGE,"E1419"),sQuery(id+"F1.wireOp",EDGE,"E1420"),sQuery(id+"F1.wireOp",EDGE,"E1421"),sQuery(id+"F1.wireOp",EDGE,"E1422"),sQuery(id+"F1.wireOp",EDGE,"E1423"),sQuery(id+"F1.wireOp",EDGE,"E1424"),sQuery(id+"F1.wireOp",EDGE,"E1425"),sQuery(id+"F1.wireOp",EDGE,"E1426"),sQuery(id+"F1.wireOp",EDGE,"E1427"),sQuery(id+"F1.wireOp",EDGE,"E1428"),sQuery(id+"F1.wireOp",EDGE,"E1429"),sQuery(id+"F1.wireOp",EDGE,"E1430"),sQuery(id+"F1.wireOp",EDGE,"E1431"),sQuery(id+"F1.wireOp",EDGE,"E1432"),sQuery(id+"F1.wireOp",EDGE,"E1433"),sQuery(id+"F1.wireOp",EDGE,"E1434"),sQuery(id+"F1.wireOp",EDGE,"E1435"),sQuery(id+"F1.wireOp",EDGE,"E1436"),sQuery(id+"F1.wireOp",EDGE,"E1437"),sQuery(id+"F1.wireOp",EDGE,"E1438"),sQuery(id+"F1.wireOp",EDGE,"E1439"),sQuery(id+"F1.wireOp",EDGE,"E1440"),sQuery(id+"F1.wireOp",EDGE,"E1441"),sQuery(id+"F1.wireOp",EDGE,"E1442"),sQuery(id+"F1.wireOp",EDGE,"E1443"),sQuery(id+"F1.wireOp",EDGE,"E1444"),sQuery(id+"F1.wireOp",EDGE,"E1445"),sQuery(id+"F1.wireOp",EDGE,"E1446"),sQuery(id+"F1.wireOp",EDGE,"E1447"),sQuery(id+"F1.wireOp",EDGE,"E1448"),sQuery(id+"F1.wireOp",EDGE,"E1449"),sQuery(id+"F1.wireOp",EDGE,"E1450"),sQuery(id+"F1.wireOp",EDGE,"E1451"),sQuery(id+"F1.wireOp",EDGE,"E1452"),sQuery(id+"F1.wireOp",EDGE,"E1453"),sQuery(id+"F1.wireOp",EDGE,"E1454"),sQuery(id+"F1.wireOp",EDGE,"E1455"),sQuery(id+"F1.wireOp",EDGE,"E1456"),sQuery(id+"F1.wireOp",EDGE,"E1457"),sQuery(id+"F1.wireOp",EDGE,"E1458"),sQuery(id+"F1.wireOp",EDGE,"E1459"),sQuery(id+"F1.wireOp",EDGE,"E1460"),sQuery(id+"F1.wireOp",EDGE,"E1461"),sQuery(id+"F1.wireOp",EDGE,"E1462"),sQuery(id+"F1.wireOp",EDGE,"E1463"),sQuery(id+"F1.wireOp",EDGE,"E1464"),sQuery(id+"F1.wireOp",EDGE,"E1465"),sQuery(id+"F1.wireOp",EDGE,"E1466"),sQuery(id+"F1.wireOp",EDGE,"E1467"),sQuery(id+"F1.wireOp",EDGE,"E1468"),sQuery(id+"F1.wireOp",EDGE,"E1469"),sQuery(id+"F1.wireOp",EDGE,"E1470"),sQuery(id+"F1.wireOp",EDGE,"E1471"),sQuery(id+"F1.wireOp",EDGE,"E1472"),sQuery(id+"F1.wireOp",EDGE,"E1473"),sQuery(id+"F1.wireOp",EDGE,"E1474"),sQuery(id+"F1.wireOp",EDGE,"E1475"),sQuery(id+"F1.wireOp",EDGE,"E1476"),sQuery(id+"F1.wireOp",EDGE,"E1477"),sQuery(id+"F1.wireOp",EDGE,"E1478"),sQuery(id+"F1.wireOp",EDGE,"E1479"),sQuery(id+"F1.wireOp",EDGE,"E1480"),sQuery(id+"F1.wireOp",EDGE,"E1481"),sQuery(id+"F1.wireOp",EDGE,"E1482"),sQuery(id+"F1.wireOp",EDGE,"E1483"),sQuery(id+"F1.wireOp",EDGE,"E1484"),sQuery(id+"F1.wireOp",EDGE,"E1485"),sQuery(id+"F1.wireOp",EDGE,"E1486"),sQuery(id+"F1.wireOp",EDGE,"E1487"),sQuery(id+"F1.wireOp",EDGE,"E1488"),sQuery(id+"F1.wireOp",EDGE,"E1489"),sQuery(id+"F1.wireOp",EDGE,"E1490"),sQuery(id+"F1.wireOp",EDGE,"E1491"),sQuery(id+"F1.wireOp",EDGE,"E1492"),sQuery(id+"F1.wireOp",EDGE,"E1493"),sQuery(id+"F1.wireOp",EDGE,"E1494"),sQuery(id+"F1.wireOp",EDGE,"E1495"),sQuery(id+"F1.wireOp",EDGE,"E1496"),sQuery(id+"F1.wireOp",EDGE,"E1497"),sQuery(id+"F1.wireOp",EDGE,"E1498"),sQuery(id+"F1.wireOp",EDGE,"E1499"),sQuery(id+"F1.wireOp",EDGE,"E1500"),sQuery(id+"F1.wireOp",EDGE,"E1501"),sQuery(id+"F1.wireOp",EDGE,"E1502"),sQuery(id+"F1.wireOp",EDGE,"E1503"),sQuery(id+"F1.wireOp",EDGE,"E1504"),sQuery(id+"F1.wireOp",EDGE,"E1505"),sQuery(id+"F1.wireOp",EDGE,"E1506"),sQuery(id+"F1.wireOp",EDGE,"E1507"),sQuery(id+"F1.wireOp",EDGE,"E1508"),sQuery(id+"F1.wireOp",EDGE,"E1509"),sQuery(id+"F1.wireOp",EDGE,"E1510"),sQuery(id+"F1.wireOp",EDGE,"E1511"),sQuery(id+"F1.wireOp",EDGE,"E1512"),sQuery(id+"F1.wireOp",EDGE,"E1513"),sQuery(id+"F1.wireOp",EDGE,"E1514"),sQuery(id+"F1.wireOp",EDGE,"E1515"),sQuery(id+"F1.wireOp",EDGE,"E1516"),sQuery(id+"F1.wireOp",EDGE,"E1517"),sQuery(id+"F1.wireOp",EDGE,"E1518"),sQuery(id+"F1.wireOp",EDGE,"E1519"),sQuery(id+"F1.wireOp",EDGE,"E1520"),sQuery(id+"F1.wireOp",EDGE,"E1521"),sQuery(id+"F1.wireOp",EDGE,"E1522"),sQuery(id+"F1.wireOp",EDGE,"E1523"),sQuery(id+"F1.wireOp",EDGE,"E1524"),sQuery(id+"F1.wireOp",EDGE,"E1525"),sQuery(id+"F1.wireOp",EDGE,"E1526"),sQuery(id+"F1.wireOp",EDGE,"E1527"),sQuery(id+"F1.wireOp",EDGE,"E1528"),sQuery(id+"F1.wireOp",EDGE,"E1529"),sQuery(id+"F1.wireOp",EDGE,"E1530"),sQuery(id+"F1.wireOp",EDGE,"E1531"),sQuery(id+"F1.wireOp",EDGE,"E1532"),sQuery(id+"F1.wireOp",EDGE,"E1533"),sQuery(id+"F1.wireOp",EDGE,"E1534"),sQuery(id+"F1.wireOp",EDGE,"E1535"),sQuery(id+"F1.wireOp",EDGE,"E1536"),sQuery(id+"F1.wireOp",EDGE,"E1537"),sQuery(id+"F1.wireOp",EDGE,"E1538"),sQuery(id+"F1.wireOp",EDGE,"E1539"),sQuery(id+"F1.wireOp",EDGE,"E1540"),sQuery(id+"F1.wireOp",EDGE,"E1541"),sQuery(id+"F1.wireOp",EDGE,"E1542"),sQuery(id+"F1.wireOp",EDGE,"E1543"),sQuery(id+"F1.wireOp",EDGE,"E1544"),sQuery(id+"F1.wireOp",EDGE,"E1545"),sQuery(id+"F1.wireOp",EDGE,"E1546"),sQuery(id+"F1.wireOp",EDGE,"E1547"),sQuery(id+"F1.wireOp",EDGE,"E1548"),sQuery(id+"F1.wireOp",EDGE,"E1549"),sQuery(id+"F1.wireOp",EDGE,"E1550"),sQuery(id+"F1.wireOp",EDGE,"E1551"),sQuery(id+"F1.wireOp",EDGE,"E1552"),sQuery(id+"F1.wireOp",EDGE,"E1553"),sQuery(id+"F1.wireOp",EDGE,"E1554"),sQuery(id+"F1.wireOp",EDGE,"E1555"),sQuery(id+"F1.wireOp",EDGE,"E1556"),sQuery(id+"F1.wireOp",EDGE,"E1557"),sQuery(id+"F1.wireOp",EDGE,"E1558"),sQuery(id+"F1.wireOp",EDGE,"E1559"),sQuery(id+"F1.wireOp",EDGE,"E1560"),sQuery(id+"F1.wireOp",EDGE,"E1561"),sQuery(id+"F1.wireOp",EDGE,"E1562"),sQuery(id+"F1.wireOp",EDGE,"E1563"),sQuery(id+"F1.wireOp",EDGE,"E1564"),sQuery(id+"F1.wireOp",EDGE,"E1565"),sQuery(id+"F1.wireOp",EDGE,"E1566"),sQuery(id+"F1.wireOp",EDGE,"E1567"),sQuery(id+"F1.wireOp",EDGE,"E1568"),sQuery(id+"F1.wireOp",EDGE,"E1569"),sQuery(id+"F1.wireOp",EDGE,"E1570"),sQuery(id+"F1.wireOp",EDGE,"E1571"),sQuery(id+"F1.wireOp",EDGE,"E1572"),sQuery(id+"F1.wireOp",EDGE,"E1573"),sQuery(id+"F1.wireOp",EDGE,"E1574"),sQuery(id+"F1.wireOp",EDGE,"E1575"),sQuery(id+"F1.wireOp",EDGE,"E1576"),sQuery(id+"F1.wireOp",EDGE,"E1577"),sQuery(id+"F1.wireOp",EDGE,"E1578"),sQuery(id+"F1.wireOp",EDGE,"E1579"),sQuery(id+"F1.wireOp",EDGE,"E1580"),sQuery(id+"F1.wireOp",EDGE,"E1581"),sQuery(id+"F1.wireOp",EDGE,"E1582"),sQuery(id+"F1.wireOp",EDGE,"E1583"),sQuery(id+"F1.wireOp",EDGE,"E1584"),sQuery(id+"F1.wireOp",EDGE,"E1585"),sQuery(id+"F1.wireOp",EDGE,"E1586"),sQuery(id+"F1.wireOp",EDGE,"E1587"),sQuery(id+"F1.wireOp",EDGE,"E1588"),sQuery(id+"F1.wireOp",EDGE,"E1589"),sQuery(id+"F1.wireOp",EDGE,"E1590"),sQuery(id+"F1.wireOp",EDGE,"E1591"),sQuery(id+"F1.wireOp",EDGE,"E1592"),sQuery(id+"F1.wireOp",EDGE,"E1593"),sQuery(id+"F1.wireOp",EDGE,"E1594"),sQuery(id+"F1.wireOp",EDGE,"E1595"),sQuery(id+"F1.wireOp",EDGE,"E1596"),sQuery(id+"F1.wireOp",EDGE,"E1597"),sQuery(id+"F1.wireOp",EDGE,"E1598"),sQuery(id+"F1.wireOp",EDGE,"E1599"),sQuery(id+"F1.wireOp",EDGE,"E1600"),sQuery(id+"F1.wireOp",EDGE,"E1601"),sQuery(id+"F1.wireOp",EDGE,"E1602"),sQuery(id+"F1.wireOp",EDGE,"E1603"),sQuery(id+"F1.wireOp",EDGE,"E1604"),sQuery(id+"F1.wireOp",EDGE,"E1605"),sQuery(id+"F1.wireOp",EDGE,"E1606"),sQuery(id+"F1.wireOp",EDGE,"E1607"),sQuery(id+"F1.wireOp",EDGE,"E1608"),sQuery(id+"F1.wireOp",EDGE,"E1609"),sQuery(id+"F1.wireOp",EDGE,"E1610"),sQuery(id+"F1.wireOp",EDGE,"E1611"),sQuery(id+"F1.wireOp",EDGE,"E1612"),sQuery(id+"F1.wireOp",EDGE,"E1613"),sQuery(id+"F1.wireOp",EDGE,"E1614"),sQuery(id+"F1.wireOp",EDGE,"E1615"),sQuery(id+"F1.wireOp",EDGE,"E1616"),sQuery(id+"F1.wireOp",EDGE,"E1617"),sQuery(id+"F1.wireOp",EDGE,"E1618"),sQuery(id+"F1.wireOp",EDGE,"E1619"),sQuery(id+"F1.wireOp",EDGE,"E1620"),sQuery(id+"F1.wireOp",EDGE,"E1621"),sQuery(id+"F1.wireOp",EDGE,"E1622"),sQuery(id+"F1.wireOp",EDGE,"E1623"),sQuery(id+"F1.wireOp",EDGE,"E1624"),sQuery(id+"F1.wireOp",EDGE,"E1625"),sQuery(id+"F1.wireOp",EDGE,"E1626"),sQuery(id+"F1.wireOp",EDGE,"E1627"),sQuery(id+"F1.wireOp",EDGE,"E1628"),sQuery(id+"F1.wireOp",EDGE,"E1629"),sQuery(id+"F1.wireOp",EDGE,"E1630"),sQuery(id+"F1.wireOp",EDGE,"E1631"),sQuery(id+"F1.wireOp",EDGE,"E1632"),sQuery(id+"F1.wireOp",EDGE,"E1633"),sQuery(id+"F1.wireOp",EDGE,"E1634"),sQuery(id+"F1.wireOp",EDGE,"E1635"),sQuery(id+"F1.wireOp",EDGE,"E1636"),sQuery(id+"F1.wireOp",EDGE,"E1637"),sQuery(id+"F1.wireOp",EDGE,"E1638"),sQuery(id+"F1.wireOp",EDGE,"E1639"),sQuery(id+"F1.wireOp",EDGE,"E1640"),sQuery(id+"F1.wireOp",EDGE,"E1641"),sQuery(id+"F1.wireOp",EDGE,"E1642"),sQuery(id+"F1.wireOp",EDGE,"E1643"),sQuery(id+"F1.wireOp",EDGE,"E1644"),sQuery(id+"F1.wireOp",EDGE,"E1645"),sQuery(id+"F1.wireOp",EDGE,"E1646"),sQuery(id+"F1.wireOp",EDGE,"E1647"),sQuery(id+"F1.wireOp",EDGE,"E1648"),sQuery(id+"F1.wireOp",EDGE,"E1649"),sQuery(id+"F1.wireOp",EDGE,"E1650"),sQuery(id+"F1.wireOp",EDGE,"E1651"),sQuery(id+"F1.wireOp",EDGE,"E1652"),sQuery(id+"F1.wireOp",EDGE,"E1653"),sQuery(id+"F1.wireOp",EDGE,"E1654"),sQuery(id+"F1.wireOp",EDGE,"E1655"),sQuery(id+"F1.wireOp",EDGE,"E1656"),sQuery(id+"F1.wireOp",EDGE,"E1657"),sQuery(id+"F1.wireOp",EDGE,"E1658"),sQuery(id+"F1.wireOp",EDGE,"E1659"),sQuery(id+"F1.wireOp",EDGE,"E1660"),sQuery(id+"F1.wireOp",EDGE,"E1661"),sQuery(id+"F1.wireOp",EDGE,"E1662"),sQuery(id+"F1.wireOp",EDGE,"E1663"),sQuery(id+"F1.wireOp",EDGE,"E1664"),sQuery(id+"F1.wireOp",EDGE,"E1665"),sQuery(id+"F1.wireOp",EDGE,"E1666"),sQuery(id+"F1.wireOp",EDGE,"E1667"),sQuery(id+"F1.wireOp",EDGE,"E1668"),sQuery(id+"F1.wireOp",EDGE,"E1669"),sQuery(id+"F1.wireOp",EDGE,"E1670"),sQuery(id+"F1.wireOp",EDGE,"E1671"),sQuery(id+"F1.wireOp",EDGE,"E1672"),sQuery(id+"F1.wireOp",EDGE,"E1673"),sQuery(id+"F1.wireOp",EDGE,"E1674"),sQuery(id+"F1.wireOp",EDGE,"E1675"),sQuery(id+"F1.wireOp",EDGE,"E1676"),sQuery(id+"F1.wireOp",EDGE,"E1677"),sQuery(id+"F1.wireOp",EDGE,"E1678"),sQuery(id+"F1.wireOp",EDGE,"E1679"),sQuery(id+"F1.wireOp",EDGE,"E1680"),sQuery(id+"F1.wireOp",EDGE,"E1681"),sQuery(id+"F1.wireOp",EDGE,"E1682"),sQuery(id+"F1.wireOp",EDGE,"E1683"),sQuery(id+"F1.wireOp",EDGE,"E1684"),sQuery(id+"F1.wireOp",EDGE,"E1685"),sQuery(id+"F1.wireOp",EDGE,"E1686"),sQuery(id+"F1.wireOp",EDGE,"E1687"),sQuery(id+"F1.wireOp",EDGE,"E1688"),sQuery(id+"F1.wireOp",EDGE,"E1689"),sQuery(id+"F1.wireOp",EDGE,"E1690"),sQuery(id+"F1.wireOp",EDGE,"E1691"),sQuery(id+"F1.wireOp",EDGE,"E1692"),sQuery(id+"F1.wireOp",EDGE,"E1693"),sQuery(id+"F1.wireOp",EDGE,"E1694"),sQuery(id+"F1.wireOp",EDGE,"E1695"),sQuery(id+"F1.wireOp",EDGE,"E1696"),sQuery(id+"F1.wireOp",EDGE,"E1697"),sQuery(id+"F1.wireOp",EDGE,"E1698"),sQuery(id+"F1.wireOp",EDGE,"E1699"),sQuery(id+"F1.wireOp",EDGE,"E1700"),sQuery(id+"F1.wireOp",EDGE,"E1701"),sQuery(id+"F1.wireOp",EDGE,"E1702"),sQuery(id+"F1.wireOp",EDGE,"E1703"),sQuery(id+"F1.wireOp",EDGE,"E1704"),sQuery(id+"F1.wireOp",EDGE,"E1705"),sQuery(id+"F1.wireOp",EDGE,"E1706"),sQuery(id+"F1.wireOp",EDGE,"E1707"),sQuery(id+"F1.wireOp",EDGE,"E1708"),sQuery(id+"F1.wireOp",EDGE,"E1709"),sQuery(id+"F1.wireOp",EDGE,"E1710"),sQuery(id+"F1.wireOp",EDGE,"E1711"),sQuery(id+"F1.wireOp",EDGE,"E1712"),sQuery(id+"F1.wireOp",EDGE,"E1713"),sQuery(id+"F1.wireOp",EDGE,"E1714"),sQuery(id+"F1.wireOp",EDGE,"E1715"),sQuery(id+"F1.wireOp",EDGE,"E1716"),sQuery(id+"F1.wireOp",EDGE,"E1717"),sQuery(id+"F1.wireOp",EDGE,"E1718"),sQuery(id+"F1.wireOp",EDGE,"E1719"),sQuery(id+"F1.wireOp",EDGE,"E1720"),sQuery(id+"F1.wireOp",EDGE,"E1721"),sQuery(id+"F1.wireOp",EDGE,"E1722"),sQuery(id+"F1.wireOp",EDGE,"E1723"),sQuery(id+"F1.wireOp",EDGE,"E1724"),sQuery(id+"F1.wireOp",EDGE,"E1725"),sQuery(id+"F1.wireOp",EDGE,"E1726"),sQuery(id+"F1.wireOp",EDGE,"E1727"),sQuery(id+"F1.wireOp",EDGE,"E1728"),sQuery(id+"F1.wireOp",EDGE,"E1729"),sQuery(id+"F1.wireOp",EDGE,"E1730"),sQuery(id+"F1.wireOp",EDGE,"E1731"),sQuery(id+"F1.wireOp",EDGE,"E1732"),sQuery(id+"F1.wireOp",EDGE,"E1733"),sQuery(id+"F1.wireOp",EDGE,"E1734"),sQuery(id+"F1.wireOp",EDGE,"E1735"),sQuery(id+"F1.wireOp",EDGE,"E1736"),sQuery(id+"F1.wireOp",EDGE,"E1737"),sQuery(id+"F1.wireOp",EDGE,"E1738"),sQuery(id+"F1.wireOp",EDGE,"E1739"),sQuery(id+"F1.wireOp",EDGE,"E1740"),sQuery(id+"F1.wireOp",EDGE,"E1741"),sQuery(id+"F1.wireOp",EDGE,"E1742"),sQuery(id+"F1.wireOp",EDGE,"E1743"),sQuery(id+"F1.wireOp",EDGE,"E1744"),sQuery(id+"F1.wireOp",EDGE,"E1745"),sQuery(id+"F1.wireOp",EDGE,"E1746"),sQuery(id+"F1.wireOp",EDGE,"E1747"),sQuery(id+"F1.wireOp",EDGE,"E1748"),sQuery(id+"F1.wireOp",EDGE,"E1749"),sQuery(id+"F1.wireOp",EDGE,"E1750"),sQuery(id+"F1.wireOp",EDGE,"E1751"),sQuery(id+"F1.wireOp",EDGE,"E1752"),sQuery(id+"F1.wireOp",EDGE,"E1753"),sQuery(id+"F1.wireOp",EDGE,"E1754"),sQuery(id+"F1.wireOp",EDGE,"E1755"),sQuery(id+"F1.wireOp",EDGE,"E1756"),sQuery(id+"F1.wireOp",EDGE,"E1757"),sQuery(id+"F1.wireOp",EDGE,"E1758"),sQuery(id+"F1.wireOp",EDGE,"E1759"),sQuery(id+"F1.wireOp",EDGE,"E1760"),sQuery(id+"F1.wireOp",EDGE,"E1761"),sQuery(id+"F1.wireOp",EDGE,"E1762"),sQuery(id+"F1.wireOp",EDGE,"E1763"),sQuery(id+"F1.wireOp",EDGE,"E1764"),sQuery(id+"F1.wireOp",EDGE,"E1765"),sQuery(id+"F1.wireOp",EDGE,"E1766"),sQuery(id+"F1.wireOp",EDGE,"E1767"),sQuery(id+"F1.wireOp",EDGE,"E1768"),sQuery(id+"F1.wireOp",EDGE,"E1769"),sQuery(id+"F1.wireOp",EDGE,"E1770"),sQuery(id+"F1.wireOp",EDGE,"E1771"),sQuery(id+"F1.wireOp",EDGE,"E1772"),sQuery(id+"F1.wireOp",EDGE,"E1773"),sQuery(id+"F1.wireOp",EDGE,"E1774"),sQuery(id+"F1.wireOp",EDGE,"E1775"),sQuery(id+"F1.wireOp",EDGE,"E1776"),sQuery(id+"F1.wireOp",EDGE,"E1777"),sQuery(id+"F1.wireOp",EDGE,"E1778"),sQuery(id+"F1.wireOp",EDGE,"E1779"),sQuery(id+"F1.wireOp",EDGE,"E1780"),sQuery(id+"F1.wireOp",EDGE,"E1781"),sQuery(id+"F1.wireOp",EDGE,"E1782"),sQuery(id+"F1.wireOp",EDGE,"E1783"),sQuery(id+"F1.wireOp",EDGE,"E1784"),sQuery(id+"F1.wireOp",EDGE,"E1785"),sQuery(id+"F1.wireOp",EDGE,"E1786"),sQuery(id+"F1.wireOp",EDGE,"E1787"),sQuery(id+"F1.wireOp",EDGE,"E1788"),sQuery(id+"F1.wireOp",EDGE,"E1789"),sQuery(id+"F1.wireOp",EDGE,"E1790"),sQuery(id+"F1.wireOp",EDGE,"E1791"),sQuery(id+"F1.wireOp",EDGE,"E1792"),sQuery(id+"F1.wireOp",EDGE,"E1793"),sQuery(id+"F1.wireOp",EDGE,"E1794"),sQuery(id+"F1.wireOp",EDGE,"E1795"),sQuery(id+"F1.wireOp",EDGE,"E1796"),sQuery(id+"F1.wireOp",EDGE,"E1797"),sQuery(id+"F1.wireOp",EDGE,"E1798"),sQuery(id+"F1.wireOp",EDGE,"E1799"),sQuery(id+"F1.wireOp",EDGE,"E1800"),sQuery(id+"F1.wireOp",EDGE,"E1801"),sQuery(id+"F1.wireOp",EDGE,"E1802"),sQuery(id+"F1.wireOp",EDGE,"E1803"),sQuery(id+"F1.wireOp",EDGE,"E1804"),sQuery(id+"F1.wireOp",EDGE,"E1805"),sQuery(id+"F1.wireOp",EDGE,"E1806"),sQuery(id+"F1.wireOp",EDGE,"E1807"),sQuery(id+"F1.wireOp",EDGE,"E1808"),sQuery(id+"F1.wireOp",EDGE,"E1809"),sQuery(id+"F1.wireOp",EDGE,"E1810"),sQuery(id+"F1.wireOp",EDGE,"E1811"),sQuery(id+"F1.wireOp",EDGE,"E1812"),sQuery(id+"F1.wireOp",EDGE,"E1813"),sQuery(id+"F1.wireOp",EDGE,"E1814"),sQuery(id+"F1.wireOp",EDGE,"E1815"),sQuery(id+"F1.wireOp",EDGE,"E1816"),sQuery(id+"F1.wireOp",EDGE,"E1817"),sQuery(id+"F1.wireOp",EDGE,"E1818"),sQuery(id+"F1.wireOp",EDGE,"E1819"),sQuery(id+"F1.wireOp",EDGE,"E1820"),sQuery(id+"F1.wireOp",EDGE,"E1821"),sQuery(id+"F1.wireOp",EDGE,"E1822"),sQuery(id+"F1.wireOp",EDGE,"E1823"),sQuery(id+"F1.wireOp",EDGE,"E1824"),sQuery(id+"F1.wireOp",EDGE,"E1825"),sQuery(id+"F1.wireOp",EDGE,"E1826"),sQuery(id+"F1.wireOp",EDGE,"E1827"),sQuery(id+"F1.wireOp",EDGE,"E1828"),sQuery(id+"F1.wireOp",EDGE,"E1829"),sQuery(id+"F1.wireOp",EDGE,"E1830"),sQuery(id+"F1.wireOp",EDGE,"E1831"),sQuery(id+"F1.wireOp",EDGE,"E1832"),sQuery(id+"F1.wireOp",EDGE,"E1833"),sQuery(id+"F1.wireOp",EDGE,"E1834"),sQuery(id+"F1.wireOp",EDGE,"E1835"),sQuery(id+"F1.wireOp",EDGE,"E1836"),sQuery(id+"F1.wireOp",EDGE,"E1837"),sQuery(id+"F1.wireOp",EDGE,"E1838"),sQuery(id+"F1.wireOp",EDGE,"E1839"),sQuery(id+"F1.wireOp",EDGE,"E1840"),sQuery(id+"F1.wireOp",EDGE,"E1841"),sQuery(id+"F1.wireOp",EDGE,"E1842"),sQuery(id+"F1.wireOp",EDGE,"E1843"),sQuery(id+"F1.wireOp",EDGE,"E1844"),sQuery(id+"F1.wireOp",EDGE,"E1845"),sQuery(id+"F1.wireOp",EDGE,"E1846"),sQuery(id+"F1.wireOp",EDGE,"E1847"),sQuery(id+"F1.wireOp",EDGE,"E1848"),sQuery(id+"F1.wireOp",EDGE,"E1849"),sQuery(id+"F1.wireOp",EDGE,"E1850"),sQuery(id+"F1.wireOp",EDGE,"E1851"),sQuery(id+"F1.wireOp",EDGE,"E1852"),sQuery(id+"F1.wireOp",EDGE,"E1853"),sQuery(id+"F1.wireOp",EDGE,"E1854"),sQuery(id+"F1.wireOp",EDGE,"E1855"),sQuery(id+"F1.wireOp",EDGE,"E1856"),sQuery(id+"F1.wireOp",EDGE,"E1857"),sQuery(id+"F1.wireOp",EDGE,"E1858"),sQuery(id+"F1.wireOp",EDGE,"E1859"),sQuery(id+"F1.wireOp",EDGE,"E1860"),sQuery(id+"F1.wireOp",EDGE,"E1861"),sQuery(id+"F1.wireOp",EDGE,"E1862"),sQuery(id+"F1.wireOp",EDGE,"E1863"),sQuery(id+"F1.wireOp",EDGE,"E1864"),sQuery(id+"F1.wireOp",EDGE,"E1865"),sQuery(id+"F1.wireOp",EDGE,"E1866"),sQuery(id+"F1.wireOp",EDGE,"E1867"),sQuery(id+"F1.wireOp",EDGE,"E1868"),sQuery(id+"F1.wireOp",EDGE,"E1869"),sQuery(id+"F1.wireOp",EDGE,"E1870"),sQuery(id+"F1.wireOp",EDGE,"E1871"),sQuery(id+"F1.wireOp",EDGE,"E1872"),sQuery(id+"F1.wireOp",EDGE,"E1873"),sQuery(id+"F1.wireOp",EDGE,"E1874"),sQuery(id+"F1.wireOp",EDGE,"E1875"),sQuery(id+"F1.wireOp",EDGE,"E1876"),sQuery(id+"F1.wireOp",EDGE,"E1877"),sQuery(id+"F1.wireOp",EDGE,"E1878"),sQuery(id+"F1.wireOp",EDGE,"E1879"),sQuery(id+"F1.wireOp",EDGE,"E1880"),sQuery(id+"F1.wireOp",EDGE,"E1881"),sQuery(id+"F1.wireOp",EDGE,"E1882"),sQuery(id+"F1.wireOp",EDGE,"E1883"),sQuery(id+"F1.wireOp",EDGE,"E1884"),sQuery(id+"F1.wireOp",EDGE,"E1885"),sQuery(id+"F1.wireOp",EDGE,"E1886"),sQuery(id+"F1.wireOp",EDGE,"E1887"),sQuery(id+"F1.wireOp",EDGE,"E1888"),sQuery(id+"F1.wireOp",EDGE,"E1889"),sQuery(id+"F1.wireOp",EDGE,"E1890"),sQuery(id+"F1.wireOp",EDGE,"E1891"),sQuery(id+"F1.wireOp",EDGE,"E1892"),sQuery(id+"F1.wireOp",EDGE,"E1893"),sQuery(id+"F1.wireOp",EDGE,"E1894"),sQuery(id+"F1.wireOp",EDGE,"E1895"),sQuery(id+"F1.wireOp",EDGE,"E1896"),sQuery(id+"F1.wireOp",EDGE,"E1897"),sQuery(id+"F1.wireOp",EDGE,"E1898"),sQuery(id+"F1.wireOp",EDGE,"E1899"),sQuery(id+"F1.wireOp",EDGE,"E1900"),sQuery(id+"F1.wireOp",EDGE,"E1901"),sQuery(id+"F1.wireOp",EDGE,"E1902"),sQuery(id+"F1.wireOp",EDGE,"E1903"),sQuery(id+"F1.wireOp",EDGE,"E1904"),sQuery(id+"F1.wireOp",EDGE,"E1905"),sQuery(id+"F1.wireOp",EDGE,"E1906"),sQuery(id+"F1.wireOp",EDGE,"E1907"),sQuery(id+"F1.wireOp",EDGE,"E1908"),sQuery(id+"F1.wireOp",EDGE,"E1909"),sQuery(id+"F1.wireOp",EDGE,"E1910"),sQuery(id+"F1.wireOp",EDGE,"E1911"),sQuery(id+"F1.wireOp",EDGE,"E1912"),sQuery(id+"F1.wireOp",EDGE,"E1913"),sQuery(id+"F1.wireOp",EDGE,"E1914"),sQuery(id+"F1.wireOp",EDGE,"E1915"),sQuery(id+"F1.wireOp",EDGE,"E1916"),sQuery(id+"F1.wireOp",EDGE,"E1917"),sQuery(id+"F1.wireOp",EDGE,"E1918"),sQuery(id+"F1.wireOp",EDGE,"E1919"),sQuery(id+"F1.wireOp",EDGE,"E1920"),sQuery(id+"F1.wireOp",EDGE,"E1921"),sQuery(id+"F1.wireOp",EDGE,"E1922"),sQuery(id+"F1.wireOp",EDGE,"E1923"),sQuery(id+"F1.wireOp",EDGE,"E1924"),sQuery(id+"F1.wireOp",EDGE,"E1925"),sQuery(id+"F1.wireOp",EDGE,"E1926"),sQuery(id+"F1.wireOp",EDGE,"E1927"),sQuery(id+"F1.wireOp",EDGE,"E1928"),sQuery(id+"F1.wireOp",EDGE,"E1929"),sQuery(id+"F1.wireOp",EDGE,"E1930"),sQuery(id+"F1.wireOp",EDGE,"E1931"),sQuery(id+"F1.wireOp",EDGE,"E1932"),sQuery(id+"F1.wireOp",EDGE,"E1933"),sQuery(id+"F1.wireOp",EDGE,"E1934"),sQuery(id+"F1.wireOp",EDGE,"E1935"),sQuery(id+"F1.wireOp",EDGE,"E1936"),sQuery(id+"F1.wireOp",EDGE,"E1937"),sQuery(id+"F1.wireOp",EDGE,"E1938"),sQuery(id+"F1.wireOp",EDGE,"E1939"),sQuery(id+"F1.wireOp",EDGE,"E1940"),sQuery(id+"F1.wireOp",EDGE,"E1941"),sQuery(id+"F1.wireOp",EDGE,"E1942"),sQuery(id+"F1.wireOp",EDGE,"E1943"),sQuery(id+"F1.wireOp",EDGE,"E1944"),sQuery(id+"F1.wireOp",EDGE,"E1945"),sQuery(id+"F1.wireOp",EDGE,"E1946"),sQuery(id+"F1.wireOp",EDGE,"E1947"),sQuery(id+"F1.wireOp",EDGE,"E1948"),sQuery(id+"F1.wireOp",EDGE,"E1949"),sQuery(id+"F1.wireOp",EDGE,"E1950"),sQuery(id+"F1.wireOp",EDGE,"E1951"),sQuery(id+"F1.wireOp",EDGE,"E1952"),sQuery(id+"F1.wireOp",EDGE,"E1953"),sQuery(id+"F1.wireOp",EDGE,"E1954"),sQuery(id+"F1.wireOp",EDGE,"E1955"),sQuery(id+"F1.wireOp",EDGE,"E1956"),sQuery(id+"F1.wireOp",EDGE,"E1957"),sQuery(id+"F1.wireOp",EDGE,"E1958"),sQuery(id+"F1.wireOp",EDGE,"E1959"),sQuery(id+"F1.wireOp",EDGE,"E1960"),sQuery(id+"F1.wireOp",EDGE,"E1961"),sQuery(id+"F1.wireOp",EDGE,"E1962"),sQuery(id+"F1.wireOp",EDGE,"E1963"),sQuery(id+"F1.wireOp",EDGE,"E1964"),sQuery(id+"F1.wireOp",EDGE,"E1965"),sQuery(id+"F1.wireOp",EDGE,"E1966"),sQuery(id+"F1.wireOp",EDGE,"E1967"),sQuery(id+"F1.wireOp",EDGE,"E1968"),sQuery(id+"F1.wireOp",EDGE,"E1969"),sQuery(id+"F1.wireOp",EDGE,"E1970"),sQuery(id+"F1.wireOp",EDGE,"E1971"),sQuery(id+"F1.wireOp",EDGE,"E1972"),sQuery(id+"F1.wireOp",EDGE,"E1973"),sQuery(id+"F1.wireOp",EDGE,"E1974"),sQuery(id+"F1.wireOp",EDGE,"E1975"),sQuery(id+"F1.wireOp",EDGE,"E1976"),sQuery(id+"F1.wireOp",EDGE,"E1977"),sQuery(id+"F1.wireOp",EDGE,"E1978"),sQuery(id+"F1.wireOp",EDGE,"E1979"),sQuery(id+"F1.wireOp",EDGE,"E1980"),sQuery(id+"F1.wireOp",EDGE,"E1981"),sQuery(id+"F1.wireOp",EDGE,"E1982"),sQuery(id+"F1.wireOp",EDGE,"E1983"),sQuery(id+"F1.wireOp",EDGE,"E1984"),sQuery(id+"F1.wireOp",EDGE,"E1985"),sQuery(id+"F1.wireOp",EDGE,"E1986"),sQuery(id+"F1.wireOp",EDGE,"E1987"),sQuery(id+"F1.wireOp",EDGE,"E1988"),sQuery(id+"F1.wireOp",EDGE,"E1989"),sQuery(id+"F1.wireOp",EDGE,"E1990"),sQuery(id+"F1.wireOp",EDGE,"E1991"),sQuery(id+"F1.wireOp",EDGE,"E1992"),sQuery(id+"F1.wireOp",EDGE,"E1993"),sQuery(id+"F1.wireOp",EDGE,"E1994"),sQuery(id+"F1.wireOp",EDGE,"E1995"),sQuery(id+"F1.wireOp",EDGE,"E1996"),sQuery(id+"F1.wireOp",EDGE,"E1997"),sQuery(id+"F1.wireOp",EDGE,"E1998"),sQuery(id+"F1.wireOp",EDGE,"E1999"),sQuery(id+"F1.wireOp",EDGE,"E2000"),sQuery(id+"F1.wireOp",EDGE,"E2001"),sQuery(id+"F1.wireOp",EDGE,"E2002"),sQuery(id+"F1.wireOp",EDGE,"E2003"),sQuery(id+"F1.wireOp",EDGE,"E2004"),sQuery(id+"F1.wireOp",EDGE,"E2005"),sQuery(id+"F1.wireOp",EDGE,"E2006"),sQuery(id+"F1.wireOp",EDGE,"E2007"),sQuery(id+"F1.wireOp",EDGE,"E2008"),sQuery(id+"F1.wireOp",EDGE,"E2009"),sQuery(id+"F1.wireOp",EDGE,"E2010"),sQuery(id+"F1.wireOp",EDGE,"E2011"),sQuery(id+"F1.wireOp",EDGE,"E2012"),sQuery(id+"F1.wireOp",EDGE,"E2013"),sQuery(id+"F1.wireOp",EDGE,"E2014"),sQuery(id+"F1.wireOp",EDGE,"E2015"),sQuery(id+"F1.wireOp",EDGE,"E2016"),sQuery(id+"F1.wireOp",EDGE,"E2017"),sQuery(id+"F1.wireOp",EDGE,"E2018"),sQuery(id+"F1.wireOp",EDGE,"E2019"),sQuery(id+"F1.wireOp",EDGE,"E2020"),sQuery(id+"F1.wireOp",EDGE,"E2021"),sQuery(id+"F1.wireOp",EDGE,"E2022"),sQuery(id+"F1.wireOp",EDGE,"E2023"),sQuery(id+"F1.wireOp",EDGE,"E2024"),sQuery(id+"F1.wireOp",EDGE,"E2025"),sQuery(id+"F1.wireOp",EDGE,"E2026"),sQuery(id+"F1.wireOp",EDGE,"E2027"),sQuery(id+"F1.wireOp",EDGE,"E2028"),sQuery(id+"F1.wireOp",EDGE,"E2029"),sQuery(id+"F1.wireOp",EDGE,"E2030"),sQuery(id+"F1.wireOp",EDGE,"E2031"),sQuery(id+"F1.wireOp",EDGE,"E2032"),sQuery(id+"F1.wireOp",EDGE,"E2033"),sQuery(id+"F1.wireOp",EDGE,"E2034"),sQuery(id+"F1.wireOp",EDGE,"E2035"),sQuery(id+"F1.wireOp",EDGE,"E2036"),sQuery(id+"F1.wireOp",EDGE,"E2037"),sQuery(id+"F1.wireOp",EDGE,"E2038"),sQuery(id+"F1.wireOp",EDGE,"E2039"),sQuery(id+"F1.wireOp",EDGE,"E2040"),sQuery(id+"F1.wireOp",EDGE,"E2041"),sQuery(id+"F1.wireOp",EDGE,"E2042"),sQuery(id+"F1.wireOp",EDGE,"E2043"),sQuery(id+"F1.wireOp",EDGE,"E2044"),sQuery(id+"F1.wireOp",EDGE,"E2045"),sQuery(id+"F1.wireOp",EDGE,"E2046"),sQuery(id+"F1.wireOp",EDGE,"E2047"),sQuery(id+"F1.wireOp",EDGE,"E2048"),sQuery(id+"F1.wireOp",EDGE,"E2049"),sQuery(id+"F1.wireOp",EDGE,"E2050"),sQuery(id+"F1.wireOp",EDGE,"E2051"),sQuery(id+"F1.wireOp",EDGE,"E2052"),sQuery(id+"F1.wireOp",EDGE,"E2053"),sQuery(id+"F1.wireOp",EDGE,"E2054"),sQuery(id+"F1.wireOp",EDGE,"E2055"),sQuery(id+"F1.wireOp",EDGE,"E2056"),sQuery(id+"F1.wireOp",EDGE,"E2057"),sQuery(id+"F1.wireOp",EDGE,"E2058"),sQuery(id+"F1.wireOp",EDGE,"E2059"),sQuery(id+"F1.wireOp",EDGE,"E2060"),sQuery(id+"F1.wireOp",EDGE,"E2061"),sQuery(id+"F1.wireOp",EDGE,"E2062"),sQuery(id+"F1.wireOp",EDGE,"E2063"),sQuery(id+"F1.wireOp",EDGE,"E2064"),sQuery(id+"F1.wireOp",EDGE,"E2065"),sQuery(id+"F1.wireOp",EDGE,"E2066"),sQuery(id+"F1.wireOp",EDGE,"E2067"),sQuery(id+"F1.wireOp",EDGE,"E2068"),sQuery(id+"F1.wireOp",EDGE,"E2069"),sQuery(id+"F1.wireOp",EDGE,"E2070"),sQuery(id+"F1.wireOp",EDGE,"E2071"),sQuery(id+"F1.wireOp",EDGE,"E2072"),sQuery(id+"F1.wireOp",EDGE,"E2073"),sQuery(id+"F1.wireOp",EDGE,"E2074"),sQuery(id+"F1.wireOp",EDGE,"E2075"),sQuery(id+"F1.wireOp",EDGE,"E2076"),sQuery(id+"F1.wireOp",EDGE,"E2077"),sQuery(id+"F1.wireOp",EDGE,"E2078"),sQuery(id+"F1.wireOp",EDGE,"E2079"),sQuery(id+"F1.wireOp",EDGE,"E2080"),sQuery(id+"F1.wireOp",EDGE,"E2081"),sQuery(id+"F1.wireOp",EDGE,"E2082"),sQuery(id+"F1.wireOp",EDGE,"E2083"),sQuery(id+"F1.wireOp",EDGE,"E2084"),sQuery(id+"F1.wireOp",EDGE,"E2085"),sQuery(id+"F1.wireOp",EDGE,"E2086"),sQuery(id+"F1.wireOp",EDGE,"E2087"),sQuery(id+"F1.wireOp",EDGE,"E2088"),sQuery(id+"F1.wireOp",EDGE,"E2089"),sQuery(id+"F1.wireOp",EDGE,"E2090"),sQuery(id+"F1.wireOp",EDGE,"E2091"),sQuery(id+"F1.wireOp",EDGE,"E2092"),sQuery(id+"F1.wireOp",EDGE,"E2093"),sQuery(id+"F1.wireOp",EDGE,"E2094"),sQuery(id+"F1.wireOp",EDGE,"E2095"),sQuery(id+"F1.wireOp",EDGE,"E2096"),sQuery(id+"F1.wireOp",EDGE,"E2097"),sQuery(id+"F1.wireOp",EDGE,"E2098"),sQuery(id+"F1.wireOp",EDGE,"E2099"),sQuery(id+"F1.wireOp",EDGE,"E2100"),sQuery(id+"F1.wireOp",EDGE,"E2101"),sQuery(id+"F1.wireOp",EDGE,"E2102"),sQuery(id+"F1.wireOp",EDGE,"E2103"),sQuery(id+"F1.wireOp",EDGE,"E2104"),sQuery(id+"F1.wireOp",EDGE,"E2105"),sQuery(id+"F1.wireOp",EDGE,"E2106"),sQuery(id+"F1.wireOp",EDGE,"E2107"),sQuery(id+"F1.wireOp",EDGE,"E2108"),sQuery(id+"F1.wireOp",EDGE,"E2109"),sQuery(id+"F1.wireOp",EDGE,"E2110"),sQuery(id+"F1.wireOp",EDGE,"E2111"),sQuery(id+"F1.wireOp",EDGE,"E2112"),sQuery(id+"F1.wireOp",EDGE,"E2113"),sQuery(id+"F1.wireOp",EDGE,"E2114"),sQuery(id+"F1.wireOp",EDGE,"E2115"),sQuery(id+"F1.wireOp",EDGE,"E2116"),sQuery(id+"F1.wireOp",EDGE,"E2117"),sQuery(id+"F1.wireOp",EDGE,"E2118"),sQuery(id+"F1.wireOp",EDGE,"E2119"),sQuery(id+"F1.wireOp",EDGE,"E2120"),sQuery(id+"F1.wireOp",EDGE,"E2121"),sQuery(id+"F1.wireOp",EDGE,"E2122"),sQuery(id+"F1.wireOp",EDGE,"E2123"),sQuery(id+"F1.wireOp",EDGE,"E2124"),sQuery(id+"F1.wireOp",EDGE,"E2125"),sQuery(id+"F1.wireOp",EDGE,"E2126"),sQuery(id+"F1.wireOp",EDGE,"E2127"),sQuery(id+"F1.wireOp",EDGE,"E2128"),sQuery(id+"F1.wireOp",EDGE,"E2129"),sQuery(id+"F1.wireOp",EDGE,"E2130"),sQuery(id+"F1.wireOp",EDGE,"E2131"),sQuery(id+"F1.wireOp",EDGE,"E2132"),sQuery(id+"F1.wireOp",EDGE,"E2133"),sQuery(id+"F1.wireOp",EDGE,"E2134"),sQuery(id+"F1.wireOp",EDGE,"E2135"),sQuery(id+"F1.wireOp",EDGE,"E2136"),sQuery(id+"F1.wireOp",EDGE,"E2137"),sQuery(id+"F1.wireOp",EDGE,"E2138"),sQuery(id+"F1.wireOp",EDGE,"E2139"),sQuery(id+"F1.wireOp",EDGE,"E2140"),sQuery(id+"F1.wireOp",EDGE,"E2141"),sQuery(id+"F1.wireOp",EDGE,"E2142"),sQuery(id+"F1.wireOp",EDGE,"E2143"),sQuery(id+"F1.wireOp",EDGE,"E2144"),sQuery(id+"F1.wireOp",EDGE,"E2145"),sQuery(id+"F1.wireOp",EDGE,"E2146"),sQuery(id+"F1.wireOp",EDGE,"E2147"),sQuery(id+"F1.wireOp",EDGE,"E2148"),sQuery(id+"F1.wireOp",EDGE,"E2149"),sQuery(id+"F1.wireOp",EDGE,"E2150"),sQuery(id+"F1.wireOp",EDGE,"E2151"),sQuery(id+"F1.wireOp",EDGE,"E2152"),sQuery(id+"F1.wireOp",EDGE,"E2153"),sQuery(id+"F1.wireOp",EDGE,"E2154"),sQuery(id+"F1.wireOp",EDGE,"E2155"),sQuery(id+"F1.wireOp",EDGE,"E2156"),sQuery(id+"F1.wireOp",EDGE,"E2157"),sQuery(id+"F1.wireOp",EDGE,"E2158"),sQuery(id+"F1.wireOp",EDGE,"E2159"),sQuery(id+"F1.wireOp",EDGE,"E2160"),sQuery(id+"F1.wireOp",EDGE,"E2161"),sQuery(id+"F1.wireOp",EDGE,"E2162"),sQuery(id+"F1.wireOp",EDGE,"E2163"),sQuery(id+"F1.wireOp",EDGE,"E2164"),sQuery(id+"F1.wireOp",EDGE,"E2165"),sQuery(id+"F1.wireOp",EDGE,"E2166"),sQuery(id+"F1.wireOp",EDGE,"E2167"),sQuery(id+"F1.wireOp",EDGE,"E2168"),sQuery(id+"F1.wireOp",EDGE,"E2169"),sQuery(id+"F1.wireOp",EDGE,"E2170"),sQuery(id+"F1.wireOp",EDGE,"E2171"),sQuery(id+"F1.wireOp",EDGE,"E2172"),sQuery(id+"F1.wireOp",EDGE,"E2173"),sQuery(id+"F1.wireOp",EDGE,"E2174"),sQuery(id+"F1.wireOp",EDGE,"E2175"),sQuery(id+"F1.wireOp",EDGE,"E2176"),sQuery(id+"F1.wireOp",EDGE,"E2177"),sQuery(id+"F1.wireOp",EDGE,"E2178"),sQuery(id+"F1.wireOp",EDGE,"E2179"),sQuery(id+"F1.wireOp",EDGE,"E2180"),sQuery(id+"F1.wireOp",EDGE,"E2181"),sQuery(id+"F1.wireOp",EDGE,"E2182"),sQuery(id+"F1.wireOp",EDGE,"E2183"),sQuery(id+"F1.wireOp",EDGE,"E2184"),sQuery(id+"F1.wireOp",EDGE,"E2185"),sQuery(id+"F1.wireOp",EDGE,"E2186"),sQuery(id+"F1.wireOp",EDGE,"E2187"),sQuery(id+"F1.wireOp",EDGE,"E2188"),sQuery(id+"F1.wireOp",EDGE,"E2189"),sQuery(id+"F1.wireOp",EDGE,"E2190"),sQuery(id+"F1.wireOp",EDGE,"E2191"),sQuery(id+"F1.wireOp",EDGE,"E2192"),sQuery(id+"F1.wireOp",EDGE,"E2193"),sQuery(id+"F1.wireOp",EDGE,"E2194"),sQuery(id+"F1.wireOp",EDGE,"E2195"),sQuery(id+"F1.wireOp",EDGE,"E2196"),sQuery(id+"F1.wireOp",EDGE,"E2197"),sQuery(id+"F1.wireOp",EDGE,"E2198"),sQuery(id+"F1.wireOp",EDGE,"E2199"),sQuery(id+"F1.wireOp",EDGE,"E2200"),sQuery(id+"F1.wireOp",EDGE,"E2201"),sQuery(id+"F1.wireOp",EDGE,"E2202"),sQuery(id+"F1.wireOp",EDGE,"E2203"),sQuery(id+"F1.wireOp",EDGE,"E2204"),sQuery(id+"F1.wireOp",EDGE,"E2205"),sQuery(id+"F1.wireOp",EDGE,"E2206"),sQuery(id+"F1.wireOp",EDGE,"E2207"),sQuery(id+"F1.wireOp",EDGE,"E2208"),sQuery(id+"F1.wireOp",EDGE,"E2209"),sQuery(id+"F1.wireOp",EDGE,"E2210"),sQuery(id+"F1.wireOp",EDGE,"E2211"),sQuery(id+"F1.wireOp",EDGE,"E2212"),sQuery(id+"F1.wireOp",EDGE,"E2213"),sQuery(id+"F1.wireOp",EDGE,"E2214"),sQuery(id+"F1.wireOp",EDGE,"E2215"),sQuery(id+"F1.wireOp",EDGE,"E2216"),sQuery(id+"F1.wireOp",EDGE,"E2217"),sQuery(id+"F1.wireOp",EDGE,"E2218"),sQuery(id+"F1.wireOp",EDGE,"E2219"),sQuery(id+"F1.wireOp",EDGE,"E2220"),sQuery(id+"F1.wireOp",EDGE,"E2221"),sQuery(id+"F1.wireOp",EDGE,"E2222"),sQuery(id+"F1.wireOp",EDGE,"E2223"),sQuery(id+"F1.wireOp",EDGE,"E2224"),sQuery(id+"F1.wireOp",EDGE,"E2225"),sQuery(id+"F1.wireOp",EDGE,"E2226"),sQuery(id+"F1.wireOp",EDGE,"E2227"),sQuery(id+"F1.wireOp",EDGE,"E2228"),sQuery(id+"F1.wireOp",EDGE,"E2229"),sQuery(id+"F1.wireOp",EDGE,"E2230"),sQuery(id+"F1.wireOp",EDGE,"E2231"),sQuery(id+"F1.wireOp",EDGE,"E2232"),sQuery(id+"F1.wireOp",EDGE,"E2233"),sQuery(id+"F1.wireOp",EDGE,"E2234"),sQuery(id+"F1.wireOp",EDGE,"E2235"),sQuery(id+"F1.wireOp",EDGE,"E2236"),sQuery(id+"F1.wireOp",EDGE,"E2237"),sQuery(id+"F1.wireOp",EDGE,"E2238"),sQuery(id+"F1.wireOp",EDGE,"E2239"),sQuery(id+"F1.wireOp",EDGE,"E2240"),sQuery(id+"F1.wireOp",EDGE,"E2241"),sQuery(id+"F1.wireOp",EDGE,"E2242"),sQuery(id+"F1.wireOp",EDGE,"E2243"),sQuery(id+"F1.wireOp",EDGE,"E2244"),sQuery(id+"F1.wireOp",EDGE,"E2245"),sQuery(id+"F1.wireOp",EDGE,"E2246"),sQuery(id+"F1.wireOp",EDGE,"E2247")])],"isStart":true}),makeQuery(id+"F4.opExtrude","CAP_FACE",FACE,{"disambiguationData":[OSD([sQuery(id+"F3.wireOp",EDGE,"E2248.bottom"),sQuery(id+"F3.wireOp",EDGE,"E2248.top"),sQuery(id+"F3.wireOp",EDGE,"E2248.left"),sQuery(id+"F3.wireOp",EDGE,"E2248.right"),sQuery(id+"F3.wireOp",EDGE,"E2249.bottom"),sQuery(id+"F3.wireOp",EDGE,"E2249.top"),sQuery(id+"F3.wireOp",EDGE,"E2249.left"),sQuery(id+"F3.wireOp",EDGE,"E2249.right")])],"isStart":false})]});
            extrude(context, id + "F8", {"entities" : qUnion([Q0]), "operationType" : NewBodyOperationType.REMOVE, "endBound" : BoundingType.UP_TO_SURFACE, "oppositeDirection" : true, "endBoundEntityFace" : qUnion([Q1]), "depth" : 25 * mm});
        }
        {
            var Q0;
            {var subQ0=sQuery(id+"F5.wireOp",EDGE,"E2251.bottom");var subQ1=sQuery(id+"F5.wireOp",EDGE,"E2251.left");var subQ2=sQuery(id+"F5.wireOp",EDGE,"E2250.left");var subQ3=sQuery(id+"F5.wireOp",EDGE,"E2250.bottom");Q0=makeQuery(id+"F8.boolean.opBoolean","SPLIT",FACE,{"disambiguationData":[TD([makeQuery(id+"F8.opExtrude","SWEPT_FACE",FACE,{"disambiguationData":[OSD([sQuery(id+"F7.wireOp",EDGE,"E2257.left")])]})])],"derivedFrom":makeQuery(id+"F6.opExtrude","CAP_FACE",FACE,{"disambiguationData":[OSD([subQ3,sQuery(id+"F5.wireOp",EDGE,"E2250.top"),subQ2,sQuery(id+"F5.wireOp",EDGE,"E2250.right"),subQ0,sQuery(id+"F5.wireOp",EDGE,"E2251.top"),subQ1,sQuery(id+"F5.wireOp",EDGE,"E2251.right")])],"isStart":false})});}
            var sketch = newSketch(context, id + "F9", { "sketchPlane" : qUnion([Q0])});
            skLineSegment(sketch, "E2259.bottom", {"start": v(-155, 60) * mm, "end": v(155, 60) * mm});
            skLineSegment(sketch, "E2259.top", {"start": v(-155, -60) * mm, "end": v(155, -60) * mm});
            skLineSegment(sketch, "E2259.left", {"start": v(-155, 60) * mm, "end": v(-155, -60) * mm});
            skLineSegment(sketch, "E2259.right", {"start": v(155, 60) * mm, "end": v(155, -60) * mm});
            skSolve(sketch);
        }
        {
            var Q0;
            Q0 = qSketchRegion(id + "F9", true);
            extrude(context, id + "F10", {"entities" : qUnion([Q0]), "depth" : 3 * mm});
        }
        {
            var Q0;
            Q0=makeQuery(id+"F6.opExtrude","SWEPT_EDGE",EDGE,{"disambiguationData":[OSD([sQuery(id+"F5.wireOp",EDGE,"E2250.bottom"),sQuery(id+"F5.wireOp",EDGE,"E2250.left")])]});
            var Q1;
            Q1=makeQuery(id+"F4.opExtrude","SWEPT_EDGE",EDGE,{"disambiguationData":[OSD([sQuery(id+"F3.wireOp",EDGE,"E2248.top"),sQuery(id+"F3.wireOp",EDGE,"E2248.right")])]});
            var Q2;
            Q2=makeQuery(id+"F10.opExtrude","SWEPT_EDGE",EDGE,{"disambiguationData":[OSD([sQuery(id+"F9.wireOp",EDGE,"E2259.bottom"),sQuery(id+"F9.wireOp",EDGE,"E2259.left")])]});
            var Q3;
            Q3=makeQuery(id+"F4.opExtrude","SWEPT_EDGE",EDGE,{"disambiguationData":[OSD([sQuery(id+"F3.wireOp",EDGE,"E2248.bottom"),sQuery(id+"F3.wireOp",EDGE,"E2248.right")])]});
            var Q4;
            Q4=makeQuery(id+"F6.opExtrude","SWEPT_EDGE",EDGE,{"disambiguationData":[OSD([sQuery(id+"F5.wireOp",EDGE,"E2250.top"),sQuery(id+"F5.wireOp",EDGE,"E2250.left")])]});
            var Q5;
            Q5=makeQuery(id+"F10.opExtrude","SWEPT_EDGE",EDGE,{"disambiguationData":[OSD([sQuery(id+"F9.wireOp",EDGE,"E2259.top"),sQuery(id+"F9.wireOp",EDGE,"E2259.left")])]});
            var Q6;
            Q6=makeQuery(id+"F4.opExtrude","SWEPT_EDGE",EDGE,{"disambiguationData":[OSD([sQuery(id+"F3.wireOp",EDGE,"E2248.bottom"),sQuery(id+"F3.wireOp",EDGE,"E2248.left")])]});
            var Q7;
            Q7=makeQuery(id+"F6.opExtrude","SWEPT_EDGE",EDGE,{"disambiguationData":[OSD([sQuery(id+"F5.wireOp",EDGE,"E2250.top"),sQuery(id+"F5.wireOp",EDGE,"E2250.right")])]});
            var Q8;
            Q8=makeQuery(id+"F10.opExtrude","SWEPT_EDGE",EDGE,{"disambiguationData":[OSD([sQuery(id+"F9.wireOp",EDGE,"E2259.top"),sQuery(id+"F9.wireOp",EDGE,"E2259.right")])]});
            var Q9;
            Q9=makeQuery(id+"F4.opExtrude","SWEPT_EDGE",EDGE,{"disambiguationData":[OSD([sQuery(id+"F3.wireOp",EDGE,"E2248.top"),sQuery(id+"F3.wireOp",EDGE,"E2248.left")])]});
            var Q10;
            Q10=makeQuery(id+"F6.opExtrude","SWEPT_EDGE",EDGE,{"disambiguationData":[OSD([sQuery(id+"F5.wireOp",EDGE,"E2250.bottom"),sQuery(id+"F5.wireOp",EDGE,"E2250.right")])]});
            var Q11;
            Q11=makeQuery(id+"F10.opExtrude","SWEPT_EDGE",EDGE,{"disambiguationData":[OSD([sQuery(id+"F9.wireOp",EDGE,"E2259.bottom"),sQuery(id+"F9.wireOp",EDGE,"E2259.right")])]});
            fillet(context, id + "F11", {"entities" : qUnion([Q0, Q1, Q2, Q3, Q4, Q5, Q6, Q7, Q8, Q9, Q10, Q11]), "radius" : 5 * mm, "tangentPropagation" : true, "allowEdgeOverflow" : false});
        }
        {
            var Q0;
            Q0=makeQuery(id+"F8.boolean.opBoolean","COPY",EDGE,{"derivedFrom":makeQuery(id+"F8.opExtrude","SWEPT_EDGE",EDGE,{"disambiguationData":[OSD([sQuery(id+"F5.wireOp",EDGE,"E2250.top"),sQuery(id+"F7.wireOp",EDGE,"E2254.bottom"),sQuery(id+"F7.wireOp",EDGE,"E2254.right")])]})});
            var Q1;
            Q1=makeQuery(id+"F8.boolean.opBoolean","COPY",EDGE,{"derivedFrom":makeQuery(id+"F8.opExtrude","SWEPT_EDGE",EDGE,{"disambiguationData":[OSD([sQuery(id+"F5.wireOp",EDGE,"E2250.top"),sQuery(id+"F7.wireOp",EDGE,"E2254.bottom"),sQuery(id+"F7.wireOp",EDGE,"E2254.left")])]})});
            fillet(context, id + "F12", {"entities" : qUnion([Q0, Q1]), "radius" : 2 * mm, "tangentPropagation" : true, "allowEdgeOverflow" : false});
        }
        {
            var Q0;
            Q0=makeQuery(id+"F4.boolean.opBoolean","MERGE",FACE,{"derivedFrom":[makeQuery(id+"F2.opExtrude","CAP_FACE",FACE,{"disambiguationData":[OSD([sQuery(id+"F1.wireOp",EDGE,"E1352"),sQuery(id+"F1.wireOp",EDGE,"E1353"),sQuery(id+"F1.wireOp",EDGE,"E1354"),sQuery(id+"F1.wireOp",EDGE,"E1355"),sQuery(id+"F1.wireOp",EDGE,"E1356"),sQuery(id+"F1.wireOp",EDGE,"E1357"),sQuery(id+"F1.wireOp",EDGE,"E1358"),sQuery(id+"F1.wireOp",EDGE,"E1359"),sQuery(id+"F1.wireOp",EDGE,"E1360"),sQuery(id+"F1.wireOp",EDGE,"E1361"),sQuery(id+"F1.wireOp",EDGE,"E1362"),sQuery(id+"F1.wireOp",EDGE,"E1363"),sQuery(id+"F1.wireOp",EDGE,"E1364"),sQuery(id+"F1.wireOp",EDGE,"E1365"),sQuery(id+"F1.wireOp",EDGE,"E1366"),sQuery(id+"F1.wireOp",EDGE,"E1367"),sQuery(id+"F1.wireOp",EDGE,"E1368"),sQuery(id+"F1.wireOp",EDGE,"E1369"),sQuery(id+"F1.wireOp",EDGE,"E1370"),sQuery(id+"F1.wireOp",EDGE,"E1371"),sQuery(id+"F1.wireOp",EDGE,"E1372"),sQuery(id+"F1.wireOp",EDGE,"E1373"),sQuery(id+"F1.wireOp",EDGE,"E1374"),sQuery(id+"F1.wireOp",EDGE,"E1375"),sQuery(id+"F1.wireOp",EDGE,"E1376"),sQuery(id+"F1.wireOp",EDGE,"E1377"),sQuery(id+"F1.wireOp",EDGE,"E1378"),sQuery(id+"F1.wireOp",EDGE,"E1379"),sQuery(id+"F1.wireOp",EDGE,"E1380"),sQuery(id+"F1.wireOp",EDGE,"E1381"),sQuery(id+"F1.wireOp",EDGE,"E1382"),sQuery(id+"F1.wireOp",EDGE,"E1383"),sQuery(id+"F1.wireOp",EDGE,"E1384"),sQuery(id+"F1.wireOp",EDGE,"E1385"),sQuery(id+"F1.wireOp",EDGE,"E1386"),sQuery(id+"F1.wireOp",EDGE,"E1387"),sQuery(id+"F1.wireOp",EDGE,"E1388"),sQuery(id+"F1.wireOp",EDGE,"E1389"),sQuery(id+"F1.wireOp",EDGE,"E1390"),sQuery(id+"F1.wireOp",EDGE,"E1391"),sQuery(id+"F1.wireOp",EDGE,"E1392"),sQuery(id+"F1.wireOp",EDGE,"E1393"),sQuery(id+"F1.wireOp",EDGE,"E1394"),sQuery(id+"F1.wireOp",EDGE,"E1395"),sQuery(id+"F1.wireOp",EDGE,"E1396"),sQuery(id+"F1.wireOp",EDGE,"E1397"),sQuery(id+"F1.wireOp",EDGE,"E1398"),sQuery(id+"F1.wireOp",EDGE,"E1399"),sQuery(id+"F1.wireOp",EDGE,"E1400"),sQuery(id+"F1.wireOp",EDGE,"E1401"),sQuery(id+"F1.wireOp",EDGE,"E1402"),sQuery(id+"F1.wireOp",EDGE,"E1403"),sQuery(id+"F1.wireOp",EDGE,"E1404"),sQuery(id+"F1.wireOp",EDGE,"E1405"),sQuery(id+"F1.wireOp",EDGE,"E1406"),sQuery(id+"F1.wireOp",EDGE,"E1407"),sQuery(id+"F1.wireOp",EDGE,"E1408"),sQuery(id+"F1.wireOp",EDGE,"E1409"),sQuery(id+"F1.wireOp",EDGE,"E1410"),sQuery(id+"F1.wireOp",EDGE,"E1411"),sQuery(id+"F1.wireOp",EDGE,"E1412"),sQuery(id+"F1.wireOp",EDGE,"E1413"),sQuery(id+"F1.wireOp",EDGE,"E1414"),sQuery(id+"F1.wireOp",EDGE,"E1415"),sQuery(id+"F1.wireOp",EDGE,"E1416"),sQuery(id+"F1.wireOp",EDGE,"E1417"),sQuery(id+"F1.wireOp",EDGE,"E1418"),sQuery(id+"F1.wireOp",EDGE,"E1419"),sQuery(id+"F1.wireOp",EDGE,"E1420"),sQuery(id+"F1.wireOp",EDGE,"E1421"),sQuery(id+"F1.wireOp",EDGE,"E1422"),sQuery(id+"F1.wireOp",EDGE,"E1423"),sQuery(id+"F1.wireOp",EDGE,"E1424"),sQuery(id+"F1.wireOp",EDGE,"E1425"),sQuery(id+"F1.wireOp",EDGE,"E1426"),sQuery(id+"F1.wireOp",EDGE,"E1427"),sQuery(id+"F1.wireOp",EDGE,"E1428"),sQuery(id+"F1.wireOp",EDGE,"E1429"),sQuery(id+"F1.wireOp",EDGE,"E1430"),sQuery(id+"F1.wireOp",EDGE,"E1431"),sQuery(id+"F1.wireOp",EDGE,"E1432"),sQuery(id+"F1.wireOp",EDGE,"E1433"),sQuery(id+"F1.wireOp",EDGE,"E1434"),sQuery(id+"F1.wireOp",EDGE,"E1435"),sQuery(id+"F1.wireOp",EDGE,"E1436"),sQuery(id+"F1.wireOp",EDGE,"E1437"),sQuery(id+"F1.wireOp",EDGE,"E1438"),sQuery(id+"F1.wireOp",EDGE,"E1439"),sQuery(id+"F1.wireOp",EDGE,"E1440"),sQuery(id+"F1.wireOp",EDGE,"E1441"),sQuery(id+"F1.wireOp",EDGE,"E1442"),sQuery(id+"F1.wireOp",EDGE,"E1443"),sQuery(id+"F1.wireOp",EDGE,"E1444"),sQuery(id+"F1.wireOp",EDGE,"E1445"),sQuery(id+"F1.wireOp",EDGE,"E1446"),sQuery(id+"F1.wireOp",EDGE,"E1447"),sQuery(id+"F1.wireOp",EDGE,"E1448"),sQuery(id+"F1.wireOp",EDGE,"E1449"),sQuery(id+"F1.wireOp",EDGE,"E1450"),sQuery(id+"F1.wireOp",EDGE,"E1451"),sQuery(id+"F1.wireOp",EDGE,"E1452"),sQuery(id+"F1.wireOp",EDGE,"E1453"),sQuery(id+"F1.wireOp",EDGE,"E1454"),sQuery(id+"F1.wireOp",EDGE,"E1455"),sQuery(id+"F1.wireOp",EDGE,"E1456"),sQuery(id+"F1.wireOp",EDGE,"E1457"),sQuery(id+"F1.wireOp",EDGE,"E1458"),sQuery(id+"F1.wireOp",EDGE,"E1459"),sQuery(id+"F1.wireOp",EDGE,"E1460"),sQuery(id+"F1.wireOp",EDGE,"E1461"),sQuery(id+"F1.wireOp",EDGE,"E1462"),sQuery(id+"F1.wireOp",EDGE,"E1463"),sQuery(id+"F1.wireOp",EDGE,"E1464"),sQuery(id+"F1.wireOp",EDGE,"E1465"),sQuery(id+"F1.wireOp",EDGE,"E1466"),sQuery(id+"F1.wireOp",EDGE,"E1467"),sQuery(id+"F1.wireOp",EDGE,"E1468"),sQuery(id+"F1.wireOp",EDGE,"E1469"),sQuery(id+"F1.wireOp",EDGE,"E1470"),sQuery(id+"F1.wireOp",EDGE,"E1471"),sQuery(id+"F1.wireOp",EDGE,"E1472"),sQuery(id+"F1.wireOp",EDGE,"E1473"),sQuery(id+"F1.wireOp",EDGE,"E1474"),sQuery(id+"F1.wireOp",EDGE,"E1475"),sQuery(id+"F1.wireOp",EDGE,"E1476"),sQuery(id+"F1.wireOp",EDGE,"E1477"),sQuery(id+"F1.wireOp",EDGE,"E1478"),sQuery(id+"F1.wireOp",EDGE,"E1479"),sQuery(id+"F1.wireOp",EDGE,"E1480"),sQuery(id+"F1.wireOp",EDGE,"E1481"),sQuery(id+"F1.wireOp",EDGE,"E1482"),sQuery(id+"F1.wireOp",EDGE,"E1483"),sQuery(id+"F1.wireOp",EDGE,"E1484"),sQuery(id+"F1.wireOp",EDGE,"E1485"),sQuery(id+"F1.wireOp",EDGE,"E1486"),sQuery(id+"F1.wireOp",EDGE,"E1487"),sQuery(id+"F1.wireOp",EDGE,"E1488"),sQuery(id+"F1.wireOp",EDGE,"E1489"),sQuery(id+"F1.wireOp",EDGE,"E1490"),sQuery(id+"F1.wireOp",EDGE,"E1491"),sQuery(id+"F1.wireOp",EDGE,"E1492"),sQuery(id+"F1.wireOp",EDGE,"E1493"),sQuery(id+"F1.wireOp",EDGE,"E1494"),sQuery(id+"F1.wireOp",EDGE,"E1495"),sQuery(id+"F1.wireOp",EDGE,"E1496"),sQuery(id+"F1.wireOp",EDGE,"E1497"),sQuery(id+"F1.wireOp",EDGE,"E1498"),sQuery(id+"F1.wireOp",EDGE,"E1499"),sQuery(id+"F1.wireOp",EDGE,"E1500"),sQuery(id+"F1.wireOp",EDGE,"E1501"),sQuery(id+"F1.wireOp",EDGE,"E1502"),sQuery(id+"F1.wireOp",EDGE,"E1503"),sQuery(id+"F1.wireOp",EDGE,"E1504"),sQuery(id+"F1.wireOp",EDGE,"E1505"),sQuery(id+"F1.wireOp",EDGE,"E1506"),sQuery(id+"F1.wireOp",EDGE,"E1507"),sQuery(id+"F1.wireOp",EDGE,"E1508"),sQuery(id+"F1.wireOp",EDGE,"E1509"),sQuery(id+"F1.wireOp",EDGE,"E1510"),sQuery(id+"F1.wireOp",EDGE,"E1511"),sQuery(id+"F1.wireOp",EDGE,"E1512"),sQuery(id+"F1.wireOp",EDGE,"E1513"),sQuery(id+"F1.wireOp",EDGE,"E1514"),sQuery(id+"F1.wireOp",EDGE,"E1515"),sQuery(id+"F1.wireOp",EDGE,"E1516"),sQuery(id+"F1.wireOp",EDGE,"E1517"),sQuery(id+"F1.wireOp",EDGE,"E1518"),sQuery(id+"F1.wireOp",EDGE,"E1519"),sQuery(id+"F1.wireOp",EDGE,"E1520"),sQuery(id+"F1.wireOp",EDGE,"E1521"),sQuery(id+"F1.wireOp",EDGE,"E1522"),sQuery(id+"F1.wireOp",EDGE,"E1523"),sQuery(id+"F1.wireOp",EDGE,"E1524"),sQuery(id+"F1.wireOp",EDGE,"E1525"),sQuery(id+"F1.wireOp",EDGE,"E1526"),sQuery(id+"F1.wireOp",EDGE,"E1527"),sQuery(id+"F1.wireOp",EDGE,"E1528"),sQuery(id+"F1.wireOp",EDGE,"E1529"),sQuery(id+"F1.wireOp",EDGE,"E1530"),sQuery(id+"F1.wireOp",EDGE,"E1531"),sQuery(id+"F1.wireOp",EDGE,"E1532"),sQuery(id+"F1.wireOp",EDGE,"E1533"),sQuery(id+"F1.wireOp",EDGE,"E1534"),sQuery(id+"F1.wireOp",EDGE,"E1535"),sQuery(id+"F1.wireOp",EDGE,"E1536"),sQuery(id+"F1.wireOp",EDGE,"E1537"),sQuery(id+"F1.wireOp",EDGE,"E1538"),sQuery(id+"F1.wireOp",EDGE,"E1539"),sQuery(id+"F1.wireOp",EDGE,"E1540"),sQuery(id+"F1.wireOp",EDGE,"E1541"),sQuery(id+"F1.wireOp",EDGE,"E1542"),sQuery(id+"F1.wireOp",EDGE,"E1543"),sQuery(id+"F1.wireOp",EDGE,"E1544"),sQuery(id+"F1.wireOp",EDGE,"E1545"),sQuery(id+"F1.wireOp",EDGE,"E1546"),sQuery(id+"F1.wireOp",EDGE,"E1547"),sQuery(id+"F1.wireOp",EDGE,"E1548"),sQuery(id+"F1.wireOp",EDGE,"E1549"),sQuery(id+"F1.wireOp",EDGE,"E1550"),sQuery(id+"F1.wireOp",EDGE,"E1551"),sQuery(id+"F1.wireOp",EDGE,"E1552"),sQuery(id+"F1.wireOp",EDGE,"E1553"),sQuery(id+"F1.wireOp",EDGE,"E1554"),sQuery(id+"F1.wireOp",EDGE,"E1555"),sQuery(id+"F1.wireOp",EDGE,"E1556"),sQuery(id+"F1.wireOp",EDGE,"E1557"),sQuery(id+"F1.wireOp",EDGE,"E1558"),sQuery(id+"F1.wireOp",EDGE,"E1559"),sQuery(id+"F1.wireOp",EDGE,"E1560"),sQuery(id+"F1.wireOp",EDGE,"E1561"),sQuery(id+"F1.wireOp",EDGE,"E1562"),sQuery(id+"F1.wireOp",EDGE,"E1563"),sQuery(id+"F1.wireOp",EDGE,"E1564"),sQuery(id+"F1.wireOp",EDGE,"E1565"),sQuery(id+"F1.wireOp",EDGE,"E1566"),sQuery(id+"F1.wireOp",EDGE,"E1567"),sQuery(id+"F1.wireOp",EDGE,"E1568"),sQuery(id+"F1.wireOp",EDGE,"E1569"),sQuery(id+"F1.wireOp",EDGE,"E1570"),sQuery(id+"F1.wireOp",EDGE,"E1571"),sQuery(id+"F1.wireOp",EDGE,"E1572"),sQuery(id+"F1.wireOp",EDGE,"E1573"),sQuery(id+"F1.wireOp",EDGE,"E1574"),sQuery(id+"F1.wireOp",EDGE,"E1575"),sQuery(id+"F1.wireOp",EDGE,"E1576"),sQuery(id+"F1.wireOp",EDGE,"E1577"),sQuery(id+"F1.wireOp",EDGE,"E1578"),sQuery(id+"F1.wireOp",EDGE,"E1579"),sQuery(id+"F1.wireOp",EDGE,"E1580"),sQuery(id+"F1.wireOp",EDGE,"E1581"),sQuery(id+"F1.wireOp",EDGE,"E1582"),sQuery(id+"F1.wireOp",EDGE,"E1583"),sQuery(id+"F1.wireOp",EDGE,"E1584"),sQuery(id+"F1.wireOp",EDGE,"E1585"),sQuery(id+"F1.wireOp",EDGE,"E1586"),sQuery(id+"F1.wireOp",EDGE,"E1587"),sQuery(id+"F1.wireOp",EDGE,"E1588"),sQuery(id+"F1.wireOp",EDGE,"E1589"),sQuery(id+"F1.wireOp",EDGE,"E1590"),sQuery(id+"F1.wireOp",EDGE,"E1591"),sQuery(id+"F1.wireOp",EDGE,"E1592"),sQuery(id+"F1.wireOp",EDGE,"E1593"),sQuery(id+"F1.wireOp",EDGE,"E1594"),sQuery(id+"F1.wireOp",EDGE,"E1595"),sQuery(id+"F1.wireOp",EDGE,"E1596"),sQuery(id+"F1.wireOp",EDGE,"E1597"),sQuery(id+"F1.wireOp",EDGE,"E1598"),sQuery(id+"F1.wireOp",EDGE,"E1599"),sQuery(id+"F1.wireOp",EDGE,"E1600"),sQuery(id+"F1.wireOp",EDGE,"E1601"),sQuery(id+"F1.wireOp",EDGE,"E1602"),sQuery(id+"F1.wireOp",EDGE,"E1603"),sQuery(id+"F1.wireOp",EDGE,"E1604"),sQuery(id+"F1.wireOp",EDGE,"E1605"),sQuery(id+"F1.wireOp",EDGE,"E1606"),sQuery(id+"F1.wireOp",EDGE,"E1607"),sQuery(id+"F1.wireOp",EDGE,"E1608"),sQuery(id+"F1.wireOp",EDGE,"E1609"),sQuery(id+"F1.wireOp",EDGE,"E1610"),sQuery(id+"F1.wireOp",EDGE,"E1611"),sQuery(id+"F1.wireOp",EDGE,"E1612"),sQuery(id+"F1.wireOp",EDGE,"E1613"),sQuery(id+"F1.wireOp",EDGE,"E1614"),sQuery(id+"F1.wireOp",EDGE,"E1615"),sQuery(id+"F1.wireOp",EDGE,"E1616"),sQuery(id+"F1.wireOp",EDGE,"E1617"),sQuery(id+"F1.wireOp",EDGE,"E1618"),sQuery(id+"F1.wireOp",EDGE,"E1619"),sQuery(id+"F1.wireOp",EDGE,"E1620"),sQuery(id+"F1.wireOp",EDGE,"E1621"),sQuery(id+"F1.wireOp",EDGE,"E1622"),sQuery(id+"F1.wireOp",EDGE,"E1623"),sQuery(id+"F1.wireOp",EDGE,"E1624"),sQuery(id+"F1.wireOp",EDGE,"E1625"),sQuery(id+"F1.wireOp",EDGE,"E1626"),sQuery(id+"F1.wireOp",EDGE,"E1627"),sQuery(id+"F1.wireOp",EDGE,"E1628"),sQuery(id+"F1.wireOp",EDGE,"E1629"),sQuery(id+"F1.wireOp",EDGE,"E1630"),sQuery(id+"F1.wireOp",EDGE,"E1631"),sQuery(id+"F1.wireOp",EDGE,"E1632"),sQuery(id+"F1.wireOp",EDGE,"E1633"),sQuery(id+"F1.wireOp",EDGE,"E1634"),sQuery(id+"F1.wireOp",EDGE,"E1635"),sQuery(id+"F1.wireOp",EDGE,"E1636"),sQuery(id+"F1.wireOp",EDGE,"E1637"),sQuery(id+"F1.wireOp",EDGE,"E1638"),sQuery(id+"F1.wireOp",EDGE,"E1639"),sQuery(id+"F1.wireOp",EDGE,"E1640"),sQuery(id+"F1.wireOp",EDGE,"E1641"),sQuery(id+"F1.wireOp",EDGE,"E1642"),sQuery(id+"F1.wireOp",EDGE,"E1643"),sQuery(id+"F1.wireOp",EDGE,"E1644"),sQuery(id+"F1.wireOp",EDGE,"E1645"),sQuery(id+"F1.wireOp",EDGE,"E1646"),sQuery(id+"F1.wireOp",EDGE,"E1647"),sQuery(id+"F1.wireOp",EDGE,"E1648"),sQuery(id+"F1.wireOp",EDGE,"E1649"),sQuery(id+"F1.wireOp",EDGE,"E1650"),sQuery(id+"F1.wireOp",EDGE,"E1651"),sQuery(id+"F1.wireOp",EDGE,"E1652"),sQuery(id+"F1.wireOp",EDGE,"E1653"),sQuery(id+"F1.wireOp",EDGE,"E1654"),sQuery(id+"F1.wireOp",EDGE,"E1655"),sQuery(id+"F1.wireOp",EDGE,"E1656"),sQuery(id+"F1.wireOp",EDGE,"E1657"),sQuery(id+"F1.wireOp",EDGE,"E1658"),sQuery(id+"F1.wireOp",EDGE,"E1659"),sQuery(id+"F1.wireOp",EDGE,"E1660"),sQuery(id+"F1.wireOp",EDGE,"E1661"),sQuery(id+"F1.wireOp",EDGE,"E1662"),sQuery(id+"F1.wireOp",EDGE,"E1663"),sQuery(id+"F1.wireOp",EDGE,"E1664"),sQuery(id+"F1.wireOp",EDGE,"E1665"),sQuery(id+"F1.wireOp",EDGE,"E1666"),sQuery(id+"F1.wireOp",EDGE,"E1667"),sQuery(id+"F1.wireOp",EDGE,"E1668"),sQuery(id+"F1.wireOp",EDGE,"E1669"),sQuery(id+"F1.wireOp",EDGE,"E1670"),sQuery(id+"F1.wireOp",EDGE,"E1671"),sQuery(id+"F1.wireOp",EDGE,"E1672"),sQuery(id+"F1.wireOp",EDGE,"E1673"),sQuery(id+"F1.wireOp",EDGE,"E1674"),sQuery(id+"F1.wireOp",EDGE,"E1675"),sQuery(id+"F1.wireOp",EDGE,"E1676"),sQuery(id+"F1.wireOp",EDGE,"E1677"),sQuery(id+"F1.wireOp",EDGE,"E1678"),sQuery(id+"F1.wireOp",EDGE,"E1679"),sQuery(id+"F1.wireOp",EDGE,"E1680"),sQuery(id+"F1.wireOp",EDGE,"E1681"),sQuery(id+"F1.wireOp",EDGE,"E1682"),sQuery(id+"F1.wireOp",EDGE,"E1683"),sQuery(id+"F1.wireOp",EDGE,"E1684"),sQuery(id+"F1.wireOp",EDGE,"E1685"),sQuery(id+"F1.wireOp",EDGE,"E1686"),sQuery(id+"F1.wireOp",EDGE,"E1687"),sQuery(id+"F1.wireOp",EDGE,"E1688"),sQuery(id+"F1.wireOp",EDGE,"E1689"),sQuery(id+"F1.wireOp",EDGE,"E1690"),sQuery(id+"F1.wireOp",EDGE,"E1691"),sQuery(id+"F1.wireOp",EDGE,"E1692"),sQuery(id+"F1.wireOp",EDGE,"E1693"),sQuery(id+"F1.wireOp",EDGE,"E1694"),sQuery(id+"F1.wireOp",EDGE,"E1695"),sQuery(id+"F1.wireOp",EDGE,"E1696"),sQuery(id+"F1.wireOp",EDGE,"E1697"),sQuery(id+"F1.wireOp",EDGE,"E1698"),sQuery(id+"F1.wireOp",EDGE,"E1699"),sQuery(id+"F1.wireOp",EDGE,"E1700"),sQuery(id+"F1.wireOp",EDGE,"E1701"),sQuery(id+"F1.wireOp",EDGE,"E1702"),sQuery(id+"F1.wireOp",EDGE,"E1703"),sQuery(id+"F1.wireOp",EDGE,"E1704"),sQuery(id+"F1.wireOp",EDGE,"E1705"),sQuery(id+"F1.wireOp",EDGE,"E1706"),sQuery(id+"F1.wireOp",EDGE,"E1707"),sQuery(id+"F1.wireOp",EDGE,"E1708"),sQuery(id+"F1.wireOp",EDGE,"E1709"),sQuery(id+"F1.wireOp",EDGE,"E1710"),sQuery(id+"F1.wireOp",EDGE,"E1711"),sQuery(id+"F1.wireOp",EDGE,"E1712"),sQuery(id+"F1.wireOp",EDGE,"E1713"),sQuery(id+"F1.wireOp",EDGE,"E1714"),sQuery(id+"F1.wireOp",EDGE,"E1715"),sQuery(id+"F1.wireOp",EDGE,"E1716"),sQuery(id+"F1.wireOp",EDGE,"E1717"),sQuery(id+"F1.wireOp",EDGE,"E1718"),sQuery(id+"F1.wireOp",EDGE,"E1719"),sQuery(id+"F1.wireOp",EDGE,"E1720"),sQuery(id+"F1.wireOp",EDGE,"E1721"),sQuery(id+"F1.wireOp",EDGE,"E1722"),sQuery(id+"F1.wireOp",EDGE,"E1723"),sQuery(id+"F1.wireOp",EDGE,"E1724"),sQuery(id+"F1.wireOp",EDGE,"E1725"),sQuery(id+"F1.wireOp",EDGE,"E1726"),sQuery(id+"F1.wireOp",EDGE,"E1727"),sQuery(id+"F1.wireOp",EDGE,"E1728"),sQuery(id+"F1.wireOp",EDGE,"E1729"),sQuery(id+"F1.wireOp",EDGE,"E1730"),sQuery(id+"F1.wireOp",EDGE,"E1731"),sQuery(id+"F1.wireOp",EDGE,"E1732"),sQuery(id+"F1.wireOp",EDGE,"E1733"),sQuery(id+"F1.wireOp",EDGE,"E1734"),sQuery(id+"F1.wireOp",EDGE,"E1735"),sQuery(id+"F1.wireOp",EDGE,"E1736"),sQuery(id+"F1.wireOp",EDGE,"E1737"),sQuery(id+"F1.wireOp",EDGE,"E1738"),sQuery(id+"F1.wireOp",EDGE,"E1739"),sQuery(id+"F1.wireOp",EDGE,"E1740"),sQuery(id+"F1.wireOp",EDGE,"E1741"),sQuery(id+"F1.wireOp",EDGE,"E1742"),sQuery(id+"F1.wireOp",EDGE,"E1743"),sQuery(id+"F1.wireOp",EDGE,"E1744"),sQuery(id+"F1.wireOp",EDGE,"E1745"),sQuery(id+"F1.wireOp",EDGE,"E1746"),sQuery(id+"F1.wireOp",EDGE,"E1747"),sQuery(id+"F1.wireOp",EDGE,"E1748"),sQuery(id+"F1.wireOp",EDGE,"E1749"),sQuery(id+"F1.wireOp",EDGE,"E1750"),sQuery(id+"F1.wireOp",EDGE,"E1751"),sQuery(id+"F1.wireOp",EDGE,"E1752"),sQuery(id+"F1.wireOp",EDGE,"E1753"),sQuery(id+"F1.wireOp",EDGE,"E1754"),sQuery(id+"F1.wireOp",EDGE,"E1755"),sQuery(id+"F1.wireOp",EDGE,"E1756"),sQuery(id+"F1.wireOp",EDGE,"E1757"),sQuery(id+"F1.wireOp",EDGE,"E1758"),sQuery(id+"F1.wireOp",EDGE,"E1759"),sQuery(id+"F1.wireOp",EDGE,"E1760"),sQuery(id+"F1.wireOp",EDGE,"E1761"),sQuery(id+"F1.wireOp",EDGE,"E1762"),sQuery(id+"F1.wireOp",EDGE,"E1763"),sQuery(id+"F1.wireOp",EDGE,"E1764"),sQuery(id+"F1.wireOp",EDGE,"E1765"),sQuery(id+"F1.wireOp",EDGE,"E1766"),sQuery(id+"F1.wireOp",EDGE,"E1767"),sQuery(id+"F1.wireOp",EDGE,"E1768"),sQuery(id+"F1.wireOp",EDGE,"E1769"),sQuery(id+"F1.wireOp",EDGE,"E1770"),sQuery(id+"F1.wireOp",EDGE,"E1771"),sQuery(id+"F1.wireOp",EDGE,"E1772"),sQuery(id+"F1.wireOp",EDGE,"E1773"),sQuery(id+"F1.wireOp",EDGE,"E1774"),sQuery(id+"F1.wireOp",EDGE,"E1775"),sQuery(id+"F1.wireOp",EDGE,"E1776"),sQuery(id+"F1.wireOp",EDGE,"E1777"),sQuery(id+"F1.wireOp",EDGE,"E1778"),sQuery(id+"F1.wireOp",EDGE,"E1779"),sQuery(id+"F1.wireOp",EDGE,"E1780"),sQuery(id+"F1.wireOp",EDGE,"E1781"),sQuery(id+"F1.wireOp",EDGE,"E1782"),sQuery(id+"F1.wireOp",EDGE,"E1783"),sQuery(id+"F1.wireOp",EDGE,"E1784"),sQuery(id+"F1.wireOp",EDGE,"E1785"),sQuery(id+"F1.wireOp",EDGE,"E1786"),sQuery(id+"F1.wireOp",EDGE,"E1787"),sQuery(id+"F1.wireOp",EDGE,"E1788"),sQuery(id+"F1.wireOp",EDGE,"E1789"),sQuery(id+"F1.wireOp",EDGE,"E1790"),sQuery(id+"F1.wireOp",EDGE,"E1791"),sQuery(id+"F1.wireOp",EDGE,"E1792"),sQuery(id+"F1.wireOp",EDGE,"E1793"),sQuery(id+"F1.wireOp",EDGE,"E1794"),sQuery(id+"F1.wireOp",EDGE,"E1795"),sQuery(id+"F1.wireOp",EDGE,"E1796"),sQuery(id+"F1.wireOp",EDGE,"E1797"),sQuery(id+"F1.wireOp",EDGE,"E1798"),sQuery(id+"F1.wireOp",EDGE,"E1799"),sQuery(id+"F1.wireOp",EDGE,"E1800"),sQuery(id+"F1.wireOp",EDGE,"E1801"),sQuery(id+"F1.wireOp",EDGE,"E1802"),sQuery(id+"F1.wireOp",EDGE,"E1803"),sQuery(id+"F1.wireOp",EDGE,"E1804"),sQuery(id+"F1.wireOp",EDGE,"E1805"),sQuery(id+"F1.wireOp",EDGE,"E1806"),sQuery(id+"F1.wireOp",EDGE,"E1807"),sQuery(id+"F1.wireOp",EDGE,"E1808"),sQuery(id+"F1.wireOp",EDGE,"E1809"),sQuery(id+"F1.wireOp",EDGE,"E1810"),sQuery(id+"F1.wireOp",EDGE,"E1811"),sQuery(id+"F1.wireOp",EDGE,"E1812"),sQuery(id+"F1.wireOp",EDGE,"E1813"),sQuery(id+"F1.wireOp",EDGE,"E1814"),sQuery(id+"F1.wireOp",EDGE,"E1815"),sQuery(id+"F1.wireOp",EDGE,"E1816"),sQuery(id+"F1.wireOp",EDGE,"E1817"),sQuery(id+"F1.wireOp",EDGE,"E1818"),sQuery(id+"F1.wireOp",EDGE,"E1819"),sQuery(id+"F1.wireOp",EDGE,"E1820"),sQuery(id+"F1.wireOp",EDGE,"E1821"),sQuery(id+"F1.wireOp",EDGE,"E1822"),sQuery(id+"F1.wireOp",EDGE,"E1823"),sQuery(id+"F1.wireOp",EDGE,"E1824"),sQuery(id+"F1.wireOp",EDGE,"E1825"),sQuery(id+"F1.wireOp",EDGE,"E1826"),sQuery(id+"F1.wireOp",EDGE,"E1827"),sQuery(id+"F1.wireOp",EDGE,"E1828"),sQuery(id+"F1.wireOp",EDGE,"E1829"),sQuery(id+"F1.wireOp",EDGE,"E1830"),sQuery(id+"F1.wireOp",EDGE,"E1831"),sQuery(id+"F1.wireOp",EDGE,"E1832"),sQuery(id+"F1.wireOp",EDGE,"E1833"),sQuery(id+"F1.wireOp",EDGE,"E1834"),sQuery(id+"F1.wireOp",EDGE,"E1835"),sQuery(id+"F1.wireOp",EDGE,"E1836"),sQuery(id+"F1.wireOp",EDGE,"E1837"),sQuery(id+"F1.wireOp",EDGE,"E1838"),sQuery(id+"F1.wireOp",EDGE,"E1839"),sQuery(id+"F1.wireOp",EDGE,"E1840"),sQuery(id+"F1.wireOp",EDGE,"E1841"),sQuery(id+"F1.wireOp",EDGE,"E1842"),sQuery(id+"F1.wireOp",EDGE,"E1843"),sQuery(id+"F1.wireOp",EDGE,"E1844"),sQuery(id+"F1.wireOp",EDGE,"E1845"),sQuery(id+"F1.wireOp",EDGE,"E1846"),sQuery(id+"F1.wireOp",EDGE,"E1847"),sQuery(id+"F1.wireOp",EDGE,"E1848"),sQuery(id+"F1.wireOp",EDGE,"E1849"),sQuery(id+"F1.wireOp",EDGE,"E1850"),sQuery(id+"F1.wireOp",EDGE,"E1851"),sQuery(id+"F1.wireOp",EDGE,"E1852"),sQuery(id+"F1.wireOp",EDGE,"E1853"),sQuery(id+"F1.wireOp",EDGE,"E1854"),sQuery(id+"F1.wireOp",EDGE,"E1855"),sQuery(id+"F1.wireOp",EDGE,"E1856"),sQuery(id+"F1.wireOp",EDGE,"E1857"),sQuery(id+"F1.wireOp",EDGE,"E1858"),sQuery(id+"F1.wireOp",EDGE,"E1859"),sQuery(id+"F1.wireOp",EDGE,"E1860"),sQuery(id+"F1.wireOp",EDGE,"E1861"),sQuery(id+"F1.wireOp",EDGE,"E1862"),sQuery(id+"F1.wireOp",EDGE,"E1863"),sQuery(id+"F1.wireOp",EDGE,"E1864"),sQuery(id+"F1.wireOp",EDGE,"E1865"),sQuery(id+"F1.wireOp",EDGE,"E1866"),sQuery(id+"F1.wireOp",EDGE,"E1867"),sQuery(id+"F1.wireOp",EDGE,"E1868"),sQuery(id+"F1.wireOp",EDGE,"E1869"),sQuery(id+"F1.wireOp",EDGE,"E1870"),sQuery(id+"F1.wireOp",EDGE,"E1871"),sQuery(id+"F1.wireOp",EDGE,"E1872"),sQuery(id+"F1.wireOp",EDGE,"E1873"),sQuery(id+"F1.wireOp",EDGE,"E1874"),sQuery(id+"F1.wireOp",EDGE,"E1875"),sQuery(id+"F1.wireOp",EDGE,"E1876"),sQuery(id+"F1.wireOp",EDGE,"E1877"),sQuery(id+"F1.wireOp",EDGE,"E1878"),sQuery(id+"F1.wireOp",EDGE,"E1879"),sQuery(id+"F1.wireOp",EDGE,"E1880"),sQuery(id+"F1.wireOp",EDGE,"E1881"),sQuery(id+"F1.wireOp",EDGE,"E1882"),sQuery(id+"F1.wireOp",EDGE,"E1883"),sQuery(id+"F1.wireOp",EDGE,"E1884"),sQuery(id+"F1.wireOp",EDGE,"E1885"),sQuery(id+"F1.wireOp",EDGE,"E1886"),sQuery(id+"F1.wireOp",EDGE,"E1887"),sQuery(id+"F1.wireOp",EDGE,"E1888"),sQuery(id+"F1.wireOp",EDGE,"E1889"),sQuery(id+"F1.wireOp",EDGE,"E1890"),sQuery(id+"F1.wireOp",EDGE,"E1891"),sQuery(id+"F1.wireOp",EDGE,"E1892"),sQuery(id+"F1.wireOp",EDGE,"E1893"),sQuery(id+"F1.wireOp",EDGE,"E1894"),sQuery(id+"F1.wireOp",EDGE,"E1895"),sQuery(id+"F1.wireOp",EDGE,"E1896"),sQuery(id+"F1.wireOp",EDGE,"E1897"),sQuery(id+"F1.wireOp",EDGE,"E1898"),sQuery(id+"F1.wireOp",EDGE,"E1899"),sQuery(id+"F1.wireOp",EDGE,"E1900"),sQuery(id+"F1.wireOp",EDGE,"E1901"),sQuery(id+"F1.wireOp",EDGE,"E1902"),sQuery(id+"F1.wireOp",EDGE,"E1903"),sQuery(id+"F1.wireOp",EDGE,"E1904"),sQuery(id+"F1.wireOp",EDGE,"E1905"),sQuery(id+"F1.wireOp",EDGE,"E1906"),sQuery(id+"F1.wireOp",EDGE,"E1907"),sQuery(id+"F1.wireOp",EDGE,"E1908"),sQuery(id+"F1.wireOp",EDGE,"E1909"),sQuery(id+"F1.wireOp",EDGE,"E1910"),sQuery(id+"F1.wireOp",EDGE,"E1911"),sQuery(id+"F1.wireOp",EDGE,"E1912"),sQuery(id+"F1.wireOp",EDGE,"E1913"),sQuery(id+"F1.wireOp",EDGE,"E1914"),sQuery(id+"F1.wireOp",EDGE,"E1915"),sQuery(id+"F1.wireOp",EDGE,"E1916"),sQuery(id+"F1.wireOp",EDGE,"E1917"),sQuery(id+"F1.wireOp",EDGE,"E1918"),sQuery(id+"F1.wireOp",EDGE,"E1919"),sQuery(id+"F1.wireOp",EDGE,"E1920"),sQuery(id+"F1.wireOp",EDGE,"E1921"),sQuery(id+"F1.wireOp",EDGE,"E1922"),sQuery(id+"F1.wireOp",EDGE,"E1923"),sQuery(id+"F1.wireOp",EDGE,"E1924"),sQuery(id+"F1.wireOp",EDGE,"E1925"),sQuery(id+"F1.wireOp",EDGE,"E1926"),sQuery(id+"F1.wireOp",EDGE,"E1927"),sQuery(id+"F1.wireOp",EDGE,"E1928"),sQuery(id+"F1.wireOp",EDGE,"E1929"),sQuery(id+"F1.wireOp",EDGE,"E1930"),sQuery(id+"F1.wireOp",EDGE,"E1931"),sQuery(id+"F1.wireOp",EDGE,"E1932"),sQuery(id+"F1.wireOp",EDGE,"E1933"),sQuery(id+"F1.wireOp",EDGE,"E1934"),sQuery(id+"F1.wireOp",EDGE,"E1935"),sQuery(id+"F1.wireOp",EDGE,"E1936"),sQuery(id+"F1.wireOp",EDGE,"E1937"),sQuery(id+"F1.wireOp",EDGE,"E1938"),sQuery(id+"F1.wireOp",EDGE,"E1939"),sQuery(id+"F1.wireOp",EDGE,"E1940"),sQuery(id+"F1.wireOp",EDGE,"E1941"),sQuery(id+"F1.wireOp",EDGE,"E1942"),sQuery(id+"F1.wireOp",EDGE,"E1943"),sQuery(id+"F1.wireOp",EDGE,"E1944"),sQuery(id+"F1.wireOp",EDGE,"E1945"),sQuery(id+"F1.wireOp",EDGE,"E1946"),sQuery(id+"F1.wireOp",EDGE,"E1947"),sQuery(id+"F1.wireOp",EDGE,"E1948"),sQuery(id+"F1.wireOp",EDGE,"E1949"),sQuery(id+"F1.wireOp",EDGE,"E1950"),sQuery(id+"F1.wireOp",EDGE,"E1951"),sQuery(id+"F1.wireOp",EDGE,"E1952"),sQuery(id+"F1.wireOp",EDGE,"E1953"),sQuery(id+"F1.wireOp",EDGE,"E1954"),sQuery(id+"F1.wireOp",EDGE,"E1955"),sQuery(id+"F1.wireOp",EDGE,"E1956"),sQuery(id+"F1.wireOp",EDGE,"E1957"),sQuery(id+"F1.wireOp",EDGE,"E1958"),sQuery(id+"F1.wireOp",EDGE,"E1959"),sQuery(id+"F1.wireOp",EDGE,"E1960"),sQuery(id+"F1.wireOp",EDGE,"E1961"),sQuery(id+"F1.wireOp",EDGE,"E1962"),sQuery(id+"F1.wireOp",EDGE,"E1963"),sQuery(id+"F1.wireOp",EDGE,"E1964"),sQuery(id+"F1.wireOp",EDGE,"E1965"),sQuery(id+"F1.wireOp",EDGE,"E1966"),sQuery(id+"F1.wireOp",EDGE,"E1967"),sQuery(id+"F1.wireOp",EDGE,"E1968"),sQuery(id+"F1.wireOp",EDGE,"E1969"),sQuery(id+"F1.wireOp",EDGE,"E1970"),sQuery(id+"F1.wireOp",EDGE,"E1971"),sQuery(id+"F1.wireOp",EDGE,"E1972"),sQuery(id+"F1.wireOp",EDGE,"E1973"),sQuery(id+"F1.wireOp",EDGE,"E1974"),sQuery(id+"F1.wireOp",EDGE,"E1975"),sQuery(id+"F1.wireOp",EDGE,"E1976"),sQuery(id+"F1.wireOp",EDGE,"E1977"),sQuery(id+"F1.wireOp",EDGE,"E1978"),sQuery(id+"F1.wireOp",EDGE,"E1979"),sQuery(id+"F1.wireOp",EDGE,"E1980"),sQuery(id+"F1.wireOp",EDGE,"E1981"),sQuery(id+"F1.wireOp",EDGE,"E1982"),sQuery(id+"F1.wireOp",EDGE,"E1983"),sQuery(id+"F1.wireOp",EDGE,"E1984"),sQuery(id+"F1.wireOp",EDGE,"E1985"),sQuery(id+"F1.wireOp",EDGE,"E1986"),sQuery(id+"F1.wireOp",EDGE,"E1987"),sQuery(id+"F1.wireOp",EDGE,"E1988"),sQuery(id+"F1.wireOp",EDGE,"E1989"),sQuery(id+"F1.wireOp",EDGE,"E1990"),sQuery(id+"F1.wireOp",EDGE,"E1991"),sQuery(id+"F1.wireOp",EDGE,"E1992"),sQuery(id+"F1.wireOp",EDGE,"E1993"),sQuery(id+"F1.wireOp",EDGE,"E1994"),sQuery(id+"F1.wireOp",EDGE,"E1995"),sQuery(id+"F1.wireOp",EDGE,"E1996"),sQuery(id+"F1.wireOp",EDGE,"E1997"),sQuery(id+"F1.wireOp",EDGE,"E1998"),sQuery(id+"F1.wireOp",EDGE,"E1999"),sQuery(id+"F1.wireOp",EDGE,"E2000"),sQuery(id+"F1.wireOp",EDGE,"E2001"),sQuery(id+"F1.wireOp",EDGE,"E2002"),sQuery(id+"F1.wireOp",EDGE,"E2003"),sQuery(id+"F1.wireOp",EDGE,"E2004"),sQuery(id+"F1.wireOp",EDGE,"E2005"),sQuery(id+"F1.wireOp",EDGE,"E2006"),sQuery(id+"F1.wireOp",EDGE,"E2007"),sQuery(id+"F1.wireOp",EDGE,"E2008"),sQuery(id+"F1.wireOp",EDGE,"E2009"),sQuery(id+"F1.wireOp",EDGE,"E2010"),sQuery(id+"F1.wireOp",EDGE,"E2011"),sQuery(id+"F1.wireOp",EDGE,"E2012"),sQuery(id+"F1.wireOp",EDGE,"E2013"),sQuery(id+"F1.wireOp",EDGE,"E2014"),sQuery(id+"F1.wireOp",EDGE,"E2015"),sQuery(id+"F1.wireOp",EDGE,"E2016"),sQuery(id+"F1.wireOp",EDGE,"E2017"),sQuery(id+"F1.wireOp",EDGE,"E2018"),sQuery(id+"F1.wireOp",EDGE,"E2019"),sQuery(id+"F1.wireOp",EDGE,"E2020"),sQuery(id+"F1.wireOp",EDGE,"E2021"),sQuery(id+"F1.wireOp",EDGE,"E2022"),sQuery(id+"F1.wireOp",EDGE,"E2023"),sQuery(id+"F1.wireOp",EDGE,"E2024"),sQuery(id+"F1.wireOp",EDGE,"E2025"),sQuery(id+"F1.wireOp",EDGE,"E2026"),sQuery(id+"F1.wireOp",EDGE,"E2027"),sQuery(id+"F1.wireOp",EDGE,"E2028"),sQuery(id+"F1.wireOp",EDGE,"E2029"),sQuery(id+"F1.wireOp",EDGE,"E2030"),sQuery(id+"F1.wireOp",EDGE,"E2031"),sQuery(id+"F1.wireOp",EDGE,"E2032"),sQuery(id+"F1.wireOp",EDGE,"E2033"),sQuery(id+"F1.wireOp",EDGE,"E2034"),sQuery(id+"F1.wireOp",EDGE,"E2035"),sQuery(id+"F1.wireOp",EDGE,"E2036"),sQuery(id+"F1.wireOp",EDGE,"E2037"),sQuery(id+"F1.wireOp",EDGE,"E2038"),sQuery(id+"F1.wireOp",EDGE,"E2039"),sQuery(id+"F1.wireOp",EDGE,"E2040"),sQuery(id+"F1.wireOp",EDGE,"E2041"),sQuery(id+"F1.wireOp",EDGE,"E2042"),sQuery(id+"F1.wireOp",EDGE,"E2043"),sQuery(id+"F1.wireOp",EDGE,"E2044"),sQuery(id+"F1.wireOp",EDGE,"E2045"),sQuery(id+"F1.wireOp",EDGE,"E2046"),sQuery(id+"F1.wireOp",EDGE,"E2047"),sQuery(id+"F1.wireOp",EDGE,"E2048"),sQuery(id+"F1.wireOp",EDGE,"E2049"),sQuery(id+"F1.wireOp",EDGE,"E2050"),sQuery(id+"F1.wireOp",EDGE,"E2051"),sQuery(id+"F1.wireOp",EDGE,"E2052"),sQuery(id+"F1.wireOp",EDGE,"E2053"),sQuery(id+"F1.wireOp",EDGE,"E2054"),sQuery(id+"F1.wireOp",EDGE,"E2055"),sQuery(id+"F1.wireOp",EDGE,"E2056"),sQuery(id+"F1.wireOp",EDGE,"E2057"),sQuery(id+"F1.wireOp",EDGE,"E2058"),sQuery(id+"F1.wireOp",EDGE,"E2059"),sQuery(id+"F1.wireOp",EDGE,"E2060"),sQuery(id+"F1.wireOp",EDGE,"E2061"),sQuery(id+"F1.wireOp",EDGE,"E2062"),sQuery(id+"F1.wireOp",EDGE,"E2063"),sQuery(id+"F1.wireOp",EDGE,"E2064"),sQuery(id+"F1.wireOp",EDGE,"E2065"),sQuery(id+"F1.wireOp",EDGE,"E2066"),sQuery(id+"F1.wireOp",EDGE,"E2067"),sQuery(id+"F1.wireOp",EDGE,"E2068"),sQuery(id+"F1.wireOp",EDGE,"E2069"),sQuery(id+"F1.wireOp",EDGE,"E2070"),sQuery(id+"F1.wireOp",EDGE,"E2071"),sQuery(id+"F1.wireOp",EDGE,"E2072"),sQuery(id+"F1.wireOp",EDGE,"E2073"),sQuery(id+"F1.wireOp",EDGE,"E2074"),sQuery(id+"F1.wireOp",EDGE,"E2075"),sQuery(id+"F1.wireOp",EDGE,"E2076"),sQuery(id+"F1.wireOp",EDGE,"E2077"),sQuery(id+"F1.wireOp",EDGE,"E2078"),sQuery(id+"F1.wireOp",EDGE,"E2079"),sQuery(id+"F1.wireOp",EDGE,"E2080"),sQuery(id+"F1.wireOp",EDGE,"E2081"),sQuery(id+"F1.wireOp",EDGE,"E2082"),sQuery(id+"F1.wireOp",EDGE,"E2083"),sQuery(id+"F1.wireOp",EDGE,"E2084"),sQuery(id+"F1.wireOp",EDGE,"E2085"),sQuery(id+"F1.wireOp",EDGE,"E2086"),sQuery(id+"F1.wireOp",EDGE,"E2087"),sQuery(id+"F1.wireOp",EDGE,"E2088"),sQuery(id+"F1.wireOp",EDGE,"E2089"),sQuery(id+"F1.wireOp",EDGE,"E2090"),sQuery(id+"F1.wireOp",EDGE,"E2091"),sQuery(id+"F1.wireOp",EDGE,"E2092"),sQuery(id+"F1.wireOp",EDGE,"E2093"),sQuery(id+"F1.wireOp",EDGE,"E2094"),sQuery(id+"F1.wireOp",EDGE,"E2095"),sQuery(id+"F1.wireOp",EDGE,"E2096"),sQuery(id+"F1.wireOp",EDGE,"E2097"),sQuery(id+"F1.wireOp",EDGE,"E2098"),sQuery(id+"F1.wireOp",EDGE,"E2099"),sQuery(id+"F1.wireOp",EDGE,"E2100"),sQuery(id+"F1.wireOp",EDGE,"E2101"),sQuery(id+"F1.wireOp",EDGE,"E2102"),sQuery(id+"F1.wireOp",EDGE,"E2103"),sQuery(id+"F1.wireOp",EDGE,"E2104"),sQuery(id+"F1.wireOp",EDGE,"E2105"),sQuery(id+"F1.wireOp",EDGE,"E2106"),sQuery(id+"F1.wireOp",EDGE,"E2107"),sQuery(id+"F1.wireOp",EDGE,"E2108"),sQuery(id+"F1.wireOp",EDGE,"E2109"),sQuery(id+"F1.wireOp",EDGE,"E2110"),sQuery(id+"F1.wireOp",EDGE,"E2111"),sQuery(id+"F1.wireOp",EDGE,"E2112"),sQuery(id+"F1.wireOp",EDGE,"E2113"),sQuery(id+"F1.wireOp",EDGE,"E2114"),sQuery(id+"F1.wireOp",EDGE,"E2115"),sQuery(id+"F1.wireOp",EDGE,"E2116"),sQuery(id+"F1.wireOp",EDGE,"E2117"),sQuery(id+"F1.wireOp",EDGE,"E2118"),sQuery(id+"F1.wireOp",EDGE,"E2119"),sQuery(id+"F1.wireOp",EDGE,"E2120"),sQuery(id+"F1.wireOp",EDGE,"E2121"),sQuery(id+"F1.wireOp",EDGE,"E2122"),sQuery(id+"F1.wireOp",EDGE,"E2123"),sQuery(id+"F1.wireOp",EDGE,"E2124"),sQuery(id+"F1.wireOp",EDGE,"E2125"),sQuery(id+"F1.wireOp",EDGE,"E2126"),sQuery(id+"F1.wireOp",EDGE,"E2127"),sQuery(id+"F1.wireOp",EDGE,"E2128"),sQuery(id+"F1.wireOp",EDGE,"E2129"),sQuery(id+"F1.wireOp",EDGE,"E2130"),sQuery(id+"F1.wireOp",EDGE,"E2131"),sQuery(id+"F1.wireOp",EDGE,"E2132"),sQuery(id+"F1.wireOp",EDGE,"E2133"),sQuery(id+"F1.wireOp",EDGE,"E2134"),sQuery(id+"F1.wireOp",EDGE,"E2135"),sQuery(id+"F1.wireOp",EDGE,"E2136"),sQuery(id+"F1.wireOp",EDGE,"E2137"),sQuery(id+"F1.wireOp",EDGE,"E2138"),sQuery(id+"F1.wireOp",EDGE,"E2139"),sQuery(id+"F1.wireOp",EDGE,"E2140"),sQuery(id+"F1.wireOp",EDGE,"E2141"),sQuery(id+"F1.wireOp",EDGE,"E2142"),sQuery(id+"F1.wireOp",EDGE,"E2143"),sQuery(id+"F1.wireOp",EDGE,"E2144"),sQuery(id+"F1.wireOp",EDGE,"E2145"),sQuery(id+"F1.wireOp",EDGE,"E2146"),sQuery(id+"F1.wireOp",EDGE,"E2147"),sQuery(id+"F1.wireOp",EDGE,"E2148"),sQuery(id+"F1.wireOp",EDGE,"E2149"),sQuery(id+"F1.wireOp",EDGE,"E2150"),sQuery(id+"F1.wireOp",EDGE,"E2151"),sQuery(id+"F1.wireOp",EDGE,"E2152"),sQuery(id+"F1.wireOp",EDGE,"E2153"),sQuery(id+"F1.wireOp",EDGE,"E2154"),sQuery(id+"F1.wireOp",EDGE,"E2155"),sQuery(id+"F1.wireOp",EDGE,"E2156"),sQuery(id+"F1.wireOp",EDGE,"E2157"),sQuery(id+"F1.wireOp",EDGE,"E2158"),sQuery(id+"F1.wireOp",EDGE,"E2159"),sQuery(id+"F1.wireOp",EDGE,"E2160"),sQuery(id+"F1.wireOp",EDGE,"E2161"),sQuery(id+"F1.wireOp",EDGE,"E2162"),sQuery(id+"F1.wireOp",EDGE,"E2163"),sQuery(id+"F1.wireOp",EDGE,"E2164"),sQuery(id+"F1.wireOp",EDGE,"E2165"),sQuery(id+"F1.wireOp",EDGE,"E2166"),sQuery(id+"F1.wireOp",EDGE,"E2167"),sQuery(id+"F1.wireOp",EDGE,"E2168"),sQuery(id+"F1.wireOp",EDGE,"E2169"),sQuery(id+"F1.wireOp",EDGE,"E2170"),sQuery(id+"F1.wireOp",EDGE,"E2171"),sQuery(id+"F1.wireOp",EDGE,"E2172"),sQuery(id+"F1.wireOp",EDGE,"E2173"),sQuery(id+"F1.wireOp",EDGE,"E2174"),sQuery(id+"F1.wireOp",EDGE,"E2175"),sQuery(id+"F1.wireOp",EDGE,"E2176"),sQuery(id+"F1.wireOp",EDGE,"E2177"),sQuery(id+"F1.wireOp",EDGE,"E2178"),sQuery(id+"F1.wireOp",EDGE,"E2179"),sQuery(id+"F1.wireOp",EDGE,"E2180"),sQuery(id+"F1.wireOp",EDGE,"E2181"),sQuery(id+"F1.wireOp",EDGE,"E2182"),sQuery(id+"F1.wireOp",EDGE,"E2183"),sQuery(id+"F1.wireOp",EDGE,"E2184"),sQuery(id+"F1.wireOp",EDGE,"E2185"),sQuery(id+"F1.wireOp",EDGE,"E2186"),sQuery(id+"F1.wireOp",EDGE,"E2187"),sQuery(id+"F1.wireOp",EDGE,"E2188"),sQuery(id+"F1.wireOp",EDGE,"E2189"),sQuery(id+"F1.wireOp",EDGE,"E2190"),sQuery(id+"F1.wireOp",EDGE,"E2191"),sQuery(id+"F1.wireOp",EDGE,"E2192"),sQuery(id+"F1.wireOp",EDGE,"E2193"),sQuery(id+"F1.wireOp",EDGE,"E2194"),sQuery(id+"F1.wireOp",EDGE,"E2195"),sQuery(id+"F1.wireOp",EDGE,"E2196"),sQuery(id+"F1.wireOp",EDGE,"E2197"),sQuery(id+"F1.wireOp",EDGE,"E2198"),sQuery(id+"F1.wireOp",EDGE,"E2199"),sQuery(id+"F1.wireOp",EDGE,"E2200"),sQuery(id+"F1.wireOp",EDGE,"E2201"),sQuery(id+"F1.wireOp",EDGE,"E2202"),sQuery(id+"F1.wireOp",EDGE,"E2203"),sQuery(id+"F1.wireOp",EDGE,"E2204"),sQuery(id+"F1.wireOp",EDGE,"E2205"),sQuery(id+"F1.wireOp",EDGE,"E2206"),sQuery(id+"F1.wireOp",EDGE,"E2207"),sQuery(id+"F1.wireOp",EDGE,"E2208"),sQuery(id+"F1.wireOp",EDGE,"E2209"),sQuery(id+"F1.wireOp",EDGE,"E2210"),sQuery(id+"F1.wireOp",EDGE,"E2211"),sQuery(id+"F1.wireOp",EDGE,"E2212"),sQuery(id+"F1.wireOp",EDGE,"E2213"),sQuery(id+"F1.wireOp",EDGE,"E2214"),sQuery(id+"F1.wireOp",EDGE,"E2215"),sQuery(id+"F1.wireOp",EDGE,"E2216"),sQuery(id+"F1.wireOp",EDGE,"E2217"),sQuery(id+"F1.wireOp",EDGE,"E2218"),sQuery(id+"F1.wireOp",EDGE,"E2219"),sQuery(id+"F1.wireOp",EDGE,"E2220"),sQuery(id+"F1.wireOp",EDGE,"E2221"),sQuery(id+"F1.wireOp",EDGE,"E2222"),sQuery(id+"F1.wireOp",EDGE,"E2223"),sQuery(id+"F1.wireOp",EDGE,"E2224"),sQuery(id+"F1.wireOp",EDGE,"E2225"),sQuery(id+"F1.wireOp",EDGE,"E2226"),sQuery(id+"F1.wireOp",EDGE,"E2227"),sQuery(id+"F1.wireOp",EDGE,"E2228"),sQuery(id+"F1.wireOp",EDGE,"E2229"),sQuery(id+"F1.wireOp",EDGE,"E2230"),sQuery(id+"F1.wireOp",EDGE,"E2231"),sQuery(id+"F1.wireOp",EDGE,"E2232"),sQuery(id+"F1.wireOp",EDGE,"E2233"),sQuery(id+"F1.wireOp",EDGE,"E2234"),sQuery(id+"F1.wireOp",EDGE,"E2235"),sQuery(id+"F1.wireOp",EDGE,"E2236"),sQuery(id+"F1.wireOp",EDGE,"E2237"),sQuery(id+"F1.wireOp",EDGE,"E2238"),sQuery(id+"F1.wireOp",EDGE,"E2239"),sQuery(id+"F1.wireOp",EDGE,"E2240"),sQuery(id+"F1.wireOp",EDGE,"E2241"),sQuery(id+"F1.wireOp",EDGE,"E2242"),sQuery(id+"F1.wireOp",EDGE,"E2243"),sQuery(id+"F1.wireOp",EDGE,"E2244"),sQuery(id+"F1.wireOp",EDGE,"E2245"),sQuery(id+"F1.wireOp",EDGE,"E2246"),sQuery(id+"F1.wireOp",EDGE,"E2247")])],"isStart":false}),makeQuery(id+"F4.opExtrude","CAP_FACE",FACE,{"disambiguationData":[OSD([sQuery(id+"F3.wireOp",EDGE,"E2248.bottom"),sQuery(id+"F3.wireOp",EDGE,"E2248.top"),sQuery(id+"F3.wireOp",EDGE,"E2248.left"),sQuery(id+"F3.wireOp",EDGE,"E2248.right"),sQuery(id+"F3.wireOp",EDGE,"E2249.bottom"),sQuery(id+"F3.wireOp",EDGE,"E2249.top"),sQuery(id+"F3.wireOp",EDGE,"E2249.left"),sQuery(id+"F3.wireOp",EDGE,"E2249.right")])],"isStart":true})]});
            var sketch = newSketch(context, id + "F13", { "sketchPlane" : qUnion([Q0])});
            skLineSegment(sketch, "E2260.bottom", {"start": v(-150, 55) * mm, "end": v(150, 55) * mm, "construction": true});
            skLineSegment(sketch, "E2260.top", {"start": v(-150, -55) * mm, "end": v(150, -55) * mm, "construction": true});
            skLineSegment(sketch, "E2260.left", {"start": v(-150, 55) * mm, "end": v(-150, -55) * mm, "construction": true});
            skLineSegment(sketch, "E2260.right", {"start": v(150, 55) * mm, "end": v(150, -55) * mm, "construction": true});
            skCircle(sketch, "E2261", {"center": v(-150, 55) * mm, "radius": 1.65 * mm});
            skCircle(sketch, "E2262", {"center": v(-150, -55) * mm, "radius": 1.65 * mm});
            skCircle(sketch, "E2263", {"center": v(150, -55) * mm, "radius": 1.65 * mm});
            skCircle(sketch, "E2264", {"center": v(150, 55) * mm, "radius": 1.65 * mm});
            skCircle(sketch, "E2265", {"center": v(10, 55) * mm, "radius": 1.65 * mm});
            skCircle(sketch, "E2266", {"center": v(-150, 0) * mm, "radius": 1.65 * mm});
            skCircle(sketch, "E2267", {"center": v(150, 0) * mm, "radius": 1.65 * mm});
            skLineSegment(sketch, "E2268", {"start": v(0, 55) * mm, "end": v(0, -55) * mm, "construction": true});
            skCircle(sketch, "E2269.MirrorC", {"center": v(-10, 55) * mm, "radius": 1.65 * mm});
            skSolve(sketch);
        }
        {
            var Q0;
            Q0 = qSketchRegion(id + "F13", true);
            extrude(context, id + "F14", {"entities" : qUnion([Q0]), "operationType" : NewBodyOperationType.REMOVE, "endBound" : BoundingType.THROUGH_ALL, "oppositeDirection" : true, "depth" : 25 * mm});
        }
    });
